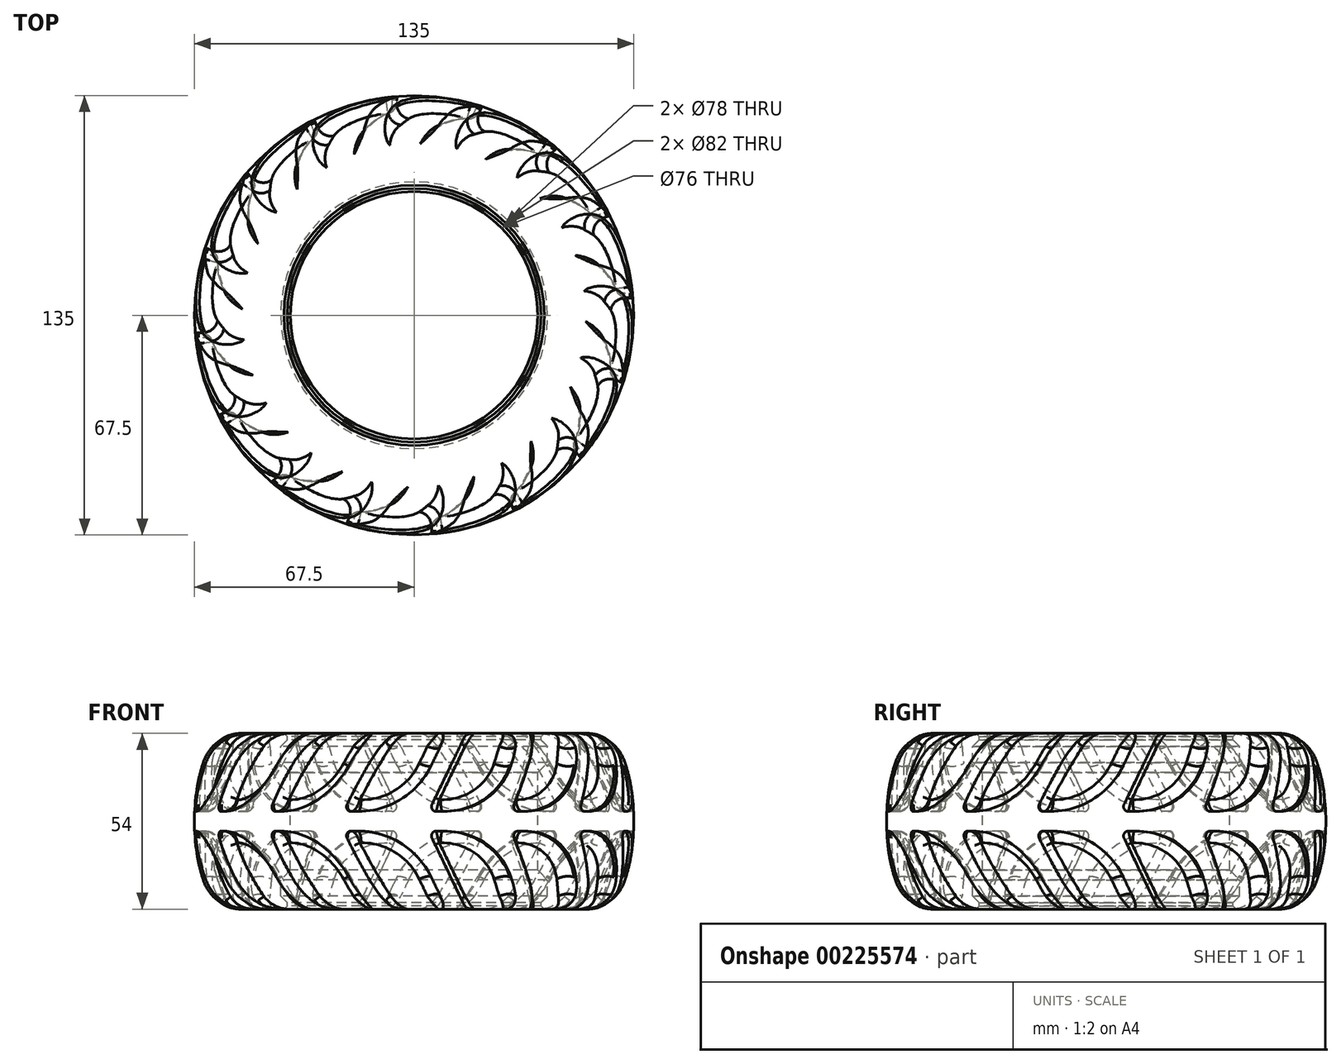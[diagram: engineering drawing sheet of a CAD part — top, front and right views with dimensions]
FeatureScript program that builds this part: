
annotation { "Feature Type Name" : "Feature", "Feature Type Description" : "" }
export const myFeature = defineFeature(function(context is Context, id is Id, definition is map)
    precondition{}
    {
        {
            var Q0;
            Q0=qCreatedBy(makeId("Front.planeOp"),FACE);
            var sketch = newSketch(context, id + "F0", { "sketchPlane" : qUnion([Q0])});
            skLineSegment(sketch, "E0", {"start": v(-39, 25) * mm, "end": v(-39, 27) * mm});
            skLineSegment(sketch, "E1", {"start": v(-39, 25) * mm, "end": v(-41, 23) * mm});
            skLineSegment(sketch, "E2", {"start": v(-41, 23) * mm, "end": v(-41, 18) * mm});
            skLineSegment(sketch, "E3", {"start": v(-41, 18) * mm, "end": v(-38, 15) * mm});
            skLineSegment(sketch, "E4", {"start": v(-38, -15) * mm, "end": v(-41, -18) * mm});
            skLineSegment(sketch, "E5", {"start": v(-41, -18) * mm, "end": v(-41, -23) * mm});
            skLineSegment(sketch, "E6", {"start": v(-41, -23) * mm, "end": v(-39, -25) * mm});
            skLineSegment(sketch, "E7", {"start": v(-39, -25) * mm, "end": v(-39, -27) * mm});
            skLineSegment(sketch, "E8", {"start": v(-38, 15) * mm, "end": v(-38, -15) * mm});
            skLineSegment(sketch, "E9", {"start": v(-38, 0) * mm, "end": v(-62.9, 0) * mm, "construction": true});
            skCircle(sketch, "E10", {"center": v(-52.82, 20.75) * mm, "radius": 6.25 * mm});
            skCircle(sketch, "E11", {"center": v(0, 0) * mm, "radius": 69 * mm});
            skCircle(sketch, "E12", {"center": v(-52.82, -20.75) * mm, "radius": 6.25 * mm});
            skCircle(sketch, "E13", {"center": v(0, 0) * mm, "radius": 63 * mm});
            skLineSegment(sketch, "E14", {"start": v(-39, 27) * mm, "end": v(-52.82, 27) * mm});
            skLineSegment(sketch, "E15", {"start": v(-39, -27) * mm, "end": v(-52.82, -27) * mm});
            skLineSegment(sketch, "E16", {"start": v(0, 89.19) * mm, "end": v(0, -93.9) * mm, "construction": true});
            skCircle(sketch, "E17", {"center": v(-52.82, 20.75) * mm, "radius": 12.25 * mm});
            skSolve(sketch);
        }
        {
            var Q0;
            Q0=makeQuery(id+"F0.imprint","IMPRINT",FACE,{"disambiguationData":[TD([[makeQuery(id+"F0.imprint","IMPRINT",EDGE,{"derivedFrom":sQuery(id+"F0.wireOp",EDGE,"E0")}),1.0]])]});
            var Q1;
            {var subQ0=sQuery(id+"F0.wireOp",EDGE,"E10");var subQ1=makeQuery(id+"F0.imprint","INTERSECT",VERTEX,{"derivedFrom":[subQ0,sQuery(id+"F0.wireOp",EDGE,"E14")]});Q1=makeQuery(id+"F0.imprint","IMPRINT",FACE,{"disambiguationData":[TD([[makeQuery(id+"F0.imprint","IMPRINT",EDGE,{"disambiguationData":[TD([[subQ1,-1.0]])],"derivedFrom":subQ0}),1.0]])]});}
            var Q2;
            {var subQ0=sQuery(id+"F0.wireOp",EDGE,"E12");var subQ1=makeQuery(id+"F0.imprint","INTERSECT",VERTEX,{"derivedFrom":[subQ0,sQuery(id+"F0.wireOp",EDGE,"E15")]});Q2=makeQuery(id+"F0.imprint","IMPRINT",FACE,{"disambiguationData":[TD([[makeQuery(id+"F0.imprint","IMPRINT",EDGE,{"disambiguationData":[TD([[subQ1,1.0]])],"derivedFrom":subQ0}),1.0]])]});}
            var Q3;
            {var subQ6=sQuery(id+"F0.wireOp",EDGE,"E2");Q3=makeQuery(id+"F0.imprint","IMPRINT",FACE,{"disambiguationData":[TD([[makeQuery(id+"F0.imprint","IMPRINT",EDGE,{"derivedFrom":subQ6}),-1.0]])]});}
            var Q4;
            Q4=makeQuery(id+"F0.imprint","IMPRINT",FACE,{"disambiguationData":[TD([[makeQuery(id+"F0.imprint","IMPRINT",EDGE,{"derivedFrom":sQuery(id+"F0.wireOp",EDGE,"E4")}),-1.0]])]});
            var Q5;
            Q5=sQuery(id+"F0.wireOp",EDGE,"E16");
            revolve(context, id + "F1", {"entities" : qUnion([Q0, Q1, Q2, Q3, Q4]), "axis" : qUnion([Q5]), "revolveType" : RevolveType.FULL});
        }
        {
            var Q0;
            Q0=qCreatedBy(makeId("Top.planeOp"),FACE);
            cPlane(context, id + "F2", {"entities" : qUnion([Q0]), "cplaneType" : CPlaneType.OFFSET, "offset" : 27 * mm, "width" : 150 * mm, "height" : 150 * mm});
        }
        {
            var Q0;
            Q0=qCreatedBy(makeId("Top.planeOp"),FACE);
            var sketch = newSketch(context, id + "F3", { "sketchPlane" : qUnion([Q0])});
            skLineSegment(sketch, "E18.bottom", {"start": v(-3, 60) * mm, "end": v(3, 60) * mm});
            skLineSegment(sketch, "E18.top", {"start": v(-3, 70) * mm, "end": v(3, 70) * mm});
            skLineSegment(sketch, "E18.left", {"start": v(-3, 60) * mm, "end": v(-3, 70) * mm});
            skLineSegment(sketch, "E18.right", {"start": v(3, 60) * mm, "end": v(3, 70) * mm});
            skLineSegment(sketch, "E19", {"start": v(0, 113.7) * mm, "end": v(0, -99.56) * mm, "construction": true});
            skLineSegment(sketch, "E20.1.0", {"start": v(-25.73, 54.28) * mm, "end": v(-29.56, 63.52) * mm});
            skLineSegment(sketch, "E20.1.1", {"start": v(-29.56, 63.52) * mm, "end": v(-24.02, 65.82) * mm});
            skLineSegment(sketch, "E20.1.2", {"start": v(-20.19, 56.58) * mm, "end": v(-24.02, 65.82) * mm});
            skLineSegment(sketch, "E20.1.3", {"start": v(-25.73, 54.28) * mm, "end": v(-20.19, 56.58) * mm});
            skLineSegment(sketch, "E20.2.0", {"start": v(-44.55, 40.3) * mm, "end": v(-51.62, 47.38) * mm});
            skLineSegment(sketch, "E20.2.1", {"start": v(-51.62, 47.38) * mm, "end": v(-47.38, 51.62) * mm});
            skLineSegment(sketch, "E20.2.2", {"start": v(-40.3, 44.55) * mm, "end": v(-47.38, 51.62) * mm});
            skLineSegment(sketch, "E20.2.3", {"start": v(-44.55, 40.3) * mm, "end": v(-40.3, 44.55) * mm});
            skLineSegment(sketch, "E20.3.0", {"start": v(-56.58, 20.19) * mm, "end": v(-65.82, 24.02) * mm});
            skLineSegment(sketch, "E20.3.1", {"start": v(-65.82, 24.02) * mm, "end": v(-63.52, 29.56) * mm});
            skLineSegment(sketch, "E20.3.2", {"start": v(-54.28, 25.73) * mm, "end": v(-63.52, 29.56) * mm});
            skLineSegment(sketch, "E20.3.3", {"start": v(-56.58, 20.19) * mm, "end": v(-54.28, 25.73) * mm});
            skLineSegment(sketch, "E20.4.0", {"start": v(-60, -3) * mm, "end": v(-70, -3) * mm});
            skLineSegment(sketch, "E20.4.1", {"start": v(-70, -3) * mm, "end": v(-70, 3) * mm});
            skLineSegment(sketch, "E20.4.2", {"start": v(-60, 3) * mm, "end": v(-70, 3) * mm});
            skLineSegment(sketch, "E20.4.3", {"start": v(-60, -3) * mm, "end": v(-60, 3) * mm});
            skLineSegment(sketch, "E20.5.0", {"start": v(-54.28, -25.73) * mm, "end": v(-63.52, -29.56) * mm});
            skLineSegment(sketch, "E20.5.1", {"start": v(-63.52, -29.56) * mm, "end": v(-65.82, -24.02) * mm});
            skLineSegment(sketch, "E20.5.2", {"start": v(-56.58, -20.19) * mm, "end": v(-65.82, -24.02) * mm});
            skLineSegment(sketch, "E20.5.3", {"start": v(-54.28, -25.73) * mm, "end": v(-56.58, -20.19) * mm});
            skLineSegment(sketch, "E20.6.0", {"start": v(-40.3, -44.55) * mm, "end": v(-47.38, -51.62) * mm});
            skLineSegment(sketch, "E20.6.1", {"start": v(-47.38, -51.62) * mm, "end": v(-51.62, -47.38) * mm});
            skLineSegment(sketch, "E20.6.2", {"start": v(-44.55, -40.3) * mm, "end": v(-51.62, -47.38) * mm});
            skLineSegment(sketch, "E20.6.3", {"start": v(-40.3, -44.55) * mm, "end": v(-44.55, -40.3) * mm});
            skLineSegment(sketch, "E20.7.0", {"start": v(-20.19, -56.58) * mm, "end": v(-24.02, -65.82) * mm});
            skLineSegment(sketch, "E20.7.1", {"start": v(-24.02, -65.82) * mm, "end": v(-29.56, -63.52) * mm});
            skLineSegment(sketch, "E20.7.2", {"start": v(-25.73, -54.28) * mm, "end": v(-29.56, -63.52) * mm});
            skLineSegment(sketch, "E20.7.3", {"start": v(-20.19, -56.58) * mm, "end": v(-25.73, -54.28) * mm});
            skLineSegment(sketch, "E20.8.0", {"start": v(3, -60) * mm, "end": v(3, -70) * mm});
            skLineSegment(sketch, "E20.8.1", {"start": v(3, -70) * mm, "end": v(-3, -70) * mm});
            skLineSegment(sketch, "E20.8.2", {"start": v(-3, -60) * mm, "end": v(-3, -70) * mm});
            skLineSegment(sketch, "E20.8.3", {"start": v(3, -60) * mm, "end": v(-3, -60) * mm});
            skLineSegment(sketch, "E20.9.0", {"start": v(25.73, -54.28) * mm, "end": v(29.56, -63.52) * mm});
            skLineSegment(sketch, "E20.9.1", {"start": v(29.56, -63.52) * mm, "end": v(24.02, -65.82) * mm});
            skLineSegment(sketch, "E20.9.2", {"start": v(20.19, -56.58) * mm, "end": v(24.02, -65.82) * mm});
            skLineSegment(sketch, "E20.9.3", {"start": v(25.73, -54.28) * mm, "end": v(20.19, -56.58) * mm});
            skLineSegment(sketch, "E20.10.0", {"start": v(44.55, -40.3) * mm, "end": v(51.62, -47.38) * mm});
            skLineSegment(sketch, "E20.10.1", {"start": v(51.62, -47.38) * mm, "end": v(47.38, -51.62) * mm});
            skLineSegment(sketch, "E20.10.2", {"start": v(40.3, -44.55) * mm, "end": v(47.38, -51.62) * mm});
            skLineSegment(sketch, "E20.10.3", {"start": v(44.55, -40.3) * mm, "end": v(40.3, -44.55) * mm});
            skLineSegment(sketch, "E20.11.0", {"start": v(56.58, -20.19) * mm, "end": v(65.82, -24.02) * mm});
            skLineSegment(sketch, "E20.11.1", {"start": v(65.82, -24.02) * mm, "end": v(63.52, -29.56) * mm});
            skLineSegment(sketch, "E20.11.2", {"start": v(54.28, -25.73) * mm, "end": v(63.52, -29.56) * mm});
            skLineSegment(sketch, "E20.11.3", {"start": v(56.58, -20.19) * mm, "end": v(54.28, -25.73) * mm});
            skLineSegment(sketch, "E20.12.0", {"start": v(60, 3) * mm, "end": v(70, 3) * mm});
            skLineSegment(sketch, "E20.12.1", {"start": v(70, 3) * mm, "end": v(70, -3) * mm});
            skLineSegment(sketch, "E20.12.2", {"start": v(60, -3) * mm, "end": v(70, -3) * mm});
            skLineSegment(sketch, "E20.12.3", {"start": v(60, 3) * mm, "end": v(60, -3) * mm});
            skLineSegment(sketch, "E20.13.0", {"start": v(54.28, 25.73) * mm, "end": v(63.52, 29.56) * mm});
            skLineSegment(sketch, "E20.13.1", {"start": v(63.52, 29.56) * mm, "end": v(65.82, 24.02) * mm});
            skLineSegment(sketch, "E20.13.2", {"start": v(56.58, 20.19) * mm, "end": v(65.82, 24.02) * mm});
            skLineSegment(sketch, "E20.13.3", {"start": v(54.28, 25.73) * mm, "end": v(56.58, 20.19) * mm});
            skLineSegment(sketch, "E20.14.0", {"start": v(40.3, 44.55) * mm, "end": v(47.38, 51.62) * mm});
            skLineSegment(sketch, "E20.14.1", {"start": v(47.38, 51.62) * mm, "end": v(51.62, 47.38) * mm});
            skLineSegment(sketch, "E20.14.2", {"start": v(44.55, 40.3) * mm, "end": v(51.62, 47.38) * mm});
            skLineSegment(sketch, "E20.14.3", {"start": v(40.3, 44.55) * mm, "end": v(44.55, 40.3) * mm});
            skLineSegment(sketch, "E20.15.0", {"start": v(20.19, 56.58) * mm, "end": v(24.02, 65.82) * mm});
            skLineSegment(sketch, "E20.15.1", {"start": v(24.02, 65.82) * mm, "end": v(29.56, 63.52) * mm});
            skLineSegment(sketch, "E20.15.2", {"start": v(25.73, 54.28) * mm, "end": v(29.56, 63.52) * mm});
            skLineSegment(sketch, "E20.15.3", {"start": v(20.19, 56.58) * mm, "end": v(25.73, 54.28) * mm});
            skPoint(sketch, "E20.center", {"position": v(0, 0) * mm});
            skSolve(sketch);
        }
        {
            var Q0;
            Q0=qCreatedBy(id+"F2.planeOp",FACE);
            var sketch = newSketch(context, id + "F4", { "sketchPlane" : qUnion([Q0])});
            skLineSegment(sketch, "E21", {"start": v(-16, 70) * mm, "end": v(-16, 50) * mm});
            skLineSegment(sketch, "E22", {"start": v(-16, 50) * mm, "end": v(-10, 50) * mm});
            skLineSegment(sketch, "E23", {"start": v(-16, 70) * mm, "end": v(-10, 70) * mm});
            skLineSegment(sketch, "E24", {"start": v(-10, 70) * mm, "end": v(-10, 50) * mm});
            skLineSegment(sketch, "E25", {"start": v(0, 99.7) * mm, "end": v(0, -107.8) * mm, "construction": true});
            skLineSegment(sketch, "E26.1.0", {"start": v(-41.57, 58.55) * mm, "end": v(-33.92, 40.07) * mm});
            skLineSegment(sketch, "E26.1.1", {"start": v(-36.03, 60.84) * mm, "end": v(-28.37, 42.37) * mm});
            skLineSegment(sketch, "E26.1.2", {"start": v(-33.92, 40.07) * mm, "end": v(-28.37, 42.37) * mm});
            skLineSegment(sketch, "E26.1.3", {"start": v(-41.57, 58.55) * mm, "end": v(-36.03, 60.84) * mm});
            skLineSegment(sketch, "E26.2.0", {"start": v(-60.81, 38.18) * mm, "end": v(-46.67, 24.04) * mm});
            skLineSegment(sketch, "E26.2.1", {"start": v(-56.57, 42.43) * mm, "end": v(-42.43, 28.28) * mm});
            skLineSegment(sketch, "E26.2.2", {"start": v(-46.67, 24.04) * mm, "end": v(-42.43, 28.28) * mm});
            skLineSegment(sketch, "E26.2.3", {"start": v(-60.81, 38.18) * mm, "end": v(-56.57, 42.43) * mm});
            skLineSegment(sketch, "E26.3.0", {"start": v(-70.8, 12) * mm, "end": v(-52.32, 4.35) * mm});
            skLineSegment(sketch, "E26.3.1", {"start": v(-68.5, 17.55) * mm, "end": v(-50.02, 9.9) * mm});
            skLineSegment(sketch, "E26.3.2", {"start": v(-52.32, 4.35) * mm, "end": v(-50.02, 9.9) * mm});
            skLineSegment(sketch, "E26.3.3", {"start": v(-70.8, 12) * mm, "end": v(-68.5, 17.55) * mm});
            skLineSegment(sketch, "E26.4.0", {"start": v(-70, -16) * mm, "end": v(-50, -16) * mm});
            skLineSegment(sketch, "E26.4.1", {"start": v(-70, -10) * mm, "end": v(-50, -10) * mm});
            skLineSegment(sketch, "E26.4.2", {"start": v(-50, -16) * mm, "end": v(-50, -10) * mm});
            skLineSegment(sketch, "E26.4.3", {"start": v(-70, -16) * mm, "end": v(-70, -10) * mm});
            skLineSegment(sketch, "E26.5.0", {"start": v(-58.55, -41.57) * mm, "end": v(-40.07, -33.92) * mm});
            skLineSegment(sketch, "E26.5.1", {"start": v(-60.84, -36.03) * mm, "end": v(-42.37, -28.37) * mm});
            skLineSegment(sketch, "E26.5.2", {"start": v(-40.07, -33.92) * mm, "end": v(-42.37, -28.37) * mm});
            skLineSegment(sketch, "E26.5.3", {"start": v(-58.55, -41.57) * mm, "end": v(-60.84, -36.03) * mm});
            skLineSegment(sketch, "E26.6.0", {"start": v(-38.18, -60.81) * mm, "end": v(-24.04, -46.67) * mm});
            skLineSegment(sketch, "E26.6.1", {"start": v(-42.43, -56.57) * mm, "end": v(-28.28, -42.43) * mm});
            skLineSegment(sketch, "E26.6.2", {"start": v(-24.04, -46.67) * mm, "end": v(-28.28, -42.43) * mm});
            skLineSegment(sketch, "E26.6.3", {"start": v(-38.18, -60.81) * mm, "end": v(-42.43, -56.57) * mm});
            skLineSegment(sketch, "E26.7.0", {"start": v(-12, -70.8) * mm, "end": v(-4.35, -52.32) * mm});
            skLineSegment(sketch, "E26.7.1", {"start": v(-17.55, -68.5) * mm, "end": v(-9.9, -50.02) * mm});
            skLineSegment(sketch, "E26.7.2", {"start": v(-4.35, -52.32) * mm, "end": v(-9.9, -50.02) * mm});
            skLineSegment(sketch, "E26.7.3", {"start": v(-12, -70.8) * mm, "end": v(-17.55, -68.5) * mm});
            skLineSegment(sketch, "E26.8.0", {"start": v(16, -70) * mm, "end": v(16, -50) * mm});
            skLineSegment(sketch, "E26.8.1", {"start": v(10, -70) * mm, "end": v(10, -50) * mm});
            skLineSegment(sketch, "E26.8.2", {"start": v(16, -50) * mm, "end": v(10, -50) * mm});
            skLineSegment(sketch, "E26.8.3", {"start": v(16, -70) * mm, "end": v(10, -70) * mm});
            skLineSegment(sketch, "E26.9.0", {"start": v(41.57, -58.55) * mm, "end": v(33.92, -40.07) * mm});
            skLineSegment(sketch, "E26.9.1", {"start": v(36.03, -60.84) * mm, "end": v(28.37, -42.37) * mm});
            skLineSegment(sketch, "E26.9.2", {"start": v(33.92, -40.07) * mm, "end": v(28.37, -42.37) * mm});
            skLineSegment(sketch, "E26.9.3", {"start": v(41.57, -58.55) * mm, "end": v(36.03, -60.84) * mm});
            skLineSegment(sketch, "E26.10.0", {"start": v(60.81, -38.18) * mm, "end": v(46.67, -24.04) * mm});
            skLineSegment(sketch, "E26.10.1", {"start": v(56.57, -42.43) * mm, "end": v(42.43, -28.28) * mm});
            skLineSegment(sketch, "E26.10.2", {"start": v(46.67, -24.04) * mm, "end": v(42.43, -28.28) * mm});
            skLineSegment(sketch, "E26.10.3", {"start": v(60.81, -38.18) * mm, "end": v(56.57, -42.43) * mm});
            skLineSegment(sketch, "E26.11.0", {"start": v(70.8, -12) * mm, "end": v(52.32, -4.35) * mm});
            skLineSegment(sketch, "E26.11.1", {"start": v(68.5, -17.55) * mm, "end": v(50.02, -9.9) * mm});
            skLineSegment(sketch, "E26.11.2", {"start": v(52.32, -4.35) * mm, "end": v(50.02, -9.9) * mm});
            skLineSegment(sketch, "E26.11.3", {"start": v(70.8, -12) * mm, "end": v(68.5, -17.55) * mm});
            skLineSegment(sketch, "E26.12.0", {"start": v(70, 16) * mm, "end": v(50, 16) * mm});
            skLineSegment(sketch, "E26.12.1", {"start": v(70, 10) * mm, "end": v(50, 10) * mm});
            skLineSegment(sketch, "E26.12.2", {"start": v(50, 16) * mm, "end": v(50, 10) * mm});
            skLineSegment(sketch, "E26.12.3", {"start": v(70, 16) * mm, "end": v(70, 10) * mm});
            skLineSegment(sketch, "E26.13.0", {"start": v(58.55, 41.57) * mm, "end": v(40.07, 33.92) * mm});
            skLineSegment(sketch, "E26.13.1", {"start": v(60.84, 36.03) * mm, "end": v(42.37, 28.37) * mm});
            skLineSegment(sketch, "E26.13.2", {"start": v(40.07, 33.92) * mm, "end": v(42.37, 28.37) * mm});
            skLineSegment(sketch, "E26.13.3", {"start": v(58.55, 41.57) * mm, "end": v(60.84, 36.03) * mm});
            skLineSegment(sketch, "E26.14.0", {"start": v(38.18, 60.81) * mm, "end": v(24.04, 46.67) * mm});
            skLineSegment(sketch, "E26.14.1", {"start": v(42.43, 56.57) * mm, "end": v(28.28, 42.43) * mm});
            skLineSegment(sketch, "E26.14.2", {"start": v(24.04, 46.67) * mm, "end": v(28.28, 42.43) * mm});
            skLineSegment(sketch, "E26.14.3", {"start": v(38.18, 60.81) * mm, "end": v(42.43, 56.57) * mm});
            skLineSegment(sketch, "E26.15.0", {"start": v(12, 70.8) * mm, "end": v(4.35, 52.32) * mm});
            skLineSegment(sketch, "E26.15.1", {"start": v(17.55, 68.5) * mm, "end": v(9.9, 50.02) * mm});
            skLineSegment(sketch, "E26.15.2", {"start": v(4.35, 52.32) * mm, "end": v(9.9, 50.02) * mm});
            skLineSegment(sketch, "E26.15.3", {"start": v(12, 70.8) * mm, "end": v(17.55, 68.5) * mm});
            skPoint(sketch, "E26.center", {"position": v(0, 0) * mm});
            skSolve(sketch);
        }
        {
            var Q1;
            Q1=makeQuery(id+"F3.imprint","IMPRINT",FACE,{"disambiguationData":[TD([[makeQuery(id+"F3.imprint","IMPRINT",EDGE,{"derivedFrom":sQuery(id+"F3.wireOp",EDGE,"E18.bottom")}),1.0]])]});
            var Q2;
            Q2=makeQuery(id+"F4.imprint","IMPRINT",FACE,{"disambiguationData":[TD([[makeQuery(id+"F4.imprint","IMPRINT",EDGE,{"derivedFrom":sQuery(id+"F4.wireOp",EDGE,"E21")}),1.0]])]});
            loft(context, id + "F5", {"operationType" : NewBodyOperationType.ADD, "sheetProfilesArray" : [{ "sheetProfileEntities" : qUnion([Q1]) }, { "sheetProfileEntities" : qUnion([Q2]) }]});
        }
        {
            var Q1;
            Q1=makeQuery(id+"F3.imprint","IMPRINT",FACE,{"disambiguationData":[TD([[makeQuery(id+"F3.imprint","IMPRINT",EDGE,{"derivedFrom":sQuery(id+"F3.wireOp",EDGE,"E20.15.0")}),-1.0]])]});
            var Q2;
            Q2=makeQuery(id+"F4.imprint","IMPRINT",FACE,{"disambiguationData":[TD([[makeQuery(id+"F4.imprint","IMPRINT",EDGE,{"derivedFrom":sQuery(id+"F4.wireOp",EDGE,"E26.15.0")}),1.0]])]});
            loft(context, id + "F6", {"operationType" : NewBodyOperationType.ADD, "sheetProfilesArray" : [{ "sheetProfileEntities" : qUnion([Q1]) }, { "sheetProfileEntities" : qUnion([Q2]) }]});
        }
        {
            var Q1;
            Q1=makeQuery(id+"F3.imprint","IMPRINT",FACE,{"disambiguationData":[TD([[makeQuery(id+"F3.imprint","IMPRINT",EDGE,{"derivedFrom":sQuery(id+"F3.wireOp",EDGE,"E20.14.0")}),-1.0]])]});
            var Q2;
            Q2=makeQuery(id+"F4.imprint","IMPRINT",FACE,{"disambiguationData":[TD([[makeQuery(id+"F4.imprint","IMPRINT",EDGE,{"derivedFrom":sQuery(id+"F4.wireOp",EDGE,"E26.14.0")}),1.0]])]});
            loft(context, id + "F7", {"operationType" : NewBodyOperationType.ADD, "sheetProfilesArray" : [{ "sheetProfileEntities" : qUnion([Q1]) }, { "sheetProfileEntities" : qUnion([Q2]) }]});
        }
        {
            var Q1;
            Q1=makeQuery(id+"F3.imprint","IMPRINT",FACE,{"disambiguationData":[TD([[makeQuery(id+"F3.imprint","IMPRINT",EDGE,{"derivedFrom":sQuery(id+"F3.wireOp",EDGE,"E20.13.0")}),-1.0]])]});
            var Q2;
            Q2=makeQuery(id+"F4.imprint","IMPRINT",FACE,{"disambiguationData":[TD([[makeQuery(id+"F4.imprint","IMPRINT",EDGE,{"derivedFrom":sQuery(id+"F4.wireOp",EDGE,"E26.13.0")}),1.0]])]});
            loft(context, id + "F8", {"operationType" : NewBodyOperationType.ADD, "sheetProfilesArray" : [{ "sheetProfileEntities" : qUnion([Q1]) }, { "sheetProfileEntities" : qUnion([Q2]) }]});
        }
        {
            var Q1;
            Q1=makeQuery(id+"F3.imprint","IMPRINT",FACE,{"disambiguationData":[TD([[makeQuery(id+"F3.imprint","IMPRINT",EDGE,{"derivedFrom":sQuery(id+"F3.wireOp",EDGE,"E20.12.0")}),-1.0]])]});
            var Q2;
            Q2=makeQuery(id+"F4.imprint","IMPRINT",FACE,{"disambiguationData":[TD([[makeQuery(id+"F4.imprint","IMPRINT",EDGE,{"derivedFrom":sQuery(id+"F4.wireOp",EDGE,"E26.12.0")}),1.0]])]});
            loft(context, id + "F9", {"operationType" : NewBodyOperationType.ADD, "sheetProfilesArray" : [{ "sheetProfileEntities" : qUnion([Q1]) }, { "sheetProfileEntities" : qUnion([Q2]) }]});
        }
        {
            var Q1;
            Q1=makeQuery(id+"F3.imprint","IMPRINT",FACE,{"disambiguationData":[TD([[makeQuery(id+"F3.imprint","IMPRINT",EDGE,{"derivedFrom":sQuery(id+"F3.wireOp",EDGE,"E20.11.0")}),-1.0]])]});
            var Q2;
            Q2=makeQuery(id+"F4.imprint","IMPRINT",FACE,{"disambiguationData":[TD([[makeQuery(id+"F4.imprint","IMPRINT",EDGE,{"derivedFrom":sQuery(id+"F4.wireOp",EDGE,"E26.11.0")}),1.0]])]});
            loft(context, id + "F10", {"operationType" : NewBodyOperationType.ADD, "sheetProfilesArray" : [{ "sheetProfileEntities" : qUnion([Q1]) }, { "sheetProfileEntities" : qUnion([Q2]) }]});
        }
        {
            var Q1;
            Q1=makeQuery(id+"F3.imprint","IMPRINT",FACE,{"disambiguationData":[TD([[makeQuery(id+"F3.imprint","IMPRINT",EDGE,{"derivedFrom":sQuery(id+"F3.wireOp",EDGE,"E20.10.0")}),-1.0]])]});
            var Q2;
            Q2=makeQuery(id+"F4.imprint","IMPRINT",FACE,{"disambiguationData":[TD([[makeQuery(id+"F4.imprint","IMPRINT",EDGE,{"derivedFrom":sQuery(id+"F4.wireOp",EDGE,"E26.10.0")}),1.0]])]});
            loft(context, id + "F11", {"operationType" : NewBodyOperationType.ADD, "sheetProfilesArray" : [{ "sheetProfileEntities" : qUnion([Q1]) }, { "sheetProfileEntities" : qUnion([Q2]) }]});
        }
        {
            var Q1;
            Q1=makeQuery(id+"F3.imprint","IMPRINT",FACE,{"disambiguationData":[TD([[makeQuery(id+"F3.imprint","IMPRINT",EDGE,{"derivedFrom":sQuery(id+"F3.wireOp",EDGE,"E20.9.0")}),-1.0]])]});
            var Q2;
            Q2=makeQuery(id+"F4.imprint","IMPRINT",FACE,{"disambiguationData":[TD([[makeQuery(id+"F4.imprint","IMPRINT",EDGE,{"derivedFrom":sQuery(id+"F4.wireOp",EDGE,"E26.9.0")}),1.0]])]});
            loft(context, id + "F12", {"operationType" : NewBodyOperationType.ADD, "sheetProfilesArray" : [{ "sheetProfileEntities" : qUnion([Q1]) }, { "sheetProfileEntities" : qUnion([Q2]) }]});
        }
        {
            var Q1;
            Q1=makeQuery(id+"F3.imprint","IMPRINT",FACE,{"disambiguationData":[TD([[makeQuery(id+"F3.imprint","IMPRINT",EDGE,{"derivedFrom":sQuery(id+"F3.wireOp",EDGE,"E20.8.0")}),-1.0]])]});
            var Q2;
            Q2=makeQuery(id+"F4.imprint","IMPRINT",FACE,{"disambiguationData":[TD([[makeQuery(id+"F4.imprint","IMPRINT",EDGE,{"derivedFrom":sQuery(id+"F4.wireOp",EDGE,"E26.8.0")}),1.0]])]});
            loft(context, id + "F13", {"operationType" : NewBodyOperationType.ADD, "sheetProfilesArray" : [{ "sheetProfileEntities" : qUnion([Q1]) }, { "sheetProfileEntities" : qUnion([Q2]) }]});
        }
        {
            var Q1;
            Q1=makeQuery(id+"F3.imprint","IMPRINT",FACE,{"disambiguationData":[TD([[makeQuery(id+"F3.imprint","IMPRINT",EDGE,{"derivedFrom":sQuery(id+"F3.wireOp",EDGE,"E20.7.0")}),-1.0]])]});
            var Q2;
            Q2=makeQuery(id+"F4.imprint","IMPRINT",FACE,{"disambiguationData":[TD([[makeQuery(id+"F4.imprint","IMPRINT",EDGE,{"derivedFrom":sQuery(id+"F4.wireOp",EDGE,"E26.7.0")}),1.0]])]});
            loft(context, id + "F14", {"operationType" : NewBodyOperationType.ADD, "sheetProfilesArray" : [{ "sheetProfileEntities" : qUnion([Q1]) }, { "sheetProfileEntities" : qUnion([Q2]) }]});
        }
        {
            var Q1;
            Q1=makeQuery(id+"F3.imprint","IMPRINT",FACE,{"disambiguationData":[TD([[makeQuery(id+"F3.imprint","IMPRINT",EDGE,{"derivedFrom":sQuery(id+"F3.wireOp",EDGE,"E20.6.0")}),-1.0]])]});
            var Q2;
            Q2=makeQuery(id+"F4.imprint","IMPRINT",FACE,{"disambiguationData":[TD([[makeQuery(id+"F4.imprint","IMPRINT",EDGE,{"derivedFrom":sQuery(id+"F4.wireOp",EDGE,"E26.6.0")}),1.0]])]});
            loft(context, id + "F15", {"operationType" : NewBodyOperationType.ADD, "sheetProfilesArray" : [{ "sheetProfileEntities" : qUnion([Q1]) }, { "sheetProfileEntities" : qUnion([Q2]) }]});
        }
        {
            var Q1;
            Q1=makeQuery(id+"F3.imprint","IMPRINT",FACE,{"disambiguationData":[TD([[makeQuery(id+"F3.imprint","IMPRINT",EDGE,{"derivedFrom":sQuery(id+"F3.wireOp",EDGE,"E20.5.0")}),-1.0]])]});
            var Q2;
            Q2=makeQuery(id+"F4.imprint","IMPRINT",FACE,{"disambiguationData":[TD([[makeQuery(id+"F4.imprint","IMPRINT",EDGE,{"derivedFrom":sQuery(id+"F4.wireOp",EDGE,"E26.5.0")}),1.0]])]});
            loft(context, id + "F16", {"operationType" : NewBodyOperationType.ADD, "sheetProfilesArray" : [{ "sheetProfileEntities" : qUnion([Q1]) }, { "sheetProfileEntities" : qUnion([Q2]) }]});
        }
        {
            var Q1;
            Q1=makeQuery(id+"F4.imprint","IMPRINT",FACE,{"disambiguationData":[TD([[makeQuery(id+"F4.imprint","IMPRINT",EDGE,{"derivedFrom":sQuery(id+"F4.wireOp",EDGE,"E26.4.0")}),1.0]])]});
            var Q2;
            Q2=makeQuery(id+"F3.imprint","IMPRINT",FACE,{"disambiguationData":[TD([[makeQuery(id+"F3.imprint","IMPRINT",EDGE,{"derivedFrom":sQuery(id+"F3.wireOp",EDGE,"E20.4.0")}),-1.0]])]});
            loft(context, id + "F17", {"operationType" : NewBodyOperationType.ADD, "sheetProfilesArray" : [{ "sheetProfileEntities" : qUnion([Q1]) }, { "sheetProfileEntities" : qUnion([Q2]) }]});
        }
        {
            var Q1;
            Q1=makeQuery(id+"F3.imprint","IMPRINT",FACE,{"disambiguationData":[TD([[makeQuery(id+"F3.imprint","IMPRINT",EDGE,{"derivedFrom":sQuery(id+"F3.wireOp",EDGE,"E20.3.0")}),-1.0]])]});
            var Q2;
            Q2=makeQuery(id+"F4.imprint","IMPRINT",FACE,{"disambiguationData":[TD([[makeQuery(id+"F4.imprint","IMPRINT",EDGE,{"derivedFrom":sQuery(id+"F4.wireOp",EDGE,"E26.3.0")}),1.0]])]});
            loft(context, id + "F18", {"operationType" : NewBodyOperationType.ADD, "sheetProfilesArray" : [{ "sheetProfileEntities" : qUnion([Q1]) }, { "sheetProfileEntities" : qUnion([Q2]) }]});
        }
        {
            var Q1;
            Q1=makeQuery(id+"F3.imprint","IMPRINT",FACE,{"disambiguationData":[TD([[makeQuery(id+"F3.imprint","IMPRINT",EDGE,{"derivedFrom":sQuery(id+"F3.wireOp",EDGE,"E20.2.0")}),-1.0]])]});
            var Q2;
            Q2=makeQuery(id+"F4.imprint","IMPRINT",FACE,{"disambiguationData":[TD([[makeQuery(id+"F4.imprint","IMPRINT",EDGE,{"derivedFrom":sQuery(id+"F4.wireOp",EDGE,"E26.2.0")}),1.0]])]});
            loft(context, id + "F19", {"operationType" : NewBodyOperationType.ADD, "sheetProfilesArray" : [{ "sheetProfileEntities" : qUnion([Q1]) }, { "sheetProfileEntities" : qUnion([Q2]) }]});
        }
        {
            var Q1;
            Q1=makeQuery(id+"F3.imprint","IMPRINT",FACE,{"disambiguationData":[TD([[makeQuery(id+"F3.imprint","IMPRINT",EDGE,{"derivedFrom":sQuery(id+"F3.wireOp",EDGE,"E20.1.0")}),-1.0]])]});
            var Q2;
            Q2=makeQuery(id+"F4.imprint","IMPRINT",FACE,{"disambiguationData":[TD([[makeQuery(id+"F4.imprint","IMPRINT",EDGE,{"derivedFrom":sQuery(id+"F4.wireOp",EDGE,"E26.1.0")}),1.0]])]});
            loft(context, id + "F20", {"operationType" : NewBodyOperationType.ADD, "sheetProfilesArray" : [{ "sheetProfileEntities" : qUnion([Q1]) }, { "sheetProfileEntities" : qUnion([Q2]) }]});
        }
        {
            var Q0;
            Q0=qCreatedBy(makeId("Top.planeOp"),FACE);
            cPlane(context, id + "F21", {"entities" : qUnion([Q0]), "cplaneType" : CPlaneType.OFFSET, "offset" : 27 * mm, "oppositeDirection" : true, "width" : 150 * mm, "height" : 150 * mm});
        }
        {
            var Q0;
            Q0=qCreatedBy(id+"F21.planeOp",FACE);
            var sketch = newSketch(context, id + "F22", { "sketchPlane" : qUnion([Q0])});
            skLineSegment(sketch, "E27.bottom", {"start": v(10, -70) * mm, "end": v(16, -70) * mm});
            skLineSegment(sketch, "E27.top", {"start": v(10, -50) * mm, "end": v(16, -50) * mm});
            skLineSegment(sketch, "E27.left", {"start": v(10, -70) * mm, "end": v(10, -50) * mm});
            skLineSegment(sketch, "E27.right", {"start": v(16, -70) * mm, "end": v(16, -50) * mm});
            skLineSegment(sketch, "E28.1.0", {"start": v(36.03, -60.84) * mm, "end": v(28.37, -42.37) * mm});
            skLineSegment(sketch, "E28.1.1", {"start": v(41.57, -58.55) * mm, "end": v(33.92, -40.07) * mm});
            skLineSegment(sketch, "E28.1.2", {"start": v(36.03, -60.84) * mm, "end": v(41.57, -58.55) * mm});
            skLineSegment(sketch, "E28.1.3", {"start": v(28.37, -42.37) * mm, "end": v(33.92, -40.07) * mm});
            skLineSegment(sketch, "E28.2.0", {"start": v(56.57, -42.43) * mm, "end": v(42.43, -28.28) * mm});
            skLineSegment(sketch, "E28.2.1", {"start": v(60.81, -38.18) * mm, "end": v(46.67, -24.04) * mm});
            skLineSegment(sketch, "E28.2.2", {"start": v(56.57, -42.43) * mm, "end": v(60.81, -38.18) * mm});
            skLineSegment(sketch, "E28.2.3", {"start": v(42.43, -28.28) * mm, "end": v(46.67, -24.04) * mm});
            skLineSegment(sketch, "E28.3.0", {"start": v(68.5, -17.55) * mm, "end": v(50.02, -9.9) * mm});
            skLineSegment(sketch, "E28.3.1", {"start": v(70.8, -12) * mm, "end": v(52.32, -4.35) * mm});
            skLineSegment(sketch, "E28.3.2", {"start": v(68.5, -17.55) * mm, "end": v(70.8, -12) * mm});
            skLineSegment(sketch, "E28.3.3", {"start": v(50.02, -9.9) * mm, "end": v(52.32, -4.35) * mm});
            skLineSegment(sketch, "E28.4.0", {"start": v(70, 10) * mm, "end": v(50, 10) * mm});
            skLineSegment(sketch, "E28.4.1", {"start": v(70, 16) * mm, "end": v(50, 16) * mm});
            skLineSegment(sketch, "E28.4.2", {"start": v(70, 10) * mm, "end": v(70, 16) * mm});
            skLineSegment(sketch, "E28.4.3", {"start": v(50, 10) * mm, "end": v(50, 16) * mm});
            skLineSegment(sketch, "E28.5.0", {"start": v(60.84, 36.03) * mm, "end": v(42.37, 28.37) * mm});
            skLineSegment(sketch, "E28.5.1", {"start": v(58.55, 41.57) * mm, "end": v(40.07, 33.92) * mm});
            skLineSegment(sketch, "E28.5.2", {"start": v(60.84, 36.03) * mm, "end": v(58.55, 41.57) * mm});
            skLineSegment(sketch, "E28.5.3", {"start": v(42.37, 28.37) * mm, "end": v(40.07, 33.92) * mm});
            skLineSegment(sketch, "E28.6.0", {"start": v(42.43, 56.57) * mm, "end": v(28.28, 42.43) * mm});
            skLineSegment(sketch, "E28.6.1", {"start": v(38.18, 60.81) * mm, "end": v(24.04, 46.67) * mm});
            skLineSegment(sketch, "E28.6.2", {"start": v(42.43, 56.57) * mm, "end": v(38.18, 60.81) * mm});
            skLineSegment(sketch, "E28.6.3", {"start": v(28.28, 42.43) * mm, "end": v(24.04, 46.67) * mm});
            skLineSegment(sketch, "E28.7.0", {"start": v(17.55, 68.5) * mm, "end": v(9.9, 50.02) * mm});
            skLineSegment(sketch, "E28.7.1", {"start": v(12, 70.8) * mm, "end": v(4.35, 52.32) * mm});
            skLineSegment(sketch, "E28.7.2", {"start": v(17.55, 68.5) * mm, "end": v(12, 70.8) * mm});
            skLineSegment(sketch, "E28.7.3", {"start": v(9.9, 50.02) * mm, "end": v(4.35, 52.32) * mm});
            skLineSegment(sketch, "E28.8.0", {"start": v(-10, 70) * mm, "end": v(-10, 50) * mm});
            skLineSegment(sketch, "E28.8.1", {"start": v(-16, 70) * mm, "end": v(-16, 50) * mm});
            skLineSegment(sketch, "E28.8.2", {"start": v(-10, 70) * mm, "end": v(-16, 70) * mm});
            skLineSegment(sketch, "E28.8.3", {"start": v(-10, 50) * mm, "end": v(-16, 50) * mm});
            skLineSegment(sketch, "E28.9.0", {"start": v(-36.03, 60.84) * mm, "end": v(-28.37, 42.37) * mm});
            skLineSegment(sketch, "E28.9.1", {"start": v(-41.57, 58.55) * mm, "end": v(-33.92, 40.07) * mm});
            skLineSegment(sketch, "E28.9.2", {"start": v(-36.03, 60.84) * mm, "end": v(-41.57, 58.55) * mm});
            skLineSegment(sketch, "E28.9.3", {"start": v(-28.37, 42.37) * mm, "end": v(-33.92, 40.07) * mm});
            skLineSegment(sketch, "E28.10.0", {"start": v(-56.57, 42.43) * mm, "end": v(-42.43, 28.28) * mm});
            skLineSegment(sketch, "E28.10.1", {"start": v(-60.81, 38.18) * mm, "end": v(-46.67, 24.04) * mm});
            skLineSegment(sketch, "E28.10.2", {"start": v(-56.57, 42.43) * mm, "end": v(-60.81, 38.18) * mm});
            skLineSegment(sketch, "E28.10.3", {"start": v(-42.43, 28.28) * mm, "end": v(-46.67, 24.04) * mm});
            skLineSegment(sketch, "E28.11.0", {"start": v(-68.5, 17.55) * mm, "end": v(-50.02, 9.9) * mm});
            skLineSegment(sketch, "E28.11.1", {"start": v(-70.8, 12) * mm, "end": v(-52.32, 4.35) * mm});
            skLineSegment(sketch, "E28.11.2", {"start": v(-68.5, 17.55) * mm, "end": v(-70.8, 12) * mm});
            skLineSegment(sketch, "E28.11.3", {"start": v(-50.02, 9.9) * mm, "end": v(-52.32, 4.35) * mm});
            skLineSegment(sketch, "E28.12.0", {"start": v(-70, -10) * mm, "end": v(-50, -10) * mm});
            skLineSegment(sketch, "E28.12.1", {"start": v(-70, -16) * mm, "end": v(-50, -16) * mm});
            skLineSegment(sketch, "E28.12.2", {"start": v(-70, -10) * mm, "end": v(-70, -16) * mm});
            skLineSegment(sketch, "E28.12.3", {"start": v(-50, -10) * mm, "end": v(-50, -16) * mm});
            skLineSegment(sketch, "E28.13.0", {"start": v(-60.84, -36.03) * mm, "end": v(-42.37, -28.37) * mm});
            skLineSegment(sketch, "E28.13.1", {"start": v(-58.55, -41.57) * mm, "end": v(-40.07, -33.92) * mm});
            skLineSegment(sketch, "E28.13.2", {"start": v(-60.84, -36.03) * mm, "end": v(-58.55, -41.57) * mm});
            skLineSegment(sketch, "E28.13.3", {"start": v(-42.37, -28.37) * mm, "end": v(-40.07, -33.92) * mm});
            skLineSegment(sketch, "E28.14.0", {"start": v(-42.43, -56.57) * mm, "end": v(-28.28, -42.43) * mm});
            skLineSegment(sketch, "E28.14.1", {"start": v(-38.18, -60.81) * mm, "end": v(-24.04, -46.67) * mm});
            skLineSegment(sketch, "E28.14.2", {"start": v(-42.43, -56.57) * mm, "end": v(-38.18, -60.81) * mm});
            skLineSegment(sketch, "E28.14.3", {"start": v(-28.28, -42.43) * mm, "end": v(-24.04, -46.67) * mm});
            skLineSegment(sketch, "E28.15.0", {"start": v(-17.55, -68.5) * mm, "end": v(-9.9, -50.02) * mm});
            skLineSegment(sketch, "E28.15.1", {"start": v(-12, -70.8) * mm, "end": v(-4.35, -52.32) * mm});
            skLineSegment(sketch, "E28.15.2", {"start": v(-17.55, -68.5) * mm, "end": v(-12, -70.8) * mm});
            skLineSegment(sketch, "E28.15.3", {"start": v(-9.9, -50.02) * mm, "end": v(-4.35, -52.32) * mm});
            skPoint(sketch, "E28.center", {"position": v(0, 0) * mm});
            skSolve(sketch);
        }
        {
            var Q1;
            Q1=makeQuery(id+"F22.imprint","IMPRINT",FACE,{"disambiguationData":[TD([[makeQuery(id+"F22.imprint","IMPRINT",EDGE,{"derivedFrom":sQuery(id+"F22.wireOp",EDGE,"E27.bottom")}),1.0]])]});
            var Q2;
            Q2=makeQuery(id+"F3.imprint","IMPRINT",FACE,{"disambiguationData":[TD([[makeQuery(id+"F3.imprint","IMPRINT",EDGE,{"derivedFrom":sQuery(id+"F3.wireOp",EDGE,"E20.8.0")}),-1.0]])]});
            loft(context, id + "F23", {"operationType" : NewBodyOperationType.ADD, "sheetProfilesArray" : [{ "sheetProfileEntities" : qUnion([Q1]) }, { "sheetProfileEntities" : qUnion([Q2]) }]});
        }
        {
            var Q1;
            Q1=makeQuery(id+"F22.imprint","IMPRINT",FACE,{"disambiguationData":[TD([[makeQuery(id+"F22.imprint","IMPRINT",EDGE,{"derivedFrom":sQuery(id+"F22.wireOp",EDGE,"E28.1.0")}),-1.0]])]});
            var Q2;
            Q2=makeQuery(id+"F3.imprint","IMPRINT",FACE,{"disambiguationData":[TD([[makeQuery(id+"F3.imprint","IMPRINT",EDGE,{"derivedFrom":sQuery(id+"F3.wireOp",EDGE,"E20.9.0")}),-1.0]])]});
            loft(context, id + "F24", {"operationType" : NewBodyOperationType.ADD, "sheetProfilesArray" : [{ "sheetProfileEntities" : qUnion([Q1]) }, { "sheetProfileEntities" : qUnion([Q2]) }]});
        }
        {
            var Q1;
            Q1=makeQuery(id+"F22.imprint","IMPRINT",FACE,{"disambiguationData":[TD([[makeQuery(id+"F22.imprint","IMPRINT",EDGE,{"derivedFrom":sQuery(id+"F22.wireOp",EDGE,"E28.2.0")}),-1.0]])]});
            var Q2;
            Q2=makeQuery(id+"F3.imprint","IMPRINT",FACE,{"disambiguationData":[TD([[makeQuery(id+"F3.imprint","IMPRINT",EDGE,{"derivedFrom":sQuery(id+"F3.wireOp",EDGE,"E20.10.0")}),-1.0]])]});
            loft(context, id + "F25", {"operationType" : NewBodyOperationType.ADD, "sheetProfilesArray" : [{ "sheetProfileEntities" : qUnion([Q1]) }, { "sheetProfileEntities" : qUnion([Q2]) }]});
        }
        {
            var Q1;
            Q1=makeQuery(id+"F22.imprint","IMPRINT",FACE,{"disambiguationData":[TD([[makeQuery(id+"F22.imprint","IMPRINT",EDGE,{"derivedFrom":sQuery(id+"F22.wireOp",EDGE,"E28.3.0")}),-1.0]])]});
            var Q2;
            Q2=makeQuery(id+"F3.imprint","IMPRINT",FACE,{"disambiguationData":[TD([[makeQuery(id+"F3.imprint","IMPRINT",EDGE,{"derivedFrom":sQuery(id+"F3.wireOp",EDGE,"E20.11.0")}),-1.0]])]});
            loft(context, id + "F26", {"operationType" : NewBodyOperationType.ADD, "sheetProfilesArray" : [{ "sheetProfileEntities" : qUnion([Q1]) }, { "sheetProfileEntities" : qUnion([Q2]) }]});
        }
        {
            var Q1;
            Q1=makeQuery(id+"F22.imprint","IMPRINT",FACE,{"disambiguationData":[TD([[makeQuery(id+"F22.imprint","IMPRINT",EDGE,{"derivedFrom":sQuery(id+"F22.wireOp",EDGE,"E28.4.0")}),-1.0]])]});
            var Q2;
            Q2=makeQuery(id+"F3.imprint","IMPRINT",FACE,{"disambiguationData":[TD([[makeQuery(id+"F3.imprint","IMPRINT",EDGE,{"derivedFrom":sQuery(id+"F3.wireOp",EDGE,"E20.12.0")}),-1.0]])]});
            loft(context, id + "F27", {"operationType" : NewBodyOperationType.ADD, "sheetProfilesArray" : [{ "sheetProfileEntities" : qUnion([Q1]) }, { "sheetProfileEntities" : qUnion([Q2]) }]});
        }
        {
            var Q1;
            Q1=makeQuery(id+"F22.imprint","IMPRINT",FACE,{"disambiguationData":[TD([[makeQuery(id+"F22.imprint","IMPRINT",EDGE,{"derivedFrom":sQuery(id+"F22.wireOp",EDGE,"E28.5.0")}),-1.0]])]});
            var Q2;
            Q2=makeQuery(id+"F3.imprint","IMPRINT",FACE,{"disambiguationData":[TD([[makeQuery(id+"F3.imprint","IMPRINT",EDGE,{"derivedFrom":sQuery(id+"F3.wireOp",EDGE,"E20.13.0")}),-1.0]])]});
            loft(context, id + "F28", {"operationType" : NewBodyOperationType.ADD, "sheetProfilesArray" : [{ "sheetProfileEntities" : qUnion([Q1]) }, { "sheetProfileEntities" : qUnion([Q2]) }]});
        }
        {
            var Q1;
            Q1=makeQuery(id+"F22.imprint","IMPRINT",FACE,{"disambiguationData":[TD([[makeQuery(id+"F22.imprint","IMPRINT",EDGE,{"derivedFrom":sQuery(id+"F22.wireOp",EDGE,"E28.6.0")}),-1.0]])]});
            var Q2;
            Q2=makeQuery(id+"F3.imprint","IMPRINT",FACE,{"disambiguationData":[TD([[makeQuery(id+"F3.imprint","IMPRINT",EDGE,{"derivedFrom":sQuery(id+"F3.wireOp",EDGE,"E20.14.0")}),-1.0]])]});
            loft(context, id + "F29", {"operationType" : NewBodyOperationType.ADD, "sheetProfilesArray" : [{ "sheetProfileEntities" : qUnion([Q1]) }, { "sheetProfileEntities" : qUnion([Q2]) }]});
        }
        {
            var Q1;
            Q1=makeQuery(id+"F22.imprint","IMPRINT",FACE,{"disambiguationData":[TD([[makeQuery(id+"F22.imprint","IMPRINT",EDGE,{"derivedFrom":sQuery(id+"F22.wireOp",EDGE,"E28.7.0")}),-1.0]])]});
            var Q2;
            Q2=makeQuery(id+"F3.imprint","IMPRINT",FACE,{"disambiguationData":[TD([[makeQuery(id+"F3.imprint","IMPRINT",EDGE,{"derivedFrom":sQuery(id+"F3.wireOp",EDGE,"E20.15.0")}),-1.0]])]});
            loft(context, id + "F30", {"operationType" : NewBodyOperationType.ADD, "sheetProfilesArray" : [{ "sheetProfileEntities" : qUnion([Q1]) }, { "sheetProfileEntities" : qUnion([Q2]) }]});
        }
        {
            var Q1;
            Q1=makeQuery(id+"F22.imprint","IMPRINT",FACE,{"disambiguationData":[TD([[makeQuery(id+"F22.imprint","IMPRINT",EDGE,{"derivedFrom":sQuery(id+"F22.wireOp",EDGE,"E28.8.0")}),-1.0]])]});
            var Q2;
            Q2=makeQuery(id+"F3.imprint","IMPRINT",FACE,{"disambiguationData":[TD([[makeQuery(id+"F3.imprint","IMPRINT",EDGE,{"derivedFrom":sQuery(id+"F3.wireOp",EDGE,"E18.bottom")}),1.0]])]});
            loft(context, id + "F31", {"operationType" : NewBodyOperationType.ADD, "sheetProfilesArray" : [{ "sheetProfileEntities" : qUnion([Q1]) }, { "sheetProfileEntities" : qUnion([Q2]) }]});
        }
        {
            var Q1;
            Q1=makeQuery(id+"F22.imprint","IMPRINT",FACE,{"disambiguationData":[TD([[makeQuery(id+"F22.imprint","IMPRINT",EDGE,{"derivedFrom":sQuery(id+"F22.wireOp",EDGE,"E28.9.0")}),-1.0]])]});
            var Q2;
            Q2=makeQuery(id+"F3.imprint","IMPRINT",FACE,{"disambiguationData":[TD([[makeQuery(id+"F3.imprint","IMPRINT",EDGE,{"derivedFrom":sQuery(id+"F3.wireOp",EDGE,"E20.1.0")}),-1.0]])]});
            loft(context, id + "F32", {"operationType" : NewBodyOperationType.ADD, "sheetProfilesArray" : [{ "sheetProfileEntities" : qUnion([Q1]) }, { "sheetProfileEntities" : qUnion([Q2]) }]});
        }
        {
            var Q1;
            Q1=makeQuery(id+"F22.imprint","IMPRINT",FACE,{"disambiguationData":[TD([[makeQuery(id+"F22.imprint","IMPRINT",EDGE,{"derivedFrom":sQuery(id+"F22.wireOp",EDGE,"E28.10.0")}),-1.0]])]});
            var Q2;
            Q2=makeQuery(id+"F3.imprint","IMPRINT",FACE,{"disambiguationData":[TD([[makeQuery(id+"F3.imprint","IMPRINT",EDGE,{"derivedFrom":sQuery(id+"F3.wireOp",EDGE,"E20.2.0")}),-1.0]])]});
            loft(context, id + "F33", {"operationType" : NewBodyOperationType.ADD, "sheetProfilesArray" : [{ "sheetProfileEntities" : qUnion([Q1]) }, { "sheetProfileEntities" : qUnion([Q2]) }]});
        }
        {
            var Q1;
            Q1=makeQuery(id+"F22.imprint","IMPRINT",FACE,{"disambiguationData":[TD([[makeQuery(id+"F22.imprint","IMPRINT",EDGE,{"derivedFrom":sQuery(id+"F22.wireOp",EDGE,"E28.11.0")}),-1.0]])]});
            var Q2;
            Q2=makeQuery(id+"F3.imprint","IMPRINT",FACE,{"disambiguationData":[TD([[makeQuery(id+"F3.imprint","IMPRINT",EDGE,{"derivedFrom":sQuery(id+"F3.wireOp",EDGE,"E20.3.0")}),-1.0]])]});
            loft(context, id + "F34", {"operationType" : NewBodyOperationType.ADD, "sheetProfilesArray" : [{ "sheetProfileEntities" : qUnion([Q1]) }, { "sheetProfileEntities" : qUnion([Q2]) }]});
        }
        {
            var Q1;
            Q1=makeQuery(id+"F22.imprint","IMPRINT",FACE,{"disambiguationData":[TD([[makeQuery(id+"F22.imprint","IMPRINT",EDGE,{"derivedFrom":sQuery(id+"F22.wireOp",EDGE,"E28.12.0")}),-1.0]])]});
            var Q2;
            Q2=makeQuery(id+"F3.imprint","IMPRINT",FACE,{"disambiguationData":[TD([[makeQuery(id+"F3.imprint","IMPRINT",EDGE,{"derivedFrom":sQuery(id+"F3.wireOp",EDGE,"E20.4.0")}),-1.0]])]});
            loft(context, id + "F35", {"operationType" : NewBodyOperationType.ADD, "sheetProfilesArray" : [{ "sheetProfileEntities" : qUnion([Q1]) }, { "sheetProfileEntities" : qUnion([Q2]) }]});
        }
        {
            var Q1;
            Q1=makeQuery(id+"F22.imprint","IMPRINT",FACE,{"disambiguationData":[TD([[makeQuery(id+"F22.imprint","IMPRINT",EDGE,{"derivedFrom":sQuery(id+"F22.wireOp",EDGE,"E28.13.0")}),-1.0]])]});
            var Q2;
            Q2=makeQuery(id+"F3.imprint","IMPRINT",FACE,{"disambiguationData":[TD([[makeQuery(id+"F3.imprint","IMPRINT",EDGE,{"derivedFrom":sQuery(id+"F3.wireOp",EDGE,"E20.5.0")}),-1.0]])]});
            loft(context, id + "F36", {"operationType" : NewBodyOperationType.ADD, "sheetProfilesArray" : [{ "sheetProfileEntities" : qUnion([Q1]) }, { "sheetProfileEntities" : qUnion([Q2]) }]});
        }
        {
            var Q1;
            Q1=makeQuery(id+"F22.imprint","IMPRINT",FACE,{"disambiguationData":[TD([[makeQuery(id+"F22.imprint","IMPRINT",EDGE,{"derivedFrom":sQuery(id+"F22.wireOp",EDGE,"E28.14.0")}),-1.0]])]});
            var Q2;
            Q2=makeQuery(id+"F3.imprint","IMPRINT",FACE,{"disambiguationData":[TD([[makeQuery(id+"F3.imprint","IMPRINT",EDGE,{"derivedFrom":sQuery(id+"F3.wireOp",EDGE,"E20.6.0")}),-1.0]])]});
            loft(context, id + "F37", {"operationType" : NewBodyOperationType.ADD, "sheetProfilesArray" : [{ "sheetProfileEntities" : qUnion([Q1]) }, { "sheetProfileEntities" : qUnion([Q2]) }]});
        }
        {
            var Q1;
            Q1=makeQuery(id+"F22.imprint","IMPRINT",FACE,{"disambiguationData":[TD([[makeQuery(id+"F22.imprint","IMPRINT",EDGE,{"derivedFrom":sQuery(id+"F22.wireOp",EDGE,"E28.15.0")}),-1.0]])]});
            var Q2;
            Q2=makeQuery(id+"F3.imprint","IMPRINT",FACE,{"disambiguationData":[TD([[makeQuery(id+"F3.imprint","IMPRINT",EDGE,{"derivedFrom":sQuery(id+"F3.wireOp",EDGE,"E20.7.0")}),-1.0]])]});
            loft(context, id + "F38", {"operationType" : NewBodyOperationType.ADD, "sheetProfilesArray" : [{ "sheetProfileEntities" : qUnion([Q1]) }, { "sheetProfileEntities" : qUnion([Q2]) }]});
        }
        {
            var Q0;
            Q0=qCreatedBy(makeId("Top.planeOp"),FACE);
            var sketch = newSketch(context, id + "F39", { "sketchPlane" : qUnion([Q0])});
            skCircle(sketch, "E29", {"center": v(0, 0) * mm, "radius": 61 * mm});
            skCircle(sketch, "E30", {"center": v(0, 0) * mm, "radius": 69 * mm});
            skSolve(sketch);
        }
        {
            var Q0;
            Q0=makeQuery(id+"F39.imprint","IMPRINT",FACE,{"disambiguationData":[TD([[makeQuery(id+"F39.imprint","IMPRINT",EDGE,{"derivedFrom":sQuery(id+"F39.wireOp",EDGE,"E29")}),-1.0]])]});
            extrude(context, id + "F40", {"entities" : qUnion([Q0]), "operationType" : NewBodyOperationType.ADD, "depth" : 6 * mm, "symmetric" : true});
        }
        {
            var Q0;
            Q0=qCreatedBy(makeId("Right.planeOp"),FACE);
            var sketch = newSketch(context, id + "F41", { "sketchPlane" : qUnion([Q0])});
            skLineSegment(sketch, "E31", {"start": v(0, 27) * mm, "end": v(0, -27) * mm, "construction": true});
            skCircle(sketch, "E32", {"center": v(0, 0) * mm, "radius": 67.5 * mm});
            skCircle(sketch, "E33", {"center": v(0, 0) * mm, "radius": 85 * mm});
            skLineSegment(sketch, "E34", {"start": v(0, 85) * mm, "end": v(0, -85) * mm});
            skSolve(sketch);
        }
        {
            var Q0;
            {var subQ0=sQuery(id+"F41.wireOp",EDGE,"E34");var subQ1=sQuery(id+"F41.wireOp",EDGE,"E32");var subQ2=makeQuery(id+"F41.imprint","INTERSECT",VERTEX,{"disambiguationData":[OD(0.0)],"derivedFrom":[subQ1,subQ0]});Q0=makeQuery(id+"F41.imprint","IMPRINT",FACE,{"disambiguationData":[TD([[makeQuery(id+"F41.imprint","IMPRINT",EDGE,{"disambiguationData":[TD([[subQ2,-1.0]])],"derivedFrom":subQ1}),-1.0]])]});}
            var Q1;
            Q1=sQuery(id+"F41.wireOp",EDGE,"E31");
            revolve(context, id + "F42", {"operationType" : NewBodyOperationType.REMOVE, "entities" : qUnion([Q0]), "axis" : qUnion([Q1]), "revolveType" : RevolveType.FULL, "oppositeDirection" : true});
        }
        {
            var Q0;
            Q0=makeQuery(id+"F42.boolean.opBoolean","INTERSECT",EDGE,{"disambiguationData":[OD(5.0)],"derivedFrom":[makeQuery(id+"F20.boolean.opBoolean","MERGE",FACE,{"derivedFrom":[makeQuery(id+"F19.boolean.opBoolean","MERGE",FACE,{"derivedFrom":[makeQuery(id+"F18.boolean.opBoolean","MERGE",FACE,{"derivedFrom":[makeQuery(id+"F17.boolean.opBoolean","MERGE",FACE,{"derivedFrom":[makeQuery(id+"F16.boolean.opBoolean","MERGE",FACE,{"derivedFrom":[makeQuery(id+"F15.boolean.opBoolean","MERGE",FACE,{"derivedFrom":[makeQuery(id+"F14.boolean.opBoolean","MERGE",FACE,{"derivedFrom":[makeQuery(id+"F13.boolean.opBoolean","MERGE",FACE,{"derivedFrom":[makeQuery(id+"F12.boolean.opBoolean","MERGE",FACE,{"derivedFrom":[makeQuery(id+"F11.boolean.opBoolean","MERGE",FACE,{"derivedFrom":[makeQuery(id+"F10.boolean.opBoolean","MERGE",FACE,{"derivedFrom":[makeQuery(id+"F9.boolean.opBoolean","MERGE",FACE,{"derivedFrom":[makeQuery(id+"F8.boolean.opBoolean","MERGE",FACE,{"derivedFrom":[makeQuery(id+"F7.boolean.opBoolean","MERGE",FACE,{"derivedFrom":[makeQuery(id+"F6.boolean.opBoolean","MERGE",FACE,{"derivedFrom":[makeQuery(id+"F5.boolean.opBoolean","MERGE",FACE,{"derivedFrom":[makeQuery(id+"F1.opRevolve","SWEPT_FACE",FACE,{"disambiguationData":[OSD([sQuery(id+"F0.wireOp",EDGE,"E14")])]}),makeQuery(id+"F5.opLoft","CAP_FACE",FACE,{"disambiguationData":[OSD([makeQuery(id+"F4.imprint","IMPRINT",FACE,{"disambiguationData":[TD([[makeQuery(id+"F4.imprint","IMPRINT",EDGE,{"derivedFrom":sQuery(id+"F4.wireOp",EDGE,"E21")}),1.0]])]})])],"isStart":true})]}),makeQuery(id+"F6.opLoft","CAP_FACE",FACE,{"disambiguationData":[OSD([makeQuery(id+"F4.imprint","IMPRINT",FACE,{"disambiguationData":[TD([[makeQuery(id+"F4.imprint","IMPRINT",EDGE,{"derivedFrom":sQuery(id+"F4.wireOp",EDGE,"E26.15.0")}),1.0]])]})])],"isStart":true})]}),makeQuery(id+"F7.opLoft","CAP_FACE",FACE,{"disambiguationData":[OSD([makeQuery(id+"F4.imprint","IMPRINT",FACE,{"disambiguationData":[TD([[makeQuery(id+"F4.imprint","IMPRINT",EDGE,{"derivedFrom":sQuery(id+"F4.wireOp",EDGE,"E26.14.0")}),1.0]])]})])],"isStart":true})]}),makeQuery(id+"F8.opLoft","CAP_FACE",FACE,{"disambiguationData":[OSD([makeQuery(id+"F4.imprint","IMPRINT",FACE,{"disambiguationData":[TD([[makeQuery(id+"F4.imprint","IMPRINT",EDGE,{"derivedFrom":sQuery(id+"F4.wireOp",EDGE,"E26.13.0")}),1.0]])]})])],"isStart":true})]}),makeQuery(id+"F9.opLoft","CAP_FACE",FACE,{"disambiguationData":[OSD([makeQuery(id+"F4.imprint","IMPRINT",FACE,{"disambiguationData":[TD([[makeQuery(id+"F4.imprint","IMPRINT",EDGE,{"derivedFrom":sQuery(id+"F4.wireOp",EDGE,"E26.12.0")}),1.0]])]})])],"isStart":true})]}),makeQuery(id+"F10.opLoft","CAP_FACE",FACE,{"disambiguationData":[OSD([makeQuery(id+"F4.imprint","IMPRINT",FACE,{"disambiguationData":[TD([[makeQuery(id+"F4.imprint","IMPRINT",EDGE,{"derivedFrom":sQuery(id+"F4.wireOp",EDGE,"E26.11.0")}),1.0]])]})])],"isStart":true})]}),makeQuery(id+"F11.opLoft","CAP_FACE",FACE,{"disambiguationData":[OSD([makeQuery(id+"F4.imprint","IMPRINT",FACE,{"disambiguationData":[TD([[makeQuery(id+"F4.imprint","IMPRINT",EDGE,{"derivedFrom":sQuery(id+"F4.wireOp",EDGE,"E26.10.0")}),1.0]])]})])],"isStart":true})]}),makeQuery(id+"F12.opLoft","CAP_FACE",FACE,{"disambiguationData":[OSD([makeQuery(id+"F4.imprint","IMPRINT",FACE,{"disambiguationData":[TD([[makeQuery(id+"F4.imprint","IMPRINT",EDGE,{"derivedFrom":sQuery(id+"F4.wireOp",EDGE,"E26.9.0")}),1.0]])]})])],"isStart":true})]}),makeQuery(id+"F13.opLoft","CAP_FACE",FACE,{"disambiguationData":[OSD([makeQuery(id+"F4.imprint","IMPRINT",FACE,{"disambiguationData":[TD([[makeQuery(id+"F4.imprint","IMPRINT",EDGE,{"derivedFrom":sQuery(id+"F4.wireOp",EDGE,"E26.8.0")}),1.0]])]})])],"isStart":true})]}),makeQuery(id+"F14.opLoft","CAP_FACE",FACE,{"disambiguationData":[OSD([makeQuery(id+"F4.imprint","IMPRINT",FACE,{"disambiguationData":[TD([[makeQuery(id+"F4.imprint","IMPRINT",EDGE,{"derivedFrom":sQuery(id+"F4.wireOp",EDGE,"E26.7.0")}),1.0]])]})])],"isStart":true})]}),makeQuery(id+"F15.opLoft","CAP_FACE",FACE,{"disambiguationData":[OSD([makeQuery(id+"F4.imprint","IMPRINT",FACE,{"disambiguationData":[TD([[makeQuery(id+"F4.imprint","IMPRINT",EDGE,{"derivedFrom":sQuery(id+"F4.wireOp",EDGE,"E26.6.0")}),1.0]])]})])],"isStart":true})]}),makeQuery(id+"F16.opLoft","CAP_FACE",FACE,{"disambiguationData":[OSD([makeQuery(id+"F4.imprint","IMPRINT",FACE,{"disambiguationData":[TD([[makeQuery(id+"F4.imprint","IMPRINT",EDGE,{"derivedFrom":sQuery(id+"F4.wireOp",EDGE,"E26.5.0")}),1.0]])]})])],"isStart":true})]}),makeQuery(id+"F17.opLoft","CAP_FACE",FACE,{"disambiguationData":[OSD([makeQuery(id+"F4.imprint","IMPRINT",FACE,{"disambiguationData":[TD([[makeQuery(id+"F4.imprint","IMPRINT",EDGE,{"derivedFrom":sQuery(id+"F4.wireOp",EDGE,"E26.4.0")}),1.0]])]})])],"isStart":true})]}),makeQuery(id+"F18.opLoft","CAP_FACE",FACE,{"disambiguationData":[OSD([makeQuery(id+"F4.imprint","IMPRINT",FACE,{"disambiguationData":[TD([[makeQuery(id+"F4.imprint","IMPRINT",EDGE,{"derivedFrom":sQuery(id+"F4.wireOp",EDGE,"E26.3.0")}),1.0]])]})])],"isStart":true})]}),makeQuery(id+"F19.opLoft","CAP_FACE",FACE,{"disambiguationData":[OSD([makeQuery(id+"F4.imprint","IMPRINT",FACE,{"disambiguationData":[TD([[makeQuery(id+"F4.imprint","IMPRINT",EDGE,{"derivedFrom":sQuery(id+"F4.wireOp",EDGE,"E26.2.0")}),1.0]])]})])],"isStart":true})]}),makeQuery(id+"F20.opLoft","CAP_FACE",FACE,{"disambiguationData":[OSD([makeQuery(id+"F4.imprint","IMPRINT",FACE,{"disambiguationData":[TD([[makeQuery(id+"F4.imprint","IMPRINT",EDGE,{"derivedFrom":sQuery(id+"F4.wireOp",EDGE,"E26.1.0")}),1.0]])]})])],"isStart":true})]}),makeQuery(id+"F42.opRevolve","SWEPT_FACE",FACE,{"disambiguationData":[OSD([sQuery(id+"F41.wireOp",EDGE,"E32")])]})]});
            var Q1;
            Q1=makeQuery(id+"F42.boolean.opBoolean","INTERSECT",EDGE,{"disambiguationData":[OD(4.0)],"derivedFrom":[makeQuery(id+"F20.boolean.opBoolean","MERGE",FACE,{"derivedFrom":[makeQuery(id+"F19.boolean.opBoolean","MERGE",FACE,{"derivedFrom":[makeQuery(id+"F18.boolean.opBoolean","MERGE",FACE,{"derivedFrom":[makeQuery(id+"F17.boolean.opBoolean","MERGE",FACE,{"derivedFrom":[makeQuery(id+"F16.boolean.opBoolean","MERGE",FACE,{"derivedFrom":[makeQuery(id+"F15.boolean.opBoolean","MERGE",FACE,{"derivedFrom":[makeQuery(id+"F14.boolean.opBoolean","MERGE",FACE,{"derivedFrom":[makeQuery(id+"F13.boolean.opBoolean","MERGE",FACE,{"derivedFrom":[makeQuery(id+"F12.boolean.opBoolean","MERGE",FACE,{"derivedFrom":[makeQuery(id+"F11.boolean.opBoolean","MERGE",FACE,{"derivedFrom":[makeQuery(id+"F10.boolean.opBoolean","MERGE",FACE,{"derivedFrom":[makeQuery(id+"F9.boolean.opBoolean","MERGE",FACE,{"derivedFrom":[makeQuery(id+"F8.boolean.opBoolean","MERGE",FACE,{"derivedFrom":[makeQuery(id+"F7.boolean.opBoolean","MERGE",FACE,{"derivedFrom":[makeQuery(id+"F6.boolean.opBoolean","MERGE",FACE,{"derivedFrom":[makeQuery(id+"F5.boolean.opBoolean","MERGE",FACE,{"derivedFrom":[makeQuery(id+"F1.opRevolve","SWEPT_FACE",FACE,{"disambiguationData":[OSD([sQuery(id+"F0.wireOp",EDGE,"E14")])]}),makeQuery(id+"F5.opLoft","CAP_FACE",FACE,{"disambiguationData":[OSD([makeQuery(id+"F4.imprint","IMPRINT",FACE,{"disambiguationData":[TD([[makeQuery(id+"F4.imprint","IMPRINT",EDGE,{"derivedFrom":sQuery(id+"F4.wireOp",EDGE,"E21")}),1.0]])]})])],"isStart":true})]}),makeQuery(id+"F6.opLoft","CAP_FACE",FACE,{"disambiguationData":[OSD([makeQuery(id+"F4.imprint","IMPRINT",FACE,{"disambiguationData":[TD([[makeQuery(id+"F4.imprint","IMPRINT",EDGE,{"derivedFrom":sQuery(id+"F4.wireOp",EDGE,"E26.15.0")}),1.0]])]})])],"isStart":true})]}),makeQuery(id+"F7.opLoft","CAP_FACE",FACE,{"disambiguationData":[OSD([makeQuery(id+"F4.imprint","IMPRINT",FACE,{"disambiguationData":[TD([[makeQuery(id+"F4.imprint","IMPRINT",EDGE,{"derivedFrom":sQuery(id+"F4.wireOp",EDGE,"E26.14.0")}),1.0]])]})])],"isStart":true})]}),makeQuery(id+"F8.opLoft","CAP_FACE",FACE,{"disambiguationData":[OSD([makeQuery(id+"F4.imprint","IMPRINT",FACE,{"disambiguationData":[TD([[makeQuery(id+"F4.imprint","IMPRINT",EDGE,{"derivedFrom":sQuery(id+"F4.wireOp",EDGE,"E26.13.0")}),1.0]])]})])],"isStart":true})]}),makeQuery(id+"F9.opLoft","CAP_FACE",FACE,{"disambiguationData":[OSD([makeQuery(id+"F4.imprint","IMPRINT",FACE,{"disambiguationData":[TD([[makeQuery(id+"F4.imprint","IMPRINT",EDGE,{"derivedFrom":sQuery(id+"F4.wireOp",EDGE,"E26.12.0")}),1.0]])]})])],"isStart":true})]}),makeQuery(id+"F10.opLoft","CAP_FACE",FACE,{"disambiguationData":[OSD([makeQuery(id+"F4.imprint","IMPRINT",FACE,{"disambiguationData":[TD([[makeQuery(id+"F4.imprint","IMPRINT",EDGE,{"derivedFrom":sQuery(id+"F4.wireOp",EDGE,"E26.11.0")}),1.0]])]})])],"isStart":true})]}),makeQuery(id+"F11.opLoft","CAP_FACE",FACE,{"disambiguationData":[OSD([makeQuery(id+"F4.imprint","IMPRINT",FACE,{"disambiguationData":[TD([[makeQuery(id+"F4.imprint","IMPRINT",EDGE,{"derivedFrom":sQuery(id+"F4.wireOp",EDGE,"E26.10.0")}),1.0]])]})])],"isStart":true})]}),makeQuery(id+"F12.opLoft","CAP_FACE",FACE,{"disambiguationData":[OSD([makeQuery(id+"F4.imprint","IMPRINT",FACE,{"disambiguationData":[TD([[makeQuery(id+"F4.imprint","IMPRINT",EDGE,{"derivedFrom":sQuery(id+"F4.wireOp",EDGE,"E26.9.0")}),1.0]])]})])],"isStart":true})]}),makeQuery(id+"F13.opLoft","CAP_FACE",FACE,{"disambiguationData":[OSD([makeQuery(id+"F4.imprint","IMPRINT",FACE,{"disambiguationData":[TD([[makeQuery(id+"F4.imprint","IMPRINT",EDGE,{"derivedFrom":sQuery(id+"F4.wireOp",EDGE,"E26.8.0")}),1.0]])]})])],"isStart":true})]}),makeQuery(id+"F14.opLoft","CAP_FACE",FACE,{"disambiguationData":[OSD([makeQuery(id+"F4.imprint","IMPRINT",FACE,{"disambiguationData":[TD([[makeQuery(id+"F4.imprint","IMPRINT",EDGE,{"derivedFrom":sQuery(id+"F4.wireOp",EDGE,"E26.7.0")}),1.0]])]})])],"isStart":true})]}),makeQuery(id+"F15.opLoft","CAP_FACE",FACE,{"disambiguationData":[OSD([makeQuery(id+"F4.imprint","IMPRINT",FACE,{"disambiguationData":[TD([[makeQuery(id+"F4.imprint","IMPRINT",EDGE,{"derivedFrom":sQuery(id+"F4.wireOp",EDGE,"E26.6.0")}),1.0]])]})])],"isStart":true})]}),makeQuery(id+"F16.opLoft","CAP_FACE",FACE,{"disambiguationData":[OSD([makeQuery(id+"F4.imprint","IMPRINT",FACE,{"disambiguationData":[TD([[makeQuery(id+"F4.imprint","IMPRINT",EDGE,{"derivedFrom":sQuery(id+"F4.wireOp",EDGE,"E26.5.0")}),1.0]])]})])],"isStart":true})]}),makeQuery(id+"F17.opLoft","CAP_FACE",FACE,{"disambiguationData":[OSD([makeQuery(id+"F4.imprint","IMPRINT",FACE,{"disambiguationData":[TD([[makeQuery(id+"F4.imprint","IMPRINT",EDGE,{"derivedFrom":sQuery(id+"F4.wireOp",EDGE,"E26.4.0")}),1.0]])]})])],"isStart":true})]}),makeQuery(id+"F18.opLoft","CAP_FACE",FACE,{"disambiguationData":[OSD([makeQuery(id+"F4.imprint","IMPRINT",FACE,{"disambiguationData":[TD([[makeQuery(id+"F4.imprint","IMPRINT",EDGE,{"derivedFrom":sQuery(id+"F4.wireOp",EDGE,"E26.3.0")}),1.0]])]})])],"isStart":true})]}),makeQuery(id+"F19.opLoft","CAP_FACE",FACE,{"disambiguationData":[OSD([makeQuery(id+"F4.imprint","IMPRINT",FACE,{"disambiguationData":[TD([[makeQuery(id+"F4.imprint","IMPRINT",EDGE,{"derivedFrom":sQuery(id+"F4.wireOp",EDGE,"E26.2.0")}),1.0]])]})])],"isStart":true})]}),makeQuery(id+"F20.opLoft","CAP_FACE",FACE,{"disambiguationData":[OSD([makeQuery(id+"F4.imprint","IMPRINT",FACE,{"disambiguationData":[TD([[makeQuery(id+"F4.imprint","IMPRINT",EDGE,{"derivedFrom":sQuery(id+"F4.wireOp",EDGE,"E26.1.0")}),1.0]])]})])],"isStart":true})]}),makeQuery(id+"F42.opRevolve","SWEPT_FACE",FACE,{"disambiguationData":[OSD([sQuery(id+"F41.wireOp",EDGE,"E32")])]})]});
            var Q2;
            Q2=makeQuery(id+"F42.boolean.opBoolean","INTERSECT",EDGE,{"disambiguationData":[OD(3.0)],"derivedFrom":[makeQuery(id+"F20.boolean.opBoolean","MERGE",FACE,{"derivedFrom":[makeQuery(id+"F19.boolean.opBoolean","MERGE",FACE,{"derivedFrom":[makeQuery(id+"F18.boolean.opBoolean","MERGE",FACE,{"derivedFrom":[makeQuery(id+"F17.boolean.opBoolean","MERGE",FACE,{"derivedFrom":[makeQuery(id+"F16.boolean.opBoolean","MERGE",FACE,{"derivedFrom":[makeQuery(id+"F15.boolean.opBoolean","MERGE",FACE,{"derivedFrom":[makeQuery(id+"F14.boolean.opBoolean","MERGE",FACE,{"derivedFrom":[makeQuery(id+"F13.boolean.opBoolean","MERGE",FACE,{"derivedFrom":[makeQuery(id+"F12.boolean.opBoolean","MERGE",FACE,{"derivedFrom":[makeQuery(id+"F11.boolean.opBoolean","MERGE",FACE,{"derivedFrom":[makeQuery(id+"F10.boolean.opBoolean","MERGE",FACE,{"derivedFrom":[makeQuery(id+"F9.boolean.opBoolean","MERGE",FACE,{"derivedFrom":[makeQuery(id+"F8.boolean.opBoolean","MERGE",FACE,{"derivedFrom":[makeQuery(id+"F7.boolean.opBoolean","MERGE",FACE,{"derivedFrom":[makeQuery(id+"F6.boolean.opBoolean","MERGE",FACE,{"derivedFrom":[makeQuery(id+"F5.boolean.opBoolean","MERGE",FACE,{"derivedFrom":[makeQuery(id+"F1.opRevolve","SWEPT_FACE",FACE,{"disambiguationData":[OSD([sQuery(id+"F0.wireOp",EDGE,"E14")])]}),makeQuery(id+"F5.opLoft","CAP_FACE",FACE,{"disambiguationData":[OSD([makeQuery(id+"F4.imprint","IMPRINT",FACE,{"disambiguationData":[TD([[makeQuery(id+"F4.imprint","IMPRINT",EDGE,{"derivedFrom":sQuery(id+"F4.wireOp",EDGE,"E21")}),1.0]])]})])],"isStart":true})]}),makeQuery(id+"F6.opLoft","CAP_FACE",FACE,{"disambiguationData":[OSD([makeQuery(id+"F4.imprint","IMPRINT",FACE,{"disambiguationData":[TD([[makeQuery(id+"F4.imprint","IMPRINT",EDGE,{"derivedFrom":sQuery(id+"F4.wireOp",EDGE,"E26.15.0")}),1.0]])]})])],"isStart":true})]}),makeQuery(id+"F7.opLoft","CAP_FACE",FACE,{"disambiguationData":[OSD([makeQuery(id+"F4.imprint","IMPRINT",FACE,{"disambiguationData":[TD([[makeQuery(id+"F4.imprint","IMPRINT",EDGE,{"derivedFrom":sQuery(id+"F4.wireOp",EDGE,"E26.14.0")}),1.0]])]})])],"isStart":true})]}),makeQuery(id+"F8.opLoft","CAP_FACE",FACE,{"disambiguationData":[OSD([makeQuery(id+"F4.imprint","IMPRINT",FACE,{"disambiguationData":[TD([[makeQuery(id+"F4.imprint","IMPRINT",EDGE,{"derivedFrom":sQuery(id+"F4.wireOp",EDGE,"E26.13.0")}),1.0]])]})])],"isStart":true})]}),makeQuery(id+"F9.opLoft","CAP_FACE",FACE,{"disambiguationData":[OSD([makeQuery(id+"F4.imprint","IMPRINT",FACE,{"disambiguationData":[TD([[makeQuery(id+"F4.imprint","IMPRINT",EDGE,{"derivedFrom":sQuery(id+"F4.wireOp",EDGE,"E26.12.0")}),1.0]])]})])],"isStart":true})]}),makeQuery(id+"F10.opLoft","CAP_FACE",FACE,{"disambiguationData":[OSD([makeQuery(id+"F4.imprint","IMPRINT",FACE,{"disambiguationData":[TD([[makeQuery(id+"F4.imprint","IMPRINT",EDGE,{"derivedFrom":sQuery(id+"F4.wireOp",EDGE,"E26.11.0")}),1.0]])]})])],"isStart":true})]}),makeQuery(id+"F11.opLoft","CAP_FACE",FACE,{"disambiguationData":[OSD([makeQuery(id+"F4.imprint","IMPRINT",FACE,{"disambiguationData":[TD([[makeQuery(id+"F4.imprint","IMPRINT",EDGE,{"derivedFrom":sQuery(id+"F4.wireOp",EDGE,"E26.10.0")}),1.0]])]})])],"isStart":true})]}),makeQuery(id+"F12.opLoft","CAP_FACE",FACE,{"disambiguationData":[OSD([makeQuery(id+"F4.imprint","IMPRINT",FACE,{"disambiguationData":[TD([[makeQuery(id+"F4.imprint","IMPRINT",EDGE,{"derivedFrom":sQuery(id+"F4.wireOp",EDGE,"E26.9.0")}),1.0]])]})])],"isStart":true})]}),makeQuery(id+"F13.opLoft","CAP_FACE",FACE,{"disambiguationData":[OSD([makeQuery(id+"F4.imprint","IMPRINT",FACE,{"disambiguationData":[TD([[makeQuery(id+"F4.imprint","IMPRINT",EDGE,{"derivedFrom":sQuery(id+"F4.wireOp",EDGE,"E26.8.0")}),1.0]])]})])],"isStart":true})]}),makeQuery(id+"F14.opLoft","CAP_FACE",FACE,{"disambiguationData":[OSD([makeQuery(id+"F4.imprint","IMPRINT",FACE,{"disambiguationData":[TD([[makeQuery(id+"F4.imprint","IMPRINT",EDGE,{"derivedFrom":sQuery(id+"F4.wireOp",EDGE,"E26.7.0")}),1.0]])]})])],"isStart":true})]}),makeQuery(id+"F15.opLoft","CAP_FACE",FACE,{"disambiguationData":[OSD([makeQuery(id+"F4.imprint","IMPRINT",FACE,{"disambiguationData":[TD([[makeQuery(id+"F4.imprint","IMPRINT",EDGE,{"derivedFrom":sQuery(id+"F4.wireOp",EDGE,"E26.6.0")}),1.0]])]})])],"isStart":true})]}),makeQuery(id+"F16.opLoft","CAP_FACE",FACE,{"disambiguationData":[OSD([makeQuery(id+"F4.imprint","IMPRINT",FACE,{"disambiguationData":[TD([[makeQuery(id+"F4.imprint","IMPRINT",EDGE,{"derivedFrom":sQuery(id+"F4.wireOp",EDGE,"E26.5.0")}),1.0]])]})])],"isStart":true})]}),makeQuery(id+"F17.opLoft","CAP_FACE",FACE,{"disambiguationData":[OSD([makeQuery(id+"F4.imprint","IMPRINT",FACE,{"disambiguationData":[TD([[makeQuery(id+"F4.imprint","IMPRINT",EDGE,{"derivedFrom":sQuery(id+"F4.wireOp",EDGE,"E26.4.0")}),1.0]])]})])],"isStart":true})]}),makeQuery(id+"F18.opLoft","CAP_FACE",FACE,{"disambiguationData":[OSD([makeQuery(id+"F4.imprint","IMPRINT",FACE,{"disambiguationData":[TD([[makeQuery(id+"F4.imprint","IMPRINT",EDGE,{"derivedFrom":sQuery(id+"F4.wireOp",EDGE,"E26.3.0")}),1.0]])]})])],"isStart":true})]}),makeQuery(id+"F19.opLoft","CAP_FACE",FACE,{"disambiguationData":[OSD([makeQuery(id+"F4.imprint","IMPRINT",FACE,{"disambiguationData":[TD([[makeQuery(id+"F4.imprint","IMPRINT",EDGE,{"derivedFrom":sQuery(id+"F4.wireOp",EDGE,"E26.2.0")}),1.0]])]})])],"isStart":true})]}),makeQuery(id+"F20.opLoft","CAP_FACE",FACE,{"disambiguationData":[OSD([makeQuery(id+"F4.imprint","IMPRINT",FACE,{"disambiguationData":[TD([[makeQuery(id+"F4.imprint","IMPRINT",EDGE,{"derivedFrom":sQuery(id+"F4.wireOp",EDGE,"E26.1.0")}),1.0]])]})])],"isStart":true})]}),makeQuery(id+"F42.opRevolve","SWEPT_FACE",FACE,{"disambiguationData":[OSD([sQuery(id+"F41.wireOp",EDGE,"E32")])]})]});
            var Q3;
            Q3=makeQuery(id+"F42.boolean.opBoolean","INTERSECT",EDGE,{"disambiguationData":[OD(2.0)],"derivedFrom":[makeQuery(id+"F20.boolean.opBoolean","MERGE",FACE,{"derivedFrom":[makeQuery(id+"F19.boolean.opBoolean","MERGE",FACE,{"derivedFrom":[makeQuery(id+"F18.boolean.opBoolean","MERGE",FACE,{"derivedFrom":[makeQuery(id+"F17.boolean.opBoolean","MERGE",FACE,{"derivedFrom":[makeQuery(id+"F16.boolean.opBoolean","MERGE",FACE,{"derivedFrom":[makeQuery(id+"F15.boolean.opBoolean","MERGE",FACE,{"derivedFrom":[makeQuery(id+"F14.boolean.opBoolean","MERGE",FACE,{"derivedFrom":[makeQuery(id+"F13.boolean.opBoolean","MERGE",FACE,{"derivedFrom":[makeQuery(id+"F12.boolean.opBoolean","MERGE",FACE,{"derivedFrom":[makeQuery(id+"F11.boolean.opBoolean","MERGE",FACE,{"derivedFrom":[makeQuery(id+"F10.boolean.opBoolean","MERGE",FACE,{"derivedFrom":[makeQuery(id+"F9.boolean.opBoolean","MERGE",FACE,{"derivedFrom":[makeQuery(id+"F8.boolean.opBoolean","MERGE",FACE,{"derivedFrom":[makeQuery(id+"F7.boolean.opBoolean","MERGE",FACE,{"derivedFrom":[makeQuery(id+"F6.boolean.opBoolean","MERGE",FACE,{"derivedFrom":[makeQuery(id+"F5.boolean.opBoolean","MERGE",FACE,{"derivedFrom":[makeQuery(id+"F1.opRevolve","SWEPT_FACE",FACE,{"disambiguationData":[OSD([sQuery(id+"F0.wireOp",EDGE,"E14")])]}),makeQuery(id+"F5.opLoft","CAP_FACE",FACE,{"disambiguationData":[OSD([makeQuery(id+"F4.imprint","IMPRINT",FACE,{"disambiguationData":[TD([[makeQuery(id+"F4.imprint","IMPRINT",EDGE,{"derivedFrom":sQuery(id+"F4.wireOp",EDGE,"E21")}),1.0]])]})])],"isStart":true})]}),makeQuery(id+"F6.opLoft","CAP_FACE",FACE,{"disambiguationData":[OSD([makeQuery(id+"F4.imprint","IMPRINT",FACE,{"disambiguationData":[TD([[makeQuery(id+"F4.imprint","IMPRINT",EDGE,{"derivedFrom":sQuery(id+"F4.wireOp",EDGE,"E26.15.0")}),1.0]])]})])],"isStart":true})]}),makeQuery(id+"F7.opLoft","CAP_FACE",FACE,{"disambiguationData":[OSD([makeQuery(id+"F4.imprint","IMPRINT",FACE,{"disambiguationData":[TD([[makeQuery(id+"F4.imprint","IMPRINT",EDGE,{"derivedFrom":sQuery(id+"F4.wireOp",EDGE,"E26.14.0")}),1.0]])]})])],"isStart":true})]}),makeQuery(id+"F8.opLoft","CAP_FACE",FACE,{"disambiguationData":[OSD([makeQuery(id+"F4.imprint","IMPRINT",FACE,{"disambiguationData":[TD([[makeQuery(id+"F4.imprint","IMPRINT",EDGE,{"derivedFrom":sQuery(id+"F4.wireOp",EDGE,"E26.13.0")}),1.0]])]})])],"isStart":true})]}),makeQuery(id+"F9.opLoft","CAP_FACE",FACE,{"disambiguationData":[OSD([makeQuery(id+"F4.imprint","IMPRINT",FACE,{"disambiguationData":[TD([[makeQuery(id+"F4.imprint","IMPRINT",EDGE,{"derivedFrom":sQuery(id+"F4.wireOp",EDGE,"E26.12.0")}),1.0]])]})])],"isStart":true})]}),makeQuery(id+"F10.opLoft","CAP_FACE",FACE,{"disambiguationData":[OSD([makeQuery(id+"F4.imprint","IMPRINT",FACE,{"disambiguationData":[TD([[makeQuery(id+"F4.imprint","IMPRINT",EDGE,{"derivedFrom":sQuery(id+"F4.wireOp",EDGE,"E26.11.0")}),1.0]])]})])],"isStart":true})]}),makeQuery(id+"F11.opLoft","CAP_FACE",FACE,{"disambiguationData":[OSD([makeQuery(id+"F4.imprint","IMPRINT",FACE,{"disambiguationData":[TD([[makeQuery(id+"F4.imprint","IMPRINT",EDGE,{"derivedFrom":sQuery(id+"F4.wireOp",EDGE,"E26.10.0")}),1.0]])]})])],"isStart":true})]}),makeQuery(id+"F12.opLoft","CAP_FACE",FACE,{"disambiguationData":[OSD([makeQuery(id+"F4.imprint","IMPRINT",FACE,{"disambiguationData":[TD([[makeQuery(id+"F4.imprint","IMPRINT",EDGE,{"derivedFrom":sQuery(id+"F4.wireOp",EDGE,"E26.9.0")}),1.0]])]})])],"isStart":true})]}),makeQuery(id+"F13.opLoft","CAP_FACE",FACE,{"disambiguationData":[OSD([makeQuery(id+"F4.imprint","IMPRINT",FACE,{"disambiguationData":[TD([[makeQuery(id+"F4.imprint","IMPRINT",EDGE,{"derivedFrom":sQuery(id+"F4.wireOp",EDGE,"E26.8.0")}),1.0]])]})])],"isStart":true})]}),makeQuery(id+"F14.opLoft","CAP_FACE",FACE,{"disambiguationData":[OSD([makeQuery(id+"F4.imprint","IMPRINT",FACE,{"disambiguationData":[TD([[makeQuery(id+"F4.imprint","IMPRINT",EDGE,{"derivedFrom":sQuery(id+"F4.wireOp",EDGE,"E26.7.0")}),1.0]])]})])],"isStart":true})]}),makeQuery(id+"F15.opLoft","CAP_FACE",FACE,{"disambiguationData":[OSD([makeQuery(id+"F4.imprint","IMPRINT",FACE,{"disambiguationData":[TD([[makeQuery(id+"F4.imprint","IMPRINT",EDGE,{"derivedFrom":sQuery(id+"F4.wireOp",EDGE,"E26.6.0")}),1.0]])]})])],"isStart":true})]}),makeQuery(id+"F16.opLoft","CAP_FACE",FACE,{"disambiguationData":[OSD([makeQuery(id+"F4.imprint","IMPRINT",FACE,{"disambiguationData":[TD([[makeQuery(id+"F4.imprint","IMPRINT",EDGE,{"derivedFrom":sQuery(id+"F4.wireOp",EDGE,"E26.5.0")}),1.0]])]})])],"isStart":true})]}),makeQuery(id+"F17.opLoft","CAP_FACE",FACE,{"disambiguationData":[OSD([makeQuery(id+"F4.imprint","IMPRINT",FACE,{"disambiguationData":[TD([[makeQuery(id+"F4.imprint","IMPRINT",EDGE,{"derivedFrom":sQuery(id+"F4.wireOp",EDGE,"E26.4.0")}),1.0]])]})])],"isStart":true})]}),makeQuery(id+"F18.opLoft","CAP_FACE",FACE,{"disambiguationData":[OSD([makeQuery(id+"F4.imprint","IMPRINT",FACE,{"disambiguationData":[TD([[makeQuery(id+"F4.imprint","IMPRINT",EDGE,{"derivedFrom":sQuery(id+"F4.wireOp",EDGE,"E26.3.0")}),1.0]])]})])],"isStart":true})]}),makeQuery(id+"F19.opLoft","CAP_FACE",FACE,{"disambiguationData":[OSD([makeQuery(id+"F4.imprint","IMPRINT",FACE,{"disambiguationData":[TD([[makeQuery(id+"F4.imprint","IMPRINT",EDGE,{"derivedFrom":sQuery(id+"F4.wireOp",EDGE,"E26.2.0")}),1.0]])]})])],"isStart":true})]}),makeQuery(id+"F20.opLoft","CAP_FACE",FACE,{"disambiguationData":[OSD([makeQuery(id+"F4.imprint","IMPRINT",FACE,{"disambiguationData":[TD([[makeQuery(id+"F4.imprint","IMPRINT",EDGE,{"derivedFrom":sQuery(id+"F4.wireOp",EDGE,"E26.1.0")}),1.0]])]})])],"isStart":true})]}),makeQuery(id+"F42.opRevolve","SWEPT_FACE",FACE,{"disambiguationData":[OSD([sQuery(id+"F41.wireOp",EDGE,"E32")])]})]});
            var Q4;
            Q4=makeQuery(id+"F42.boolean.opBoolean","INTERSECT",EDGE,{"disambiguationData":[OD(1.0)],"derivedFrom":[makeQuery(id+"F20.boolean.opBoolean","MERGE",FACE,{"derivedFrom":[makeQuery(id+"F19.boolean.opBoolean","MERGE",FACE,{"derivedFrom":[makeQuery(id+"F18.boolean.opBoolean","MERGE",FACE,{"derivedFrom":[makeQuery(id+"F17.boolean.opBoolean","MERGE",FACE,{"derivedFrom":[makeQuery(id+"F16.boolean.opBoolean","MERGE",FACE,{"derivedFrom":[makeQuery(id+"F15.boolean.opBoolean","MERGE",FACE,{"derivedFrom":[makeQuery(id+"F14.boolean.opBoolean","MERGE",FACE,{"derivedFrom":[makeQuery(id+"F13.boolean.opBoolean","MERGE",FACE,{"derivedFrom":[makeQuery(id+"F12.boolean.opBoolean","MERGE",FACE,{"derivedFrom":[makeQuery(id+"F11.boolean.opBoolean","MERGE",FACE,{"derivedFrom":[makeQuery(id+"F10.boolean.opBoolean","MERGE",FACE,{"derivedFrom":[makeQuery(id+"F9.boolean.opBoolean","MERGE",FACE,{"derivedFrom":[makeQuery(id+"F8.boolean.opBoolean","MERGE",FACE,{"derivedFrom":[makeQuery(id+"F7.boolean.opBoolean","MERGE",FACE,{"derivedFrom":[makeQuery(id+"F6.boolean.opBoolean","MERGE",FACE,{"derivedFrom":[makeQuery(id+"F5.boolean.opBoolean","MERGE",FACE,{"derivedFrom":[makeQuery(id+"F1.opRevolve","SWEPT_FACE",FACE,{"disambiguationData":[OSD([sQuery(id+"F0.wireOp",EDGE,"E14")])]}),makeQuery(id+"F5.opLoft","CAP_FACE",FACE,{"disambiguationData":[OSD([makeQuery(id+"F4.imprint","IMPRINT",FACE,{"disambiguationData":[TD([[makeQuery(id+"F4.imprint","IMPRINT",EDGE,{"derivedFrom":sQuery(id+"F4.wireOp",EDGE,"E21")}),1.0]])]})])],"isStart":true})]}),makeQuery(id+"F6.opLoft","CAP_FACE",FACE,{"disambiguationData":[OSD([makeQuery(id+"F4.imprint","IMPRINT",FACE,{"disambiguationData":[TD([[makeQuery(id+"F4.imprint","IMPRINT",EDGE,{"derivedFrom":sQuery(id+"F4.wireOp",EDGE,"E26.15.0")}),1.0]])]})])],"isStart":true})]}),makeQuery(id+"F7.opLoft","CAP_FACE",FACE,{"disambiguationData":[OSD([makeQuery(id+"F4.imprint","IMPRINT",FACE,{"disambiguationData":[TD([[makeQuery(id+"F4.imprint","IMPRINT",EDGE,{"derivedFrom":sQuery(id+"F4.wireOp",EDGE,"E26.14.0")}),1.0]])]})])],"isStart":true})]}),makeQuery(id+"F8.opLoft","CAP_FACE",FACE,{"disambiguationData":[OSD([makeQuery(id+"F4.imprint","IMPRINT",FACE,{"disambiguationData":[TD([[makeQuery(id+"F4.imprint","IMPRINT",EDGE,{"derivedFrom":sQuery(id+"F4.wireOp",EDGE,"E26.13.0")}),1.0]])]})])],"isStart":true})]}),makeQuery(id+"F9.opLoft","CAP_FACE",FACE,{"disambiguationData":[OSD([makeQuery(id+"F4.imprint","IMPRINT",FACE,{"disambiguationData":[TD([[makeQuery(id+"F4.imprint","IMPRINT",EDGE,{"derivedFrom":sQuery(id+"F4.wireOp",EDGE,"E26.12.0")}),1.0]])]})])],"isStart":true})]}),makeQuery(id+"F10.opLoft","CAP_FACE",FACE,{"disambiguationData":[OSD([makeQuery(id+"F4.imprint","IMPRINT",FACE,{"disambiguationData":[TD([[makeQuery(id+"F4.imprint","IMPRINT",EDGE,{"derivedFrom":sQuery(id+"F4.wireOp",EDGE,"E26.11.0")}),1.0]])]})])],"isStart":true})]}),makeQuery(id+"F11.opLoft","CAP_FACE",FACE,{"disambiguationData":[OSD([makeQuery(id+"F4.imprint","IMPRINT",FACE,{"disambiguationData":[TD([[makeQuery(id+"F4.imprint","IMPRINT",EDGE,{"derivedFrom":sQuery(id+"F4.wireOp",EDGE,"E26.10.0")}),1.0]])]})])],"isStart":true})]}),makeQuery(id+"F12.opLoft","CAP_FACE",FACE,{"disambiguationData":[OSD([makeQuery(id+"F4.imprint","IMPRINT",FACE,{"disambiguationData":[TD([[makeQuery(id+"F4.imprint","IMPRINT",EDGE,{"derivedFrom":sQuery(id+"F4.wireOp",EDGE,"E26.9.0")}),1.0]])]})])],"isStart":true})]}),makeQuery(id+"F13.opLoft","CAP_FACE",FACE,{"disambiguationData":[OSD([makeQuery(id+"F4.imprint","IMPRINT",FACE,{"disambiguationData":[TD([[makeQuery(id+"F4.imprint","IMPRINT",EDGE,{"derivedFrom":sQuery(id+"F4.wireOp",EDGE,"E26.8.0")}),1.0]])]})])],"isStart":true})]}),makeQuery(id+"F14.opLoft","CAP_FACE",FACE,{"disambiguationData":[OSD([makeQuery(id+"F4.imprint","IMPRINT",FACE,{"disambiguationData":[TD([[makeQuery(id+"F4.imprint","IMPRINT",EDGE,{"derivedFrom":sQuery(id+"F4.wireOp",EDGE,"E26.7.0")}),1.0]])]})])],"isStart":true})]}),makeQuery(id+"F15.opLoft","CAP_FACE",FACE,{"disambiguationData":[OSD([makeQuery(id+"F4.imprint","IMPRINT",FACE,{"disambiguationData":[TD([[makeQuery(id+"F4.imprint","IMPRINT",EDGE,{"derivedFrom":sQuery(id+"F4.wireOp",EDGE,"E26.6.0")}),1.0]])]})])],"isStart":true})]}),makeQuery(id+"F16.opLoft","CAP_FACE",FACE,{"disambiguationData":[OSD([makeQuery(id+"F4.imprint","IMPRINT",FACE,{"disambiguationData":[TD([[makeQuery(id+"F4.imprint","IMPRINT",EDGE,{"derivedFrom":sQuery(id+"F4.wireOp",EDGE,"E26.5.0")}),1.0]])]})])],"isStart":true})]}),makeQuery(id+"F17.opLoft","CAP_FACE",FACE,{"disambiguationData":[OSD([makeQuery(id+"F4.imprint","IMPRINT",FACE,{"disambiguationData":[TD([[makeQuery(id+"F4.imprint","IMPRINT",EDGE,{"derivedFrom":sQuery(id+"F4.wireOp",EDGE,"E26.4.0")}),1.0]])]})])],"isStart":true})]}),makeQuery(id+"F18.opLoft","CAP_FACE",FACE,{"disambiguationData":[OSD([makeQuery(id+"F4.imprint","IMPRINT",FACE,{"disambiguationData":[TD([[makeQuery(id+"F4.imprint","IMPRINT",EDGE,{"derivedFrom":sQuery(id+"F4.wireOp",EDGE,"E26.3.0")}),1.0]])]})])],"isStart":true})]}),makeQuery(id+"F19.opLoft","CAP_FACE",FACE,{"disambiguationData":[OSD([makeQuery(id+"F4.imprint","IMPRINT",FACE,{"disambiguationData":[TD([[makeQuery(id+"F4.imprint","IMPRINT",EDGE,{"derivedFrom":sQuery(id+"F4.wireOp",EDGE,"E26.2.0")}),1.0]])]})])],"isStart":true})]}),makeQuery(id+"F20.opLoft","CAP_FACE",FACE,{"disambiguationData":[OSD([makeQuery(id+"F4.imprint","IMPRINT",FACE,{"disambiguationData":[TD([[makeQuery(id+"F4.imprint","IMPRINT",EDGE,{"derivedFrom":sQuery(id+"F4.wireOp",EDGE,"E26.1.0")}),1.0]])]})])],"isStart":true})]}),makeQuery(id+"F42.opRevolve","SWEPT_FACE",FACE,{"disambiguationData":[OSD([sQuery(id+"F41.wireOp",EDGE,"E32")])]})]});
            var Q5;
            Q5=makeQuery(id+"F42.boolean.opBoolean","INTERSECT",EDGE,{"disambiguationData":[OD(0.0)],"derivedFrom":[makeQuery(id+"F20.boolean.opBoolean","MERGE",FACE,{"derivedFrom":[makeQuery(id+"F19.boolean.opBoolean","MERGE",FACE,{"derivedFrom":[makeQuery(id+"F18.boolean.opBoolean","MERGE",FACE,{"derivedFrom":[makeQuery(id+"F17.boolean.opBoolean","MERGE",FACE,{"derivedFrom":[makeQuery(id+"F16.boolean.opBoolean","MERGE",FACE,{"derivedFrom":[makeQuery(id+"F15.boolean.opBoolean","MERGE",FACE,{"derivedFrom":[makeQuery(id+"F14.boolean.opBoolean","MERGE",FACE,{"derivedFrom":[makeQuery(id+"F13.boolean.opBoolean","MERGE",FACE,{"derivedFrom":[makeQuery(id+"F12.boolean.opBoolean","MERGE",FACE,{"derivedFrom":[makeQuery(id+"F11.boolean.opBoolean","MERGE",FACE,{"derivedFrom":[makeQuery(id+"F10.boolean.opBoolean","MERGE",FACE,{"derivedFrom":[makeQuery(id+"F9.boolean.opBoolean","MERGE",FACE,{"derivedFrom":[makeQuery(id+"F8.boolean.opBoolean","MERGE",FACE,{"derivedFrom":[makeQuery(id+"F7.boolean.opBoolean","MERGE",FACE,{"derivedFrom":[makeQuery(id+"F6.boolean.opBoolean","MERGE",FACE,{"derivedFrom":[makeQuery(id+"F5.boolean.opBoolean","MERGE",FACE,{"derivedFrom":[makeQuery(id+"F1.opRevolve","SWEPT_FACE",FACE,{"disambiguationData":[OSD([sQuery(id+"F0.wireOp",EDGE,"E14")])]}),makeQuery(id+"F5.opLoft","CAP_FACE",FACE,{"disambiguationData":[OSD([makeQuery(id+"F4.imprint","IMPRINT",FACE,{"disambiguationData":[TD([[makeQuery(id+"F4.imprint","IMPRINT",EDGE,{"derivedFrom":sQuery(id+"F4.wireOp",EDGE,"E21")}),1.0]])]})])],"isStart":true})]}),makeQuery(id+"F6.opLoft","CAP_FACE",FACE,{"disambiguationData":[OSD([makeQuery(id+"F4.imprint","IMPRINT",FACE,{"disambiguationData":[TD([[makeQuery(id+"F4.imprint","IMPRINT",EDGE,{"derivedFrom":sQuery(id+"F4.wireOp",EDGE,"E26.15.0")}),1.0]])]})])],"isStart":true})]}),makeQuery(id+"F7.opLoft","CAP_FACE",FACE,{"disambiguationData":[OSD([makeQuery(id+"F4.imprint","IMPRINT",FACE,{"disambiguationData":[TD([[makeQuery(id+"F4.imprint","IMPRINT",EDGE,{"derivedFrom":sQuery(id+"F4.wireOp",EDGE,"E26.14.0")}),1.0]])]})])],"isStart":true})]}),makeQuery(id+"F8.opLoft","CAP_FACE",FACE,{"disambiguationData":[OSD([makeQuery(id+"F4.imprint","IMPRINT",FACE,{"disambiguationData":[TD([[makeQuery(id+"F4.imprint","IMPRINT",EDGE,{"derivedFrom":sQuery(id+"F4.wireOp",EDGE,"E26.13.0")}),1.0]])]})])],"isStart":true})]}),makeQuery(id+"F9.opLoft","CAP_FACE",FACE,{"disambiguationData":[OSD([makeQuery(id+"F4.imprint","IMPRINT",FACE,{"disambiguationData":[TD([[makeQuery(id+"F4.imprint","IMPRINT",EDGE,{"derivedFrom":sQuery(id+"F4.wireOp",EDGE,"E26.12.0")}),1.0]])]})])],"isStart":true})]}),makeQuery(id+"F10.opLoft","CAP_FACE",FACE,{"disambiguationData":[OSD([makeQuery(id+"F4.imprint","IMPRINT",FACE,{"disambiguationData":[TD([[makeQuery(id+"F4.imprint","IMPRINT",EDGE,{"derivedFrom":sQuery(id+"F4.wireOp",EDGE,"E26.11.0")}),1.0]])]})])],"isStart":true})]}),makeQuery(id+"F11.opLoft","CAP_FACE",FACE,{"disambiguationData":[OSD([makeQuery(id+"F4.imprint","IMPRINT",FACE,{"disambiguationData":[TD([[makeQuery(id+"F4.imprint","IMPRINT",EDGE,{"derivedFrom":sQuery(id+"F4.wireOp",EDGE,"E26.10.0")}),1.0]])]})])],"isStart":true})]}),makeQuery(id+"F12.opLoft","CAP_FACE",FACE,{"disambiguationData":[OSD([makeQuery(id+"F4.imprint","IMPRINT",FACE,{"disambiguationData":[TD([[makeQuery(id+"F4.imprint","IMPRINT",EDGE,{"derivedFrom":sQuery(id+"F4.wireOp",EDGE,"E26.9.0")}),1.0]])]})])],"isStart":true})]}),makeQuery(id+"F13.opLoft","CAP_FACE",FACE,{"disambiguationData":[OSD([makeQuery(id+"F4.imprint","IMPRINT",FACE,{"disambiguationData":[TD([[makeQuery(id+"F4.imprint","IMPRINT",EDGE,{"derivedFrom":sQuery(id+"F4.wireOp",EDGE,"E26.8.0")}),1.0]])]})])],"isStart":true})]}),makeQuery(id+"F14.opLoft","CAP_FACE",FACE,{"disambiguationData":[OSD([makeQuery(id+"F4.imprint","IMPRINT",FACE,{"disambiguationData":[TD([[makeQuery(id+"F4.imprint","IMPRINT",EDGE,{"derivedFrom":sQuery(id+"F4.wireOp",EDGE,"E26.7.0")}),1.0]])]})])],"isStart":true})]}),makeQuery(id+"F15.opLoft","CAP_FACE",FACE,{"disambiguationData":[OSD([makeQuery(id+"F4.imprint","IMPRINT",FACE,{"disambiguationData":[TD([[makeQuery(id+"F4.imprint","IMPRINT",EDGE,{"derivedFrom":sQuery(id+"F4.wireOp",EDGE,"E26.6.0")}),1.0]])]})])],"isStart":true})]}),makeQuery(id+"F16.opLoft","CAP_FACE",FACE,{"disambiguationData":[OSD([makeQuery(id+"F4.imprint","IMPRINT",FACE,{"disambiguationData":[TD([[makeQuery(id+"F4.imprint","IMPRINT",EDGE,{"derivedFrom":sQuery(id+"F4.wireOp",EDGE,"E26.5.0")}),1.0]])]})])],"isStart":true})]}),makeQuery(id+"F17.opLoft","CAP_FACE",FACE,{"disambiguationData":[OSD([makeQuery(id+"F4.imprint","IMPRINT",FACE,{"disambiguationData":[TD([[makeQuery(id+"F4.imprint","IMPRINT",EDGE,{"derivedFrom":sQuery(id+"F4.wireOp",EDGE,"E26.4.0")}),1.0]])]})])],"isStart":true})]}),makeQuery(id+"F18.opLoft","CAP_FACE",FACE,{"disambiguationData":[OSD([makeQuery(id+"F4.imprint","IMPRINT",FACE,{"disambiguationData":[TD([[makeQuery(id+"F4.imprint","IMPRINT",EDGE,{"derivedFrom":sQuery(id+"F4.wireOp",EDGE,"E26.3.0")}),1.0]])]})])],"isStart":true})]}),makeQuery(id+"F19.opLoft","CAP_FACE",FACE,{"disambiguationData":[OSD([makeQuery(id+"F4.imprint","IMPRINT",FACE,{"disambiguationData":[TD([[makeQuery(id+"F4.imprint","IMPRINT",EDGE,{"derivedFrom":sQuery(id+"F4.wireOp",EDGE,"E26.2.0")}),1.0]])]})])],"isStart":true})]}),makeQuery(id+"F20.opLoft","CAP_FACE",FACE,{"disambiguationData":[OSD([makeQuery(id+"F4.imprint","IMPRINT",FACE,{"disambiguationData":[TD([[makeQuery(id+"F4.imprint","IMPRINT",EDGE,{"derivedFrom":sQuery(id+"F4.wireOp",EDGE,"E26.1.0")}),1.0]])]})])],"isStart":true})]}),makeQuery(id+"F42.opRevolve","SWEPT_FACE",FACE,{"disambiguationData":[OSD([sQuery(id+"F41.wireOp",EDGE,"E32")])]})]});
            var Q6;
            Q6=makeQuery(id+"F42.boolean.opBoolean","INTERSECT",EDGE,{"disambiguationData":[OD(15.0)],"derivedFrom":[makeQuery(id+"F20.boolean.opBoolean","MERGE",FACE,{"derivedFrom":[makeQuery(id+"F19.boolean.opBoolean","MERGE",FACE,{"derivedFrom":[makeQuery(id+"F18.boolean.opBoolean","MERGE",FACE,{"derivedFrom":[makeQuery(id+"F17.boolean.opBoolean","MERGE",FACE,{"derivedFrom":[makeQuery(id+"F16.boolean.opBoolean","MERGE",FACE,{"derivedFrom":[makeQuery(id+"F15.boolean.opBoolean","MERGE",FACE,{"derivedFrom":[makeQuery(id+"F14.boolean.opBoolean","MERGE",FACE,{"derivedFrom":[makeQuery(id+"F13.boolean.opBoolean","MERGE",FACE,{"derivedFrom":[makeQuery(id+"F12.boolean.opBoolean","MERGE",FACE,{"derivedFrom":[makeQuery(id+"F11.boolean.opBoolean","MERGE",FACE,{"derivedFrom":[makeQuery(id+"F10.boolean.opBoolean","MERGE",FACE,{"derivedFrom":[makeQuery(id+"F9.boolean.opBoolean","MERGE",FACE,{"derivedFrom":[makeQuery(id+"F8.boolean.opBoolean","MERGE",FACE,{"derivedFrom":[makeQuery(id+"F7.boolean.opBoolean","MERGE",FACE,{"derivedFrom":[makeQuery(id+"F6.boolean.opBoolean","MERGE",FACE,{"derivedFrom":[makeQuery(id+"F5.boolean.opBoolean","MERGE",FACE,{"derivedFrom":[makeQuery(id+"F1.opRevolve","SWEPT_FACE",FACE,{"disambiguationData":[OSD([sQuery(id+"F0.wireOp",EDGE,"E14")])]}),makeQuery(id+"F5.opLoft","CAP_FACE",FACE,{"disambiguationData":[OSD([makeQuery(id+"F4.imprint","IMPRINT",FACE,{"disambiguationData":[TD([[makeQuery(id+"F4.imprint","IMPRINT",EDGE,{"derivedFrom":sQuery(id+"F4.wireOp",EDGE,"E21")}),1.0]])]})])],"isStart":true})]}),makeQuery(id+"F6.opLoft","CAP_FACE",FACE,{"disambiguationData":[OSD([makeQuery(id+"F4.imprint","IMPRINT",FACE,{"disambiguationData":[TD([[makeQuery(id+"F4.imprint","IMPRINT",EDGE,{"derivedFrom":sQuery(id+"F4.wireOp",EDGE,"E26.15.0")}),1.0]])]})])],"isStart":true})]}),makeQuery(id+"F7.opLoft","CAP_FACE",FACE,{"disambiguationData":[OSD([makeQuery(id+"F4.imprint","IMPRINT",FACE,{"disambiguationData":[TD([[makeQuery(id+"F4.imprint","IMPRINT",EDGE,{"derivedFrom":sQuery(id+"F4.wireOp",EDGE,"E26.14.0")}),1.0]])]})])],"isStart":true})]}),makeQuery(id+"F8.opLoft","CAP_FACE",FACE,{"disambiguationData":[OSD([makeQuery(id+"F4.imprint","IMPRINT",FACE,{"disambiguationData":[TD([[makeQuery(id+"F4.imprint","IMPRINT",EDGE,{"derivedFrom":sQuery(id+"F4.wireOp",EDGE,"E26.13.0")}),1.0]])]})])],"isStart":true})]}),makeQuery(id+"F9.opLoft","CAP_FACE",FACE,{"disambiguationData":[OSD([makeQuery(id+"F4.imprint","IMPRINT",FACE,{"disambiguationData":[TD([[makeQuery(id+"F4.imprint","IMPRINT",EDGE,{"derivedFrom":sQuery(id+"F4.wireOp",EDGE,"E26.12.0")}),1.0]])]})])],"isStart":true})]}),makeQuery(id+"F10.opLoft","CAP_FACE",FACE,{"disambiguationData":[OSD([makeQuery(id+"F4.imprint","IMPRINT",FACE,{"disambiguationData":[TD([[makeQuery(id+"F4.imprint","IMPRINT",EDGE,{"derivedFrom":sQuery(id+"F4.wireOp",EDGE,"E26.11.0")}),1.0]])]})])],"isStart":true})]}),makeQuery(id+"F11.opLoft","CAP_FACE",FACE,{"disambiguationData":[OSD([makeQuery(id+"F4.imprint","IMPRINT",FACE,{"disambiguationData":[TD([[makeQuery(id+"F4.imprint","IMPRINT",EDGE,{"derivedFrom":sQuery(id+"F4.wireOp",EDGE,"E26.10.0")}),1.0]])]})])],"isStart":true})]}),makeQuery(id+"F12.opLoft","CAP_FACE",FACE,{"disambiguationData":[OSD([makeQuery(id+"F4.imprint","IMPRINT",FACE,{"disambiguationData":[TD([[makeQuery(id+"F4.imprint","IMPRINT",EDGE,{"derivedFrom":sQuery(id+"F4.wireOp",EDGE,"E26.9.0")}),1.0]])]})])],"isStart":true})]}),makeQuery(id+"F13.opLoft","CAP_FACE",FACE,{"disambiguationData":[OSD([makeQuery(id+"F4.imprint","IMPRINT",FACE,{"disambiguationData":[TD([[makeQuery(id+"F4.imprint","IMPRINT",EDGE,{"derivedFrom":sQuery(id+"F4.wireOp",EDGE,"E26.8.0")}),1.0]])]})])],"isStart":true})]}),makeQuery(id+"F14.opLoft","CAP_FACE",FACE,{"disambiguationData":[OSD([makeQuery(id+"F4.imprint","IMPRINT",FACE,{"disambiguationData":[TD([[makeQuery(id+"F4.imprint","IMPRINT",EDGE,{"derivedFrom":sQuery(id+"F4.wireOp",EDGE,"E26.7.0")}),1.0]])]})])],"isStart":true})]}),makeQuery(id+"F15.opLoft","CAP_FACE",FACE,{"disambiguationData":[OSD([makeQuery(id+"F4.imprint","IMPRINT",FACE,{"disambiguationData":[TD([[makeQuery(id+"F4.imprint","IMPRINT",EDGE,{"derivedFrom":sQuery(id+"F4.wireOp",EDGE,"E26.6.0")}),1.0]])]})])],"isStart":true})]}),makeQuery(id+"F16.opLoft","CAP_FACE",FACE,{"disambiguationData":[OSD([makeQuery(id+"F4.imprint","IMPRINT",FACE,{"disambiguationData":[TD([[makeQuery(id+"F4.imprint","IMPRINT",EDGE,{"derivedFrom":sQuery(id+"F4.wireOp",EDGE,"E26.5.0")}),1.0]])]})])],"isStart":true})]}),makeQuery(id+"F17.opLoft","CAP_FACE",FACE,{"disambiguationData":[OSD([makeQuery(id+"F4.imprint","IMPRINT",FACE,{"disambiguationData":[TD([[makeQuery(id+"F4.imprint","IMPRINT",EDGE,{"derivedFrom":sQuery(id+"F4.wireOp",EDGE,"E26.4.0")}),1.0]])]})])],"isStart":true})]}),makeQuery(id+"F18.opLoft","CAP_FACE",FACE,{"disambiguationData":[OSD([makeQuery(id+"F4.imprint","IMPRINT",FACE,{"disambiguationData":[TD([[makeQuery(id+"F4.imprint","IMPRINT",EDGE,{"derivedFrom":sQuery(id+"F4.wireOp",EDGE,"E26.3.0")}),1.0]])]})])],"isStart":true})]}),makeQuery(id+"F19.opLoft","CAP_FACE",FACE,{"disambiguationData":[OSD([makeQuery(id+"F4.imprint","IMPRINT",FACE,{"disambiguationData":[TD([[makeQuery(id+"F4.imprint","IMPRINT",EDGE,{"derivedFrom":sQuery(id+"F4.wireOp",EDGE,"E26.2.0")}),1.0]])]})])],"isStart":true})]}),makeQuery(id+"F20.opLoft","CAP_FACE",FACE,{"disambiguationData":[OSD([makeQuery(id+"F4.imprint","IMPRINT",FACE,{"disambiguationData":[TD([[makeQuery(id+"F4.imprint","IMPRINT",EDGE,{"derivedFrom":sQuery(id+"F4.wireOp",EDGE,"E26.1.0")}),1.0]])]})])],"isStart":true})]}),makeQuery(id+"F42.opRevolve","SWEPT_FACE",FACE,{"disambiguationData":[OSD([sQuery(id+"F41.wireOp",EDGE,"E32")])]})]});
            var Q7;
            Q7=makeQuery(id+"F42.boolean.opBoolean","INTERSECT",EDGE,{"disambiguationData":[OD(14.0)],"derivedFrom":[makeQuery(id+"F20.boolean.opBoolean","MERGE",FACE,{"derivedFrom":[makeQuery(id+"F19.boolean.opBoolean","MERGE",FACE,{"derivedFrom":[makeQuery(id+"F18.boolean.opBoolean","MERGE",FACE,{"derivedFrom":[makeQuery(id+"F17.boolean.opBoolean","MERGE",FACE,{"derivedFrom":[makeQuery(id+"F16.boolean.opBoolean","MERGE",FACE,{"derivedFrom":[makeQuery(id+"F15.boolean.opBoolean","MERGE",FACE,{"derivedFrom":[makeQuery(id+"F14.boolean.opBoolean","MERGE",FACE,{"derivedFrom":[makeQuery(id+"F13.boolean.opBoolean","MERGE",FACE,{"derivedFrom":[makeQuery(id+"F12.boolean.opBoolean","MERGE",FACE,{"derivedFrom":[makeQuery(id+"F11.boolean.opBoolean","MERGE",FACE,{"derivedFrom":[makeQuery(id+"F10.boolean.opBoolean","MERGE",FACE,{"derivedFrom":[makeQuery(id+"F9.boolean.opBoolean","MERGE",FACE,{"derivedFrom":[makeQuery(id+"F8.boolean.opBoolean","MERGE",FACE,{"derivedFrom":[makeQuery(id+"F7.boolean.opBoolean","MERGE",FACE,{"derivedFrom":[makeQuery(id+"F6.boolean.opBoolean","MERGE",FACE,{"derivedFrom":[makeQuery(id+"F5.boolean.opBoolean","MERGE",FACE,{"derivedFrom":[makeQuery(id+"F1.opRevolve","SWEPT_FACE",FACE,{"disambiguationData":[OSD([sQuery(id+"F0.wireOp",EDGE,"E14")])]}),makeQuery(id+"F5.opLoft","CAP_FACE",FACE,{"disambiguationData":[OSD([makeQuery(id+"F4.imprint","IMPRINT",FACE,{"disambiguationData":[TD([[makeQuery(id+"F4.imprint","IMPRINT",EDGE,{"derivedFrom":sQuery(id+"F4.wireOp",EDGE,"E21")}),1.0]])]})])],"isStart":true})]}),makeQuery(id+"F6.opLoft","CAP_FACE",FACE,{"disambiguationData":[OSD([makeQuery(id+"F4.imprint","IMPRINT",FACE,{"disambiguationData":[TD([[makeQuery(id+"F4.imprint","IMPRINT",EDGE,{"derivedFrom":sQuery(id+"F4.wireOp",EDGE,"E26.15.0")}),1.0]])]})])],"isStart":true})]}),makeQuery(id+"F7.opLoft","CAP_FACE",FACE,{"disambiguationData":[OSD([makeQuery(id+"F4.imprint","IMPRINT",FACE,{"disambiguationData":[TD([[makeQuery(id+"F4.imprint","IMPRINT",EDGE,{"derivedFrom":sQuery(id+"F4.wireOp",EDGE,"E26.14.0")}),1.0]])]})])],"isStart":true})]}),makeQuery(id+"F8.opLoft","CAP_FACE",FACE,{"disambiguationData":[OSD([makeQuery(id+"F4.imprint","IMPRINT",FACE,{"disambiguationData":[TD([[makeQuery(id+"F4.imprint","IMPRINT",EDGE,{"derivedFrom":sQuery(id+"F4.wireOp",EDGE,"E26.13.0")}),1.0]])]})])],"isStart":true})]}),makeQuery(id+"F9.opLoft","CAP_FACE",FACE,{"disambiguationData":[OSD([makeQuery(id+"F4.imprint","IMPRINT",FACE,{"disambiguationData":[TD([[makeQuery(id+"F4.imprint","IMPRINT",EDGE,{"derivedFrom":sQuery(id+"F4.wireOp",EDGE,"E26.12.0")}),1.0]])]})])],"isStart":true})]}),makeQuery(id+"F10.opLoft","CAP_FACE",FACE,{"disambiguationData":[OSD([makeQuery(id+"F4.imprint","IMPRINT",FACE,{"disambiguationData":[TD([[makeQuery(id+"F4.imprint","IMPRINT",EDGE,{"derivedFrom":sQuery(id+"F4.wireOp",EDGE,"E26.11.0")}),1.0]])]})])],"isStart":true})]}),makeQuery(id+"F11.opLoft","CAP_FACE",FACE,{"disambiguationData":[OSD([makeQuery(id+"F4.imprint","IMPRINT",FACE,{"disambiguationData":[TD([[makeQuery(id+"F4.imprint","IMPRINT",EDGE,{"derivedFrom":sQuery(id+"F4.wireOp",EDGE,"E26.10.0")}),1.0]])]})])],"isStart":true})]}),makeQuery(id+"F12.opLoft","CAP_FACE",FACE,{"disambiguationData":[OSD([makeQuery(id+"F4.imprint","IMPRINT",FACE,{"disambiguationData":[TD([[makeQuery(id+"F4.imprint","IMPRINT",EDGE,{"derivedFrom":sQuery(id+"F4.wireOp",EDGE,"E26.9.0")}),1.0]])]})])],"isStart":true})]}),makeQuery(id+"F13.opLoft","CAP_FACE",FACE,{"disambiguationData":[OSD([makeQuery(id+"F4.imprint","IMPRINT",FACE,{"disambiguationData":[TD([[makeQuery(id+"F4.imprint","IMPRINT",EDGE,{"derivedFrom":sQuery(id+"F4.wireOp",EDGE,"E26.8.0")}),1.0]])]})])],"isStart":true})]}),makeQuery(id+"F14.opLoft","CAP_FACE",FACE,{"disambiguationData":[OSD([makeQuery(id+"F4.imprint","IMPRINT",FACE,{"disambiguationData":[TD([[makeQuery(id+"F4.imprint","IMPRINT",EDGE,{"derivedFrom":sQuery(id+"F4.wireOp",EDGE,"E26.7.0")}),1.0]])]})])],"isStart":true})]}),makeQuery(id+"F15.opLoft","CAP_FACE",FACE,{"disambiguationData":[OSD([makeQuery(id+"F4.imprint","IMPRINT",FACE,{"disambiguationData":[TD([[makeQuery(id+"F4.imprint","IMPRINT",EDGE,{"derivedFrom":sQuery(id+"F4.wireOp",EDGE,"E26.6.0")}),1.0]])]})])],"isStart":true})]}),makeQuery(id+"F16.opLoft","CAP_FACE",FACE,{"disambiguationData":[OSD([makeQuery(id+"F4.imprint","IMPRINT",FACE,{"disambiguationData":[TD([[makeQuery(id+"F4.imprint","IMPRINT",EDGE,{"derivedFrom":sQuery(id+"F4.wireOp",EDGE,"E26.5.0")}),1.0]])]})])],"isStart":true})]}),makeQuery(id+"F17.opLoft","CAP_FACE",FACE,{"disambiguationData":[OSD([makeQuery(id+"F4.imprint","IMPRINT",FACE,{"disambiguationData":[TD([[makeQuery(id+"F4.imprint","IMPRINT",EDGE,{"derivedFrom":sQuery(id+"F4.wireOp",EDGE,"E26.4.0")}),1.0]])]})])],"isStart":true})]}),makeQuery(id+"F18.opLoft","CAP_FACE",FACE,{"disambiguationData":[OSD([makeQuery(id+"F4.imprint","IMPRINT",FACE,{"disambiguationData":[TD([[makeQuery(id+"F4.imprint","IMPRINT",EDGE,{"derivedFrom":sQuery(id+"F4.wireOp",EDGE,"E26.3.0")}),1.0]])]})])],"isStart":true})]}),makeQuery(id+"F19.opLoft","CAP_FACE",FACE,{"disambiguationData":[OSD([makeQuery(id+"F4.imprint","IMPRINT",FACE,{"disambiguationData":[TD([[makeQuery(id+"F4.imprint","IMPRINT",EDGE,{"derivedFrom":sQuery(id+"F4.wireOp",EDGE,"E26.2.0")}),1.0]])]})])],"isStart":true})]}),makeQuery(id+"F20.opLoft","CAP_FACE",FACE,{"disambiguationData":[OSD([makeQuery(id+"F4.imprint","IMPRINT",FACE,{"disambiguationData":[TD([[makeQuery(id+"F4.imprint","IMPRINT",EDGE,{"derivedFrom":sQuery(id+"F4.wireOp",EDGE,"E26.1.0")}),1.0]])]})])],"isStart":true})]}),makeQuery(id+"F42.opRevolve","SWEPT_FACE",FACE,{"disambiguationData":[OSD([sQuery(id+"F41.wireOp",EDGE,"E32")])]})]});
            var Q8;
            Q8=makeQuery(id+"F42.boolean.opBoolean","INTERSECT",EDGE,{"disambiguationData":[OD(13.0)],"derivedFrom":[makeQuery(id+"F20.boolean.opBoolean","MERGE",FACE,{"derivedFrom":[makeQuery(id+"F19.boolean.opBoolean","MERGE",FACE,{"derivedFrom":[makeQuery(id+"F18.boolean.opBoolean","MERGE",FACE,{"derivedFrom":[makeQuery(id+"F17.boolean.opBoolean","MERGE",FACE,{"derivedFrom":[makeQuery(id+"F16.boolean.opBoolean","MERGE",FACE,{"derivedFrom":[makeQuery(id+"F15.boolean.opBoolean","MERGE",FACE,{"derivedFrom":[makeQuery(id+"F14.boolean.opBoolean","MERGE",FACE,{"derivedFrom":[makeQuery(id+"F13.boolean.opBoolean","MERGE",FACE,{"derivedFrom":[makeQuery(id+"F12.boolean.opBoolean","MERGE",FACE,{"derivedFrom":[makeQuery(id+"F11.boolean.opBoolean","MERGE",FACE,{"derivedFrom":[makeQuery(id+"F10.boolean.opBoolean","MERGE",FACE,{"derivedFrom":[makeQuery(id+"F9.boolean.opBoolean","MERGE",FACE,{"derivedFrom":[makeQuery(id+"F8.boolean.opBoolean","MERGE",FACE,{"derivedFrom":[makeQuery(id+"F7.boolean.opBoolean","MERGE",FACE,{"derivedFrom":[makeQuery(id+"F6.boolean.opBoolean","MERGE",FACE,{"derivedFrom":[makeQuery(id+"F5.boolean.opBoolean","MERGE",FACE,{"derivedFrom":[makeQuery(id+"F1.opRevolve","SWEPT_FACE",FACE,{"disambiguationData":[OSD([sQuery(id+"F0.wireOp",EDGE,"E14")])]}),makeQuery(id+"F5.opLoft","CAP_FACE",FACE,{"disambiguationData":[OSD([makeQuery(id+"F4.imprint","IMPRINT",FACE,{"disambiguationData":[TD([[makeQuery(id+"F4.imprint","IMPRINT",EDGE,{"derivedFrom":sQuery(id+"F4.wireOp",EDGE,"E21")}),1.0]])]})])],"isStart":true})]}),makeQuery(id+"F6.opLoft","CAP_FACE",FACE,{"disambiguationData":[OSD([makeQuery(id+"F4.imprint","IMPRINT",FACE,{"disambiguationData":[TD([[makeQuery(id+"F4.imprint","IMPRINT",EDGE,{"derivedFrom":sQuery(id+"F4.wireOp",EDGE,"E26.15.0")}),1.0]])]})])],"isStart":true})]}),makeQuery(id+"F7.opLoft","CAP_FACE",FACE,{"disambiguationData":[OSD([makeQuery(id+"F4.imprint","IMPRINT",FACE,{"disambiguationData":[TD([[makeQuery(id+"F4.imprint","IMPRINT",EDGE,{"derivedFrom":sQuery(id+"F4.wireOp",EDGE,"E26.14.0")}),1.0]])]})])],"isStart":true})]}),makeQuery(id+"F8.opLoft","CAP_FACE",FACE,{"disambiguationData":[OSD([makeQuery(id+"F4.imprint","IMPRINT",FACE,{"disambiguationData":[TD([[makeQuery(id+"F4.imprint","IMPRINT",EDGE,{"derivedFrom":sQuery(id+"F4.wireOp",EDGE,"E26.13.0")}),1.0]])]})])],"isStart":true})]}),makeQuery(id+"F9.opLoft","CAP_FACE",FACE,{"disambiguationData":[OSD([makeQuery(id+"F4.imprint","IMPRINT",FACE,{"disambiguationData":[TD([[makeQuery(id+"F4.imprint","IMPRINT",EDGE,{"derivedFrom":sQuery(id+"F4.wireOp",EDGE,"E26.12.0")}),1.0]])]})])],"isStart":true})]}),makeQuery(id+"F10.opLoft","CAP_FACE",FACE,{"disambiguationData":[OSD([makeQuery(id+"F4.imprint","IMPRINT",FACE,{"disambiguationData":[TD([[makeQuery(id+"F4.imprint","IMPRINT",EDGE,{"derivedFrom":sQuery(id+"F4.wireOp",EDGE,"E26.11.0")}),1.0]])]})])],"isStart":true})]}),makeQuery(id+"F11.opLoft","CAP_FACE",FACE,{"disambiguationData":[OSD([makeQuery(id+"F4.imprint","IMPRINT",FACE,{"disambiguationData":[TD([[makeQuery(id+"F4.imprint","IMPRINT",EDGE,{"derivedFrom":sQuery(id+"F4.wireOp",EDGE,"E26.10.0")}),1.0]])]})])],"isStart":true})]}),makeQuery(id+"F12.opLoft","CAP_FACE",FACE,{"disambiguationData":[OSD([makeQuery(id+"F4.imprint","IMPRINT",FACE,{"disambiguationData":[TD([[makeQuery(id+"F4.imprint","IMPRINT",EDGE,{"derivedFrom":sQuery(id+"F4.wireOp",EDGE,"E26.9.0")}),1.0]])]})])],"isStart":true})]}),makeQuery(id+"F13.opLoft","CAP_FACE",FACE,{"disambiguationData":[OSD([makeQuery(id+"F4.imprint","IMPRINT",FACE,{"disambiguationData":[TD([[makeQuery(id+"F4.imprint","IMPRINT",EDGE,{"derivedFrom":sQuery(id+"F4.wireOp",EDGE,"E26.8.0")}),1.0]])]})])],"isStart":true})]}),makeQuery(id+"F14.opLoft","CAP_FACE",FACE,{"disambiguationData":[OSD([makeQuery(id+"F4.imprint","IMPRINT",FACE,{"disambiguationData":[TD([[makeQuery(id+"F4.imprint","IMPRINT",EDGE,{"derivedFrom":sQuery(id+"F4.wireOp",EDGE,"E26.7.0")}),1.0]])]})])],"isStart":true})]}),makeQuery(id+"F15.opLoft","CAP_FACE",FACE,{"disambiguationData":[OSD([makeQuery(id+"F4.imprint","IMPRINT",FACE,{"disambiguationData":[TD([[makeQuery(id+"F4.imprint","IMPRINT",EDGE,{"derivedFrom":sQuery(id+"F4.wireOp",EDGE,"E26.6.0")}),1.0]])]})])],"isStart":true})]}),makeQuery(id+"F16.opLoft","CAP_FACE",FACE,{"disambiguationData":[OSD([makeQuery(id+"F4.imprint","IMPRINT",FACE,{"disambiguationData":[TD([[makeQuery(id+"F4.imprint","IMPRINT",EDGE,{"derivedFrom":sQuery(id+"F4.wireOp",EDGE,"E26.5.0")}),1.0]])]})])],"isStart":true})]}),makeQuery(id+"F17.opLoft","CAP_FACE",FACE,{"disambiguationData":[OSD([makeQuery(id+"F4.imprint","IMPRINT",FACE,{"disambiguationData":[TD([[makeQuery(id+"F4.imprint","IMPRINT",EDGE,{"derivedFrom":sQuery(id+"F4.wireOp",EDGE,"E26.4.0")}),1.0]])]})])],"isStart":true})]}),makeQuery(id+"F18.opLoft","CAP_FACE",FACE,{"disambiguationData":[OSD([makeQuery(id+"F4.imprint","IMPRINT",FACE,{"disambiguationData":[TD([[makeQuery(id+"F4.imprint","IMPRINT",EDGE,{"derivedFrom":sQuery(id+"F4.wireOp",EDGE,"E26.3.0")}),1.0]])]})])],"isStart":true})]}),makeQuery(id+"F19.opLoft","CAP_FACE",FACE,{"disambiguationData":[OSD([makeQuery(id+"F4.imprint","IMPRINT",FACE,{"disambiguationData":[TD([[makeQuery(id+"F4.imprint","IMPRINT",EDGE,{"derivedFrom":sQuery(id+"F4.wireOp",EDGE,"E26.2.0")}),1.0]])]})])],"isStart":true})]}),makeQuery(id+"F20.opLoft","CAP_FACE",FACE,{"disambiguationData":[OSD([makeQuery(id+"F4.imprint","IMPRINT",FACE,{"disambiguationData":[TD([[makeQuery(id+"F4.imprint","IMPRINT",EDGE,{"derivedFrom":sQuery(id+"F4.wireOp",EDGE,"E26.1.0")}),1.0]])]})])],"isStart":true})]}),makeQuery(id+"F42.opRevolve","SWEPT_FACE",FACE,{"disambiguationData":[OSD([sQuery(id+"F41.wireOp",EDGE,"E32")])]})]});
            var Q9;
            Q9=makeQuery(id+"F42.boolean.opBoolean","INTERSECT",EDGE,{"disambiguationData":[OD(12.0)],"derivedFrom":[makeQuery(id+"F20.boolean.opBoolean","MERGE",FACE,{"derivedFrom":[makeQuery(id+"F19.boolean.opBoolean","MERGE",FACE,{"derivedFrom":[makeQuery(id+"F18.boolean.opBoolean","MERGE",FACE,{"derivedFrom":[makeQuery(id+"F17.boolean.opBoolean","MERGE",FACE,{"derivedFrom":[makeQuery(id+"F16.boolean.opBoolean","MERGE",FACE,{"derivedFrom":[makeQuery(id+"F15.boolean.opBoolean","MERGE",FACE,{"derivedFrom":[makeQuery(id+"F14.boolean.opBoolean","MERGE",FACE,{"derivedFrom":[makeQuery(id+"F13.boolean.opBoolean","MERGE",FACE,{"derivedFrom":[makeQuery(id+"F12.boolean.opBoolean","MERGE",FACE,{"derivedFrom":[makeQuery(id+"F11.boolean.opBoolean","MERGE",FACE,{"derivedFrom":[makeQuery(id+"F10.boolean.opBoolean","MERGE",FACE,{"derivedFrom":[makeQuery(id+"F9.boolean.opBoolean","MERGE",FACE,{"derivedFrom":[makeQuery(id+"F8.boolean.opBoolean","MERGE",FACE,{"derivedFrom":[makeQuery(id+"F7.boolean.opBoolean","MERGE",FACE,{"derivedFrom":[makeQuery(id+"F6.boolean.opBoolean","MERGE",FACE,{"derivedFrom":[makeQuery(id+"F5.boolean.opBoolean","MERGE",FACE,{"derivedFrom":[makeQuery(id+"F1.opRevolve","SWEPT_FACE",FACE,{"disambiguationData":[OSD([sQuery(id+"F0.wireOp",EDGE,"E14")])]}),makeQuery(id+"F5.opLoft","CAP_FACE",FACE,{"disambiguationData":[OSD([makeQuery(id+"F4.imprint","IMPRINT",FACE,{"disambiguationData":[TD([[makeQuery(id+"F4.imprint","IMPRINT",EDGE,{"derivedFrom":sQuery(id+"F4.wireOp",EDGE,"E21")}),1.0]])]})])],"isStart":true})]}),makeQuery(id+"F6.opLoft","CAP_FACE",FACE,{"disambiguationData":[OSD([makeQuery(id+"F4.imprint","IMPRINT",FACE,{"disambiguationData":[TD([[makeQuery(id+"F4.imprint","IMPRINT",EDGE,{"derivedFrom":sQuery(id+"F4.wireOp",EDGE,"E26.15.0")}),1.0]])]})])],"isStart":true})]}),makeQuery(id+"F7.opLoft","CAP_FACE",FACE,{"disambiguationData":[OSD([makeQuery(id+"F4.imprint","IMPRINT",FACE,{"disambiguationData":[TD([[makeQuery(id+"F4.imprint","IMPRINT",EDGE,{"derivedFrom":sQuery(id+"F4.wireOp",EDGE,"E26.14.0")}),1.0]])]})])],"isStart":true})]}),makeQuery(id+"F8.opLoft","CAP_FACE",FACE,{"disambiguationData":[OSD([makeQuery(id+"F4.imprint","IMPRINT",FACE,{"disambiguationData":[TD([[makeQuery(id+"F4.imprint","IMPRINT",EDGE,{"derivedFrom":sQuery(id+"F4.wireOp",EDGE,"E26.13.0")}),1.0]])]})])],"isStart":true})]}),makeQuery(id+"F9.opLoft","CAP_FACE",FACE,{"disambiguationData":[OSD([makeQuery(id+"F4.imprint","IMPRINT",FACE,{"disambiguationData":[TD([[makeQuery(id+"F4.imprint","IMPRINT",EDGE,{"derivedFrom":sQuery(id+"F4.wireOp",EDGE,"E26.12.0")}),1.0]])]})])],"isStart":true})]}),makeQuery(id+"F10.opLoft","CAP_FACE",FACE,{"disambiguationData":[OSD([makeQuery(id+"F4.imprint","IMPRINT",FACE,{"disambiguationData":[TD([[makeQuery(id+"F4.imprint","IMPRINT",EDGE,{"derivedFrom":sQuery(id+"F4.wireOp",EDGE,"E26.11.0")}),1.0]])]})])],"isStart":true})]}),makeQuery(id+"F11.opLoft","CAP_FACE",FACE,{"disambiguationData":[OSD([makeQuery(id+"F4.imprint","IMPRINT",FACE,{"disambiguationData":[TD([[makeQuery(id+"F4.imprint","IMPRINT",EDGE,{"derivedFrom":sQuery(id+"F4.wireOp",EDGE,"E26.10.0")}),1.0]])]})])],"isStart":true})]}),makeQuery(id+"F12.opLoft","CAP_FACE",FACE,{"disambiguationData":[OSD([makeQuery(id+"F4.imprint","IMPRINT",FACE,{"disambiguationData":[TD([[makeQuery(id+"F4.imprint","IMPRINT",EDGE,{"derivedFrom":sQuery(id+"F4.wireOp",EDGE,"E26.9.0")}),1.0]])]})])],"isStart":true})]}),makeQuery(id+"F13.opLoft","CAP_FACE",FACE,{"disambiguationData":[OSD([makeQuery(id+"F4.imprint","IMPRINT",FACE,{"disambiguationData":[TD([[makeQuery(id+"F4.imprint","IMPRINT",EDGE,{"derivedFrom":sQuery(id+"F4.wireOp",EDGE,"E26.8.0")}),1.0]])]})])],"isStart":true})]}),makeQuery(id+"F14.opLoft","CAP_FACE",FACE,{"disambiguationData":[OSD([makeQuery(id+"F4.imprint","IMPRINT",FACE,{"disambiguationData":[TD([[makeQuery(id+"F4.imprint","IMPRINT",EDGE,{"derivedFrom":sQuery(id+"F4.wireOp",EDGE,"E26.7.0")}),1.0]])]})])],"isStart":true})]}),makeQuery(id+"F15.opLoft","CAP_FACE",FACE,{"disambiguationData":[OSD([makeQuery(id+"F4.imprint","IMPRINT",FACE,{"disambiguationData":[TD([[makeQuery(id+"F4.imprint","IMPRINT",EDGE,{"derivedFrom":sQuery(id+"F4.wireOp",EDGE,"E26.6.0")}),1.0]])]})])],"isStart":true})]}),makeQuery(id+"F16.opLoft","CAP_FACE",FACE,{"disambiguationData":[OSD([makeQuery(id+"F4.imprint","IMPRINT",FACE,{"disambiguationData":[TD([[makeQuery(id+"F4.imprint","IMPRINT",EDGE,{"derivedFrom":sQuery(id+"F4.wireOp",EDGE,"E26.5.0")}),1.0]])]})])],"isStart":true})]}),makeQuery(id+"F17.opLoft","CAP_FACE",FACE,{"disambiguationData":[OSD([makeQuery(id+"F4.imprint","IMPRINT",FACE,{"disambiguationData":[TD([[makeQuery(id+"F4.imprint","IMPRINT",EDGE,{"derivedFrom":sQuery(id+"F4.wireOp",EDGE,"E26.4.0")}),1.0]])]})])],"isStart":true})]}),makeQuery(id+"F18.opLoft","CAP_FACE",FACE,{"disambiguationData":[OSD([makeQuery(id+"F4.imprint","IMPRINT",FACE,{"disambiguationData":[TD([[makeQuery(id+"F4.imprint","IMPRINT",EDGE,{"derivedFrom":sQuery(id+"F4.wireOp",EDGE,"E26.3.0")}),1.0]])]})])],"isStart":true})]}),makeQuery(id+"F19.opLoft","CAP_FACE",FACE,{"disambiguationData":[OSD([makeQuery(id+"F4.imprint","IMPRINT",FACE,{"disambiguationData":[TD([[makeQuery(id+"F4.imprint","IMPRINT",EDGE,{"derivedFrom":sQuery(id+"F4.wireOp",EDGE,"E26.2.0")}),1.0]])]})])],"isStart":true})]}),makeQuery(id+"F20.opLoft","CAP_FACE",FACE,{"disambiguationData":[OSD([makeQuery(id+"F4.imprint","IMPRINT",FACE,{"disambiguationData":[TD([[makeQuery(id+"F4.imprint","IMPRINT",EDGE,{"derivedFrom":sQuery(id+"F4.wireOp",EDGE,"E26.1.0")}),1.0]])]})])],"isStart":true})]}),makeQuery(id+"F42.opRevolve","SWEPT_FACE",FACE,{"disambiguationData":[OSD([sQuery(id+"F41.wireOp",EDGE,"E32")])]})]});
            var Q10;
            Q10=makeQuery(id+"F42.boolean.opBoolean","INTERSECT",EDGE,{"disambiguationData":[OD(11.0)],"derivedFrom":[makeQuery(id+"F20.boolean.opBoolean","MERGE",FACE,{"derivedFrom":[makeQuery(id+"F19.boolean.opBoolean","MERGE",FACE,{"derivedFrom":[makeQuery(id+"F18.boolean.opBoolean","MERGE",FACE,{"derivedFrom":[makeQuery(id+"F17.boolean.opBoolean","MERGE",FACE,{"derivedFrom":[makeQuery(id+"F16.boolean.opBoolean","MERGE",FACE,{"derivedFrom":[makeQuery(id+"F15.boolean.opBoolean","MERGE",FACE,{"derivedFrom":[makeQuery(id+"F14.boolean.opBoolean","MERGE",FACE,{"derivedFrom":[makeQuery(id+"F13.boolean.opBoolean","MERGE",FACE,{"derivedFrom":[makeQuery(id+"F12.boolean.opBoolean","MERGE",FACE,{"derivedFrom":[makeQuery(id+"F11.boolean.opBoolean","MERGE",FACE,{"derivedFrom":[makeQuery(id+"F10.boolean.opBoolean","MERGE",FACE,{"derivedFrom":[makeQuery(id+"F9.boolean.opBoolean","MERGE",FACE,{"derivedFrom":[makeQuery(id+"F8.boolean.opBoolean","MERGE",FACE,{"derivedFrom":[makeQuery(id+"F7.boolean.opBoolean","MERGE",FACE,{"derivedFrom":[makeQuery(id+"F6.boolean.opBoolean","MERGE",FACE,{"derivedFrom":[makeQuery(id+"F5.boolean.opBoolean","MERGE",FACE,{"derivedFrom":[makeQuery(id+"F1.opRevolve","SWEPT_FACE",FACE,{"disambiguationData":[OSD([sQuery(id+"F0.wireOp",EDGE,"E14")])]}),makeQuery(id+"F5.opLoft","CAP_FACE",FACE,{"disambiguationData":[OSD([makeQuery(id+"F4.imprint","IMPRINT",FACE,{"disambiguationData":[TD([[makeQuery(id+"F4.imprint","IMPRINT",EDGE,{"derivedFrom":sQuery(id+"F4.wireOp",EDGE,"E21")}),1.0]])]})])],"isStart":true})]}),makeQuery(id+"F6.opLoft","CAP_FACE",FACE,{"disambiguationData":[OSD([makeQuery(id+"F4.imprint","IMPRINT",FACE,{"disambiguationData":[TD([[makeQuery(id+"F4.imprint","IMPRINT",EDGE,{"derivedFrom":sQuery(id+"F4.wireOp",EDGE,"E26.15.0")}),1.0]])]})])],"isStart":true})]}),makeQuery(id+"F7.opLoft","CAP_FACE",FACE,{"disambiguationData":[OSD([makeQuery(id+"F4.imprint","IMPRINT",FACE,{"disambiguationData":[TD([[makeQuery(id+"F4.imprint","IMPRINT",EDGE,{"derivedFrom":sQuery(id+"F4.wireOp",EDGE,"E26.14.0")}),1.0]])]})])],"isStart":true})]}),makeQuery(id+"F8.opLoft","CAP_FACE",FACE,{"disambiguationData":[OSD([makeQuery(id+"F4.imprint","IMPRINT",FACE,{"disambiguationData":[TD([[makeQuery(id+"F4.imprint","IMPRINT",EDGE,{"derivedFrom":sQuery(id+"F4.wireOp",EDGE,"E26.13.0")}),1.0]])]})])],"isStart":true})]}),makeQuery(id+"F9.opLoft","CAP_FACE",FACE,{"disambiguationData":[OSD([makeQuery(id+"F4.imprint","IMPRINT",FACE,{"disambiguationData":[TD([[makeQuery(id+"F4.imprint","IMPRINT",EDGE,{"derivedFrom":sQuery(id+"F4.wireOp",EDGE,"E26.12.0")}),1.0]])]})])],"isStart":true})]}),makeQuery(id+"F10.opLoft","CAP_FACE",FACE,{"disambiguationData":[OSD([makeQuery(id+"F4.imprint","IMPRINT",FACE,{"disambiguationData":[TD([[makeQuery(id+"F4.imprint","IMPRINT",EDGE,{"derivedFrom":sQuery(id+"F4.wireOp",EDGE,"E26.11.0")}),1.0]])]})])],"isStart":true})]}),makeQuery(id+"F11.opLoft","CAP_FACE",FACE,{"disambiguationData":[OSD([makeQuery(id+"F4.imprint","IMPRINT",FACE,{"disambiguationData":[TD([[makeQuery(id+"F4.imprint","IMPRINT",EDGE,{"derivedFrom":sQuery(id+"F4.wireOp",EDGE,"E26.10.0")}),1.0]])]})])],"isStart":true})]}),makeQuery(id+"F12.opLoft","CAP_FACE",FACE,{"disambiguationData":[OSD([makeQuery(id+"F4.imprint","IMPRINT",FACE,{"disambiguationData":[TD([[makeQuery(id+"F4.imprint","IMPRINT",EDGE,{"derivedFrom":sQuery(id+"F4.wireOp",EDGE,"E26.9.0")}),1.0]])]})])],"isStart":true})]}),makeQuery(id+"F13.opLoft","CAP_FACE",FACE,{"disambiguationData":[OSD([makeQuery(id+"F4.imprint","IMPRINT",FACE,{"disambiguationData":[TD([[makeQuery(id+"F4.imprint","IMPRINT",EDGE,{"derivedFrom":sQuery(id+"F4.wireOp",EDGE,"E26.8.0")}),1.0]])]})])],"isStart":true})]}),makeQuery(id+"F14.opLoft","CAP_FACE",FACE,{"disambiguationData":[OSD([makeQuery(id+"F4.imprint","IMPRINT",FACE,{"disambiguationData":[TD([[makeQuery(id+"F4.imprint","IMPRINT",EDGE,{"derivedFrom":sQuery(id+"F4.wireOp",EDGE,"E26.7.0")}),1.0]])]})])],"isStart":true})]}),makeQuery(id+"F15.opLoft","CAP_FACE",FACE,{"disambiguationData":[OSD([makeQuery(id+"F4.imprint","IMPRINT",FACE,{"disambiguationData":[TD([[makeQuery(id+"F4.imprint","IMPRINT",EDGE,{"derivedFrom":sQuery(id+"F4.wireOp",EDGE,"E26.6.0")}),1.0]])]})])],"isStart":true})]}),makeQuery(id+"F16.opLoft","CAP_FACE",FACE,{"disambiguationData":[OSD([makeQuery(id+"F4.imprint","IMPRINT",FACE,{"disambiguationData":[TD([[makeQuery(id+"F4.imprint","IMPRINT",EDGE,{"derivedFrom":sQuery(id+"F4.wireOp",EDGE,"E26.5.0")}),1.0]])]})])],"isStart":true})]}),makeQuery(id+"F17.opLoft","CAP_FACE",FACE,{"disambiguationData":[OSD([makeQuery(id+"F4.imprint","IMPRINT",FACE,{"disambiguationData":[TD([[makeQuery(id+"F4.imprint","IMPRINT",EDGE,{"derivedFrom":sQuery(id+"F4.wireOp",EDGE,"E26.4.0")}),1.0]])]})])],"isStart":true})]}),makeQuery(id+"F18.opLoft","CAP_FACE",FACE,{"disambiguationData":[OSD([makeQuery(id+"F4.imprint","IMPRINT",FACE,{"disambiguationData":[TD([[makeQuery(id+"F4.imprint","IMPRINT",EDGE,{"derivedFrom":sQuery(id+"F4.wireOp",EDGE,"E26.3.0")}),1.0]])]})])],"isStart":true})]}),makeQuery(id+"F19.opLoft","CAP_FACE",FACE,{"disambiguationData":[OSD([makeQuery(id+"F4.imprint","IMPRINT",FACE,{"disambiguationData":[TD([[makeQuery(id+"F4.imprint","IMPRINT",EDGE,{"derivedFrom":sQuery(id+"F4.wireOp",EDGE,"E26.2.0")}),1.0]])]})])],"isStart":true})]}),makeQuery(id+"F20.opLoft","CAP_FACE",FACE,{"disambiguationData":[OSD([makeQuery(id+"F4.imprint","IMPRINT",FACE,{"disambiguationData":[TD([[makeQuery(id+"F4.imprint","IMPRINT",EDGE,{"derivedFrom":sQuery(id+"F4.wireOp",EDGE,"E26.1.0")}),1.0]])]})])],"isStart":true})]}),makeQuery(id+"F42.opRevolve","SWEPT_FACE",FACE,{"disambiguationData":[OSD([sQuery(id+"F41.wireOp",EDGE,"E32")])]})]});
            var Q11;
            Q11=makeQuery(id+"F42.boolean.opBoolean","INTERSECT",EDGE,{"disambiguationData":[OD(10.0)],"derivedFrom":[makeQuery(id+"F20.boolean.opBoolean","MERGE",FACE,{"derivedFrom":[makeQuery(id+"F19.boolean.opBoolean","MERGE",FACE,{"derivedFrom":[makeQuery(id+"F18.boolean.opBoolean","MERGE",FACE,{"derivedFrom":[makeQuery(id+"F17.boolean.opBoolean","MERGE",FACE,{"derivedFrom":[makeQuery(id+"F16.boolean.opBoolean","MERGE",FACE,{"derivedFrom":[makeQuery(id+"F15.boolean.opBoolean","MERGE",FACE,{"derivedFrom":[makeQuery(id+"F14.boolean.opBoolean","MERGE",FACE,{"derivedFrom":[makeQuery(id+"F13.boolean.opBoolean","MERGE",FACE,{"derivedFrom":[makeQuery(id+"F12.boolean.opBoolean","MERGE",FACE,{"derivedFrom":[makeQuery(id+"F11.boolean.opBoolean","MERGE",FACE,{"derivedFrom":[makeQuery(id+"F10.boolean.opBoolean","MERGE",FACE,{"derivedFrom":[makeQuery(id+"F9.boolean.opBoolean","MERGE",FACE,{"derivedFrom":[makeQuery(id+"F8.boolean.opBoolean","MERGE",FACE,{"derivedFrom":[makeQuery(id+"F7.boolean.opBoolean","MERGE",FACE,{"derivedFrom":[makeQuery(id+"F6.boolean.opBoolean","MERGE",FACE,{"derivedFrom":[makeQuery(id+"F5.boolean.opBoolean","MERGE",FACE,{"derivedFrom":[makeQuery(id+"F1.opRevolve","SWEPT_FACE",FACE,{"disambiguationData":[OSD([sQuery(id+"F0.wireOp",EDGE,"E14")])]}),makeQuery(id+"F5.opLoft","CAP_FACE",FACE,{"disambiguationData":[OSD([makeQuery(id+"F4.imprint","IMPRINT",FACE,{"disambiguationData":[TD([[makeQuery(id+"F4.imprint","IMPRINT",EDGE,{"derivedFrom":sQuery(id+"F4.wireOp",EDGE,"E21")}),1.0]])]})])],"isStart":true})]}),makeQuery(id+"F6.opLoft","CAP_FACE",FACE,{"disambiguationData":[OSD([makeQuery(id+"F4.imprint","IMPRINT",FACE,{"disambiguationData":[TD([[makeQuery(id+"F4.imprint","IMPRINT",EDGE,{"derivedFrom":sQuery(id+"F4.wireOp",EDGE,"E26.15.0")}),1.0]])]})])],"isStart":true})]}),makeQuery(id+"F7.opLoft","CAP_FACE",FACE,{"disambiguationData":[OSD([makeQuery(id+"F4.imprint","IMPRINT",FACE,{"disambiguationData":[TD([[makeQuery(id+"F4.imprint","IMPRINT",EDGE,{"derivedFrom":sQuery(id+"F4.wireOp",EDGE,"E26.14.0")}),1.0]])]})])],"isStart":true})]}),makeQuery(id+"F8.opLoft","CAP_FACE",FACE,{"disambiguationData":[OSD([makeQuery(id+"F4.imprint","IMPRINT",FACE,{"disambiguationData":[TD([[makeQuery(id+"F4.imprint","IMPRINT",EDGE,{"derivedFrom":sQuery(id+"F4.wireOp",EDGE,"E26.13.0")}),1.0]])]})])],"isStart":true})]}),makeQuery(id+"F9.opLoft","CAP_FACE",FACE,{"disambiguationData":[OSD([makeQuery(id+"F4.imprint","IMPRINT",FACE,{"disambiguationData":[TD([[makeQuery(id+"F4.imprint","IMPRINT",EDGE,{"derivedFrom":sQuery(id+"F4.wireOp",EDGE,"E26.12.0")}),1.0]])]})])],"isStart":true})]}),makeQuery(id+"F10.opLoft","CAP_FACE",FACE,{"disambiguationData":[OSD([makeQuery(id+"F4.imprint","IMPRINT",FACE,{"disambiguationData":[TD([[makeQuery(id+"F4.imprint","IMPRINT",EDGE,{"derivedFrom":sQuery(id+"F4.wireOp",EDGE,"E26.11.0")}),1.0]])]})])],"isStart":true})]}),makeQuery(id+"F11.opLoft","CAP_FACE",FACE,{"disambiguationData":[OSD([makeQuery(id+"F4.imprint","IMPRINT",FACE,{"disambiguationData":[TD([[makeQuery(id+"F4.imprint","IMPRINT",EDGE,{"derivedFrom":sQuery(id+"F4.wireOp",EDGE,"E26.10.0")}),1.0]])]})])],"isStart":true})]}),makeQuery(id+"F12.opLoft","CAP_FACE",FACE,{"disambiguationData":[OSD([makeQuery(id+"F4.imprint","IMPRINT",FACE,{"disambiguationData":[TD([[makeQuery(id+"F4.imprint","IMPRINT",EDGE,{"derivedFrom":sQuery(id+"F4.wireOp",EDGE,"E26.9.0")}),1.0]])]})])],"isStart":true})]}),makeQuery(id+"F13.opLoft","CAP_FACE",FACE,{"disambiguationData":[OSD([makeQuery(id+"F4.imprint","IMPRINT",FACE,{"disambiguationData":[TD([[makeQuery(id+"F4.imprint","IMPRINT",EDGE,{"derivedFrom":sQuery(id+"F4.wireOp",EDGE,"E26.8.0")}),1.0]])]})])],"isStart":true})]}),makeQuery(id+"F14.opLoft","CAP_FACE",FACE,{"disambiguationData":[OSD([makeQuery(id+"F4.imprint","IMPRINT",FACE,{"disambiguationData":[TD([[makeQuery(id+"F4.imprint","IMPRINT",EDGE,{"derivedFrom":sQuery(id+"F4.wireOp",EDGE,"E26.7.0")}),1.0]])]})])],"isStart":true})]}),makeQuery(id+"F15.opLoft","CAP_FACE",FACE,{"disambiguationData":[OSD([makeQuery(id+"F4.imprint","IMPRINT",FACE,{"disambiguationData":[TD([[makeQuery(id+"F4.imprint","IMPRINT",EDGE,{"derivedFrom":sQuery(id+"F4.wireOp",EDGE,"E26.6.0")}),1.0]])]})])],"isStart":true})]}),makeQuery(id+"F16.opLoft","CAP_FACE",FACE,{"disambiguationData":[OSD([makeQuery(id+"F4.imprint","IMPRINT",FACE,{"disambiguationData":[TD([[makeQuery(id+"F4.imprint","IMPRINT",EDGE,{"derivedFrom":sQuery(id+"F4.wireOp",EDGE,"E26.5.0")}),1.0]])]})])],"isStart":true})]}),makeQuery(id+"F17.opLoft","CAP_FACE",FACE,{"disambiguationData":[OSD([makeQuery(id+"F4.imprint","IMPRINT",FACE,{"disambiguationData":[TD([[makeQuery(id+"F4.imprint","IMPRINT",EDGE,{"derivedFrom":sQuery(id+"F4.wireOp",EDGE,"E26.4.0")}),1.0]])]})])],"isStart":true})]}),makeQuery(id+"F18.opLoft","CAP_FACE",FACE,{"disambiguationData":[OSD([makeQuery(id+"F4.imprint","IMPRINT",FACE,{"disambiguationData":[TD([[makeQuery(id+"F4.imprint","IMPRINT",EDGE,{"derivedFrom":sQuery(id+"F4.wireOp",EDGE,"E26.3.0")}),1.0]])]})])],"isStart":true})]}),makeQuery(id+"F19.opLoft","CAP_FACE",FACE,{"disambiguationData":[OSD([makeQuery(id+"F4.imprint","IMPRINT",FACE,{"disambiguationData":[TD([[makeQuery(id+"F4.imprint","IMPRINT",EDGE,{"derivedFrom":sQuery(id+"F4.wireOp",EDGE,"E26.2.0")}),1.0]])]})])],"isStart":true})]}),makeQuery(id+"F20.opLoft","CAP_FACE",FACE,{"disambiguationData":[OSD([makeQuery(id+"F4.imprint","IMPRINT",FACE,{"disambiguationData":[TD([[makeQuery(id+"F4.imprint","IMPRINT",EDGE,{"derivedFrom":sQuery(id+"F4.wireOp",EDGE,"E26.1.0")}),1.0]])]})])],"isStart":true})]}),makeQuery(id+"F42.opRevolve","SWEPT_FACE",FACE,{"disambiguationData":[OSD([sQuery(id+"F41.wireOp",EDGE,"E32")])]})]});
            var Q12;
            Q12=makeQuery(id+"F42.boolean.opBoolean","INTERSECT",EDGE,{"disambiguationData":[OD(9.0)],"derivedFrom":[makeQuery(id+"F20.boolean.opBoolean","MERGE",FACE,{"derivedFrom":[makeQuery(id+"F19.boolean.opBoolean","MERGE",FACE,{"derivedFrom":[makeQuery(id+"F18.boolean.opBoolean","MERGE",FACE,{"derivedFrom":[makeQuery(id+"F17.boolean.opBoolean","MERGE",FACE,{"derivedFrom":[makeQuery(id+"F16.boolean.opBoolean","MERGE",FACE,{"derivedFrom":[makeQuery(id+"F15.boolean.opBoolean","MERGE",FACE,{"derivedFrom":[makeQuery(id+"F14.boolean.opBoolean","MERGE",FACE,{"derivedFrom":[makeQuery(id+"F13.boolean.opBoolean","MERGE",FACE,{"derivedFrom":[makeQuery(id+"F12.boolean.opBoolean","MERGE",FACE,{"derivedFrom":[makeQuery(id+"F11.boolean.opBoolean","MERGE",FACE,{"derivedFrom":[makeQuery(id+"F10.boolean.opBoolean","MERGE",FACE,{"derivedFrom":[makeQuery(id+"F9.boolean.opBoolean","MERGE",FACE,{"derivedFrom":[makeQuery(id+"F8.boolean.opBoolean","MERGE",FACE,{"derivedFrom":[makeQuery(id+"F7.boolean.opBoolean","MERGE",FACE,{"derivedFrom":[makeQuery(id+"F6.boolean.opBoolean","MERGE",FACE,{"derivedFrom":[makeQuery(id+"F5.boolean.opBoolean","MERGE",FACE,{"derivedFrom":[makeQuery(id+"F1.opRevolve","SWEPT_FACE",FACE,{"disambiguationData":[OSD([sQuery(id+"F0.wireOp",EDGE,"E14")])]}),makeQuery(id+"F5.opLoft","CAP_FACE",FACE,{"disambiguationData":[OSD([makeQuery(id+"F4.imprint","IMPRINT",FACE,{"disambiguationData":[TD([[makeQuery(id+"F4.imprint","IMPRINT",EDGE,{"derivedFrom":sQuery(id+"F4.wireOp",EDGE,"E21")}),1.0]])]})])],"isStart":true})]}),makeQuery(id+"F6.opLoft","CAP_FACE",FACE,{"disambiguationData":[OSD([makeQuery(id+"F4.imprint","IMPRINT",FACE,{"disambiguationData":[TD([[makeQuery(id+"F4.imprint","IMPRINT",EDGE,{"derivedFrom":sQuery(id+"F4.wireOp",EDGE,"E26.15.0")}),1.0]])]})])],"isStart":true})]}),makeQuery(id+"F7.opLoft","CAP_FACE",FACE,{"disambiguationData":[OSD([makeQuery(id+"F4.imprint","IMPRINT",FACE,{"disambiguationData":[TD([[makeQuery(id+"F4.imprint","IMPRINT",EDGE,{"derivedFrom":sQuery(id+"F4.wireOp",EDGE,"E26.14.0")}),1.0]])]})])],"isStart":true})]}),makeQuery(id+"F8.opLoft","CAP_FACE",FACE,{"disambiguationData":[OSD([makeQuery(id+"F4.imprint","IMPRINT",FACE,{"disambiguationData":[TD([[makeQuery(id+"F4.imprint","IMPRINT",EDGE,{"derivedFrom":sQuery(id+"F4.wireOp",EDGE,"E26.13.0")}),1.0]])]})])],"isStart":true})]}),makeQuery(id+"F9.opLoft","CAP_FACE",FACE,{"disambiguationData":[OSD([makeQuery(id+"F4.imprint","IMPRINT",FACE,{"disambiguationData":[TD([[makeQuery(id+"F4.imprint","IMPRINT",EDGE,{"derivedFrom":sQuery(id+"F4.wireOp",EDGE,"E26.12.0")}),1.0]])]})])],"isStart":true})]}),makeQuery(id+"F10.opLoft","CAP_FACE",FACE,{"disambiguationData":[OSD([makeQuery(id+"F4.imprint","IMPRINT",FACE,{"disambiguationData":[TD([[makeQuery(id+"F4.imprint","IMPRINT",EDGE,{"derivedFrom":sQuery(id+"F4.wireOp",EDGE,"E26.11.0")}),1.0]])]})])],"isStart":true})]}),makeQuery(id+"F11.opLoft","CAP_FACE",FACE,{"disambiguationData":[OSD([makeQuery(id+"F4.imprint","IMPRINT",FACE,{"disambiguationData":[TD([[makeQuery(id+"F4.imprint","IMPRINT",EDGE,{"derivedFrom":sQuery(id+"F4.wireOp",EDGE,"E26.10.0")}),1.0]])]})])],"isStart":true})]}),makeQuery(id+"F12.opLoft","CAP_FACE",FACE,{"disambiguationData":[OSD([makeQuery(id+"F4.imprint","IMPRINT",FACE,{"disambiguationData":[TD([[makeQuery(id+"F4.imprint","IMPRINT",EDGE,{"derivedFrom":sQuery(id+"F4.wireOp",EDGE,"E26.9.0")}),1.0]])]})])],"isStart":true})]}),makeQuery(id+"F13.opLoft","CAP_FACE",FACE,{"disambiguationData":[OSD([makeQuery(id+"F4.imprint","IMPRINT",FACE,{"disambiguationData":[TD([[makeQuery(id+"F4.imprint","IMPRINT",EDGE,{"derivedFrom":sQuery(id+"F4.wireOp",EDGE,"E26.8.0")}),1.0]])]})])],"isStart":true})]}),makeQuery(id+"F14.opLoft","CAP_FACE",FACE,{"disambiguationData":[OSD([makeQuery(id+"F4.imprint","IMPRINT",FACE,{"disambiguationData":[TD([[makeQuery(id+"F4.imprint","IMPRINT",EDGE,{"derivedFrom":sQuery(id+"F4.wireOp",EDGE,"E26.7.0")}),1.0]])]})])],"isStart":true})]}),makeQuery(id+"F15.opLoft","CAP_FACE",FACE,{"disambiguationData":[OSD([makeQuery(id+"F4.imprint","IMPRINT",FACE,{"disambiguationData":[TD([[makeQuery(id+"F4.imprint","IMPRINT",EDGE,{"derivedFrom":sQuery(id+"F4.wireOp",EDGE,"E26.6.0")}),1.0]])]})])],"isStart":true})]}),makeQuery(id+"F16.opLoft","CAP_FACE",FACE,{"disambiguationData":[OSD([makeQuery(id+"F4.imprint","IMPRINT",FACE,{"disambiguationData":[TD([[makeQuery(id+"F4.imprint","IMPRINT",EDGE,{"derivedFrom":sQuery(id+"F4.wireOp",EDGE,"E26.5.0")}),1.0]])]})])],"isStart":true})]}),makeQuery(id+"F17.opLoft","CAP_FACE",FACE,{"disambiguationData":[OSD([makeQuery(id+"F4.imprint","IMPRINT",FACE,{"disambiguationData":[TD([[makeQuery(id+"F4.imprint","IMPRINT",EDGE,{"derivedFrom":sQuery(id+"F4.wireOp",EDGE,"E26.4.0")}),1.0]])]})])],"isStart":true})]}),makeQuery(id+"F18.opLoft","CAP_FACE",FACE,{"disambiguationData":[OSD([makeQuery(id+"F4.imprint","IMPRINT",FACE,{"disambiguationData":[TD([[makeQuery(id+"F4.imprint","IMPRINT",EDGE,{"derivedFrom":sQuery(id+"F4.wireOp",EDGE,"E26.3.0")}),1.0]])]})])],"isStart":true})]}),makeQuery(id+"F19.opLoft","CAP_FACE",FACE,{"disambiguationData":[OSD([makeQuery(id+"F4.imprint","IMPRINT",FACE,{"disambiguationData":[TD([[makeQuery(id+"F4.imprint","IMPRINT",EDGE,{"derivedFrom":sQuery(id+"F4.wireOp",EDGE,"E26.2.0")}),1.0]])]})])],"isStart":true})]}),makeQuery(id+"F20.opLoft","CAP_FACE",FACE,{"disambiguationData":[OSD([makeQuery(id+"F4.imprint","IMPRINT",FACE,{"disambiguationData":[TD([[makeQuery(id+"F4.imprint","IMPRINT",EDGE,{"derivedFrom":sQuery(id+"F4.wireOp",EDGE,"E26.1.0")}),1.0]])]})])],"isStart":true})]}),makeQuery(id+"F42.opRevolve","SWEPT_FACE",FACE,{"disambiguationData":[OSD([sQuery(id+"F41.wireOp",EDGE,"E32")])]})]});
            var Q13;
            Q13=makeQuery(id+"F42.boolean.opBoolean","INTERSECT",EDGE,{"disambiguationData":[OD(8.0)],"derivedFrom":[makeQuery(id+"F20.boolean.opBoolean","MERGE",FACE,{"derivedFrom":[makeQuery(id+"F19.boolean.opBoolean","MERGE",FACE,{"derivedFrom":[makeQuery(id+"F18.boolean.opBoolean","MERGE",FACE,{"derivedFrom":[makeQuery(id+"F17.boolean.opBoolean","MERGE",FACE,{"derivedFrom":[makeQuery(id+"F16.boolean.opBoolean","MERGE",FACE,{"derivedFrom":[makeQuery(id+"F15.boolean.opBoolean","MERGE",FACE,{"derivedFrom":[makeQuery(id+"F14.boolean.opBoolean","MERGE",FACE,{"derivedFrom":[makeQuery(id+"F13.boolean.opBoolean","MERGE",FACE,{"derivedFrom":[makeQuery(id+"F12.boolean.opBoolean","MERGE",FACE,{"derivedFrom":[makeQuery(id+"F11.boolean.opBoolean","MERGE",FACE,{"derivedFrom":[makeQuery(id+"F10.boolean.opBoolean","MERGE",FACE,{"derivedFrom":[makeQuery(id+"F9.boolean.opBoolean","MERGE",FACE,{"derivedFrom":[makeQuery(id+"F8.boolean.opBoolean","MERGE",FACE,{"derivedFrom":[makeQuery(id+"F7.boolean.opBoolean","MERGE",FACE,{"derivedFrom":[makeQuery(id+"F6.boolean.opBoolean","MERGE",FACE,{"derivedFrom":[makeQuery(id+"F5.boolean.opBoolean","MERGE",FACE,{"derivedFrom":[makeQuery(id+"F1.opRevolve","SWEPT_FACE",FACE,{"disambiguationData":[OSD([sQuery(id+"F0.wireOp",EDGE,"E14")])]}),makeQuery(id+"F5.opLoft","CAP_FACE",FACE,{"disambiguationData":[OSD([makeQuery(id+"F4.imprint","IMPRINT",FACE,{"disambiguationData":[TD([[makeQuery(id+"F4.imprint","IMPRINT",EDGE,{"derivedFrom":sQuery(id+"F4.wireOp",EDGE,"E21")}),1.0]])]})])],"isStart":true})]}),makeQuery(id+"F6.opLoft","CAP_FACE",FACE,{"disambiguationData":[OSD([makeQuery(id+"F4.imprint","IMPRINT",FACE,{"disambiguationData":[TD([[makeQuery(id+"F4.imprint","IMPRINT",EDGE,{"derivedFrom":sQuery(id+"F4.wireOp",EDGE,"E26.15.0")}),1.0]])]})])],"isStart":true})]}),makeQuery(id+"F7.opLoft","CAP_FACE",FACE,{"disambiguationData":[OSD([makeQuery(id+"F4.imprint","IMPRINT",FACE,{"disambiguationData":[TD([[makeQuery(id+"F4.imprint","IMPRINT",EDGE,{"derivedFrom":sQuery(id+"F4.wireOp",EDGE,"E26.14.0")}),1.0]])]})])],"isStart":true})]}),makeQuery(id+"F8.opLoft","CAP_FACE",FACE,{"disambiguationData":[OSD([makeQuery(id+"F4.imprint","IMPRINT",FACE,{"disambiguationData":[TD([[makeQuery(id+"F4.imprint","IMPRINT",EDGE,{"derivedFrom":sQuery(id+"F4.wireOp",EDGE,"E26.13.0")}),1.0]])]})])],"isStart":true})]}),makeQuery(id+"F9.opLoft","CAP_FACE",FACE,{"disambiguationData":[OSD([makeQuery(id+"F4.imprint","IMPRINT",FACE,{"disambiguationData":[TD([[makeQuery(id+"F4.imprint","IMPRINT",EDGE,{"derivedFrom":sQuery(id+"F4.wireOp",EDGE,"E26.12.0")}),1.0]])]})])],"isStart":true})]}),makeQuery(id+"F10.opLoft","CAP_FACE",FACE,{"disambiguationData":[OSD([makeQuery(id+"F4.imprint","IMPRINT",FACE,{"disambiguationData":[TD([[makeQuery(id+"F4.imprint","IMPRINT",EDGE,{"derivedFrom":sQuery(id+"F4.wireOp",EDGE,"E26.11.0")}),1.0]])]})])],"isStart":true})]}),makeQuery(id+"F11.opLoft","CAP_FACE",FACE,{"disambiguationData":[OSD([makeQuery(id+"F4.imprint","IMPRINT",FACE,{"disambiguationData":[TD([[makeQuery(id+"F4.imprint","IMPRINT",EDGE,{"derivedFrom":sQuery(id+"F4.wireOp",EDGE,"E26.10.0")}),1.0]])]})])],"isStart":true})]}),makeQuery(id+"F12.opLoft","CAP_FACE",FACE,{"disambiguationData":[OSD([makeQuery(id+"F4.imprint","IMPRINT",FACE,{"disambiguationData":[TD([[makeQuery(id+"F4.imprint","IMPRINT",EDGE,{"derivedFrom":sQuery(id+"F4.wireOp",EDGE,"E26.9.0")}),1.0]])]})])],"isStart":true})]}),makeQuery(id+"F13.opLoft","CAP_FACE",FACE,{"disambiguationData":[OSD([makeQuery(id+"F4.imprint","IMPRINT",FACE,{"disambiguationData":[TD([[makeQuery(id+"F4.imprint","IMPRINT",EDGE,{"derivedFrom":sQuery(id+"F4.wireOp",EDGE,"E26.8.0")}),1.0]])]})])],"isStart":true})]}),makeQuery(id+"F14.opLoft","CAP_FACE",FACE,{"disambiguationData":[OSD([makeQuery(id+"F4.imprint","IMPRINT",FACE,{"disambiguationData":[TD([[makeQuery(id+"F4.imprint","IMPRINT",EDGE,{"derivedFrom":sQuery(id+"F4.wireOp",EDGE,"E26.7.0")}),1.0]])]})])],"isStart":true})]}),makeQuery(id+"F15.opLoft","CAP_FACE",FACE,{"disambiguationData":[OSD([makeQuery(id+"F4.imprint","IMPRINT",FACE,{"disambiguationData":[TD([[makeQuery(id+"F4.imprint","IMPRINT",EDGE,{"derivedFrom":sQuery(id+"F4.wireOp",EDGE,"E26.6.0")}),1.0]])]})])],"isStart":true})]}),makeQuery(id+"F16.opLoft","CAP_FACE",FACE,{"disambiguationData":[OSD([makeQuery(id+"F4.imprint","IMPRINT",FACE,{"disambiguationData":[TD([[makeQuery(id+"F4.imprint","IMPRINT",EDGE,{"derivedFrom":sQuery(id+"F4.wireOp",EDGE,"E26.5.0")}),1.0]])]})])],"isStart":true})]}),makeQuery(id+"F17.opLoft","CAP_FACE",FACE,{"disambiguationData":[OSD([makeQuery(id+"F4.imprint","IMPRINT",FACE,{"disambiguationData":[TD([[makeQuery(id+"F4.imprint","IMPRINT",EDGE,{"derivedFrom":sQuery(id+"F4.wireOp",EDGE,"E26.4.0")}),1.0]])]})])],"isStart":true})]}),makeQuery(id+"F18.opLoft","CAP_FACE",FACE,{"disambiguationData":[OSD([makeQuery(id+"F4.imprint","IMPRINT",FACE,{"disambiguationData":[TD([[makeQuery(id+"F4.imprint","IMPRINT",EDGE,{"derivedFrom":sQuery(id+"F4.wireOp",EDGE,"E26.3.0")}),1.0]])]})])],"isStart":true})]}),makeQuery(id+"F19.opLoft","CAP_FACE",FACE,{"disambiguationData":[OSD([makeQuery(id+"F4.imprint","IMPRINT",FACE,{"disambiguationData":[TD([[makeQuery(id+"F4.imprint","IMPRINT",EDGE,{"derivedFrom":sQuery(id+"F4.wireOp",EDGE,"E26.2.0")}),1.0]])]})])],"isStart":true})]}),makeQuery(id+"F20.opLoft","CAP_FACE",FACE,{"disambiguationData":[OSD([makeQuery(id+"F4.imprint","IMPRINT",FACE,{"disambiguationData":[TD([[makeQuery(id+"F4.imprint","IMPRINT",EDGE,{"derivedFrom":sQuery(id+"F4.wireOp",EDGE,"E26.1.0")}),1.0]])]})])],"isStart":true})]}),makeQuery(id+"F42.opRevolve","SWEPT_FACE",FACE,{"disambiguationData":[OSD([sQuery(id+"F41.wireOp",EDGE,"E32")])]})]});
            var Q14;
            Q14=makeQuery(id+"F42.boolean.opBoolean","INTERSECT",EDGE,{"disambiguationData":[OD(7.0)],"derivedFrom":[makeQuery(id+"F20.boolean.opBoolean","MERGE",FACE,{"derivedFrom":[makeQuery(id+"F19.boolean.opBoolean","MERGE",FACE,{"derivedFrom":[makeQuery(id+"F18.boolean.opBoolean","MERGE",FACE,{"derivedFrom":[makeQuery(id+"F17.boolean.opBoolean","MERGE",FACE,{"derivedFrom":[makeQuery(id+"F16.boolean.opBoolean","MERGE",FACE,{"derivedFrom":[makeQuery(id+"F15.boolean.opBoolean","MERGE",FACE,{"derivedFrom":[makeQuery(id+"F14.boolean.opBoolean","MERGE",FACE,{"derivedFrom":[makeQuery(id+"F13.boolean.opBoolean","MERGE",FACE,{"derivedFrom":[makeQuery(id+"F12.boolean.opBoolean","MERGE",FACE,{"derivedFrom":[makeQuery(id+"F11.boolean.opBoolean","MERGE",FACE,{"derivedFrom":[makeQuery(id+"F10.boolean.opBoolean","MERGE",FACE,{"derivedFrom":[makeQuery(id+"F9.boolean.opBoolean","MERGE",FACE,{"derivedFrom":[makeQuery(id+"F8.boolean.opBoolean","MERGE",FACE,{"derivedFrom":[makeQuery(id+"F7.boolean.opBoolean","MERGE",FACE,{"derivedFrom":[makeQuery(id+"F6.boolean.opBoolean","MERGE",FACE,{"derivedFrom":[makeQuery(id+"F5.boolean.opBoolean","MERGE",FACE,{"derivedFrom":[makeQuery(id+"F1.opRevolve","SWEPT_FACE",FACE,{"disambiguationData":[OSD([sQuery(id+"F0.wireOp",EDGE,"E14")])]}),makeQuery(id+"F5.opLoft","CAP_FACE",FACE,{"disambiguationData":[OSD([makeQuery(id+"F4.imprint","IMPRINT",FACE,{"disambiguationData":[TD([[makeQuery(id+"F4.imprint","IMPRINT",EDGE,{"derivedFrom":sQuery(id+"F4.wireOp",EDGE,"E21")}),1.0]])]})])],"isStart":true})]}),makeQuery(id+"F6.opLoft","CAP_FACE",FACE,{"disambiguationData":[OSD([makeQuery(id+"F4.imprint","IMPRINT",FACE,{"disambiguationData":[TD([[makeQuery(id+"F4.imprint","IMPRINT",EDGE,{"derivedFrom":sQuery(id+"F4.wireOp",EDGE,"E26.15.0")}),1.0]])]})])],"isStart":true})]}),makeQuery(id+"F7.opLoft","CAP_FACE",FACE,{"disambiguationData":[OSD([makeQuery(id+"F4.imprint","IMPRINT",FACE,{"disambiguationData":[TD([[makeQuery(id+"F4.imprint","IMPRINT",EDGE,{"derivedFrom":sQuery(id+"F4.wireOp",EDGE,"E26.14.0")}),1.0]])]})])],"isStart":true})]}),makeQuery(id+"F8.opLoft","CAP_FACE",FACE,{"disambiguationData":[OSD([makeQuery(id+"F4.imprint","IMPRINT",FACE,{"disambiguationData":[TD([[makeQuery(id+"F4.imprint","IMPRINT",EDGE,{"derivedFrom":sQuery(id+"F4.wireOp",EDGE,"E26.13.0")}),1.0]])]})])],"isStart":true})]}),makeQuery(id+"F9.opLoft","CAP_FACE",FACE,{"disambiguationData":[OSD([makeQuery(id+"F4.imprint","IMPRINT",FACE,{"disambiguationData":[TD([[makeQuery(id+"F4.imprint","IMPRINT",EDGE,{"derivedFrom":sQuery(id+"F4.wireOp",EDGE,"E26.12.0")}),1.0]])]})])],"isStart":true})]}),makeQuery(id+"F10.opLoft","CAP_FACE",FACE,{"disambiguationData":[OSD([makeQuery(id+"F4.imprint","IMPRINT",FACE,{"disambiguationData":[TD([[makeQuery(id+"F4.imprint","IMPRINT",EDGE,{"derivedFrom":sQuery(id+"F4.wireOp",EDGE,"E26.11.0")}),1.0]])]})])],"isStart":true})]}),makeQuery(id+"F11.opLoft","CAP_FACE",FACE,{"disambiguationData":[OSD([makeQuery(id+"F4.imprint","IMPRINT",FACE,{"disambiguationData":[TD([[makeQuery(id+"F4.imprint","IMPRINT",EDGE,{"derivedFrom":sQuery(id+"F4.wireOp",EDGE,"E26.10.0")}),1.0]])]})])],"isStart":true})]}),makeQuery(id+"F12.opLoft","CAP_FACE",FACE,{"disambiguationData":[OSD([makeQuery(id+"F4.imprint","IMPRINT",FACE,{"disambiguationData":[TD([[makeQuery(id+"F4.imprint","IMPRINT",EDGE,{"derivedFrom":sQuery(id+"F4.wireOp",EDGE,"E26.9.0")}),1.0]])]})])],"isStart":true})]}),makeQuery(id+"F13.opLoft","CAP_FACE",FACE,{"disambiguationData":[OSD([makeQuery(id+"F4.imprint","IMPRINT",FACE,{"disambiguationData":[TD([[makeQuery(id+"F4.imprint","IMPRINT",EDGE,{"derivedFrom":sQuery(id+"F4.wireOp",EDGE,"E26.8.0")}),1.0]])]})])],"isStart":true})]}),makeQuery(id+"F14.opLoft","CAP_FACE",FACE,{"disambiguationData":[OSD([makeQuery(id+"F4.imprint","IMPRINT",FACE,{"disambiguationData":[TD([[makeQuery(id+"F4.imprint","IMPRINT",EDGE,{"derivedFrom":sQuery(id+"F4.wireOp",EDGE,"E26.7.0")}),1.0]])]})])],"isStart":true})]}),makeQuery(id+"F15.opLoft","CAP_FACE",FACE,{"disambiguationData":[OSD([makeQuery(id+"F4.imprint","IMPRINT",FACE,{"disambiguationData":[TD([[makeQuery(id+"F4.imprint","IMPRINT",EDGE,{"derivedFrom":sQuery(id+"F4.wireOp",EDGE,"E26.6.0")}),1.0]])]})])],"isStart":true})]}),makeQuery(id+"F16.opLoft","CAP_FACE",FACE,{"disambiguationData":[OSD([makeQuery(id+"F4.imprint","IMPRINT",FACE,{"disambiguationData":[TD([[makeQuery(id+"F4.imprint","IMPRINT",EDGE,{"derivedFrom":sQuery(id+"F4.wireOp",EDGE,"E26.5.0")}),1.0]])]})])],"isStart":true})]}),makeQuery(id+"F17.opLoft","CAP_FACE",FACE,{"disambiguationData":[OSD([makeQuery(id+"F4.imprint","IMPRINT",FACE,{"disambiguationData":[TD([[makeQuery(id+"F4.imprint","IMPRINT",EDGE,{"derivedFrom":sQuery(id+"F4.wireOp",EDGE,"E26.4.0")}),1.0]])]})])],"isStart":true})]}),makeQuery(id+"F18.opLoft","CAP_FACE",FACE,{"disambiguationData":[OSD([makeQuery(id+"F4.imprint","IMPRINT",FACE,{"disambiguationData":[TD([[makeQuery(id+"F4.imprint","IMPRINT",EDGE,{"derivedFrom":sQuery(id+"F4.wireOp",EDGE,"E26.3.0")}),1.0]])]})])],"isStart":true})]}),makeQuery(id+"F19.opLoft","CAP_FACE",FACE,{"disambiguationData":[OSD([makeQuery(id+"F4.imprint","IMPRINT",FACE,{"disambiguationData":[TD([[makeQuery(id+"F4.imprint","IMPRINT",EDGE,{"derivedFrom":sQuery(id+"F4.wireOp",EDGE,"E26.2.0")}),1.0]])]})])],"isStart":true})]}),makeQuery(id+"F20.opLoft","CAP_FACE",FACE,{"disambiguationData":[OSD([makeQuery(id+"F4.imprint","IMPRINT",FACE,{"disambiguationData":[TD([[makeQuery(id+"F4.imprint","IMPRINT",EDGE,{"derivedFrom":sQuery(id+"F4.wireOp",EDGE,"E26.1.0")}),1.0]])]})])],"isStart":true})]}),makeQuery(id+"F42.opRevolve","SWEPT_FACE",FACE,{"disambiguationData":[OSD([sQuery(id+"F41.wireOp",EDGE,"E32")])]})]});
            var Q15;
            Q15=makeQuery(id+"F42.boolean.opBoolean","INTERSECT",EDGE,{"disambiguationData":[OD(6.0)],"derivedFrom":[makeQuery(id+"F20.boolean.opBoolean","MERGE",FACE,{"derivedFrom":[makeQuery(id+"F19.boolean.opBoolean","MERGE",FACE,{"derivedFrom":[makeQuery(id+"F18.boolean.opBoolean","MERGE",FACE,{"derivedFrom":[makeQuery(id+"F17.boolean.opBoolean","MERGE",FACE,{"derivedFrom":[makeQuery(id+"F16.boolean.opBoolean","MERGE",FACE,{"derivedFrom":[makeQuery(id+"F15.boolean.opBoolean","MERGE",FACE,{"derivedFrom":[makeQuery(id+"F14.boolean.opBoolean","MERGE",FACE,{"derivedFrom":[makeQuery(id+"F13.boolean.opBoolean","MERGE",FACE,{"derivedFrom":[makeQuery(id+"F12.boolean.opBoolean","MERGE",FACE,{"derivedFrom":[makeQuery(id+"F11.boolean.opBoolean","MERGE",FACE,{"derivedFrom":[makeQuery(id+"F10.boolean.opBoolean","MERGE",FACE,{"derivedFrom":[makeQuery(id+"F9.boolean.opBoolean","MERGE",FACE,{"derivedFrom":[makeQuery(id+"F8.boolean.opBoolean","MERGE",FACE,{"derivedFrom":[makeQuery(id+"F7.boolean.opBoolean","MERGE",FACE,{"derivedFrom":[makeQuery(id+"F6.boolean.opBoolean","MERGE",FACE,{"derivedFrom":[makeQuery(id+"F5.boolean.opBoolean","MERGE",FACE,{"derivedFrom":[makeQuery(id+"F1.opRevolve","SWEPT_FACE",FACE,{"disambiguationData":[OSD([sQuery(id+"F0.wireOp",EDGE,"E14")])]}),makeQuery(id+"F5.opLoft","CAP_FACE",FACE,{"disambiguationData":[OSD([makeQuery(id+"F4.imprint","IMPRINT",FACE,{"disambiguationData":[TD([[makeQuery(id+"F4.imprint","IMPRINT",EDGE,{"derivedFrom":sQuery(id+"F4.wireOp",EDGE,"E21")}),1.0]])]})])],"isStart":true})]}),makeQuery(id+"F6.opLoft","CAP_FACE",FACE,{"disambiguationData":[OSD([makeQuery(id+"F4.imprint","IMPRINT",FACE,{"disambiguationData":[TD([[makeQuery(id+"F4.imprint","IMPRINT",EDGE,{"derivedFrom":sQuery(id+"F4.wireOp",EDGE,"E26.15.0")}),1.0]])]})])],"isStart":true})]}),makeQuery(id+"F7.opLoft","CAP_FACE",FACE,{"disambiguationData":[OSD([makeQuery(id+"F4.imprint","IMPRINT",FACE,{"disambiguationData":[TD([[makeQuery(id+"F4.imprint","IMPRINT",EDGE,{"derivedFrom":sQuery(id+"F4.wireOp",EDGE,"E26.14.0")}),1.0]])]})])],"isStart":true})]}),makeQuery(id+"F8.opLoft","CAP_FACE",FACE,{"disambiguationData":[OSD([makeQuery(id+"F4.imprint","IMPRINT",FACE,{"disambiguationData":[TD([[makeQuery(id+"F4.imprint","IMPRINT",EDGE,{"derivedFrom":sQuery(id+"F4.wireOp",EDGE,"E26.13.0")}),1.0]])]})])],"isStart":true})]}),makeQuery(id+"F9.opLoft","CAP_FACE",FACE,{"disambiguationData":[OSD([makeQuery(id+"F4.imprint","IMPRINT",FACE,{"disambiguationData":[TD([[makeQuery(id+"F4.imprint","IMPRINT",EDGE,{"derivedFrom":sQuery(id+"F4.wireOp",EDGE,"E26.12.0")}),1.0]])]})])],"isStart":true})]}),makeQuery(id+"F10.opLoft","CAP_FACE",FACE,{"disambiguationData":[OSD([makeQuery(id+"F4.imprint","IMPRINT",FACE,{"disambiguationData":[TD([[makeQuery(id+"F4.imprint","IMPRINT",EDGE,{"derivedFrom":sQuery(id+"F4.wireOp",EDGE,"E26.11.0")}),1.0]])]})])],"isStart":true})]}),makeQuery(id+"F11.opLoft","CAP_FACE",FACE,{"disambiguationData":[OSD([makeQuery(id+"F4.imprint","IMPRINT",FACE,{"disambiguationData":[TD([[makeQuery(id+"F4.imprint","IMPRINT",EDGE,{"derivedFrom":sQuery(id+"F4.wireOp",EDGE,"E26.10.0")}),1.0]])]})])],"isStart":true})]}),makeQuery(id+"F12.opLoft","CAP_FACE",FACE,{"disambiguationData":[OSD([makeQuery(id+"F4.imprint","IMPRINT",FACE,{"disambiguationData":[TD([[makeQuery(id+"F4.imprint","IMPRINT",EDGE,{"derivedFrom":sQuery(id+"F4.wireOp",EDGE,"E26.9.0")}),1.0]])]})])],"isStart":true})]}),makeQuery(id+"F13.opLoft","CAP_FACE",FACE,{"disambiguationData":[OSD([makeQuery(id+"F4.imprint","IMPRINT",FACE,{"disambiguationData":[TD([[makeQuery(id+"F4.imprint","IMPRINT",EDGE,{"derivedFrom":sQuery(id+"F4.wireOp",EDGE,"E26.8.0")}),1.0]])]})])],"isStart":true})]}),makeQuery(id+"F14.opLoft","CAP_FACE",FACE,{"disambiguationData":[OSD([makeQuery(id+"F4.imprint","IMPRINT",FACE,{"disambiguationData":[TD([[makeQuery(id+"F4.imprint","IMPRINT",EDGE,{"derivedFrom":sQuery(id+"F4.wireOp",EDGE,"E26.7.0")}),1.0]])]})])],"isStart":true})]}),makeQuery(id+"F15.opLoft","CAP_FACE",FACE,{"disambiguationData":[OSD([makeQuery(id+"F4.imprint","IMPRINT",FACE,{"disambiguationData":[TD([[makeQuery(id+"F4.imprint","IMPRINT",EDGE,{"derivedFrom":sQuery(id+"F4.wireOp",EDGE,"E26.6.0")}),1.0]])]})])],"isStart":true})]}),makeQuery(id+"F16.opLoft","CAP_FACE",FACE,{"disambiguationData":[OSD([makeQuery(id+"F4.imprint","IMPRINT",FACE,{"disambiguationData":[TD([[makeQuery(id+"F4.imprint","IMPRINT",EDGE,{"derivedFrom":sQuery(id+"F4.wireOp",EDGE,"E26.5.0")}),1.0]])]})])],"isStart":true})]}),makeQuery(id+"F17.opLoft","CAP_FACE",FACE,{"disambiguationData":[OSD([makeQuery(id+"F4.imprint","IMPRINT",FACE,{"disambiguationData":[TD([[makeQuery(id+"F4.imprint","IMPRINT",EDGE,{"derivedFrom":sQuery(id+"F4.wireOp",EDGE,"E26.4.0")}),1.0]])]})])],"isStart":true})]}),makeQuery(id+"F18.opLoft","CAP_FACE",FACE,{"disambiguationData":[OSD([makeQuery(id+"F4.imprint","IMPRINT",FACE,{"disambiguationData":[TD([[makeQuery(id+"F4.imprint","IMPRINT",EDGE,{"derivedFrom":sQuery(id+"F4.wireOp",EDGE,"E26.3.0")}),1.0]])]})])],"isStart":true})]}),makeQuery(id+"F19.opLoft","CAP_FACE",FACE,{"disambiguationData":[OSD([makeQuery(id+"F4.imprint","IMPRINT",FACE,{"disambiguationData":[TD([[makeQuery(id+"F4.imprint","IMPRINT",EDGE,{"derivedFrom":sQuery(id+"F4.wireOp",EDGE,"E26.2.0")}),1.0]])]})])],"isStart":true})]}),makeQuery(id+"F20.opLoft","CAP_FACE",FACE,{"disambiguationData":[OSD([makeQuery(id+"F4.imprint","IMPRINT",FACE,{"disambiguationData":[TD([[makeQuery(id+"F4.imprint","IMPRINT",EDGE,{"derivedFrom":sQuery(id+"F4.wireOp",EDGE,"E26.1.0")}),1.0]])]})])],"isStart":true})]}),makeQuery(id+"F42.opRevolve","SWEPT_FACE",FACE,{"disambiguationData":[OSD([sQuery(id+"F41.wireOp",EDGE,"E32")])]})]});
            var Q16;
            Q16=makeQuery(id+"F42.boolean.opBoolean","INTERSECT",EDGE,{"derivedFrom":[makeQuery(id+"F27.opLoft","CAP_FACE",FACE,{"disambiguationData":[OSD([makeQuery(id+"F22.imprint","IMPRINT",FACE,{"disambiguationData":[TD([[makeQuery(id+"F22.imprint","IMPRINT",EDGE,{"derivedFrom":sQuery(id+"F22.wireOp",EDGE,"E28.4.0")}),-1.0]])]})])],"isStart":true}),makeQuery(id+"F42.opRevolve","SWEPT_FACE",FACE,{"disambiguationData":[OSD([sQuery(id+"F41.wireOp",EDGE,"E32")])]})]});
            var Q17;
            Q17=makeQuery(id+"F42.boolean.opBoolean","INTERSECT",EDGE,{"derivedFrom":[makeQuery(id+"F26.opLoft","CAP_FACE",FACE,{"disambiguationData":[OSD([makeQuery(id+"F22.imprint","IMPRINT",FACE,{"disambiguationData":[TD([[makeQuery(id+"F22.imprint","IMPRINT",EDGE,{"derivedFrom":sQuery(id+"F22.wireOp",EDGE,"E28.3.0")}),-1.0]])]})])],"isStart":true}),makeQuery(id+"F42.opRevolve","SWEPT_FACE",FACE,{"disambiguationData":[OSD([sQuery(id+"F41.wireOp",EDGE,"E32")])]})]});
            var Q18;
            Q18=makeQuery(id+"F42.boolean.opBoolean","INTERSECT",EDGE,{"derivedFrom":[makeQuery(id+"F25.opLoft","CAP_FACE",FACE,{"disambiguationData":[OSD([makeQuery(id+"F22.imprint","IMPRINT",FACE,{"disambiguationData":[TD([[makeQuery(id+"F22.imprint","IMPRINT",EDGE,{"derivedFrom":sQuery(id+"F22.wireOp",EDGE,"E28.2.0")}),-1.0]])]})])],"isStart":true}),makeQuery(id+"F42.opRevolve","SWEPT_FACE",FACE,{"disambiguationData":[OSD([sQuery(id+"F41.wireOp",EDGE,"E32")])]})]});
            var Q19;
            Q19=makeQuery(id+"F42.boolean.opBoolean","INTERSECT",EDGE,{"derivedFrom":[makeQuery(id+"F24.opLoft","CAP_FACE",FACE,{"disambiguationData":[OSD([makeQuery(id+"F22.imprint","IMPRINT",FACE,{"disambiguationData":[TD([[makeQuery(id+"F22.imprint","IMPRINT",EDGE,{"derivedFrom":sQuery(id+"F22.wireOp",EDGE,"E28.1.0")}),-1.0]])]})])],"isStart":true}),makeQuery(id+"F42.opRevolve","SWEPT_FACE",FACE,{"disambiguationData":[OSD([sQuery(id+"F41.wireOp",EDGE,"E32")])]})]});
            var Q20;
            Q20=makeQuery(id+"F42.boolean.opBoolean","INTERSECT",EDGE,{"derivedFrom":[makeQuery(id+"F23.opLoft","CAP_FACE",FACE,{"disambiguationData":[OSD([makeQuery(id+"F22.imprint","IMPRINT",FACE,{"disambiguationData":[TD([[makeQuery(id+"F22.imprint","IMPRINT",EDGE,{"derivedFrom":sQuery(id+"F22.wireOp",EDGE,"E27.bottom")}),1.0]])]})])],"isStart":true}),makeQuery(id+"F42.opRevolve","SWEPT_FACE",FACE,{"disambiguationData":[OSD([sQuery(id+"F41.wireOp",EDGE,"E32")])]})]});
            var Q21;
            Q21=makeQuery(id+"F42.boolean.opBoolean","INTERSECT",EDGE,{"derivedFrom":[makeQuery(id+"F38.opLoft","CAP_FACE",FACE,{"disambiguationData":[OSD([makeQuery(id+"F22.imprint","IMPRINT",FACE,{"disambiguationData":[TD([[makeQuery(id+"F22.imprint","IMPRINT",EDGE,{"derivedFrom":sQuery(id+"F22.wireOp",EDGE,"E28.15.0")}),-1.0]])]})])],"isStart":true}),makeQuery(id+"F42.opRevolve","SWEPT_FACE",FACE,{"disambiguationData":[OSD([sQuery(id+"F41.wireOp",EDGE,"E32")])]})]});
            var Q22;
            Q22=makeQuery(id+"F42.boolean.opBoolean","INTERSECT",EDGE,{"derivedFrom":[makeQuery(id+"F37.opLoft","CAP_FACE",FACE,{"disambiguationData":[OSD([makeQuery(id+"F22.imprint","IMPRINT",FACE,{"disambiguationData":[TD([[makeQuery(id+"F22.imprint","IMPRINT",EDGE,{"derivedFrom":sQuery(id+"F22.wireOp",EDGE,"E28.14.0")}),-1.0]])]})])],"isStart":true}),makeQuery(id+"F42.opRevolve","SWEPT_FACE",FACE,{"disambiguationData":[OSD([sQuery(id+"F41.wireOp",EDGE,"E32")])]})]});
            var Q23;
            Q23=makeQuery(id+"F42.boolean.opBoolean","INTERSECT",EDGE,{"derivedFrom":[makeQuery(id+"F36.opLoft","CAP_FACE",FACE,{"disambiguationData":[OSD([makeQuery(id+"F22.imprint","IMPRINT",FACE,{"disambiguationData":[TD([[makeQuery(id+"F22.imprint","IMPRINT",EDGE,{"derivedFrom":sQuery(id+"F22.wireOp",EDGE,"E28.13.0")}),-1.0]])]})])],"isStart":true}),makeQuery(id+"F42.opRevolve","SWEPT_FACE",FACE,{"disambiguationData":[OSD([sQuery(id+"F41.wireOp",EDGE,"E32")])]})]});
            var Q24;
            Q24=makeQuery(id+"F42.boolean.opBoolean","INTERSECT",EDGE,{"derivedFrom":[makeQuery(id+"F35.opLoft","CAP_FACE",FACE,{"disambiguationData":[OSD([makeQuery(id+"F22.imprint","IMPRINT",FACE,{"disambiguationData":[TD([[makeQuery(id+"F22.imprint","IMPRINT",EDGE,{"derivedFrom":sQuery(id+"F22.wireOp",EDGE,"E28.12.0")}),-1.0]])]})])],"isStart":true}),makeQuery(id+"F42.opRevolve","SWEPT_FACE",FACE,{"disambiguationData":[OSD([sQuery(id+"F41.wireOp",EDGE,"E32")])]})]});
            var Q25;
            Q25=makeQuery(id+"F42.boolean.opBoolean","INTERSECT",EDGE,{"derivedFrom":[makeQuery(id+"F34.opLoft","CAP_FACE",FACE,{"disambiguationData":[OSD([makeQuery(id+"F22.imprint","IMPRINT",FACE,{"disambiguationData":[TD([[makeQuery(id+"F22.imprint","IMPRINT",EDGE,{"derivedFrom":sQuery(id+"F22.wireOp",EDGE,"E28.11.0")}),-1.0]])]})])],"isStart":true}),makeQuery(id+"F42.opRevolve","SWEPT_FACE",FACE,{"disambiguationData":[OSD([sQuery(id+"F41.wireOp",EDGE,"E32")])]})]});
            var Q26;
            Q26=makeQuery(id+"F42.boolean.opBoolean","INTERSECT",EDGE,{"derivedFrom":[makeQuery(id+"F33.opLoft","CAP_FACE",FACE,{"disambiguationData":[OSD([makeQuery(id+"F22.imprint","IMPRINT",FACE,{"disambiguationData":[TD([[makeQuery(id+"F22.imprint","IMPRINT",EDGE,{"derivedFrom":sQuery(id+"F22.wireOp",EDGE,"E28.10.0")}),-1.0]])]})])],"isStart":true}),makeQuery(id+"F42.opRevolve","SWEPT_FACE",FACE,{"disambiguationData":[OSD([sQuery(id+"F41.wireOp",EDGE,"E32")])]})]});
            var Q27;
            Q27=makeQuery(id+"F42.boolean.opBoolean","INTERSECT",EDGE,{"derivedFrom":[makeQuery(id+"F32.opLoft","CAP_FACE",FACE,{"disambiguationData":[OSD([makeQuery(id+"F22.imprint","IMPRINT",FACE,{"disambiguationData":[TD([[makeQuery(id+"F22.imprint","IMPRINT",EDGE,{"derivedFrom":sQuery(id+"F22.wireOp",EDGE,"E28.9.0")}),-1.0]])]})])],"isStart":true}),makeQuery(id+"F42.opRevolve","SWEPT_FACE",FACE,{"disambiguationData":[OSD([sQuery(id+"F41.wireOp",EDGE,"E32")])]})]});
            var Q28;
            Q28=makeQuery(id+"F42.boolean.opBoolean","INTERSECT",EDGE,{"derivedFrom":[makeQuery(id+"F31.opLoft","CAP_FACE",FACE,{"disambiguationData":[OSD([makeQuery(id+"F22.imprint","IMPRINT",FACE,{"disambiguationData":[TD([[makeQuery(id+"F22.imprint","IMPRINT",EDGE,{"derivedFrom":sQuery(id+"F22.wireOp",EDGE,"E28.8.0")}),-1.0]])]})])],"isStart":true}),makeQuery(id+"F42.opRevolve","SWEPT_FACE",FACE,{"disambiguationData":[OSD([sQuery(id+"F41.wireOp",EDGE,"E32")])]})]});
            var Q29;
            Q29=makeQuery(id+"F42.boolean.opBoolean","INTERSECT",EDGE,{"derivedFrom":[makeQuery(id+"F30.opLoft","CAP_FACE",FACE,{"disambiguationData":[OSD([makeQuery(id+"F22.imprint","IMPRINT",FACE,{"disambiguationData":[TD([[makeQuery(id+"F22.imprint","IMPRINT",EDGE,{"derivedFrom":sQuery(id+"F22.wireOp",EDGE,"E28.7.0")}),-1.0]])]})])],"isStart":true}),makeQuery(id+"F42.opRevolve","SWEPT_FACE",FACE,{"disambiguationData":[OSD([sQuery(id+"F41.wireOp",EDGE,"E32")])]})]});
            var Q30;
            Q30=makeQuery(id+"F42.boolean.opBoolean","INTERSECT",EDGE,{"derivedFrom":[makeQuery(id+"F29.opLoft","CAP_FACE",FACE,{"disambiguationData":[OSD([makeQuery(id+"F22.imprint","IMPRINT",FACE,{"disambiguationData":[TD([[makeQuery(id+"F22.imprint","IMPRINT",EDGE,{"derivedFrom":sQuery(id+"F22.wireOp",EDGE,"E28.6.0")}),-1.0]])]})])],"isStart":true}),makeQuery(id+"F42.opRevolve","SWEPT_FACE",FACE,{"disambiguationData":[OSD([sQuery(id+"F41.wireOp",EDGE,"E32")])]})]});
            var Q31;
            Q31=makeQuery(id+"F42.boolean.opBoolean","INTERSECT",EDGE,{"derivedFrom":[makeQuery(id+"F28.opLoft","CAP_FACE",FACE,{"disambiguationData":[OSD([makeQuery(id+"F22.imprint","IMPRINT",FACE,{"disambiguationData":[TD([[makeQuery(id+"F22.imprint","IMPRINT",EDGE,{"derivedFrom":sQuery(id+"F22.wireOp",EDGE,"E28.5.0")}),-1.0]])]})])],"isStart":true}),makeQuery(id+"F42.opRevolve","SWEPT_FACE",FACE,{"disambiguationData":[OSD([sQuery(id+"F41.wireOp",EDGE,"E32")])]})]});
            fillet(context, id + "F43", {"entities" : qUnion([Q0, Q1, Q2, Q3, Q4, Q5, Q6, Q7, Q8, Q9, Q10, Q11, Q12, Q13, Q14, Q15, Q16, Q17, Q18, Q19, Q20, Q21, Q22, Q23, Q24, Q25, Q26, Q27, Q28, Q29, Q30, Q31]), "radius" : 12 * mm, "tangentPropagation" : true, "allowEdgeOverflow" : false});
        }
        {
            var Q0;
            Q0=makeQuery(id+"F40.boolean.opBoolean","INTERSECT",EDGE,{"derivedFrom":[makeQuery(id+"F20.opLoft","SWEPT_FACE",FACE,{"disambiguationData":[OSD([sQuery(id+"F3.wireOp",EDGE,"E20.1.1"),sQuery(id+"F3.wireOp",EDGE,"E20.1.2"),sQuery(id+"F3.wireOp",EDGE,"E20.1.3"),sQuery(id+"F4.wireOp",EDGE,"E26.1.1"),sQuery(id+"F4.wireOp",EDGE,"E26.1.2"),sQuery(id+"F4.wireOp",EDGE,"E26.1.3")])]}),makeQuery(id+"F40.opExtrude","CAP_FACE",FACE,{"disambiguationData":[OSD([sQuery(id+"F39.wireOp",EDGE,"E29"),sQuery(id+"F39.wireOp",EDGE,"E30")])],"isStart":false})]});
            var Q1;
            Q1=makeQuery(id+"F40.boolean.opBoolean","INTERSECT",EDGE,{"derivedFrom":[makeQuery(id+"F32.opLoft","SWEPT_FACE",FACE,{"disambiguationData":[OSD([sQuery(id+"F3.wireOp",EDGE,"E20.1.1"),sQuery(id+"F3.wireOp",EDGE,"E20.1.2"),sQuery(id+"F3.wireOp",EDGE,"E20.1.3"),sQuery(id+"F22.wireOp",EDGE,"E28.9.0"),sQuery(id+"F22.wireOp",EDGE,"E28.9.2"),sQuery(id+"F22.wireOp",EDGE,"E28.9.3")])]}),makeQuery(id+"F40.opExtrude","CAP_FACE",FACE,{"disambiguationData":[OSD([sQuery(id+"F39.wireOp",EDGE,"E29"),sQuery(id+"F39.wireOp",EDGE,"E30")])],"isStart":true})]});
            var Q2;
            Q2=makeQuery(id+"F40.boolean.opBoolean","INTERSECT",EDGE,{"derivedFrom":[makeQuery(id+"F5.opLoft","SWEPT_FACE",FACE,{"disambiguationData":[OSD([sQuery(id+"F3.wireOp",EDGE,"E18.bottom"),sQuery(id+"F3.wireOp",EDGE,"E18.top"),sQuery(id+"F3.wireOp",EDGE,"E18.right"),sQuery(id+"F4.wireOp",EDGE,"E22"),sQuery(id+"F4.wireOp",EDGE,"E23"),sQuery(id+"F4.wireOp",EDGE,"E24")])]}),makeQuery(id+"F40.opExtrude","CAP_FACE",FACE,{"disambiguationData":[OSD([sQuery(id+"F39.wireOp",EDGE,"E29"),sQuery(id+"F39.wireOp",EDGE,"E30")])],"isStart":false})]});
            var Q3;
            Q3=makeQuery(id+"F40.boolean.opBoolean","INTERSECT",EDGE,{"derivedFrom":[makeQuery(id+"F31.opLoft","SWEPT_FACE",FACE,{"disambiguationData":[OSD([sQuery(id+"F3.wireOp",EDGE,"E18.bottom"),sQuery(id+"F3.wireOp",EDGE,"E18.top"),sQuery(id+"F3.wireOp",EDGE,"E18.right"),sQuery(id+"F22.wireOp",EDGE,"E28.8.0"),sQuery(id+"F22.wireOp",EDGE,"E28.8.2"),sQuery(id+"F22.wireOp",EDGE,"E28.8.3")])]}),makeQuery(id+"F40.opExtrude","CAP_FACE",FACE,{"disambiguationData":[OSD([sQuery(id+"F39.wireOp",EDGE,"E29"),sQuery(id+"F39.wireOp",EDGE,"E30")])],"isStart":true})]});
            var Q4;
            Q4=makeQuery(id+"F40.boolean.opBoolean","INTERSECT",EDGE,{"derivedFrom":[makeQuery(id+"F6.opLoft","SWEPT_FACE",FACE,{"disambiguationData":[OSD([sQuery(id+"F3.wireOp",EDGE,"E20.15.1"),sQuery(id+"F3.wireOp",EDGE,"E20.15.2"),sQuery(id+"F3.wireOp",EDGE,"E20.15.3"),sQuery(id+"F4.wireOp",EDGE,"E26.15.1"),sQuery(id+"F4.wireOp",EDGE,"E26.15.2"),sQuery(id+"F4.wireOp",EDGE,"E26.15.3")])]}),makeQuery(id+"F40.opExtrude","CAP_FACE",FACE,{"disambiguationData":[OSD([sQuery(id+"F39.wireOp",EDGE,"E29"),sQuery(id+"F39.wireOp",EDGE,"E30")])],"isStart":false})]});
            var Q5;
            Q5=makeQuery(id+"F40.boolean.opBoolean","INTERSECT",EDGE,{"derivedFrom":[makeQuery(id+"F30.opLoft","SWEPT_FACE",FACE,{"disambiguationData":[OSD([sQuery(id+"F3.wireOp",EDGE,"E20.15.1"),sQuery(id+"F3.wireOp",EDGE,"E20.15.2"),sQuery(id+"F3.wireOp",EDGE,"E20.15.3"),sQuery(id+"F22.wireOp",EDGE,"E28.7.0"),sQuery(id+"F22.wireOp",EDGE,"E28.7.2"),sQuery(id+"F22.wireOp",EDGE,"E28.7.3")])]}),makeQuery(id+"F40.opExtrude","CAP_FACE",FACE,{"disambiguationData":[OSD([sQuery(id+"F39.wireOp",EDGE,"E29"),sQuery(id+"F39.wireOp",EDGE,"E30")])],"isStart":true})]});
            var Q6;
            Q6=makeQuery(id+"F40.boolean.opBoolean","INTERSECT",EDGE,{"derivedFrom":[makeQuery(id+"F29.opLoft","SWEPT_FACE",FACE,{"disambiguationData":[OSD([sQuery(id+"F3.wireOp",EDGE,"E20.14.1"),sQuery(id+"F3.wireOp",EDGE,"E20.14.2"),sQuery(id+"F3.wireOp",EDGE,"E20.14.3"),sQuery(id+"F22.wireOp",EDGE,"E28.6.0"),sQuery(id+"F22.wireOp",EDGE,"E28.6.2"),sQuery(id+"F22.wireOp",EDGE,"E28.6.3")])]}),makeQuery(id+"F40.opExtrude","CAP_FACE",FACE,{"disambiguationData":[OSD([sQuery(id+"F39.wireOp",EDGE,"E29"),sQuery(id+"F39.wireOp",EDGE,"E30")])],"isStart":true})]});
            var Q7;
            Q7=makeQuery(id+"F40.boolean.opBoolean","INTERSECT",EDGE,{"derivedFrom":[makeQuery(id+"F28.opLoft","SWEPT_FACE",FACE,{"disambiguationData":[OSD([sQuery(id+"F3.wireOp",EDGE,"E20.13.1"),sQuery(id+"F3.wireOp",EDGE,"E20.13.2"),sQuery(id+"F3.wireOp",EDGE,"E20.13.3"),sQuery(id+"F22.wireOp",EDGE,"E28.5.0"),sQuery(id+"F22.wireOp",EDGE,"E28.5.2"),sQuery(id+"F22.wireOp",EDGE,"E28.5.3")])]}),makeQuery(id+"F40.opExtrude","CAP_FACE",FACE,{"disambiguationData":[OSD([sQuery(id+"F39.wireOp",EDGE,"E29"),sQuery(id+"F39.wireOp",EDGE,"E30")])],"isStart":true})]});
            var Q8;
            Q8=makeQuery(id+"F40.boolean.opBoolean","INTERSECT",EDGE,{"derivedFrom":[makeQuery(id+"F27.opLoft","SWEPT_FACE",FACE,{"disambiguationData":[OSD([sQuery(id+"F3.wireOp",EDGE,"E20.12.1"),sQuery(id+"F3.wireOp",EDGE,"E20.12.2"),sQuery(id+"F3.wireOp",EDGE,"E20.12.3"),sQuery(id+"F22.wireOp",EDGE,"E28.4.0"),sQuery(id+"F22.wireOp",EDGE,"E28.4.2"),sQuery(id+"F22.wireOp",EDGE,"E28.4.3")])]}),makeQuery(id+"F40.opExtrude","CAP_FACE",FACE,{"disambiguationData":[OSD([sQuery(id+"F39.wireOp",EDGE,"E29"),sQuery(id+"F39.wireOp",EDGE,"E30")])],"isStart":true})]});
            var Q9;
            Q9=makeQuery(id+"F40.boolean.opBoolean","INTERSECT",EDGE,{"derivedFrom":[makeQuery(id+"F26.opLoft","SWEPT_FACE",FACE,{"disambiguationData":[OSD([sQuery(id+"F3.wireOp",EDGE,"E20.11.1"),sQuery(id+"F3.wireOp",EDGE,"E20.11.2"),sQuery(id+"F3.wireOp",EDGE,"E20.11.3"),sQuery(id+"F22.wireOp",EDGE,"E28.3.0"),sQuery(id+"F22.wireOp",EDGE,"E28.3.2"),sQuery(id+"F22.wireOp",EDGE,"E28.3.3")])]}),makeQuery(id+"F40.opExtrude","CAP_FACE",FACE,{"disambiguationData":[OSD([sQuery(id+"F39.wireOp",EDGE,"E29"),sQuery(id+"F39.wireOp",EDGE,"E30")])],"isStart":true})]});
            var Q10;
            Q10=makeQuery(id+"F40.boolean.opBoolean","INTERSECT",EDGE,{"derivedFrom":[makeQuery(id+"F25.opLoft","SWEPT_FACE",FACE,{"disambiguationData":[OSD([sQuery(id+"F3.wireOp",EDGE,"E20.10.1"),sQuery(id+"F3.wireOp",EDGE,"E20.10.2"),sQuery(id+"F3.wireOp",EDGE,"E20.10.3"),sQuery(id+"F22.wireOp",EDGE,"E28.2.0"),sQuery(id+"F22.wireOp",EDGE,"E28.2.2"),sQuery(id+"F22.wireOp",EDGE,"E28.2.3")])]}),makeQuery(id+"F40.opExtrude","CAP_FACE",FACE,{"disambiguationData":[OSD([sQuery(id+"F39.wireOp",EDGE,"E29"),sQuery(id+"F39.wireOp",EDGE,"E30")])],"isStart":true})]});
            var Q11;
            Q11=makeQuery(id+"F40.boolean.opBoolean","INTERSECT",EDGE,{"derivedFrom":[makeQuery(id+"F24.opLoft","SWEPT_FACE",FACE,{"disambiguationData":[OSD([sQuery(id+"F3.wireOp",EDGE,"E20.9.1"),sQuery(id+"F3.wireOp",EDGE,"E20.9.2"),sQuery(id+"F3.wireOp",EDGE,"E20.9.3"),sQuery(id+"F22.wireOp",EDGE,"E28.1.0"),sQuery(id+"F22.wireOp",EDGE,"E28.1.2"),sQuery(id+"F22.wireOp",EDGE,"E28.1.3")])]}),makeQuery(id+"F40.opExtrude","CAP_FACE",FACE,{"disambiguationData":[OSD([sQuery(id+"F39.wireOp",EDGE,"E29"),sQuery(id+"F39.wireOp",EDGE,"E30")])],"isStart":true})]});
            var Q12;
            Q12=makeQuery(id+"F40.boolean.opBoolean","INTERSECT",EDGE,{"derivedFrom":[makeQuery(id+"F23.opLoft","SWEPT_FACE",FACE,{"disambiguationData":[OSD([sQuery(id+"F3.wireOp",EDGE,"E20.8.1"),sQuery(id+"F3.wireOp",EDGE,"E20.8.2"),sQuery(id+"F3.wireOp",EDGE,"E20.8.3"),sQuery(id+"F22.wireOp",EDGE,"E27.bottom"),sQuery(id+"F22.wireOp",EDGE,"E27.top"),sQuery(id+"F22.wireOp",EDGE,"E27.left")])]}),makeQuery(id+"F40.opExtrude","CAP_FACE",FACE,{"disambiguationData":[OSD([sQuery(id+"F39.wireOp",EDGE,"E29"),sQuery(id+"F39.wireOp",EDGE,"E30")])],"isStart":true})]});
            var Q13;
            Q13=makeQuery(id+"F40.boolean.opBoolean","INTERSECT",EDGE,{"derivedFrom":[makeQuery(id+"F38.opLoft","SWEPT_FACE",FACE,{"disambiguationData":[OSD([sQuery(id+"F3.wireOp",EDGE,"E20.7.1"),sQuery(id+"F3.wireOp",EDGE,"E20.7.2"),sQuery(id+"F3.wireOp",EDGE,"E20.7.3"),sQuery(id+"F22.wireOp",EDGE,"E28.15.0"),sQuery(id+"F22.wireOp",EDGE,"E28.15.2"),sQuery(id+"F22.wireOp",EDGE,"E28.15.3")])]}),makeQuery(id+"F40.opExtrude","CAP_FACE",FACE,{"disambiguationData":[OSD([sQuery(id+"F39.wireOp",EDGE,"E29"),sQuery(id+"F39.wireOp",EDGE,"E30")])],"isStart":true})]});
            var Q14;
            Q14=makeQuery(id+"F40.boolean.opBoolean","INTERSECT",EDGE,{"derivedFrom":[makeQuery(id+"F37.opLoft","SWEPT_FACE",FACE,{"disambiguationData":[OSD([sQuery(id+"F3.wireOp",EDGE,"E20.6.1"),sQuery(id+"F3.wireOp",EDGE,"E20.6.2"),sQuery(id+"F3.wireOp",EDGE,"E20.6.3"),sQuery(id+"F22.wireOp",EDGE,"E28.14.0"),sQuery(id+"F22.wireOp",EDGE,"E28.14.2"),sQuery(id+"F22.wireOp",EDGE,"E28.14.3")])]}),makeQuery(id+"F40.opExtrude","CAP_FACE",FACE,{"disambiguationData":[OSD([sQuery(id+"F39.wireOp",EDGE,"E29"),sQuery(id+"F39.wireOp",EDGE,"E30")])],"isStart":true})]});
            var Q15;
            Q15=makeQuery(id+"F40.boolean.opBoolean","INTERSECT",EDGE,{"derivedFrom":[makeQuery(id+"F36.opLoft","SWEPT_FACE",FACE,{"disambiguationData":[OSD([sQuery(id+"F3.wireOp",EDGE,"E20.5.1"),sQuery(id+"F3.wireOp",EDGE,"E20.5.2"),sQuery(id+"F3.wireOp",EDGE,"E20.5.3"),sQuery(id+"F22.wireOp",EDGE,"E28.13.0"),sQuery(id+"F22.wireOp",EDGE,"E28.13.2"),sQuery(id+"F22.wireOp",EDGE,"E28.13.3")])]}),makeQuery(id+"F40.opExtrude","CAP_FACE",FACE,{"disambiguationData":[OSD([sQuery(id+"F39.wireOp",EDGE,"E29"),sQuery(id+"F39.wireOp",EDGE,"E30")])],"isStart":true})]});
            var Q16;
            Q16=makeQuery(id+"F40.boolean.opBoolean","INTERSECT",EDGE,{"derivedFrom":[makeQuery(id+"F35.opLoft","SWEPT_FACE",FACE,{"disambiguationData":[OSD([sQuery(id+"F3.wireOp",EDGE,"E20.4.1"),sQuery(id+"F3.wireOp",EDGE,"E20.4.2"),sQuery(id+"F3.wireOp",EDGE,"E20.4.3"),sQuery(id+"F22.wireOp",EDGE,"E28.12.0"),sQuery(id+"F22.wireOp",EDGE,"E28.12.2"),sQuery(id+"F22.wireOp",EDGE,"E28.12.3")])]}),makeQuery(id+"F40.opExtrude","CAP_FACE",FACE,{"disambiguationData":[OSD([sQuery(id+"F39.wireOp",EDGE,"E29"),sQuery(id+"F39.wireOp",EDGE,"E30")])],"isStart":true})]});
            var Q17;
            Q17=makeQuery(id+"F40.boolean.opBoolean","INTERSECT",EDGE,{"derivedFrom":[makeQuery(id+"F34.opLoft","SWEPT_FACE",FACE,{"disambiguationData":[OSD([sQuery(id+"F3.wireOp",EDGE,"E20.3.1"),sQuery(id+"F3.wireOp",EDGE,"E20.3.2"),sQuery(id+"F3.wireOp",EDGE,"E20.3.3"),sQuery(id+"F22.wireOp",EDGE,"E28.11.0"),sQuery(id+"F22.wireOp",EDGE,"E28.11.2"),sQuery(id+"F22.wireOp",EDGE,"E28.11.3")])]}),makeQuery(id+"F40.opExtrude","CAP_FACE",FACE,{"disambiguationData":[OSD([sQuery(id+"F39.wireOp",EDGE,"E29"),sQuery(id+"F39.wireOp",EDGE,"E30")])],"isStart":true})]});
            var Q18;
            Q18=makeQuery(id+"F40.boolean.opBoolean","INTERSECT",EDGE,{"derivedFrom":[makeQuery(id+"F33.opLoft","SWEPT_FACE",FACE,{"disambiguationData":[OSD([sQuery(id+"F3.wireOp",EDGE,"E20.2.1"),sQuery(id+"F3.wireOp",EDGE,"E20.2.2"),sQuery(id+"F3.wireOp",EDGE,"E20.2.3"),sQuery(id+"F22.wireOp",EDGE,"E28.10.0"),sQuery(id+"F22.wireOp",EDGE,"E28.10.2"),sQuery(id+"F22.wireOp",EDGE,"E28.10.3")])]}),makeQuery(id+"F40.opExtrude","CAP_FACE",FACE,{"disambiguationData":[OSD([sQuery(id+"F39.wireOp",EDGE,"E29"),sQuery(id+"F39.wireOp",EDGE,"E30")])],"isStart":true})]});
            var Q19;
            Q19=makeQuery(id+"F40.boolean.opBoolean","INTERSECT",EDGE,{"derivedFrom":[makeQuery(id+"F19.opLoft","SWEPT_FACE",FACE,{"disambiguationData":[OSD([sQuery(id+"F3.wireOp",EDGE,"E20.2.1"),sQuery(id+"F3.wireOp",EDGE,"E20.2.2"),sQuery(id+"F3.wireOp",EDGE,"E20.2.3"),sQuery(id+"F4.wireOp",EDGE,"E26.2.1"),sQuery(id+"F4.wireOp",EDGE,"E26.2.2"),sQuery(id+"F4.wireOp",EDGE,"E26.2.3")])]}),makeQuery(id+"F40.opExtrude","CAP_FACE",FACE,{"disambiguationData":[OSD([sQuery(id+"F39.wireOp",EDGE,"E29"),sQuery(id+"F39.wireOp",EDGE,"E30")])],"isStart":false})]});
            var Q20;
            Q20=makeQuery(id+"F40.boolean.opBoolean","INTERSECT",EDGE,{"derivedFrom":[makeQuery(id+"F18.opLoft","SWEPT_FACE",FACE,{"disambiguationData":[OSD([sQuery(id+"F3.wireOp",EDGE,"E20.3.1"),sQuery(id+"F3.wireOp",EDGE,"E20.3.2"),sQuery(id+"F3.wireOp",EDGE,"E20.3.3"),sQuery(id+"F4.wireOp",EDGE,"E26.3.1"),sQuery(id+"F4.wireOp",EDGE,"E26.3.2"),sQuery(id+"F4.wireOp",EDGE,"E26.3.3")])]}),makeQuery(id+"F40.opExtrude","CAP_FACE",FACE,{"disambiguationData":[OSD([sQuery(id+"F39.wireOp",EDGE,"E29"),sQuery(id+"F39.wireOp",EDGE,"E30")])],"isStart":false})]});
            var Q21;
            Q21=makeQuery(id+"F40.boolean.opBoolean","INTERSECT",EDGE,{"derivedFrom":[makeQuery(id+"F17.opLoft","SWEPT_FACE",FACE,{"disambiguationData":[OSD([sQuery(id+"F3.wireOp",EDGE,"E20.4.1"),sQuery(id+"F3.wireOp",EDGE,"E20.4.2"),sQuery(id+"F3.wireOp",EDGE,"E20.4.3"),sQuery(id+"F4.wireOp",EDGE,"E26.4.1"),sQuery(id+"F4.wireOp",EDGE,"E26.4.2"),sQuery(id+"F4.wireOp",EDGE,"E26.4.3")])]}),makeQuery(id+"F40.opExtrude","CAP_FACE",FACE,{"disambiguationData":[OSD([sQuery(id+"F39.wireOp",EDGE,"E29"),sQuery(id+"F39.wireOp",EDGE,"E30")])],"isStart":false})]});
            var Q22;
            Q22=makeQuery(id+"F40.boolean.opBoolean","INTERSECT",EDGE,{"derivedFrom":[makeQuery(id+"F16.opLoft","SWEPT_FACE",FACE,{"disambiguationData":[OSD([sQuery(id+"F3.wireOp",EDGE,"E20.5.1"),sQuery(id+"F3.wireOp",EDGE,"E20.5.2"),sQuery(id+"F3.wireOp",EDGE,"E20.5.3"),sQuery(id+"F4.wireOp",EDGE,"E26.5.1"),sQuery(id+"F4.wireOp",EDGE,"E26.5.2"),sQuery(id+"F4.wireOp",EDGE,"E26.5.3")])]}),makeQuery(id+"F40.opExtrude","CAP_FACE",FACE,{"disambiguationData":[OSD([sQuery(id+"F39.wireOp",EDGE,"E29"),sQuery(id+"F39.wireOp",EDGE,"E30")])],"isStart":false})]});
            var Q23;
            Q23=makeQuery(id+"F40.boolean.opBoolean","INTERSECT",EDGE,{"derivedFrom":[makeQuery(id+"F15.opLoft","SWEPT_FACE",FACE,{"disambiguationData":[OSD([sQuery(id+"F3.wireOp",EDGE,"E20.6.1"),sQuery(id+"F3.wireOp",EDGE,"E20.6.2"),sQuery(id+"F3.wireOp",EDGE,"E20.6.3"),sQuery(id+"F4.wireOp",EDGE,"E26.6.1"),sQuery(id+"F4.wireOp",EDGE,"E26.6.2"),sQuery(id+"F4.wireOp",EDGE,"E26.6.3")])]}),makeQuery(id+"F40.opExtrude","CAP_FACE",FACE,{"disambiguationData":[OSD([sQuery(id+"F39.wireOp",EDGE,"E29"),sQuery(id+"F39.wireOp",EDGE,"E30")])],"isStart":false})]});
            var Q24;
            Q24=makeQuery(id+"F40.boolean.opBoolean","INTERSECT",EDGE,{"derivedFrom":[makeQuery(id+"F14.opLoft","SWEPT_FACE",FACE,{"disambiguationData":[OSD([sQuery(id+"F3.wireOp",EDGE,"E20.7.1"),sQuery(id+"F3.wireOp",EDGE,"E20.7.2"),sQuery(id+"F3.wireOp",EDGE,"E20.7.3"),sQuery(id+"F4.wireOp",EDGE,"E26.7.1"),sQuery(id+"F4.wireOp",EDGE,"E26.7.2"),sQuery(id+"F4.wireOp",EDGE,"E26.7.3")])]}),makeQuery(id+"F40.opExtrude","CAP_FACE",FACE,{"disambiguationData":[OSD([sQuery(id+"F39.wireOp",EDGE,"E29"),sQuery(id+"F39.wireOp",EDGE,"E30")])],"isStart":false})]});
            var Q25;
            Q25=makeQuery(id+"F40.boolean.opBoolean","INTERSECT",EDGE,{"derivedFrom":[makeQuery(id+"F13.opLoft","SWEPT_FACE",FACE,{"disambiguationData":[OSD([sQuery(id+"F3.wireOp",EDGE,"E20.8.1"),sQuery(id+"F3.wireOp",EDGE,"E20.8.2"),sQuery(id+"F3.wireOp",EDGE,"E20.8.3"),sQuery(id+"F4.wireOp",EDGE,"E26.8.1"),sQuery(id+"F4.wireOp",EDGE,"E26.8.2"),sQuery(id+"F4.wireOp",EDGE,"E26.8.3")])]}),makeQuery(id+"F40.opExtrude","CAP_FACE",FACE,{"disambiguationData":[OSD([sQuery(id+"F39.wireOp",EDGE,"E29"),sQuery(id+"F39.wireOp",EDGE,"E30")])],"isStart":false})]});
            var Q26;
            Q26=makeQuery(id+"F40.boolean.opBoolean","INTERSECT",EDGE,{"derivedFrom":[makeQuery(id+"F12.opLoft","SWEPT_FACE",FACE,{"disambiguationData":[OSD([sQuery(id+"F3.wireOp",EDGE,"E20.9.1"),sQuery(id+"F3.wireOp",EDGE,"E20.9.2"),sQuery(id+"F3.wireOp",EDGE,"E20.9.3"),sQuery(id+"F4.wireOp",EDGE,"E26.9.1"),sQuery(id+"F4.wireOp",EDGE,"E26.9.2"),sQuery(id+"F4.wireOp",EDGE,"E26.9.3")])]}),makeQuery(id+"F40.opExtrude","CAP_FACE",FACE,{"disambiguationData":[OSD([sQuery(id+"F39.wireOp",EDGE,"E29"),sQuery(id+"F39.wireOp",EDGE,"E30")])],"isStart":false})]});
            var Q27;
            Q27=makeQuery(id+"F40.boolean.opBoolean","INTERSECT",EDGE,{"derivedFrom":[makeQuery(id+"F11.opLoft","SWEPT_FACE",FACE,{"disambiguationData":[OSD([sQuery(id+"F3.wireOp",EDGE,"E20.10.1"),sQuery(id+"F3.wireOp",EDGE,"E20.10.2"),sQuery(id+"F3.wireOp",EDGE,"E20.10.3"),sQuery(id+"F4.wireOp",EDGE,"E26.10.1"),sQuery(id+"F4.wireOp",EDGE,"E26.10.2"),sQuery(id+"F4.wireOp",EDGE,"E26.10.3")])]}),makeQuery(id+"F40.opExtrude","CAP_FACE",FACE,{"disambiguationData":[OSD([sQuery(id+"F39.wireOp",EDGE,"E29"),sQuery(id+"F39.wireOp",EDGE,"E30")])],"isStart":false})]});
            var Q28;
            Q28=makeQuery(id+"F40.boolean.opBoolean","INTERSECT",EDGE,{"derivedFrom":[makeQuery(id+"F10.opLoft","SWEPT_FACE",FACE,{"disambiguationData":[OSD([sQuery(id+"F3.wireOp",EDGE,"E20.11.1"),sQuery(id+"F3.wireOp",EDGE,"E20.11.2"),sQuery(id+"F3.wireOp",EDGE,"E20.11.3"),sQuery(id+"F4.wireOp",EDGE,"E26.11.1"),sQuery(id+"F4.wireOp",EDGE,"E26.11.2"),sQuery(id+"F4.wireOp",EDGE,"E26.11.3")])]}),makeQuery(id+"F40.opExtrude","CAP_FACE",FACE,{"disambiguationData":[OSD([sQuery(id+"F39.wireOp",EDGE,"E29"),sQuery(id+"F39.wireOp",EDGE,"E30")])],"isStart":false})]});
            var Q29;
            Q29=makeQuery(id+"F40.boolean.opBoolean","INTERSECT",EDGE,{"derivedFrom":[makeQuery(id+"F9.opLoft","SWEPT_FACE",FACE,{"disambiguationData":[OSD([sQuery(id+"F3.wireOp",EDGE,"E20.12.1"),sQuery(id+"F3.wireOp",EDGE,"E20.12.2"),sQuery(id+"F3.wireOp",EDGE,"E20.12.3"),sQuery(id+"F4.wireOp",EDGE,"E26.12.1"),sQuery(id+"F4.wireOp",EDGE,"E26.12.2"),sQuery(id+"F4.wireOp",EDGE,"E26.12.3")])]}),makeQuery(id+"F40.opExtrude","CAP_FACE",FACE,{"disambiguationData":[OSD([sQuery(id+"F39.wireOp",EDGE,"E29"),sQuery(id+"F39.wireOp",EDGE,"E30")])],"isStart":false})]});
            var Q30;
            Q30=makeQuery(id+"F40.boolean.opBoolean","INTERSECT",EDGE,{"derivedFrom":[makeQuery(id+"F8.opLoft","SWEPT_FACE",FACE,{"disambiguationData":[OSD([sQuery(id+"F3.wireOp",EDGE,"E20.13.1"),sQuery(id+"F3.wireOp",EDGE,"E20.13.2"),sQuery(id+"F3.wireOp",EDGE,"E20.13.3"),sQuery(id+"F4.wireOp",EDGE,"E26.13.1"),sQuery(id+"F4.wireOp",EDGE,"E26.13.2"),sQuery(id+"F4.wireOp",EDGE,"E26.13.3")])]}),makeQuery(id+"F40.opExtrude","CAP_FACE",FACE,{"disambiguationData":[OSD([sQuery(id+"F39.wireOp",EDGE,"E29"),sQuery(id+"F39.wireOp",EDGE,"E30")])],"isStart":false})]});
            var Q31;
            Q31=makeQuery(id+"F40.boolean.opBoolean","INTERSECT",EDGE,{"derivedFrom":[makeQuery(id+"F7.opLoft","SWEPT_FACE",FACE,{"disambiguationData":[OSD([sQuery(id+"F3.wireOp",EDGE,"E20.14.1"),sQuery(id+"F3.wireOp",EDGE,"E20.14.2"),sQuery(id+"F3.wireOp",EDGE,"E20.14.3"),sQuery(id+"F4.wireOp",EDGE,"E26.14.1"),sQuery(id+"F4.wireOp",EDGE,"E26.14.2"),sQuery(id+"F4.wireOp",EDGE,"E26.14.3")])]}),makeQuery(id+"F40.opExtrude","CAP_FACE",FACE,{"disambiguationData":[OSD([sQuery(id+"F39.wireOp",EDGE,"E29"),sQuery(id+"F39.wireOp",EDGE,"E30")])],"isStart":false})]});
            fillet(context, id + "F44", {"entities" : qUnion([Q0, Q1, Q2, Q3, Q4, Q5, Q6, Q7, Q8, Q9, Q10, Q11, Q12, Q13, Q14, Q15, Q16, Q17, Q18, Q19, Q20, Q21, Q22, Q23, Q24, Q25, Q26, Q27, Q28, Q29, Q30, Q31]), "radius" : 25 * mm, "tangentPropagation" : true, "allowEdgeOverflow" : false});
        }
        {
            var Q0;
            {var subQ0=makeQuery(id+"F1.opRevolve","SWEPT_FACE",FACE,{"disambiguationData":[OSD([sQuery(id+"F0.wireOp",EDGE,"E10")])]});var subQ1=sQuery(id+"F4.wireOp",EDGE,"E23");var subQ2=sQuery(id+"F4.wireOp",EDGE,"E22");var subQ3=sQuery(id+"F3.wireOp",EDGE,"E18.right");var subQ4=sQuery(id+"F3.wireOp",EDGE,"E18.top");var subQ5=sQuery(id+"F3.wireOp",EDGE,"E18.bottom");var subQ6=makeQuery(id+"F5.opLoft","SWEPT_FACE",FACE,{"disambiguationData":[OSD([subQ5,subQ4,subQ3,subQ2,subQ1,sQuery(id+"F4.wireOp",EDGE,"E24")])]});var subQ13=makeQuery(id+"F40.opExtrude","CAP_FACE",FACE,{"disambiguationData":[OSD([sQuery(id+"F39.wireOp",EDGE,"E29"),sQuery(id+"F39.wireOp",EDGE,"E30")])],"isStart":false});var subQ58=makeQuery(id+"F5.opLoft","CAP_FACE",FACE,{"disambiguationData":[OSD([makeQuery(id+"F3.imprint","IMPRINT",FACE,{"disambiguationData":[TD([[makeQuery(id+"F3.imprint","IMPRINT",EDGE,{"derivedFrom":subQ5}),1.0]])]})])],"isStart":true});Q0=makeQuery(id+"F44.opFillet","BLEND_EDGE",EDGE,{"blendedFrom":[makeQuery(id+"F40.boolean.opBoolean","INTERSECT",EDGE,{"derivedFrom":[subQ6,subQ13]}),makeQuery(id+"F40.boolean.opBoolean","SPLIT",FACE,{"disambiguationData":[TD([subQ0])],"derivedFrom":makeQuery(id+"F31.boolean.opBoolean","SPLIT",FACE,{"disambiguationData":[TD([subQ6])],"derivedFrom":makeQuery(id+"F30.boolean.opBoolean","SPLIT",FACE,{"disambiguationData":[TD([subQ58])],"derivedFrom":makeQuery(id+"F29.boolean.opBoolean","SPLIT",FACE,{"disambiguationData":[TD([subQ58])],"derivedFrom":makeQuery(id+"F28.boolean.opBoolean","SPLIT",FACE,{"disambiguationData":[TD([subQ58])],"derivedFrom":makeQuery(id+"F27.boolean.opBoolean","SPLIT",FACE,{"disambiguationData":[TD([subQ58])],"derivedFrom":makeQuery(id+"F26.boolean.opBoolean","SPLIT",FACE,{"disambiguationData":[TD([subQ58])],"derivedFrom":makeQuery(id+"F25.boolean.opBoolean","SPLIT",FACE,{"disambiguationData":[TD([subQ58])],"derivedFrom":makeQuery(id+"F24.boolean.opBoolean","SPLIT",FACE,{"disambiguationData":[TD([subQ58])],"derivedFrom":makeQuery(id+"F1.opRevolve","SWEPT_FACE",FACE,{"disambiguationData":[OSD([sQuery(id+"F0.wireOp",EDGE,"E13")])]})})})})})})})})})})],"blendedInto":[makeQuery(id+"F40.boolean.opBoolean","SPLIT",FACE,{"disambiguationData":[TD([subQ0])],"derivedFrom":makeQuery(id+"F31.boolean.opBoolean","SPLIT",FACE,{"disambiguationData":[TD([subQ6])],"derivedFrom":makeQuery(id+"F30.boolean.opBoolean","SPLIT",FACE,{"disambiguationData":[TD([subQ58])],"derivedFrom":makeQuery(id+"F29.boolean.opBoolean","SPLIT",FACE,{"disambiguationData":[TD([subQ58])],"derivedFrom":makeQuery(id+"F28.boolean.opBoolean","SPLIT",FACE,{"disambiguationData":[TD([subQ58])],"derivedFrom":makeQuery(id+"F27.boolean.opBoolean","SPLIT",FACE,{"disambiguationData":[TD([subQ58])],"derivedFrom":makeQuery(id+"F26.boolean.opBoolean","SPLIT",FACE,{"disambiguationData":[TD([subQ58])],"derivedFrom":makeQuery(id+"F25.boolean.opBoolean","SPLIT",FACE,{"disambiguationData":[TD([subQ58])],"derivedFrom":makeQuery(id+"F24.boolean.opBoolean","SPLIT",FACE,{"disambiguationData":[TD([subQ58])],"derivedFrom":makeQuery(id+"F1.opRevolve","SWEPT_FACE",FACE,{"disambiguationData":[OSD([sQuery(id+"F0.wireOp",EDGE,"E13")])]})})})})})})})})})})]});}
            var Q1;
            {var subQ0=makeQuery(id+"F1.opRevolve","SWEPT_FACE",FACE,{"disambiguationData":[OSD([sQuery(id+"F0.wireOp",EDGE,"E10")])]});var subQ1=sQuery(id+"F4.wireOp",EDGE,"E23");var subQ2=sQuery(id+"F4.wireOp",EDGE,"E22");var subQ3=sQuery(id+"F3.wireOp",EDGE,"E18.left");var subQ4=sQuery(id+"F3.wireOp",EDGE,"E18.top");var subQ5=sQuery(id+"F3.wireOp",EDGE,"E18.bottom");var subQ6=makeQuery(id+"F5.opLoft","SWEPT_FACE",FACE,{"disambiguationData":[OSD([subQ5,subQ4,subQ3,sQuery(id+"F4.wireOp",EDGE,"E21"),subQ2,subQ1])]});var subQ7=sQuery(id+"F4.wireOp",EDGE,"E26.1.3");var subQ8=sQuery(id+"F4.wireOp",EDGE,"E26.1.2");var subQ9=sQuery(id+"F3.wireOp",EDGE,"E20.1.3");var subQ10=sQuery(id+"F3.wireOp",EDGE,"E20.1.2");var subQ11=sQuery(id+"F3.wireOp",EDGE,"E20.1.1");var subQ12=makeQuery(id+"F20.opLoft","SWEPT_FACE",FACE,{"disambiguationData":[OSD([subQ11,subQ10,subQ9,sQuery(id+"F4.wireOp",EDGE,"E26.1.1"),subQ8,subQ7])]});var subQ13=makeQuery(id+"F40.opExtrude","CAP_FACE",FACE,{"disambiguationData":[OSD([sQuery(id+"F39.wireOp",EDGE,"E29"),sQuery(id+"F39.wireOp",EDGE,"E30")])],"isStart":false});var subQ64=sQuery(id+"F3.wireOp",EDGE,"E20.7.0");var subQ72=makeQuery(id+"F14.opLoft","CAP_FACE",FACE,{"disambiguationData":[OSD([makeQuery(id+"F3.imprint","IMPRINT",FACE,{"disambiguationData":[TD([[makeQuery(id+"F3.imprint","IMPRINT",EDGE,{"derivedFrom":subQ64}),-1.0]])]})])],"isStart":true});var subQ80=makeQuery(id+"F5.opLoft","CAP_FACE",FACE,{"disambiguationData":[OSD([makeQuery(id+"F3.imprint","IMPRINT",FACE,{"disambiguationData":[TD([[makeQuery(id+"F3.imprint","IMPRINT",EDGE,{"derivedFrom":subQ5}),1.0]])]})])],"isStart":true});Q1=makeQuery(id+"F44.opFillet","BLEND_EDGE",EDGE,{"blendedFrom":[makeQuery(id+"F40.boolean.opBoolean","INTERSECT",EDGE,{"derivedFrom":[subQ12,subQ13]}),makeQuery(id+"F40.boolean.opBoolean","SPLIT",FACE,{"disambiguationData":[TD([subQ0])],"derivedFrom":makeQuery(id+"F32.boolean.opBoolean","SPLIT",FACE,{"disambiguationData":[TD([subQ6])],"derivedFrom":makeQuery(id+"F31.boolean.opBoolean","SPLIT",FACE,{"disambiguationData":[TD([subQ72])],"derivedFrom":makeQuery(id+"F30.boolean.opBoolean","SPLIT",FACE,{"disambiguationData":[TD([subQ80])],"derivedFrom":makeQuery(id+"F29.boolean.opBoolean","SPLIT",FACE,{"disambiguationData":[TD([subQ80])],"derivedFrom":makeQuery(id+"F28.boolean.opBoolean","SPLIT",FACE,{"disambiguationData":[TD([subQ80])],"derivedFrom":makeQuery(id+"F27.boolean.opBoolean","SPLIT",FACE,{"disambiguationData":[TD([subQ80])],"derivedFrom":makeQuery(id+"F26.boolean.opBoolean","SPLIT",FACE,{"disambiguationData":[TD([subQ80])],"derivedFrom":makeQuery(id+"F25.boolean.opBoolean","SPLIT",FACE,{"disambiguationData":[TD([subQ80])],"derivedFrom":makeQuery(id+"F24.boolean.opBoolean","SPLIT",FACE,{"disambiguationData":[TD([subQ80])],"derivedFrom":makeQuery(id+"F1.opRevolve","SWEPT_FACE",FACE,{"disambiguationData":[OSD([sQuery(id+"F0.wireOp",EDGE,"E13")])]})})})})})})})})})})})],"blendedInto":[makeQuery(id+"F40.boolean.opBoolean","SPLIT",FACE,{"disambiguationData":[TD([subQ0])],"derivedFrom":makeQuery(id+"F32.boolean.opBoolean","SPLIT",FACE,{"disambiguationData":[TD([subQ6])],"derivedFrom":makeQuery(id+"F31.boolean.opBoolean","SPLIT",FACE,{"disambiguationData":[TD([subQ72])],"derivedFrom":makeQuery(id+"F30.boolean.opBoolean","SPLIT",FACE,{"disambiguationData":[TD([subQ80])],"derivedFrom":makeQuery(id+"F29.boolean.opBoolean","SPLIT",FACE,{"disambiguationData":[TD([subQ80])],"derivedFrom":makeQuery(id+"F28.boolean.opBoolean","SPLIT",FACE,{"disambiguationData":[TD([subQ80])],"derivedFrom":makeQuery(id+"F27.boolean.opBoolean","SPLIT",FACE,{"disambiguationData":[TD([subQ80])],"derivedFrom":makeQuery(id+"F26.boolean.opBoolean","SPLIT",FACE,{"disambiguationData":[TD([subQ80])],"derivedFrom":makeQuery(id+"F25.boolean.opBoolean","SPLIT",FACE,{"disambiguationData":[TD([subQ80])],"derivedFrom":makeQuery(id+"F24.boolean.opBoolean","SPLIT",FACE,{"disambiguationData":[TD([subQ80])],"derivedFrom":makeQuery(id+"F1.opRevolve","SWEPT_FACE",FACE,{"disambiguationData":[OSD([sQuery(id+"F0.wireOp",EDGE,"E13")])]})})})})})})})})})})})]});}
            var Q2;
            {var subQ0=makeQuery(id+"F1.opRevolve","SWEPT_FACE",FACE,{"disambiguationData":[OSD([sQuery(id+"F0.wireOp",EDGE,"E10")])]});var subQ1=sQuery(id+"F4.wireOp",EDGE,"E26.2.3");var subQ2=sQuery(id+"F4.wireOp",EDGE,"E26.2.2");var subQ3=sQuery(id+"F3.wireOp",EDGE,"E20.2.3");var subQ4=sQuery(id+"F3.wireOp",EDGE,"E20.2.2");var subQ5=sQuery(id+"F3.wireOp",EDGE,"E20.2.1");var subQ6=makeQuery(id+"F19.opLoft","SWEPT_FACE",FACE,{"disambiguationData":[OSD([subQ5,subQ4,subQ3,sQuery(id+"F4.wireOp",EDGE,"E26.2.1"),subQ2,subQ1])]});var subQ13=makeQuery(id+"F40.opExtrude","CAP_FACE",FACE,{"disambiguationData":[OSD([sQuery(id+"F39.wireOp",EDGE,"E29"),sQuery(id+"F39.wireOp",EDGE,"E30")])],"isStart":false});var subQ55=sQuery(id+"F3.wireOp",EDGE,"E20.7.0");var subQ62=makeQuery(id+"F14.opLoft","CAP_FACE",FACE,{"disambiguationData":[OSD([makeQuery(id+"F3.imprint","IMPRINT",FACE,{"disambiguationData":[TD([[makeQuery(id+"F3.imprint","IMPRINT",EDGE,{"derivedFrom":subQ55}),-1.0]])]})])],"isStart":true});var subQ75=sQuery(id+"F3.wireOp",EDGE,"E18.bottom");var subQ80=makeQuery(id+"F5.opLoft","CAP_FACE",FACE,{"disambiguationData":[OSD([makeQuery(id+"F3.imprint","IMPRINT",FACE,{"disambiguationData":[TD([[makeQuery(id+"F3.imprint","IMPRINT",EDGE,{"derivedFrom":subQ75}),1.0]])]})])],"isStart":true});Q2=makeQuery(id+"F44.opFillet","BLEND_EDGE",EDGE,{"blendedFrom":[makeQuery(id+"F40.boolean.opBoolean","INTERSECT",EDGE,{"derivedFrom":[subQ6,subQ13]}),makeQuery(id+"F40.boolean.opBoolean","SPLIT",FACE,{"disambiguationData":[TD([subQ0])],"derivedFrom":makeQuery(id+"F33.boolean.opBoolean","SPLIT",FACE,{"disambiguationData":[TD([subQ6])],"derivedFrom":makeQuery(id+"F32.boolean.opBoolean","SPLIT",FACE,{"disambiguationData":[TD([subQ62])],"derivedFrom":makeQuery(id+"F31.boolean.opBoolean","SPLIT",FACE,{"disambiguationData":[TD([subQ62])],"derivedFrom":makeQuery(id+"F30.boolean.opBoolean","SPLIT",FACE,{"disambiguationData":[TD([subQ80])],"derivedFrom":makeQuery(id+"F29.boolean.opBoolean","SPLIT",FACE,{"disambiguationData":[TD([subQ80])],"derivedFrom":makeQuery(id+"F28.boolean.opBoolean","SPLIT",FACE,{"disambiguationData":[TD([subQ80])],"derivedFrom":makeQuery(id+"F27.boolean.opBoolean","SPLIT",FACE,{"disambiguationData":[TD([subQ80])],"derivedFrom":makeQuery(id+"F26.boolean.opBoolean","SPLIT",FACE,{"disambiguationData":[TD([subQ80])],"derivedFrom":makeQuery(id+"F25.boolean.opBoolean","SPLIT",FACE,{"disambiguationData":[TD([subQ80])],"derivedFrom":makeQuery(id+"F24.boolean.opBoolean","SPLIT",FACE,{"disambiguationData":[TD([subQ80])],"derivedFrom":makeQuery(id+"F1.opRevolve","SWEPT_FACE",FACE,{"disambiguationData":[OSD([sQuery(id+"F0.wireOp",EDGE,"E13")])]})})})})})})})})})})})})],"blendedInto":[makeQuery(id+"F40.boolean.opBoolean","SPLIT",FACE,{"disambiguationData":[TD([subQ0])],"derivedFrom":makeQuery(id+"F33.boolean.opBoolean","SPLIT",FACE,{"disambiguationData":[TD([subQ6])],"derivedFrom":makeQuery(id+"F32.boolean.opBoolean","SPLIT",FACE,{"disambiguationData":[TD([subQ62])],"derivedFrom":makeQuery(id+"F31.boolean.opBoolean","SPLIT",FACE,{"disambiguationData":[TD([subQ62])],"derivedFrom":makeQuery(id+"F30.boolean.opBoolean","SPLIT",FACE,{"disambiguationData":[TD([subQ80])],"derivedFrom":makeQuery(id+"F29.boolean.opBoolean","SPLIT",FACE,{"disambiguationData":[TD([subQ80])],"derivedFrom":makeQuery(id+"F28.boolean.opBoolean","SPLIT",FACE,{"disambiguationData":[TD([subQ80])],"derivedFrom":makeQuery(id+"F27.boolean.opBoolean","SPLIT",FACE,{"disambiguationData":[TD([subQ80])],"derivedFrom":makeQuery(id+"F26.boolean.opBoolean","SPLIT",FACE,{"disambiguationData":[TD([subQ80])],"derivedFrom":makeQuery(id+"F25.boolean.opBoolean","SPLIT",FACE,{"disambiguationData":[TD([subQ80])],"derivedFrom":makeQuery(id+"F24.boolean.opBoolean","SPLIT",FACE,{"disambiguationData":[TD([subQ80])],"derivedFrom":makeQuery(id+"F1.opRevolve","SWEPT_FACE",FACE,{"disambiguationData":[OSD([sQuery(id+"F0.wireOp",EDGE,"E13")])]})})})})})})})})})})})})]});}
            var Q3;
            {var subQ0=makeQuery(id+"F1.opRevolve","SWEPT_FACE",FACE,{"disambiguationData":[OSD([sQuery(id+"F0.wireOp",EDGE,"E12")])]});var subQ5=sQuery(id+"F3.wireOp",EDGE,"E20.2.3");var subQ6=sQuery(id+"F3.wireOp",EDGE,"E20.2.2");var subQ7=sQuery(id+"F3.wireOp",EDGE,"E20.2.1");var subQ8=makeQuery(id+"F33.opLoft","SWEPT_FACE",FACE,{"disambiguationData":[OSD([subQ7,subQ6,subQ5,sQuery(id+"F22.wireOp",EDGE,"E28.10.0"),sQuery(id+"F22.wireOp",EDGE,"E28.10.2"),sQuery(id+"F22.wireOp",EDGE,"E28.10.3")])]});var subQ9=makeQuery(id+"F40.opExtrude","CAP_FACE",FACE,{"disambiguationData":[OSD([sQuery(id+"F39.wireOp",EDGE,"E29"),sQuery(id+"F39.wireOp",EDGE,"E30")])],"isStart":true});var subQ13=sQuery(id+"F4.wireOp",EDGE,"E26.2.3");var subQ14=sQuery(id+"F4.wireOp",EDGE,"E26.2.2");var subQ15=makeQuery(id+"F19.opLoft","SWEPT_FACE",FACE,{"disambiguationData":[OSD([subQ7,subQ6,subQ5,sQuery(id+"F4.wireOp",EDGE,"E26.2.1"),subQ14,subQ13])]});var subQ56=sQuery(id+"F3.wireOp",EDGE,"E20.7.0");var subQ63=makeQuery(id+"F14.opLoft","CAP_FACE",FACE,{"disambiguationData":[OSD([makeQuery(id+"F3.imprint","IMPRINT",FACE,{"disambiguationData":[TD([[makeQuery(id+"F3.imprint","IMPRINT",EDGE,{"derivedFrom":subQ56}),-1.0]])]})])],"isStart":true});var subQ76=sQuery(id+"F3.wireOp",EDGE,"E18.bottom");var subQ81=makeQuery(id+"F5.opLoft","CAP_FACE",FACE,{"disambiguationData":[OSD([makeQuery(id+"F3.imprint","IMPRINT",FACE,{"disambiguationData":[TD([[makeQuery(id+"F3.imprint","IMPRINT",EDGE,{"derivedFrom":subQ76}),1.0]])]})])],"isStart":true});Q3=makeQuery(id+"F44.opFillet","BLEND_EDGE",EDGE,{"blendedFrom":[makeQuery(id+"F40.boolean.opBoolean","INTERSECT",EDGE,{"derivedFrom":[subQ8,subQ9]}),makeQuery(id+"F40.boolean.opBoolean","SPLIT",FACE,{"disambiguationData":[TD([subQ0])],"derivedFrom":makeQuery(id+"F33.boolean.opBoolean","SPLIT",FACE,{"disambiguationData":[TD([subQ15])],"derivedFrom":makeQuery(id+"F32.boolean.opBoolean","SPLIT",FACE,{"disambiguationData":[TD([subQ63])],"derivedFrom":makeQuery(id+"F31.boolean.opBoolean","SPLIT",FACE,{"disambiguationData":[TD([subQ63])],"derivedFrom":makeQuery(id+"F30.boolean.opBoolean","SPLIT",FACE,{"disambiguationData":[TD([subQ81])],"derivedFrom":makeQuery(id+"F29.boolean.opBoolean","SPLIT",FACE,{"disambiguationData":[TD([subQ81])],"derivedFrom":makeQuery(id+"F28.boolean.opBoolean","SPLIT",FACE,{"disambiguationData":[TD([subQ81])],"derivedFrom":makeQuery(id+"F27.boolean.opBoolean","SPLIT",FACE,{"disambiguationData":[TD([subQ81])],"derivedFrom":makeQuery(id+"F26.boolean.opBoolean","SPLIT",FACE,{"disambiguationData":[TD([subQ81])],"derivedFrom":makeQuery(id+"F25.boolean.opBoolean","SPLIT",FACE,{"disambiguationData":[TD([subQ81])],"derivedFrom":makeQuery(id+"F24.boolean.opBoolean","SPLIT",FACE,{"disambiguationData":[TD([subQ81])],"derivedFrom":makeQuery(id+"F1.opRevolve","SWEPT_FACE",FACE,{"disambiguationData":[OSD([sQuery(id+"F0.wireOp",EDGE,"E13")])]})})})})})})})})})})})})],"blendedInto":[makeQuery(id+"F40.boolean.opBoolean","SPLIT",FACE,{"disambiguationData":[TD([subQ0])],"derivedFrom":makeQuery(id+"F33.boolean.opBoolean","SPLIT",FACE,{"disambiguationData":[TD([subQ15])],"derivedFrom":makeQuery(id+"F32.boolean.opBoolean","SPLIT",FACE,{"disambiguationData":[TD([subQ63])],"derivedFrom":makeQuery(id+"F31.boolean.opBoolean","SPLIT",FACE,{"disambiguationData":[TD([subQ63])],"derivedFrom":makeQuery(id+"F30.boolean.opBoolean","SPLIT",FACE,{"disambiguationData":[TD([subQ81])],"derivedFrom":makeQuery(id+"F29.boolean.opBoolean","SPLIT",FACE,{"disambiguationData":[TD([subQ81])],"derivedFrom":makeQuery(id+"F28.boolean.opBoolean","SPLIT",FACE,{"disambiguationData":[TD([subQ81])],"derivedFrom":makeQuery(id+"F27.boolean.opBoolean","SPLIT",FACE,{"disambiguationData":[TD([subQ81])],"derivedFrom":makeQuery(id+"F26.boolean.opBoolean","SPLIT",FACE,{"disambiguationData":[TD([subQ81])],"derivedFrom":makeQuery(id+"F25.boolean.opBoolean","SPLIT",FACE,{"disambiguationData":[TD([subQ81])],"derivedFrom":makeQuery(id+"F24.boolean.opBoolean","SPLIT",FACE,{"disambiguationData":[TD([subQ81])],"derivedFrom":makeQuery(id+"F1.opRevolve","SWEPT_FACE",FACE,{"disambiguationData":[OSD([sQuery(id+"F0.wireOp",EDGE,"E13")])]})})})})})})})})})})})})]});}
            var Q4;
            {var subQ0=makeQuery(id+"F1.opRevolve","SWEPT_FACE",FACE,{"disambiguationData":[OSD([sQuery(id+"F0.wireOp",EDGE,"E12")])]});var subQ1=sQuery(id+"F3.wireOp",EDGE,"E20.1.3");var subQ2=sQuery(id+"F3.wireOp",EDGE,"E20.1.2");var subQ3=sQuery(id+"F3.wireOp",EDGE,"E20.1.1");var subQ4=makeQuery(id+"F32.opLoft","SWEPT_FACE",FACE,{"disambiguationData":[OSD([subQ3,subQ2,subQ1,sQuery(id+"F22.wireOp",EDGE,"E28.9.0"),sQuery(id+"F22.wireOp",EDGE,"E28.9.2"),sQuery(id+"F22.wireOp",EDGE,"E28.9.3")])]});var subQ5=sQuery(id+"F3.wireOp",EDGE,"E18.left");var subQ6=sQuery(id+"F3.wireOp",EDGE,"E18.top");var subQ7=sQuery(id+"F3.wireOp",EDGE,"E18.bottom");var subQ9=makeQuery(id+"F40.opExtrude","CAP_FACE",FACE,{"disambiguationData":[OSD([sQuery(id+"F39.wireOp",EDGE,"E29"),sQuery(id+"F39.wireOp",EDGE,"E30")])],"isStart":true});var subQ13=sQuery(id+"F4.wireOp",EDGE,"E23");var subQ14=sQuery(id+"F4.wireOp",EDGE,"E22");var subQ15=makeQuery(id+"F5.opLoft","SWEPT_FACE",FACE,{"disambiguationData":[OSD([subQ7,subQ6,subQ5,sQuery(id+"F4.wireOp",EDGE,"E21"),subQ14,subQ13])]});var subQ65=sQuery(id+"F3.wireOp",EDGE,"E20.7.0");var subQ73=makeQuery(id+"F14.opLoft","CAP_FACE",FACE,{"disambiguationData":[OSD([makeQuery(id+"F3.imprint","IMPRINT",FACE,{"disambiguationData":[TD([[makeQuery(id+"F3.imprint","IMPRINT",EDGE,{"derivedFrom":subQ65}),-1.0]])]})])],"isStart":true});var subQ81=makeQuery(id+"F5.opLoft","CAP_FACE",FACE,{"disambiguationData":[OSD([makeQuery(id+"F3.imprint","IMPRINT",FACE,{"disambiguationData":[TD([[makeQuery(id+"F3.imprint","IMPRINT",EDGE,{"derivedFrom":subQ7}),1.0]])]})])],"isStart":true});Q4=makeQuery(id+"F44.opFillet","BLEND_EDGE",EDGE,{"blendedFrom":[makeQuery(id+"F40.boolean.opBoolean","INTERSECT",EDGE,{"derivedFrom":[subQ4,subQ9]}),makeQuery(id+"F40.boolean.opBoolean","SPLIT",FACE,{"disambiguationData":[TD([subQ0])],"derivedFrom":makeQuery(id+"F32.boolean.opBoolean","SPLIT",FACE,{"disambiguationData":[TD([subQ15])],"derivedFrom":makeQuery(id+"F31.boolean.opBoolean","SPLIT",FACE,{"disambiguationData":[TD([subQ73])],"derivedFrom":makeQuery(id+"F30.boolean.opBoolean","SPLIT",FACE,{"disambiguationData":[TD([subQ81])],"derivedFrom":makeQuery(id+"F29.boolean.opBoolean","SPLIT",FACE,{"disambiguationData":[TD([subQ81])],"derivedFrom":makeQuery(id+"F28.boolean.opBoolean","SPLIT",FACE,{"disambiguationData":[TD([subQ81])],"derivedFrom":makeQuery(id+"F27.boolean.opBoolean","SPLIT",FACE,{"disambiguationData":[TD([subQ81])],"derivedFrom":makeQuery(id+"F26.boolean.opBoolean","SPLIT",FACE,{"disambiguationData":[TD([subQ81])],"derivedFrom":makeQuery(id+"F25.boolean.opBoolean","SPLIT",FACE,{"disambiguationData":[TD([subQ81])],"derivedFrom":makeQuery(id+"F24.boolean.opBoolean","SPLIT",FACE,{"disambiguationData":[TD([subQ81])],"derivedFrom":makeQuery(id+"F1.opRevolve","SWEPT_FACE",FACE,{"disambiguationData":[OSD([sQuery(id+"F0.wireOp",EDGE,"E13")])]})})})})})})})})})})})],"blendedInto":[makeQuery(id+"F40.boolean.opBoolean","SPLIT",FACE,{"disambiguationData":[TD([subQ0])],"derivedFrom":makeQuery(id+"F32.boolean.opBoolean","SPLIT",FACE,{"disambiguationData":[TD([subQ15])],"derivedFrom":makeQuery(id+"F31.boolean.opBoolean","SPLIT",FACE,{"disambiguationData":[TD([subQ73])],"derivedFrom":makeQuery(id+"F30.boolean.opBoolean","SPLIT",FACE,{"disambiguationData":[TD([subQ81])],"derivedFrom":makeQuery(id+"F29.boolean.opBoolean","SPLIT",FACE,{"disambiguationData":[TD([subQ81])],"derivedFrom":makeQuery(id+"F28.boolean.opBoolean","SPLIT",FACE,{"disambiguationData":[TD([subQ81])],"derivedFrom":makeQuery(id+"F27.boolean.opBoolean","SPLIT",FACE,{"disambiguationData":[TD([subQ81])],"derivedFrom":makeQuery(id+"F26.boolean.opBoolean","SPLIT",FACE,{"disambiguationData":[TD([subQ81])],"derivedFrom":makeQuery(id+"F25.boolean.opBoolean","SPLIT",FACE,{"disambiguationData":[TD([subQ81])],"derivedFrom":makeQuery(id+"F24.boolean.opBoolean","SPLIT",FACE,{"disambiguationData":[TD([subQ81])],"derivedFrom":makeQuery(id+"F1.opRevolve","SWEPT_FACE",FACE,{"disambiguationData":[OSD([sQuery(id+"F0.wireOp",EDGE,"E13")])]})})})})})})})})})})})]});}
            var Q5;
            {var subQ0=makeQuery(id+"F1.opRevolve","SWEPT_FACE",FACE,{"disambiguationData":[OSD([sQuery(id+"F0.wireOp",EDGE,"E12")])]});var subQ1=sQuery(id+"F3.wireOp",EDGE,"E18.right");var subQ2=sQuery(id+"F3.wireOp",EDGE,"E18.top");var subQ3=sQuery(id+"F3.wireOp",EDGE,"E18.bottom");var subQ4=makeQuery(id+"F31.opLoft","SWEPT_FACE",FACE,{"disambiguationData":[OSD([subQ3,subQ2,subQ1,sQuery(id+"F22.wireOp",EDGE,"E28.8.0"),sQuery(id+"F22.wireOp",EDGE,"E28.8.2"),sQuery(id+"F22.wireOp",EDGE,"E28.8.3")])]});var subQ9=makeQuery(id+"F40.opExtrude","CAP_FACE",FACE,{"disambiguationData":[OSD([sQuery(id+"F39.wireOp",EDGE,"E29"),sQuery(id+"F39.wireOp",EDGE,"E30")])],"isStart":true});var subQ13=sQuery(id+"F4.wireOp",EDGE,"E23");var subQ14=sQuery(id+"F4.wireOp",EDGE,"E22");var subQ15=makeQuery(id+"F5.opLoft","SWEPT_FACE",FACE,{"disambiguationData":[OSD([subQ3,subQ2,subQ1,subQ14,subQ13,sQuery(id+"F4.wireOp",EDGE,"E24")])]});var subQ59=makeQuery(id+"F5.opLoft","CAP_FACE",FACE,{"disambiguationData":[OSD([makeQuery(id+"F3.imprint","IMPRINT",FACE,{"disambiguationData":[TD([[makeQuery(id+"F3.imprint","IMPRINT",EDGE,{"derivedFrom":subQ3}),1.0]])]})])],"isStart":true});Q5=makeQuery(id+"F44.opFillet","BLEND_EDGE",EDGE,{"blendedFrom":[makeQuery(id+"F40.boolean.opBoolean","INTERSECT",EDGE,{"derivedFrom":[subQ4,subQ9]}),makeQuery(id+"F40.boolean.opBoolean","SPLIT",FACE,{"disambiguationData":[TD([subQ0])],"derivedFrom":makeQuery(id+"F31.boolean.opBoolean","SPLIT",FACE,{"disambiguationData":[TD([subQ15])],"derivedFrom":makeQuery(id+"F30.boolean.opBoolean","SPLIT",FACE,{"disambiguationData":[TD([subQ59])],"derivedFrom":makeQuery(id+"F29.boolean.opBoolean","SPLIT",FACE,{"disambiguationData":[TD([subQ59])],"derivedFrom":makeQuery(id+"F28.boolean.opBoolean","SPLIT",FACE,{"disambiguationData":[TD([subQ59])],"derivedFrom":makeQuery(id+"F27.boolean.opBoolean","SPLIT",FACE,{"disambiguationData":[TD([subQ59])],"derivedFrom":makeQuery(id+"F26.boolean.opBoolean","SPLIT",FACE,{"disambiguationData":[TD([subQ59])],"derivedFrom":makeQuery(id+"F25.boolean.opBoolean","SPLIT",FACE,{"disambiguationData":[TD([subQ59])],"derivedFrom":makeQuery(id+"F24.boolean.opBoolean","SPLIT",FACE,{"disambiguationData":[TD([subQ59])],"derivedFrom":makeQuery(id+"F1.opRevolve","SWEPT_FACE",FACE,{"disambiguationData":[OSD([sQuery(id+"F0.wireOp",EDGE,"E13")])]})})})})})})})})})})],"blendedInto":[makeQuery(id+"F40.boolean.opBoolean","SPLIT",FACE,{"disambiguationData":[TD([subQ0])],"derivedFrom":makeQuery(id+"F31.boolean.opBoolean","SPLIT",FACE,{"disambiguationData":[TD([subQ15])],"derivedFrom":makeQuery(id+"F30.boolean.opBoolean","SPLIT",FACE,{"disambiguationData":[TD([subQ59])],"derivedFrom":makeQuery(id+"F29.boolean.opBoolean","SPLIT",FACE,{"disambiguationData":[TD([subQ59])],"derivedFrom":makeQuery(id+"F28.boolean.opBoolean","SPLIT",FACE,{"disambiguationData":[TD([subQ59])],"derivedFrom":makeQuery(id+"F27.boolean.opBoolean","SPLIT",FACE,{"disambiguationData":[TD([subQ59])],"derivedFrom":makeQuery(id+"F26.boolean.opBoolean","SPLIT",FACE,{"disambiguationData":[TD([subQ59])],"derivedFrom":makeQuery(id+"F25.boolean.opBoolean","SPLIT",FACE,{"disambiguationData":[TD([subQ59])],"derivedFrom":makeQuery(id+"F24.boolean.opBoolean","SPLIT",FACE,{"disambiguationData":[TD([subQ59])],"derivedFrom":makeQuery(id+"F1.opRevolve","SWEPT_FACE",FACE,{"disambiguationData":[OSD([sQuery(id+"F0.wireOp",EDGE,"E13")])]})})})})})})})})})})]});}
            var Q6;
            {var subQ0=makeQuery(id+"F1.opRevolve","SWEPT_FACE",FACE,{"disambiguationData":[OSD([sQuery(id+"F0.wireOp",EDGE,"E12")])]});var subQ5=sQuery(id+"F3.wireOp",EDGE,"E20.15.3");var subQ6=sQuery(id+"F3.wireOp",EDGE,"E20.15.2");var subQ7=sQuery(id+"F3.wireOp",EDGE,"E20.15.1");var subQ8=makeQuery(id+"F30.opLoft","SWEPT_FACE",FACE,{"disambiguationData":[OSD([subQ7,subQ6,subQ5,sQuery(id+"F22.wireOp",EDGE,"E28.7.0"),sQuery(id+"F22.wireOp",EDGE,"E28.7.2"),sQuery(id+"F22.wireOp",EDGE,"E28.7.3")])]});var subQ9=makeQuery(id+"F40.opExtrude","CAP_FACE",FACE,{"disambiguationData":[OSD([sQuery(id+"F39.wireOp",EDGE,"E29"),sQuery(id+"F39.wireOp",EDGE,"E30")])],"isStart":true});var subQ10=sQuery(id+"F4.wireOp",EDGE,"E26.15.3");var subQ11=sQuery(id+"F4.wireOp",EDGE,"E26.15.2");var subQ12=makeQuery(id+"F6.opLoft","SWEPT_FACE",FACE,{"disambiguationData":[OSD([subQ7,subQ6,subQ5,sQuery(id+"F4.wireOp",EDGE,"E26.15.1"),subQ11,subQ10])]});var subQ48=sQuery(id+"F3.wireOp",EDGE,"E18.bottom");var subQ51=makeQuery(id+"F5.opLoft","CAP_FACE",FACE,{"disambiguationData":[OSD([makeQuery(id+"F3.imprint","IMPRINT",FACE,{"disambiguationData":[TD([[makeQuery(id+"F3.imprint","IMPRINT",EDGE,{"derivedFrom":subQ48}),1.0]])]})])],"isStart":true});Q6=makeQuery(id+"F44.opFillet","BLEND_EDGE",EDGE,{"blendedFrom":[makeQuery(id+"F40.boolean.opBoolean","INTERSECT",EDGE,{"derivedFrom":[subQ8,subQ9]}),makeQuery(id+"F40.boolean.opBoolean","SPLIT",FACE,{"disambiguationData":[TD([subQ0])],"derivedFrom":makeQuery(id+"F30.boolean.opBoolean","SPLIT",FACE,{"disambiguationData":[TD([subQ12])],"derivedFrom":makeQuery(id+"F29.boolean.opBoolean","SPLIT",FACE,{"disambiguationData":[TD([subQ51])],"derivedFrom":makeQuery(id+"F28.boolean.opBoolean","SPLIT",FACE,{"disambiguationData":[TD([subQ51])],"derivedFrom":makeQuery(id+"F27.boolean.opBoolean","SPLIT",FACE,{"disambiguationData":[TD([subQ51])],"derivedFrom":makeQuery(id+"F26.boolean.opBoolean","SPLIT",FACE,{"disambiguationData":[TD([subQ51])],"derivedFrom":makeQuery(id+"F25.boolean.opBoolean","SPLIT",FACE,{"disambiguationData":[TD([subQ51])],"derivedFrom":makeQuery(id+"F24.boolean.opBoolean","SPLIT",FACE,{"disambiguationData":[TD([subQ51])],"derivedFrom":makeQuery(id+"F1.opRevolve","SWEPT_FACE",FACE,{"disambiguationData":[OSD([sQuery(id+"F0.wireOp",EDGE,"E13")])]})})})})})})})})})],"blendedInto":[makeQuery(id+"F40.boolean.opBoolean","SPLIT",FACE,{"disambiguationData":[TD([subQ0])],"derivedFrom":makeQuery(id+"F30.boolean.opBoolean","SPLIT",FACE,{"disambiguationData":[TD([subQ12])],"derivedFrom":makeQuery(id+"F29.boolean.opBoolean","SPLIT",FACE,{"disambiguationData":[TD([subQ51])],"derivedFrom":makeQuery(id+"F28.boolean.opBoolean","SPLIT",FACE,{"disambiguationData":[TD([subQ51])],"derivedFrom":makeQuery(id+"F27.boolean.opBoolean","SPLIT",FACE,{"disambiguationData":[TD([subQ51])],"derivedFrom":makeQuery(id+"F26.boolean.opBoolean","SPLIT",FACE,{"disambiguationData":[TD([subQ51])],"derivedFrom":makeQuery(id+"F25.boolean.opBoolean","SPLIT",FACE,{"disambiguationData":[TD([subQ51])],"derivedFrom":makeQuery(id+"F24.boolean.opBoolean","SPLIT",FACE,{"disambiguationData":[TD([subQ51])],"derivedFrom":makeQuery(id+"F1.opRevolve","SWEPT_FACE",FACE,{"disambiguationData":[OSD([sQuery(id+"F0.wireOp",EDGE,"E13")])]})})})})})})})})})]});}
            var Q7;
            {var subQ0=makeQuery(id+"F1.opRevolve","SWEPT_FACE",FACE,{"disambiguationData":[OSD([sQuery(id+"F0.wireOp",EDGE,"E12")])]});var subQ5=sQuery(id+"F3.wireOp",EDGE,"E20.14.3");var subQ6=sQuery(id+"F3.wireOp",EDGE,"E20.14.2");var subQ7=sQuery(id+"F3.wireOp",EDGE,"E20.14.1");var subQ8=makeQuery(id+"F29.opLoft","SWEPT_FACE",FACE,{"disambiguationData":[OSD([subQ7,subQ6,subQ5,sQuery(id+"F22.wireOp",EDGE,"E28.6.0"),sQuery(id+"F22.wireOp",EDGE,"E28.6.2"),sQuery(id+"F22.wireOp",EDGE,"E28.6.3")])]});var subQ9=makeQuery(id+"F40.opExtrude","CAP_FACE",FACE,{"disambiguationData":[OSD([sQuery(id+"F39.wireOp",EDGE,"E29"),sQuery(id+"F39.wireOp",EDGE,"E30")])],"isStart":true});var subQ13=sQuery(id+"F4.wireOp",EDGE,"E26.14.3");var subQ14=sQuery(id+"F4.wireOp",EDGE,"E26.14.2");var subQ15=makeQuery(id+"F7.opLoft","SWEPT_FACE",FACE,{"disambiguationData":[OSD([subQ7,subQ6,subQ5,sQuery(id+"F4.wireOp",EDGE,"E26.14.1"),subQ14,subQ13])]});var subQ49=sQuery(id+"F3.wireOp",EDGE,"E18.bottom");var subQ52=makeQuery(id+"F5.opLoft","CAP_FACE",FACE,{"disambiguationData":[OSD([makeQuery(id+"F3.imprint","IMPRINT",FACE,{"disambiguationData":[TD([[makeQuery(id+"F3.imprint","IMPRINT",EDGE,{"derivedFrom":subQ49}),1.0]])]})])],"isStart":true});Q7=makeQuery(id+"F44.opFillet","BLEND_EDGE",EDGE,{"blendedFrom":[makeQuery(id+"F40.boolean.opBoolean","INTERSECT",EDGE,{"derivedFrom":[subQ8,subQ9]}),makeQuery(id+"F40.boolean.opBoolean","SPLIT",FACE,{"disambiguationData":[TD([subQ0])],"derivedFrom":makeQuery(id+"F29.boolean.opBoolean","SPLIT",FACE,{"disambiguationData":[TD([subQ15])],"derivedFrom":makeQuery(id+"F28.boolean.opBoolean","SPLIT",FACE,{"disambiguationData":[TD([subQ52])],"derivedFrom":makeQuery(id+"F27.boolean.opBoolean","SPLIT",FACE,{"disambiguationData":[TD([subQ52])],"derivedFrom":makeQuery(id+"F26.boolean.opBoolean","SPLIT",FACE,{"disambiguationData":[TD([subQ52])],"derivedFrom":makeQuery(id+"F25.boolean.opBoolean","SPLIT",FACE,{"disambiguationData":[TD([subQ52])],"derivedFrom":makeQuery(id+"F24.boolean.opBoolean","SPLIT",FACE,{"disambiguationData":[TD([subQ52])],"derivedFrom":makeQuery(id+"F1.opRevolve","SWEPT_FACE",FACE,{"disambiguationData":[OSD([sQuery(id+"F0.wireOp",EDGE,"E13")])]})})})})})})})})],"blendedInto":[makeQuery(id+"F40.boolean.opBoolean","SPLIT",FACE,{"disambiguationData":[TD([subQ0])],"derivedFrom":makeQuery(id+"F29.boolean.opBoolean","SPLIT",FACE,{"disambiguationData":[TD([subQ15])],"derivedFrom":makeQuery(id+"F28.boolean.opBoolean","SPLIT",FACE,{"disambiguationData":[TD([subQ52])],"derivedFrom":makeQuery(id+"F27.boolean.opBoolean","SPLIT",FACE,{"disambiguationData":[TD([subQ52])],"derivedFrom":makeQuery(id+"F26.boolean.opBoolean","SPLIT",FACE,{"disambiguationData":[TD([subQ52])],"derivedFrom":makeQuery(id+"F25.boolean.opBoolean","SPLIT",FACE,{"disambiguationData":[TD([subQ52])],"derivedFrom":makeQuery(id+"F24.boolean.opBoolean","SPLIT",FACE,{"disambiguationData":[TD([subQ52])],"derivedFrom":makeQuery(id+"F1.opRevolve","SWEPT_FACE",FACE,{"disambiguationData":[OSD([sQuery(id+"F0.wireOp",EDGE,"E13")])]})})})})})})})})]});}
            var Q8;
            {var subQ0=makeQuery(id+"F1.opRevolve","SWEPT_FACE",FACE,{"disambiguationData":[OSD([sQuery(id+"F0.wireOp",EDGE,"E12")])]});var subQ5=sQuery(id+"F3.wireOp",EDGE,"E20.13.3");var subQ6=sQuery(id+"F3.wireOp",EDGE,"E20.13.2");var subQ7=sQuery(id+"F3.wireOp",EDGE,"E20.13.1");var subQ8=makeQuery(id+"F28.opLoft","SWEPT_FACE",FACE,{"disambiguationData":[OSD([subQ7,subQ6,subQ5,sQuery(id+"F22.wireOp",EDGE,"E28.5.0"),sQuery(id+"F22.wireOp",EDGE,"E28.5.2"),sQuery(id+"F22.wireOp",EDGE,"E28.5.3")])]});var subQ9=makeQuery(id+"F40.opExtrude","CAP_FACE",FACE,{"disambiguationData":[OSD([sQuery(id+"F39.wireOp",EDGE,"E29"),sQuery(id+"F39.wireOp",EDGE,"E30")])],"isStart":true});var subQ13=sQuery(id+"F4.wireOp",EDGE,"E26.13.3");var subQ14=sQuery(id+"F4.wireOp",EDGE,"E26.13.2");var subQ15=makeQuery(id+"F8.opLoft","SWEPT_FACE",FACE,{"disambiguationData":[OSD([subQ7,subQ6,subQ5,sQuery(id+"F4.wireOp",EDGE,"E26.13.1"),subQ14,subQ13])]});var subQ57=sQuery(id+"F3.wireOp",EDGE,"E18.bottom");var subQ60=makeQuery(id+"F5.opLoft","CAP_FACE",FACE,{"disambiguationData":[OSD([makeQuery(id+"F3.imprint","IMPRINT",FACE,{"disambiguationData":[TD([[makeQuery(id+"F3.imprint","IMPRINT",EDGE,{"derivedFrom":subQ57}),1.0]])]})])],"isStart":true});Q8=makeQuery(id+"F44.opFillet","BLEND_EDGE",EDGE,{"blendedFrom":[makeQuery(id+"F40.boolean.opBoolean","INTERSECT",EDGE,{"derivedFrom":[subQ8,subQ9]}),makeQuery(id+"F40.boolean.opBoolean","SPLIT",FACE,{"disambiguationData":[TD([subQ0])],"derivedFrom":makeQuery(id+"F28.boolean.opBoolean","SPLIT",FACE,{"disambiguationData":[TD([subQ15])],"derivedFrom":makeQuery(id+"F27.boolean.opBoolean","SPLIT",FACE,{"disambiguationData":[TD([subQ60])],"derivedFrom":makeQuery(id+"F26.boolean.opBoolean","SPLIT",FACE,{"disambiguationData":[TD([subQ60])],"derivedFrom":makeQuery(id+"F25.boolean.opBoolean","SPLIT",FACE,{"disambiguationData":[TD([subQ60])],"derivedFrom":makeQuery(id+"F24.boolean.opBoolean","SPLIT",FACE,{"disambiguationData":[TD([subQ60])],"derivedFrom":makeQuery(id+"F1.opRevolve","SWEPT_FACE",FACE,{"disambiguationData":[OSD([sQuery(id+"F0.wireOp",EDGE,"E13")])]})})})})})})})],"blendedInto":[makeQuery(id+"F40.boolean.opBoolean","SPLIT",FACE,{"disambiguationData":[TD([subQ0])],"derivedFrom":makeQuery(id+"F28.boolean.opBoolean","SPLIT",FACE,{"disambiguationData":[TD([subQ15])],"derivedFrom":makeQuery(id+"F27.boolean.opBoolean","SPLIT",FACE,{"disambiguationData":[TD([subQ60])],"derivedFrom":makeQuery(id+"F26.boolean.opBoolean","SPLIT",FACE,{"disambiguationData":[TD([subQ60])],"derivedFrom":makeQuery(id+"F25.boolean.opBoolean","SPLIT",FACE,{"disambiguationData":[TD([subQ60])],"derivedFrom":makeQuery(id+"F24.boolean.opBoolean","SPLIT",FACE,{"disambiguationData":[TD([subQ60])],"derivedFrom":makeQuery(id+"F1.opRevolve","SWEPT_FACE",FACE,{"disambiguationData":[OSD([sQuery(id+"F0.wireOp",EDGE,"E13")])]})})})})})})})]});}
            var Q9;
            {var subQ0=makeQuery(id+"F1.opRevolve","SWEPT_FACE",FACE,{"disambiguationData":[OSD([sQuery(id+"F0.wireOp",EDGE,"E12")])]});var subQ5=sQuery(id+"F3.wireOp",EDGE,"E20.12.3");var subQ6=sQuery(id+"F3.wireOp",EDGE,"E20.12.2");var subQ7=sQuery(id+"F3.wireOp",EDGE,"E20.12.1");var subQ8=makeQuery(id+"F27.opLoft","SWEPT_FACE",FACE,{"disambiguationData":[OSD([subQ7,subQ6,subQ5,sQuery(id+"F22.wireOp",EDGE,"E28.4.0"),sQuery(id+"F22.wireOp",EDGE,"E28.4.2"),sQuery(id+"F22.wireOp",EDGE,"E28.4.3")])]});var subQ9=makeQuery(id+"F40.opExtrude","CAP_FACE",FACE,{"disambiguationData":[OSD([sQuery(id+"F39.wireOp",EDGE,"E29"),sQuery(id+"F39.wireOp",EDGE,"E30")])],"isStart":true});var subQ13=sQuery(id+"F4.wireOp",EDGE,"E26.12.3");var subQ14=sQuery(id+"F4.wireOp",EDGE,"E26.12.2");var subQ15=makeQuery(id+"F9.opLoft","SWEPT_FACE",FACE,{"disambiguationData":[OSD([subQ7,subQ6,subQ5,sQuery(id+"F4.wireOp",EDGE,"E26.12.1"),subQ14,subQ13])]});var subQ75=sQuery(id+"F3.wireOp",EDGE,"E18.bottom");var subQ78=makeQuery(id+"F5.opLoft","CAP_FACE",FACE,{"disambiguationData":[OSD([makeQuery(id+"F3.imprint","IMPRINT",FACE,{"disambiguationData":[TD([[makeQuery(id+"F3.imprint","IMPRINT",EDGE,{"derivedFrom":subQ75}),1.0]])]})])],"isStart":true});Q9=makeQuery(id+"F44.opFillet","BLEND_EDGE",EDGE,{"blendedFrom":[makeQuery(id+"F40.boolean.opBoolean","INTERSECT",EDGE,{"derivedFrom":[subQ8,subQ9]}),makeQuery(id+"F40.boolean.opBoolean","SPLIT",FACE,{"disambiguationData":[TD([subQ0])],"derivedFrom":makeQuery(id+"F27.boolean.opBoolean","SPLIT",FACE,{"disambiguationData":[TD([subQ15])],"derivedFrom":makeQuery(id+"F26.boolean.opBoolean","SPLIT",FACE,{"disambiguationData":[TD([subQ78])],"derivedFrom":makeQuery(id+"F25.boolean.opBoolean","SPLIT",FACE,{"disambiguationData":[TD([subQ78])],"derivedFrom":makeQuery(id+"F24.boolean.opBoolean","SPLIT",FACE,{"disambiguationData":[TD([subQ78])],"derivedFrom":makeQuery(id+"F1.opRevolve","SWEPT_FACE",FACE,{"disambiguationData":[OSD([sQuery(id+"F0.wireOp",EDGE,"E13")])]})})})})})})],"blendedInto":[makeQuery(id+"F40.boolean.opBoolean","SPLIT",FACE,{"disambiguationData":[TD([subQ0])],"derivedFrom":makeQuery(id+"F27.boolean.opBoolean","SPLIT",FACE,{"disambiguationData":[TD([subQ15])],"derivedFrom":makeQuery(id+"F26.boolean.opBoolean","SPLIT",FACE,{"disambiguationData":[TD([subQ78])],"derivedFrom":makeQuery(id+"F25.boolean.opBoolean","SPLIT",FACE,{"disambiguationData":[TD([subQ78])],"derivedFrom":makeQuery(id+"F24.boolean.opBoolean","SPLIT",FACE,{"disambiguationData":[TD([subQ78])],"derivedFrom":makeQuery(id+"F1.opRevolve","SWEPT_FACE",FACE,{"disambiguationData":[OSD([sQuery(id+"F0.wireOp",EDGE,"E13")])]})})})})})})]});}
            var Q10;
            {var subQ0=makeQuery(id+"F1.opRevolve","SWEPT_FACE",FACE,{"disambiguationData":[OSD([sQuery(id+"F0.wireOp",EDGE,"E12")])]});var subQ5=sQuery(id+"F3.wireOp",EDGE,"E20.11.3");var subQ6=sQuery(id+"F3.wireOp",EDGE,"E20.11.2");var subQ7=sQuery(id+"F3.wireOp",EDGE,"E20.11.1");var subQ8=makeQuery(id+"F26.opLoft","SWEPT_FACE",FACE,{"disambiguationData":[OSD([subQ7,subQ6,subQ5,sQuery(id+"F22.wireOp",EDGE,"E28.3.0"),sQuery(id+"F22.wireOp",EDGE,"E28.3.2"),sQuery(id+"F22.wireOp",EDGE,"E28.3.3")])]});var subQ9=makeQuery(id+"F40.opExtrude","CAP_FACE",FACE,{"disambiguationData":[OSD([sQuery(id+"F39.wireOp",EDGE,"E29"),sQuery(id+"F39.wireOp",EDGE,"E30")])],"isStart":true});var subQ13=sQuery(id+"F4.wireOp",EDGE,"E26.11.3");var subQ14=sQuery(id+"F4.wireOp",EDGE,"E26.11.2");var subQ15=makeQuery(id+"F10.opLoft","SWEPT_FACE",FACE,{"disambiguationData":[OSD([subQ7,subQ6,subQ5,sQuery(id+"F4.wireOp",EDGE,"E26.11.1"),subQ14,subQ13])]});var subQ80=sQuery(id+"F3.wireOp",EDGE,"E18.bottom");var subQ83=makeQuery(id+"F5.opLoft","CAP_FACE",FACE,{"disambiguationData":[OSD([makeQuery(id+"F3.imprint","IMPRINT",FACE,{"disambiguationData":[TD([[makeQuery(id+"F3.imprint","IMPRINT",EDGE,{"derivedFrom":subQ80}),1.0]])]})])],"isStart":true});Q10=makeQuery(id+"F44.opFillet","BLEND_EDGE",EDGE,{"blendedFrom":[makeQuery(id+"F40.boolean.opBoolean","INTERSECT",EDGE,{"derivedFrom":[subQ8,subQ9]}),makeQuery(id+"F40.boolean.opBoolean","SPLIT",FACE,{"disambiguationData":[TD([subQ0])],"derivedFrom":makeQuery(id+"F26.boolean.opBoolean","SPLIT",FACE,{"disambiguationData":[TD([subQ15])],"derivedFrom":makeQuery(id+"F25.boolean.opBoolean","SPLIT",FACE,{"disambiguationData":[TD([subQ83])],"derivedFrom":makeQuery(id+"F24.boolean.opBoolean","SPLIT",FACE,{"disambiguationData":[TD([subQ83])],"derivedFrom":makeQuery(id+"F1.opRevolve","SWEPT_FACE",FACE,{"disambiguationData":[OSD([sQuery(id+"F0.wireOp",EDGE,"E13")])]})})})})})],"blendedInto":[makeQuery(id+"F40.boolean.opBoolean","SPLIT",FACE,{"disambiguationData":[TD([subQ0])],"derivedFrom":makeQuery(id+"F26.boolean.opBoolean","SPLIT",FACE,{"disambiguationData":[TD([subQ15])],"derivedFrom":makeQuery(id+"F25.boolean.opBoolean","SPLIT",FACE,{"disambiguationData":[TD([subQ83])],"derivedFrom":makeQuery(id+"F24.boolean.opBoolean","SPLIT",FACE,{"disambiguationData":[TD([subQ83])],"derivedFrom":makeQuery(id+"F1.opRevolve","SWEPT_FACE",FACE,{"disambiguationData":[OSD([sQuery(id+"F0.wireOp",EDGE,"E13")])]})})})})})]});}
            var Q11;
            {var subQ0=makeQuery(id+"F1.opRevolve","SWEPT_FACE",FACE,{"disambiguationData":[OSD([sQuery(id+"F0.wireOp",EDGE,"E12")])]});var subQ5=sQuery(id+"F3.wireOp",EDGE,"E20.10.3");var subQ6=sQuery(id+"F3.wireOp",EDGE,"E20.10.2");var subQ7=sQuery(id+"F3.wireOp",EDGE,"E20.10.1");var subQ8=makeQuery(id+"F25.opLoft","SWEPT_FACE",FACE,{"disambiguationData":[OSD([subQ7,subQ6,subQ5,sQuery(id+"F22.wireOp",EDGE,"E28.2.0"),sQuery(id+"F22.wireOp",EDGE,"E28.2.2"),sQuery(id+"F22.wireOp",EDGE,"E28.2.3")])]});var subQ9=makeQuery(id+"F40.opExtrude","CAP_FACE",FACE,{"disambiguationData":[OSD([sQuery(id+"F39.wireOp",EDGE,"E29"),sQuery(id+"F39.wireOp",EDGE,"E30")])],"isStart":true});var subQ12=sQuery(id+"F4.wireOp",EDGE,"E26.10.3");var subQ13=sQuery(id+"F4.wireOp",EDGE,"E26.10.2");var subQ14=makeQuery(id+"F11.opLoft","SWEPT_FACE",FACE,{"disambiguationData":[OSD([subQ7,subQ6,subQ5,sQuery(id+"F4.wireOp",EDGE,"E26.10.1"),subQ13,subQ12])]});var subQ90=sQuery(id+"F3.wireOp",EDGE,"E18.bottom");Q11=makeQuery(id+"F44.opFillet","BLEND_EDGE",EDGE,{"blendedFrom":[makeQuery(id+"F40.boolean.opBoolean","INTERSECT",EDGE,{"derivedFrom":[subQ8,subQ9]}),makeQuery(id+"F40.boolean.opBoolean","SPLIT",FACE,{"disambiguationData":[TD([subQ0])],"derivedFrom":makeQuery(id+"F25.boolean.opBoolean","SPLIT",FACE,{"disambiguationData":[TD([subQ14])],"derivedFrom":makeQuery(id+"F24.boolean.opBoolean","SPLIT",FACE,{"disambiguationData":[TD([makeQuery(id+"F5.opLoft","CAP_FACE",FACE,{"disambiguationData":[OSD([makeQuery(id+"F3.imprint","IMPRINT",FACE,{"disambiguationData":[TD([[makeQuery(id+"F3.imprint","IMPRINT",EDGE,{"derivedFrom":subQ90}),1.0]])]})])],"isStart":true})])],"derivedFrom":makeQuery(id+"F1.opRevolve","SWEPT_FACE",FACE,{"disambiguationData":[OSD([sQuery(id+"F0.wireOp",EDGE,"E13")])]})})})})],"blendedInto":[makeQuery(id+"F40.boolean.opBoolean","SPLIT",FACE,{"disambiguationData":[TD([subQ0])],"derivedFrom":makeQuery(id+"F25.boolean.opBoolean","SPLIT",FACE,{"disambiguationData":[TD([subQ14])],"derivedFrom":makeQuery(id+"F24.boolean.opBoolean","SPLIT",FACE,{"disambiguationData":[TD([makeQuery(id+"F5.opLoft","CAP_FACE",FACE,{"disambiguationData":[OSD([makeQuery(id+"F3.imprint","IMPRINT",FACE,{"disambiguationData":[TD([[makeQuery(id+"F3.imprint","IMPRINT",EDGE,{"derivedFrom":subQ90}),1.0]])]})])],"isStart":true})])],"derivedFrom":makeQuery(id+"F1.opRevolve","SWEPT_FACE",FACE,{"disambiguationData":[OSD([sQuery(id+"F0.wireOp",EDGE,"E13")])]})})})})]});}
            var Q12;
            {var subQ0=makeQuery(id+"F1.opRevolve","SWEPT_FACE",FACE,{"disambiguationData":[OSD([sQuery(id+"F0.wireOp",EDGE,"E12")])]});var subQ1=sQuery(id+"F3.wireOp",EDGE,"E20.9.3");var subQ2=sQuery(id+"F3.wireOp",EDGE,"E20.9.2");var subQ3=sQuery(id+"F3.wireOp",EDGE,"E20.9.1");var subQ4=makeQuery(id+"F24.opLoft","SWEPT_FACE",FACE,{"disambiguationData":[OSD([subQ3,subQ2,subQ1,sQuery(id+"F22.wireOp",EDGE,"E28.1.0"),sQuery(id+"F22.wireOp",EDGE,"E28.1.2"),sQuery(id+"F22.wireOp",EDGE,"E28.1.3")])]});var subQ9=makeQuery(id+"F40.opExtrude","CAP_FACE",FACE,{"disambiguationData":[OSD([sQuery(id+"F39.wireOp",EDGE,"E29"),sQuery(id+"F39.wireOp",EDGE,"E30")])],"isStart":true});Q12=makeQuery(id+"F44.opFillet","BLEND_EDGE",EDGE,{"blendedFrom":[makeQuery(id+"F40.boolean.opBoolean","INTERSECT",EDGE,{"derivedFrom":[subQ4,subQ9]}),makeQuery(id+"F40.boolean.opBoolean","SPLIT",FACE,{"disambiguationData":[TD([subQ0])],"derivedFrom":makeQuery(id+"F24.boolean.opBoolean","SPLIT",FACE,{"disambiguationData":[TD([makeQuery(id+"F12.opLoft","SWEPT_FACE",FACE,{"disambiguationData":[OSD([subQ3,subQ2,subQ1,sQuery(id+"F4.wireOp",EDGE,"E26.9.1"),sQuery(id+"F4.wireOp",EDGE,"E26.9.2"),sQuery(id+"F4.wireOp",EDGE,"E26.9.3")])]})])],"derivedFrom":makeQuery(id+"F1.opRevolve","SWEPT_FACE",FACE,{"disambiguationData":[OSD([sQuery(id+"F0.wireOp",EDGE,"E13")])]})})})],"blendedInto":[makeQuery(id+"F40.boolean.opBoolean","SPLIT",FACE,{"disambiguationData":[TD([subQ0])],"derivedFrom":makeQuery(id+"F24.boolean.opBoolean","SPLIT",FACE,{"disambiguationData":[TD([makeQuery(id+"F12.opLoft","SWEPT_FACE",FACE,{"disambiguationData":[OSD([subQ3,subQ2,subQ1,sQuery(id+"F4.wireOp",EDGE,"E26.9.1"),sQuery(id+"F4.wireOp",EDGE,"E26.9.2"),sQuery(id+"F4.wireOp",EDGE,"E26.9.3")])]})])],"derivedFrom":makeQuery(id+"F1.opRevolve","SWEPT_FACE",FACE,{"disambiguationData":[OSD([sQuery(id+"F0.wireOp",EDGE,"E13")])]})})})]});}
            var Q13;
            {var subQ0=makeQuery(id+"F1.opRevolve","SWEPT_FACE",FACE,{"disambiguationData":[OSD([sQuery(id+"F0.wireOp",EDGE,"E12")])]});var subQ1=sQuery(id+"F3.wireOp",EDGE,"E20.8.3");var subQ2=sQuery(id+"F3.wireOp",EDGE,"E20.8.2");var subQ3=sQuery(id+"F3.wireOp",EDGE,"E20.8.1");var subQ4=makeQuery(id+"F23.opLoft","SWEPT_FACE",FACE,{"disambiguationData":[OSD([subQ3,subQ2,subQ1,sQuery(id+"F22.wireOp",EDGE,"E27.bottom"),sQuery(id+"F22.wireOp",EDGE,"E27.top"),sQuery(id+"F22.wireOp",EDGE,"E27.left")])]});var subQ7=sQuery(id+"F3.wireOp",EDGE,"E20.7.0");var subQ9=makeQuery(id+"F40.opExtrude","CAP_FACE",FACE,{"disambiguationData":[OSD([sQuery(id+"F39.wireOp",EDGE,"E29"),sQuery(id+"F39.wireOp",EDGE,"E30")])],"isStart":true});var subQ10=makeQuery(id+"F13.opLoft","SWEPT_FACE",FACE,{"disambiguationData":[OSD([subQ3,subQ2,subQ1,sQuery(id+"F4.wireOp",EDGE,"E26.8.1"),sQuery(id+"F4.wireOp",EDGE,"E26.8.2"),sQuery(id+"F4.wireOp",EDGE,"E26.8.3")])]});var subQ17=makeQuery(id+"F14.opLoft","CAP_FACE",FACE,{"disambiguationData":[OSD([makeQuery(id+"F3.imprint","IMPRINT",FACE,{"disambiguationData":[TD([[makeQuery(id+"F3.imprint","IMPRINT",EDGE,{"derivedFrom":subQ7}),-1.0]])]})])],"isStart":true});var subQ75=sQuery(id+"F3.wireOp",EDGE,"E18.bottom");var subQ80=makeQuery(id+"F5.opLoft","CAP_FACE",FACE,{"disambiguationData":[OSD([makeQuery(id+"F3.imprint","IMPRINT",FACE,{"disambiguationData":[TD([[makeQuery(id+"F3.imprint","IMPRINT",EDGE,{"derivedFrom":subQ75}),1.0]])]})])],"isStart":true});Q13=makeQuery(id+"F44.opFillet","BLEND_EDGE",EDGE,{"blendedFrom":[makeQuery(id+"F40.boolean.opBoolean","INTERSECT",EDGE,{"derivedFrom":[subQ4,subQ9]}),makeQuery(id+"F40.boolean.opBoolean","SPLIT",FACE,{"disambiguationData":[TD([subQ0])],"derivedFrom":makeQuery(id+"F38.boolean.opBoolean","SPLIT",FACE,{"disambiguationData":[TD([subQ10])],"derivedFrom":makeQuery(id+"F37.boolean.opBoolean","SPLIT",FACE,{"disambiguationData":[TD([subQ17])],"derivedFrom":makeQuery(id+"F36.boolean.opBoolean","SPLIT",FACE,{"disambiguationData":[TD([subQ17])],"derivedFrom":makeQuery(id+"F35.boolean.opBoolean","SPLIT",FACE,{"disambiguationData":[TD([subQ17])],"derivedFrom":makeQuery(id+"F34.boolean.opBoolean","SPLIT",FACE,{"disambiguationData":[TD([subQ17])],"derivedFrom":makeQuery(id+"F33.boolean.opBoolean","SPLIT",FACE,{"disambiguationData":[TD([subQ17])],"derivedFrom":makeQuery(id+"F32.boolean.opBoolean","SPLIT",FACE,{"disambiguationData":[TD([subQ17])],"derivedFrom":makeQuery(id+"F31.boolean.opBoolean","SPLIT",FACE,{"disambiguationData":[TD([subQ17])],"derivedFrom":makeQuery(id+"F30.boolean.opBoolean","SPLIT",FACE,{"disambiguationData":[TD([subQ80])],"derivedFrom":makeQuery(id+"F29.boolean.opBoolean","SPLIT",FACE,{"disambiguationData":[TD([subQ80])],"derivedFrom":makeQuery(id+"F28.boolean.opBoolean","SPLIT",FACE,{"disambiguationData":[TD([subQ80])],"derivedFrom":makeQuery(id+"F27.boolean.opBoolean","SPLIT",FACE,{"disambiguationData":[TD([subQ80])],"derivedFrom":makeQuery(id+"F26.boolean.opBoolean","SPLIT",FACE,{"disambiguationData":[TD([subQ80])],"derivedFrom":makeQuery(id+"F25.boolean.opBoolean","SPLIT",FACE,{"disambiguationData":[TD([subQ80])],"derivedFrom":makeQuery(id+"F24.boolean.opBoolean","SPLIT",FACE,{"disambiguationData":[TD([subQ80])],"derivedFrom":makeQuery(id+"F1.opRevolve","SWEPT_FACE",FACE,{"disambiguationData":[OSD([sQuery(id+"F0.wireOp",EDGE,"E13")])]})})})})})})})})})})})})})})})})})],"blendedInto":[makeQuery(id+"F40.boolean.opBoolean","SPLIT",FACE,{"disambiguationData":[TD([subQ0])],"derivedFrom":makeQuery(id+"F38.boolean.opBoolean","SPLIT",FACE,{"disambiguationData":[TD([subQ10])],"derivedFrom":makeQuery(id+"F37.boolean.opBoolean","SPLIT",FACE,{"disambiguationData":[TD([subQ17])],"derivedFrom":makeQuery(id+"F36.boolean.opBoolean","SPLIT",FACE,{"disambiguationData":[TD([subQ17])],"derivedFrom":makeQuery(id+"F35.boolean.opBoolean","SPLIT",FACE,{"disambiguationData":[TD([subQ17])],"derivedFrom":makeQuery(id+"F34.boolean.opBoolean","SPLIT",FACE,{"disambiguationData":[TD([subQ17])],"derivedFrom":makeQuery(id+"F33.boolean.opBoolean","SPLIT",FACE,{"disambiguationData":[TD([subQ17])],"derivedFrom":makeQuery(id+"F32.boolean.opBoolean","SPLIT",FACE,{"disambiguationData":[TD([subQ17])],"derivedFrom":makeQuery(id+"F31.boolean.opBoolean","SPLIT",FACE,{"disambiguationData":[TD([subQ17])],"derivedFrom":makeQuery(id+"F30.boolean.opBoolean","SPLIT",FACE,{"disambiguationData":[TD([subQ80])],"derivedFrom":makeQuery(id+"F29.boolean.opBoolean","SPLIT",FACE,{"disambiguationData":[TD([subQ80])],"derivedFrom":makeQuery(id+"F28.boolean.opBoolean","SPLIT",FACE,{"disambiguationData":[TD([subQ80])],"derivedFrom":makeQuery(id+"F27.boolean.opBoolean","SPLIT",FACE,{"disambiguationData":[TD([subQ80])],"derivedFrom":makeQuery(id+"F26.boolean.opBoolean","SPLIT",FACE,{"disambiguationData":[TD([subQ80])],"derivedFrom":makeQuery(id+"F25.boolean.opBoolean","SPLIT",FACE,{"disambiguationData":[TD([subQ80])],"derivedFrom":makeQuery(id+"F24.boolean.opBoolean","SPLIT",FACE,{"disambiguationData":[TD([subQ80])],"derivedFrom":makeQuery(id+"F1.opRevolve","SWEPT_FACE",FACE,{"disambiguationData":[OSD([sQuery(id+"F0.wireOp",EDGE,"E13")])]})})})})})})})})})})})})})})})})})]});}
            var Q14;
            {var subQ0=makeQuery(id+"F1.opRevolve","SWEPT_FACE",FACE,{"disambiguationData":[OSD([sQuery(id+"F0.wireOp",EDGE,"E12")])]});var subQ5=sQuery(id+"F3.wireOp",EDGE,"E20.7.3");var subQ6=sQuery(id+"F3.wireOp",EDGE,"E20.7.2");var subQ7=sQuery(id+"F3.wireOp",EDGE,"E20.7.1");var subQ8=makeQuery(id+"F38.opLoft","SWEPT_FACE",FACE,{"disambiguationData":[OSD([subQ7,subQ6,subQ5,sQuery(id+"F22.wireOp",EDGE,"E28.15.0"),sQuery(id+"F22.wireOp",EDGE,"E28.15.2"),sQuery(id+"F22.wireOp",EDGE,"E28.15.3")])]});var subQ9=makeQuery(id+"F40.opExtrude","CAP_FACE",FACE,{"disambiguationData":[OSD([sQuery(id+"F39.wireOp",EDGE,"E29"),sQuery(id+"F39.wireOp",EDGE,"E30")])],"isStart":true});var subQ13=sQuery(id+"F4.wireOp",EDGE,"E26.7.3");var subQ14=sQuery(id+"F4.wireOp",EDGE,"E26.7.2");var subQ15=makeQuery(id+"F14.opLoft","SWEPT_FACE",FACE,{"disambiguationData":[OSD([subQ7,subQ6,subQ5,sQuery(id+"F4.wireOp",EDGE,"E26.7.1"),subQ14,subQ13])]});var subQ21=sQuery(id+"F3.wireOp",EDGE,"E20.7.0");var subQ23=makeQuery(id+"F14.opLoft","CAP_FACE",FACE,{"disambiguationData":[OSD([makeQuery(id+"F3.imprint","IMPRINT",FACE,{"disambiguationData":[TD([[makeQuery(id+"F3.imprint","IMPRINT",EDGE,{"derivedFrom":subQ21}),-1.0]])]})])],"isStart":true});var subQ76=sQuery(id+"F3.wireOp",EDGE,"E18.bottom");var subQ81=makeQuery(id+"F5.opLoft","CAP_FACE",FACE,{"disambiguationData":[OSD([makeQuery(id+"F3.imprint","IMPRINT",FACE,{"disambiguationData":[TD([[makeQuery(id+"F3.imprint","IMPRINT",EDGE,{"derivedFrom":subQ76}),1.0]])]})])],"isStart":true});Q14=makeQuery(id+"F44.opFillet","BLEND_EDGE",EDGE,{"blendedFrom":[makeQuery(id+"F40.boolean.opBoolean","INTERSECT",EDGE,{"derivedFrom":[subQ8,subQ9]}),makeQuery(id+"F40.boolean.opBoolean","SPLIT",FACE,{"disambiguationData":[TD([subQ0])],"derivedFrom":makeQuery(id+"F38.boolean.opBoolean","SPLIT",FACE,{"disambiguationData":[TD([subQ15])],"derivedFrom":makeQuery(id+"F37.boolean.opBoolean","SPLIT",FACE,{"disambiguationData":[TD([subQ23])],"derivedFrom":makeQuery(id+"F36.boolean.opBoolean","SPLIT",FACE,{"disambiguationData":[TD([subQ23])],"derivedFrom":makeQuery(id+"F35.boolean.opBoolean","SPLIT",FACE,{"disambiguationData":[TD([subQ23])],"derivedFrom":makeQuery(id+"F34.boolean.opBoolean","SPLIT",FACE,{"disambiguationData":[TD([subQ23])],"derivedFrom":makeQuery(id+"F33.boolean.opBoolean","SPLIT",FACE,{"disambiguationData":[TD([subQ23])],"derivedFrom":makeQuery(id+"F32.boolean.opBoolean","SPLIT",FACE,{"disambiguationData":[TD([subQ23])],"derivedFrom":makeQuery(id+"F31.boolean.opBoolean","SPLIT",FACE,{"disambiguationData":[TD([subQ23])],"derivedFrom":makeQuery(id+"F30.boolean.opBoolean","SPLIT",FACE,{"disambiguationData":[TD([subQ81])],"derivedFrom":makeQuery(id+"F29.boolean.opBoolean","SPLIT",FACE,{"disambiguationData":[TD([subQ81])],"derivedFrom":makeQuery(id+"F28.boolean.opBoolean","SPLIT",FACE,{"disambiguationData":[TD([subQ81])],"derivedFrom":makeQuery(id+"F27.boolean.opBoolean","SPLIT",FACE,{"disambiguationData":[TD([subQ81])],"derivedFrom":makeQuery(id+"F26.boolean.opBoolean","SPLIT",FACE,{"disambiguationData":[TD([subQ81])],"derivedFrom":makeQuery(id+"F25.boolean.opBoolean","SPLIT",FACE,{"disambiguationData":[TD([subQ81])],"derivedFrom":makeQuery(id+"F24.boolean.opBoolean","SPLIT",FACE,{"disambiguationData":[TD([subQ81])],"derivedFrom":makeQuery(id+"F1.opRevolve","SWEPT_FACE",FACE,{"disambiguationData":[OSD([sQuery(id+"F0.wireOp",EDGE,"E13")])]})})})})})})})})})})})})})})})})})],"blendedInto":[makeQuery(id+"F40.boolean.opBoolean","SPLIT",FACE,{"disambiguationData":[TD([subQ0])],"derivedFrom":makeQuery(id+"F38.boolean.opBoolean","SPLIT",FACE,{"disambiguationData":[TD([subQ15])],"derivedFrom":makeQuery(id+"F37.boolean.opBoolean","SPLIT",FACE,{"disambiguationData":[TD([subQ23])],"derivedFrom":makeQuery(id+"F36.boolean.opBoolean","SPLIT",FACE,{"disambiguationData":[TD([subQ23])],"derivedFrom":makeQuery(id+"F35.boolean.opBoolean","SPLIT",FACE,{"disambiguationData":[TD([subQ23])],"derivedFrom":makeQuery(id+"F34.boolean.opBoolean","SPLIT",FACE,{"disambiguationData":[TD([subQ23])],"derivedFrom":makeQuery(id+"F33.boolean.opBoolean","SPLIT",FACE,{"disambiguationData":[TD([subQ23])],"derivedFrom":makeQuery(id+"F32.boolean.opBoolean","SPLIT",FACE,{"disambiguationData":[TD([subQ23])],"derivedFrom":makeQuery(id+"F31.boolean.opBoolean","SPLIT",FACE,{"disambiguationData":[TD([subQ23])],"derivedFrom":makeQuery(id+"F30.boolean.opBoolean","SPLIT",FACE,{"disambiguationData":[TD([subQ81])],"derivedFrom":makeQuery(id+"F29.boolean.opBoolean","SPLIT",FACE,{"disambiguationData":[TD([subQ81])],"derivedFrom":makeQuery(id+"F28.boolean.opBoolean","SPLIT",FACE,{"disambiguationData":[TD([subQ81])],"derivedFrom":makeQuery(id+"F27.boolean.opBoolean","SPLIT",FACE,{"disambiguationData":[TD([subQ81])],"derivedFrom":makeQuery(id+"F26.boolean.opBoolean","SPLIT",FACE,{"disambiguationData":[TD([subQ81])],"derivedFrom":makeQuery(id+"F25.boolean.opBoolean","SPLIT",FACE,{"disambiguationData":[TD([subQ81])],"derivedFrom":makeQuery(id+"F24.boolean.opBoolean","SPLIT",FACE,{"disambiguationData":[TD([subQ81])],"derivedFrom":makeQuery(id+"F1.opRevolve","SWEPT_FACE",FACE,{"disambiguationData":[OSD([sQuery(id+"F0.wireOp",EDGE,"E13")])]})})})})})})})})})})})})})})})})})]});}
            var Q15;
            {var subQ0=makeQuery(id+"F1.opRevolve","SWEPT_FACE",FACE,{"disambiguationData":[OSD([sQuery(id+"F0.wireOp",EDGE,"E12")])]});var subQ5=sQuery(id+"F3.wireOp",EDGE,"E20.6.3");var subQ6=sQuery(id+"F3.wireOp",EDGE,"E20.6.2");var subQ7=sQuery(id+"F3.wireOp",EDGE,"E20.6.1");var subQ8=makeQuery(id+"F37.opLoft","SWEPT_FACE",FACE,{"disambiguationData":[OSD([subQ7,subQ6,subQ5,sQuery(id+"F22.wireOp",EDGE,"E28.14.0"),sQuery(id+"F22.wireOp",EDGE,"E28.14.2"),sQuery(id+"F22.wireOp",EDGE,"E28.14.3")])]});var subQ9=makeQuery(id+"F40.opExtrude","CAP_FACE",FACE,{"disambiguationData":[OSD([sQuery(id+"F39.wireOp",EDGE,"E29"),sQuery(id+"F39.wireOp",EDGE,"E30")])],"isStart":true});var subQ13=sQuery(id+"F4.wireOp",EDGE,"E26.6.3");var subQ14=sQuery(id+"F4.wireOp",EDGE,"E26.6.2");var subQ15=makeQuery(id+"F15.opLoft","SWEPT_FACE",FACE,{"disambiguationData":[OSD([subQ7,subQ6,subQ5,sQuery(id+"F4.wireOp",EDGE,"E26.6.1"),subQ14,subQ13])]});var subQ20=sQuery(id+"F3.wireOp",EDGE,"E20.7.0");var subQ24=makeQuery(id+"F14.opLoft","CAP_FACE",FACE,{"disambiguationData":[OSD([makeQuery(id+"F3.imprint","IMPRINT",FACE,{"disambiguationData":[TD([[makeQuery(id+"F3.imprint","IMPRINT",EDGE,{"derivedFrom":subQ20}),-1.0]])]})])],"isStart":true});var subQ76=sQuery(id+"F3.wireOp",EDGE,"E18.bottom");var subQ81=makeQuery(id+"F5.opLoft","CAP_FACE",FACE,{"disambiguationData":[OSD([makeQuery(id+"F3.imprint","IMPRINT",FACE,{"disambiguationData":[TD([[makeQuery(id+"F3.imprint","IMPRINT",EDGE,{"derivedFrom":subQ76}),1.0]])]})])],"isStart":true});Q15=makeQuery(id+"F44.opFillet","BLEND_EDGE",EDGE,{"blendedFrom":[makeQuery(id+"F40.boolean.opBoolean","INTERSECT",EDGE,{"derivedFrom":[subQ8,subQ9]}),makeQuery(id+"F40.boolean.opBoolean","SPLIT",FACE,{"disambiguationData":[TD([subQ0])],"derivedFrom":makeQuery(id+"F37.boolean.opBoolean","SPLIT",FACE,{"disambiguationData":[TD([subQ15])],"derivedFrom":makeQuery(id+"F36.boolean.opBoolean","SPLIT",FACE,{"disambiguationData":[TD([subQ24])],"derivedFrom":makeQuery(id+"F35.boolean.opBoolean","SPLIT",FACE,{"disambiguationData":[TD([subQ24])],"derivedFrom":makeQuery(id+"F34.boolean.opBoolean","SPLIT",FACE,{"disambiguationData":[TD([subQ24])],"derivedFrom":makeQuery(id+"F33.boolean.opBoolean","SPLIT",FACE,{"disambiguationData":[TD([subQ24])],"derivedFrom":makeQuery(id+"F32.boolean.opBoolean","SPLIT",FACE,{"disambiguationData":[TD([subQ24])],"derivedFrom":makeQuery(id+"F31.boolean.opBoolean","SPLIT",FACE,{"disambiguationData":[TD([subQ24])],"derivedFrom":makeQuery(id+"F30.boolean.opBoolean","SPLIT",FACE,{"disambiguationData":[TD([subQ81])],"derivedFrom":makeQuery(id+"F29.boolean.opBoolean","SPLIT",FACE,{"disambiguationData":[TD([subQ81])],"derivedFrom":makeQuery(id+"F28.boolean.opBoolean","SPLIT",FACE,{"disambiguationData":[TD([subQ81])],"derivedFrom":makeQuery(id+"F27.boolean.opBoolean","SPLIT",FACE,{"disambiguationData":[TD([subQ81])],"derivedFrom":makeQuery(id+"F26.boolean.opBoolean","SPLIT",FACE,{"disambiguationData":[TD([subQ81])],"derivedFrom":makeQuery(id+"F25.boolean.opBoolean","SPLIT",FACE,{"disambiguationData":[TD([subQ81])],"derivedFrom":makeQuery(id+"F24.boolean.opBoolean","SPLIT",FACE,{"disambiguationData":[TD([subQ81])],"derivedFrom":makeQuery(id+"F1.opRevolve","SWEPT_FACE",FACE,{"disambiguationData":[OSD([sQuery(id+"F0.wireOp",EDGE,"E13")])]})})})})})})})})})})})})})})})})],"blendedInto":[makeQuery(id+"F40.boolean.opBoolean","SPLIT",FACE,{"disambiguationData":[TD([subQ0])],"derivedFrom":makeQuery(id+"F37.boolean.opBoolean","SPLIT",FACE,{"disambiguationData":[TD([subQ15])],"derivedFrom":makeQuery(id+"F36.boolean.opBoolean","SPLIT",FACE,{"disambiguationData":[TD([subQ24])],"derivedFrom":makeQuery(id+"F35.boolean.opBoolean","SPLIT",FACE,{"disambiguationData":[TD([subQ24])],"derivedFrom":makeQuery(id+"F34.boolean.opBoolean","SPLIT",FACE,{"disambiguationData":[TD([subQ24])],"derivedFrom":makeQuery(id+"F33.boolean.opBoolean","SPLIT",FACE,{"disambiguationData":[TD([subQ24])],"derivedFrom":makeQuery(id+"F32.boolean.opBoolean","SPLIT",FACE,{"disambiguationData":[TD([subQ24])],"derivedFrom":makeQuery(id+"F31.boolean.opBoolean","SPLIT",FACE,{"disambiguationData":[TD([subQ24])],"derivedFrom":makeQuery(id+"F30.boolean.opBoolean","SPLIT",FACE,{"disambiguationData":[TD([subQ81])],"derivedFrom":makeQuery(id+"F29.boolean.opBoolean","SPLIT",FACE,{"disambiguationData":[TD([subQ81])],"derivedFrom":makeQuery(id+"F28.boolean.opBoolean","SPLIT",FACE,{"disambiguationData":[TD([subQ81])],"derivedFrom":makeQuery(id+"F27.boolean.opBoolean","SPLIT",FACE,{"disambiguationData":[TD([subQ81])],"derivedFrom":makeQuery(id+"F26.boolean.opBoolean","SPLIT",FACE,{"disambiguationData":[TD([subQ81])],"derivedFrom":makeQuery(id+"F25.boolean.opBoolean","SPLIT",FACE,{"disambiguationData":[TD([subQ81])],"derivedFrom":makeQuery(id+"F24.boolean.opBoolean","SPLIT",FACE,{"disambiguationData":[TD([subQ81])],"derivedFrom":makeQuery(id+"F1.opRevolve","SWEPT_FACE",FACE,{"disambiguationData":[OSD([sQuery(id+"F0.wireOp",EDGE,"E13")])]})})})})})})})})})})})})})})})})]});}
            var Q16;
            {var subQ0=makeQuery(id+"F1.opRevolve","SWEPT_FACE",FACE,{"disambiguationData":[OSD([sQuery(id+"F0.wireOp",EDGE,"E12")])]});var subQ1=sQuery(id+"F3.wireOp",EDGE,"E20.5.3");var subQ2=sQuery(id+"F3.wireOp",EDGE,"E20.5.2");var subQ3=sQuery(id+"F3.wireOp",EDGE,"E20.5.1");var subQ4=makeQuery(id+"F36.opLoft","SWEPT_FACE",FACE,{"disambiguationData":[OSD([subQ3,subQ2,subQ1,sQuery(id+"F22.wireOp",EDGE,"E28.13.0"),sQuery(id+"F22.wireOp",EDGE,"E28.13.2"),sQuery(id+"F22.wireOp",EDGE,"E28.13.3")])]});var subQ9=makeQuery(id+"F40.opExtrude","CAP_FACE",FACE,{"disambiguationData":[OSD([sQuery(id+"F39.wireOp",EDGE,"E29"),sQuery(id+"F39.wireOp",EDGE,"E30")])],"isStart":true});var subQ10=sQuery(id+"F4.wireOp",EDGE,"E26.5.3");var subQ11=sQuery(id+"F4.wireOp",EDGE,"E26.5.2");var subQ12=makeQuery(id+"F16.opLoft","SWEPT_FACE",FACE,{"disambiguationData":[OSD([subQ3,subQ2,subQ1,sQuery(id+"F4.wireOp",EDGE,"E26.5.1"),subQ11,subQ10])]});var subQ27=sQuery(id+"F3.wireOp",EDGE,"E20.7.0");var subQ31=makeQuery(id+"F14.opLoft","CAP_FACE",FACE,{"disambiguationData":[OSD([makeQuery(id+"F3.imprint","IMPRINT",FACE,{"disambiguationData":[TD([[makeQuery(id+"F3.imprint","IMPRINT",EDGE,{"derivedFrom":subQ27}),-1.0]])]})])],"isStart":true});var subQ76=sQuery(id+"F3.wireOp",EDGE,"E18.bottom");var subQ81=makeQuery(id+"F5.opLoft","CAP_FACE",FACE,{"disambiguationData":[OSD([makeQuery(id+"F3.imprint","IMPRINT",FACE,{"disambiguationData":[TD([[makeQuery(id+"F3.imprint","IMPRINT",EDGE,{"derivedFrom":subQ76}),1.0]])]})])],"isStart":true});Q16=makeQuery(id+"F44.opFillet","BLEND_EDGE",EDGE,{"blendedFrom":[makeQuery(id+"F40.boolean.opBoolean","INTERSECT",EDGE,{"derivedFrom":[subQ4,subQ9]}),makeQuery(id+"F40.boolean.opBoolean","SPLIT",FACE,{"disambiguationData":[TD([subQ0])],"derivedFrom":makeQuery(id+"F36.boolean.opBoolean","SPLIT",FACE,{"disambiguationData":[TD([subQ12])],"derivedFrom":makeQuery(id+"F35.boolean.opBoolean","SPLIT",FACE,{"disambiguationData":[TD([subQ31])],"derivedFrom":makeQuery(id+"F34.boolean.opBoolean","SPLIT",FACE,{"disambiguationData":[TD([subQ31])],"derivedFrom":makeQuery(id+"F33.boolean.opBoolean","SPLIT",FACE,{"disambiguationData":[TD([subQ31])],"derivedFrom":makeQuery(id+"F32.boolean.opBoolean","SPLIT",FACE,{"disambiguationData":[TD([subQ31])],"derivedFrom":makeQuery(id+"F31.boolean.opBoolean","SPLIT",FACE,{"disambiguationData":[TD([subQ31])],"derivedFrom":makeQuery(id+"F30.boolean.opBoolean","SPLIT",FACE,{"disambiguationData":[TD([subQ81])],"derivedFrom":makeQuery(id+"F29.boolean.opBoolean","SPLIT",FACE,{"disambiguationData":[TD([subQ81])],"derivedFrom":makeQuery(id+"F28.boolean.opBoolean","SPLIT",FACE,{"disambiguationData":[TD([subQ81])],"derivedFrom":makeQuery(id+"F27.boolean.opBoolean","SPLIT",FACE,{"disambiguationData":[TD([subQ81])],"derivedFrom":makeQuery(id+"F26.boolean.opBoolean","SPLIT",FACE,{"disambiguationData":[TD([subQ81])],"derivedFrom":makeQuery(id+"F25.boolean.opBoolean","SPLIT",FACE,{"disambiguationData":[TD([subQ81])],"derivedFrom":makeQuery(id+"F24.boolean.opBoolean","SPLIT",FACE,{"disambiguationData":[TD([subQ81])],"derivedFrom":makeQuery(id+"F1.opRevolve","SWEPT_FACE",FACE,{"disambiguationData":[OSD([sQuery(id+"F0.wireOp",EDGE,"E13")])]})})})})})})})})})})})})})})})],"blendedInto":[makeQuery(id+"F40.boolean.opBoolean","SPLIT",FACE,{"disambiguationData":[TD([subQ0])],"derivedFrom":makeQuery(id+"F36.boolean.opBoolean","SPLIT",FACE,{"disambiguationData":[TD([subQ12])],"derivedFrom":makeQuery(id+"F35.boolean.opBoolean","SPLIT",FACE,{"disambiguationData":[TD([subQ31])],"derivedFrom":makeQuery(id+"F34.boolean.opBoolean","SPLIT",FACE,{"disambiguationData":[TD([subQ31])],"derivedFrom":makeQuery(id+"F33.boolean.opBoolean","SPLIT",FACE,{"disambiguationData":[TD([subQ31])],"derivedFrom":makeQuery(id+"F32.boolean.opBoolean","SPLIT",FACE,{"disambiguationData":[TD([subQ31])],"derivedFrom":makeQuery(id+"F31.boolean.opBoolean","SPLIT",FACE,{"disambiguationData":[TD([subQ31])],"derivedFrom":makeQuery(id+"F30.boolean.opBoolean","SPLIT",FACE,{"disambiguationData":[TD([subQ81])],"derivedFrom":makeQuery(id+"F29.boolean.opBoolean","SPLIT",FACE,{"disambiguationData":[TD([subQ81])],"derivedFrom":makeQuery(id+"F28.boolean.opBoolean","SPLIT",FACE,{"disambiguationData":[TD([subQ81])],"derivedFrom":makeQuery(id+"F27.boolean.opBoolean","SPLIT",FACE,{"disambiguationData":[TD([subQ81])],"derivedFrom":makeQuery(id+"F26.boolean.opBoolean","SPLIT",FACE,{"disambiguationData":[TD([subQ81])],"derivedFrom":makeQuery(id+"F25.boolean.opBoolean","SPLIT",FACE,{"disambiguationData":[TD([subQ81])],"derivedFrom":makeQuery(id+"F24.boolean.opBoolean","SPLIT",FACE,{"disambiguationData":[TD([subQ81])],"derivedFrom":makeQuery(id+"F1.opRevolve","SWEPT_FACE",FACE,{"disambiguationData":[OSD([sQuery(id+"F0.wireOp",EDGE,"E13")])]})})})})})})})})})})})})})})})]});}
            var Q17;
            {var subQ0=makeQuery(id+"F1.opRevolve","SWEPT_FACE",FACE,{"disambiguationData":[OSD([sQuery(id+"F0.wireOp",EDGE,"E12")])]});var subQ5=sQuery(id+"F3.wireOp",EDGE,"E20.4.3");var subQ6=sQuery(id+"F3.wireOp",EDGE,"E20.4.2");var subQ7=sQuery(id+"F3.wireOp",EDGE,"E20.4.1");var subQ8=makeQuery(id+"F35.opLoft","SWEPT_FACE",FACE,{"disambiguationData":[OSD([subQ7,subQ6,subQ5,sQuery(id+"F22.wireOp",EDGE,"E28.12.0"),sQuery(id+"F22.wireOp",EDGE,"E28.12.2"),sQuery(id+"F22.wireOp",EDGE,"E28.12.3")])]});var subQ9=makeQuery(id+"F40.opExtrude","CAP_FACE",FACE,{"disambiguationData":[OSD([sQuery(id+"F39.wireOp",EDGE,"E29"),sQuery(id+"F39.wireOp",EDGE,"E30")])],"isStart":true});var subQ10=sQuery(id+"F4.wireOp",EDGE,"E26.4.3");var subQ11=sQuery(id+"F4.wireOp",EDGE,"E26.4.2");var subQ12=makeQuery(id+"F17.opLoft","SWEPT_FACE",FACE,{"disambiguationData":[OSD([subQ7,subQ6,subQ5,sQuery(id+"F4.wireOp",EDGE,"E26.4.1"),subQ11,subQ10])]});var subQ33=sQuery(id+"F3.wireOp",EDGE,"E20.7.0");var subQ37=makeQuery(id+"F14.opLoft","CAP_FACE",FACE,{"disambiguationData":[OSD([makeQuery(id+"F3.imprint","IMPRINT",FACE,{"disambiguationData":[TD([[makeQuery(id+"F3.imprint","IMPRINT",EDGE,{"derivedFrom":subQ33}),-1.0]])]})])],"isStart":true});var subQ76=sQuery(id+"F3.wireOp",EDGE,"E18.bottom");var subQ81=makeQuery(id+"F5.opLoft","CAP_FACE",FACE,{"disambiguationData":[OSD([makeQuery(id+"F3.imprint","IMPRINT",FACE,{"disambiguationData":[TD([[makeQuery(id+"F3.imprint","IMPRINT",EDGE,{"derivedFrom":subQ76}),1.0]])]})])],"isStart":true});Q17=makeQuery(id+"F44.opFillet","BLEND_EDGE",EDGE,{"blendedFrom":[makeQuery(id+"F40.boolean.opBoolean","INTERSECT",EDGE,{"derivedFrom":[subQ8,subQ9]}),makeQuery(id+"F40.boolean.opBoolean","SPLIT",FACE,{"disambiguationData":[TD([subQ0])],"derivedFrom":makeQuery(id+"F35.boolean.opBoolean","SPLIT",FACE,{"disambiguationData":[TD([subQ12])],"derivedFrom":makeQuery(id+"F34.boolean.opBoolean","SPLIT",FACE,{"disambiguationData":[TD([subQ37])],"derivedFrom":makeQuery(id+"F33.boolean.opBoolean","SPLIT",FACE,{"disambiguationData":[TD([subQ37])],"derivedFrom":makeQuery(id+"F32.boolean.opBoolean","SPLIT",FACE,{"disambiguationData":[TD([subQ37])],"derivedFrom":makeQuery(id+"F31.boolean.opBoolean","SPLIT",FACE,{"disambiguationData":[TD([subQ37])],"derivedFrom":makeQuery(id+"F30.boolean.opBoolean","SPLIT",FACE,{"disambiguationData":[TD([subQ81])],"derivedFrom":makeQuery(id+"F29.boolean.opBoolean","SPLIT",FACE,{"disambiguationData":[TD([subQ81])],"derivedFrom":makeQuery(id+"F28.boolean.opBoolean","SPLIT",FACE,{"disambiguationData":[TD([subQ81])],"derivedFrom":makeQuery(id+"F27.boolean.opBoolean","SPLIT",FACE,{"disambiguationData":[TD([subQ81])],"derivedFrom":makeQuery(id+"F26.boolean.opBoolean","SPLIT",FACE,{"disambiguationData":[TD([subQ81])],"derivedFrom":makeQuery(id+"F25.boolean.opBoolean","SPLIT",FACE,{"disambiguationData":[TD([subQ81])],"derivedFrom":makeQuery(id+"F24.boolean.opBoolean","SPLIT",FACE,{"disambiguationData":[TD([subQ81])],"derivedFrom":makeQuery(id+"F1.opRevolve","SWEPT_FACE",FACE,{"disambiguationData":[OSD([sQuery(id+"F0.wireOp",EDGE,"E13")])]})})})})})})})})})})})})})})],"blendedInto":[makeQuery(id+"F40.boolean.opBoolean","SPLIT",FACE,{"disambiguationData":[TD([subQ0])],"derivedFrom":makeQuery(id+"F35.boolean.opBoolean","SPLIT",FACE,{"disambiguationData":[TD([subQ12])],"derivedFrom":makeQuery(id+"F34.boolean.opBoolean","SPLIT",FACE,{"disambiguationData":[TD([subQ37])],"derivedFrom":makeQuery(id+"F33.boolean.opBoolean","SPLIT",FACE,{"disambiguationData":[TD([subQ37])],"derivedFrom":makeQuery(id+"F32.boolean.opBoolean","SPLIT",FACE,{"disambiguationData":[TD([subQ37])],"derivedFrom":makeQuery(id+"F31.boolean.opBoolean","SPLIT",FACE,{"disambiguationData":[TD([subQ37])],"derivedFrom":makeQuery(id+"F30.boolean.opBoolean","SPLIT",FACE,{"disambiguationData":[TD([subQ81])],"derivedFrom":makeQuery(id+"F29.boolean.opBoolean","SPLIT",FACE,{"disambiguationData":[TD([subQ81])],"derivedFrom":makeQuery(id+"F28.boolean.opBoolean","SPLIT",FACE,{"disambiguationData":[TD([subQ81])],"derivedFrom":makeQuery(id+"F27.boolean.opBoolean","SPLIT",FACE,{"disambiguationData":[TD([subQ81])],"derivedFrom":makeQuery(id+"F26.boolean.opBoolean","SPLIT",FACE,{"disambiguationData":[TD([subQ81])],"derivedFrom":makeQuery(id+"F25.boolean.opBoolean","SPLIT",FACE,{"disambiguationData":[TD([subQ81])],"derivedFrom":makeQuery(id+"F24.boolean.opBoolean","SPLIT",FACE,{"disambiguationData":[TD([subQ81])],"derivedFrom":makeQuery(id+"F1.opRevolve","SWEPT_FACE",FACE,{"disambiguationData":[OSD([sQuery(id+"F0.wireOp",EDGE,"E13")])]})})})})})})})})})})})})})})]});}
            var Q18;
            {var subQ0=makeQuery(id+"F1.opRevolve","SWEPT_FACE",FACE,{"disambiguationData":[OSD([sQuery(id+"F0.wireOp",EDGE,"E12")])]});var subQ5=makeQuery(id+"F40.opExtrude","CAP_FACE",FACE,{"disambiguationData":[OSD([sQuery(id+"F39.wireOp",EDGE,"E29"),sQuery(id+"F39.wireOp",EDGE,"E30")])],"isStart":true});var subQ6=sQuery(id+"F3.wireOp",EDGE,"E20.3.3");var subQ7=sQuery(id+"F3.wireOp",EDGE,"E20.3.2");var subQ8=sQuery(id+"F3.wireOp",EDGE,"E20.3.1");var subQ9=makeQuery(id+"F34.opLoft","SWEPT_FACE",FACE,{"disambiguationData":[OSD([subQ8,subQ7,subQ6,sQuery(id+"F22.wireOp",EDGE,"E28.11.0"),sQuery(id+"F22.wireOp",EDGE,"E28.11.2"),sQuery(id+"F22.wireOp",EDGE,"E28.11.3")])]});var subQ13=sQuery(id+"F4.wireOp",EDGE,"E26.3.3");var subQ14=sQuery(id+"F4.wireOp",EDGE,"E26.3.2");var subQ15=makeQuery(id+"F18.opLoft","SWEPT_FACE",FACE,{"disambiguationData":[OSD([subQ8,subQ7,subQ6,sQuery(id+"F4.wireOp",EDGE,"E26.3.1"),subQ14,subQ13])]});var subQ36=sQuery(id+"F3.wireOp",EDGE,"E20.7.0");var subQ40=makeQuery(id+"F14.opLoft","CAP_FACE",FACE,{"disambiguationData":[OSD([makeQuery(id+"F3.imprint","IMPRINT",FACE,{"disambiguationData":[TD([[makeQuery(id+"F3.imprint","IMPRINT",EDGE,{"derivedFrom":subQ36}),-1.0]])]})])],"isStart":true});var subQ76=sQuery(id+"F3.wireOp",EDGE,"E18.bottom");var subQ81=makeQuery(id+"F5.opLoft","CAP_FACE",FACE,{"disambiguationData":[OSD([makeQuery(id+"F3.imprint","IMPRINT",FACE,{"disambiguationData":[TD([[makeQuery(id+"F3.imprint","IMPRINT",EDGE,{"derivedFrom":subQ76}),1.0]])]})])],"isStart":true});Q18=makeQuery(id+"F44.opFillet","BLEND_EDGE",EDGE,{"blendedFrom":[makeQuery(id+"F40.boolean.opBoolean","INTERSECT",EDGE,{"derivedFrom":[subQ9,subQ5]}),makeQuery(id+"F40.boolean.opBoolean","SPLIT",FACE,{"disambiguationData":[TD([subQ0])],"derivedFrom":makeQuery(id+"F34.boolean.opBoolean","SPLIT",FACE,{"disambiguationData":[TD([subQ15])],"derivedFrom":makeQuery(id+"F33.boolean.opBoolean","SPLIT",FACE,{"disambiguationData":[TD([subQ40])],"derivedFrom":makeQuery(id+"F32.boolean.opBoolean","SPLIT",FACE,{"disambiguationData":[TD([subQ40])],"derivedFrom":makeQuery(id+"F31.boolean.opBoolean","SPLIT",FACE,{"disambiguationData":[TD([subQ40])],"derivedFrom":makeQuery(id+"F30.boolean.opBoolean","SPLIT",FACE,{"disambiguationData":[TD([subQ81])],"derivedFrom":makeQuery(id+"F29.boolean.opBoolean","SPLIT",FACE,{"disambiguationData":[TD([subQ81])],"derivedFrom":makeQuery(id+"F28.boolean.opBoolean","SPLIT",FACE,{"disambiguationData":[TD([subQ81])],"derivedFrom":makeQuery(id+"F27.boolean.opBoolean","SPLIT",FACE,{"disambiguationData":[TD([subQ81])],"derivedFrom":makeQuery(id+"F26.boolean.opBoolean","SPLIT",FACE,{"disambiguationData":[TD([subQ81])],"derivedFrom":makeQuery(id+"F25.boolean.opBoolean","SPLIT",FACE,{"disambiguationData":[TD([subQ81])],"derivedFrom":makeQuery(id+"F24.boolean.opBoolean","SPLIT",FACE,{"disambiguationData":[TD([subQ81])],"derivedFrom":makeQuery(id+"F1.opRevolve","SWEPT_FACE",FACE,{"disambiguationData":[OSD([sQuery(id+"F0.wireOp",EDGE,"E13")])]})})})})})})})})})})})})})],"blendedInto":[makeQuery(id+"F40.boolean.opBoolean","SPLIT",FACE,{"disambiguationData":[TD([subQ0])],"derivedFrom":makeQuery(id+"F34.boolean.opBoolean","SPLIT",FACE,{"disambiguationData":[TD([subQ15])],"derivedFrom":makeQuery(id+"F33.boolean.opBoolean","SPLIT",FACE,{"disambiguationData":[TD([subQ40])],"derivedFrom":makeQuery(id+"F32.boolean.opBoolean","SPLIT",FACE,{"disambiguationData":[TD([subQ40])],"derivedFrom":makeQuery(id+"F31.boolean.opBoolean","SPLIT",FACE,{"disambiguationData":[TD([subQ40])],"derivedFrom":makeQuery(id+"F30.boolean.opBoolean","SPLIT",FACE,{"disambiguationData":[TD([subQ81])],"derivedFrom":makeQuery(id+"F29.boolean.opBoolean","SPLIT",FACE,{"disambiguationData":[TD([subQ81])],"derivedFrom":makeQuery(id+"F28.boolean.opBoolean","SPLIT",FACE,{"disambiguationData":[TD([subQ81])],"derivedFrom":makeQuery(id+"F27.boolean.opBoolean","SPLIT",FACE,{"disambiguationData":[TD([subQ81])],"derivedFrom":makeQuery(id+"F26.boolean.opBoolean","SPLIT",FACE,{"disambiguationData":[TD([subQ81])],"derivedFrom":makeQuery(id+"F25.boolean.opBoolean","SPLIT",FACE,{"disambiguationData":[TD([subQ81])],"derivedFrom":makeQuery(id+"F24.boolean.opBoolean","SPLIT",FACE,{"disambiguationData":[TD([subQ81])],"derivedFrom":makeQuery(id+"F1.opRevolve","SWEPT_FACE",FACE,{"disambiguationData":[OSD([sQuery(id+"F0.wireOp",EDGE,"E13")])]})})})})})})})})})})})})})]});}
            var Q19;
            {var subQ0=makeQuery(id+"F1.opRevolve","SWEPT_FACE",FACE,{"disambiguationData":[OSD([sQuery(id+"F0.wireOp",EDGE,"E10")])]});var subQ1=sQuery(id+"F4.wireOp",EDGE,"E26.3.3");var subQ2=sQuery(id+"F4.wireOp",EDGE,"E26.3.2");var subQ3=sQuery(id+"F3.wireOp",EDGE,"E20.3.3");var subQ4=sQuery(id+"F3.wireOp",EDGE,"E20.3.2");var subQ5=sQuery(id+"F3.wireOp",EDGE,"E20.3.1");var subQ6=makeQuery(id+"F18.opLoft","SWEPT_FACE",FACE,{"disambiguationData":[OSD([subQ5,subQ4,subQ3,sQuery(id+"F4.wireOp",EDGE,"E26.3.1"),subQ2,subQ1])]});var subQ13=makeQuery(id+"F40.opExtrude","CAP_FACE",FACE,{"disambiguationData":[OSD([sQuery(id+"F39.wireOp",EDGE,"E29"),sQuery(id+"F39.wireOp",EDGE,"E30")])],"isStart":false});var subQ35=sQuery(id+"F3.wireOp",EDGE,"E20.7.0");var subQ39=makeQuery(id+"F14.opLoft","CAP_FACE",FACE,{"disambiguationData":[OSD([makeQuery(id+"F3.imprint","IMPRINT",FACE,{"disambiguationData":[TD([[makeQuery(id+"F3.imprint","IMPRINT",EDGE,{"derivedFrom":subQ35}),-1.0]])]})])],"isStart":true});var subQ75=sQuery(id+"F3.wireOp",EDGE,"E18.bottom");var subQ80=makeQuery(id+"F5.opLoft","CAP_FACE",FACE,{"disambiguationData":[OSD([makeQuery(id+"F3.imprint","IMPRINT",FACE,{"disambiguationData":[TD([[makeQuery(id+"F3.imprint","IMPRINT",EDGE,{"derivedFrom":subQ75}),1.0]])]})])],"isStart":true});Q19=makeQuery(id+"F44.opFillet","BLEND_EDGE",EDGE,{"blendedFrom":[makeQuery(id+"F40.boolean.opBoolean","INTERSECT",EDGE,{"derivedFrom":[subQ6,subQ13]}),makeQuery(id+"F40.boolean.opBoolean","SPLIT",FACE,{"disambiguationData":[TD([subQ0])],"derivedFrom":makeQuery(id+"F34.boolean.opBoolean","SPLIT",FACE,{"disambiguationData":[TD([subQ6])],"derivedFrom":makeQuery(id+"F33.boolean.opBoolean","SPLIT",FACE,{"disambiguationData":[TD([subQ39])],"derivedFrom":makeQuery(id+"F32.boolean.opBoolean","SPLIT",FACE,{"disambiguationData":[TD([subQ39])],"derivedFrom":makeQuery(id+"F31.boolean.opBoolean","SPLIT",FACE,{"disambiguationData":[TD([subQ39])],"derivedFrom":makeQuery(id+"F30.boolean.opBoolean","SPLIT",FACE,{"disambiguationData":[TD([subQ80])],"derivedFrom":makeQuery(id+"F29.boolean.opBoolean","SPLIT",FACE,{"disambiguationData":[TD([subQ80])],"derivedFrom":makeQuery(id+"F28.boolean.opBoolean","SPLIT",FACE,{"disambiguationData":[TD([subQ80])],"derivedFrom":makeQuery(id+"F27.boolean.opBoolean","SPLIT",FACE,{"disambiguationData":[TD([subQ80])],"derivedFrom":makeQuery(id+"F26.boolean.opBoolean","SPLIT",FACE,{"disambiguationData":[TD([subQ80])],"derivedFrom":makeQuery(id+"F25.boolean.opBoolean","SPLIT",FACE,{"disambiguationData":[TD([subQ80])],"derivedFrom":makeQuery(id+"F24.boolean.opBoolean","SPLIT",FACE,{"disambiguationData":[TD([subQ80])],"derivedFrom":makeQuery(id+"F1.opRevolve","SWEPT_FACE",FACE,{"disambiguationData":[OSD([sQuery(id+"F0.wireOp",EDGE,"E13")])]})})})})})})})})})})})})})],"blendedInto":[makeQuery(id+"F40.boolean.opBoolean","SPLIT",FACE,{"disambiguationData":[TD([subQ0])],"derivedFrom":makeQuery(id+"F34.boolean.opBoolean","SPLIT",FACE,{"disambiguationData":[TD([subQ6])],"derivedFrom":makeQuery(id+"F33.boolean.opBoolean","SPLIT",FACE,{"disambiguationData":[TD([subQ39])],"derivedFrom":makeQuery(id+"F32.boolean.opBoolean","SPLIT",FACE,{"disambiguationData":[TD([subQ39])],"derivedFrom":makeQuery(id+"F31.boolean.opBoolean","SPLIT",FACE,{"disambiguationData":[TD([subQ39])],"derivedFrom":makeQuery(id+"F30.boolean.opBoolean","SPLIT",FACE,{"disambiguationData":[TD([subQ80])],"derivedFrom":makeQuery(id+"F29.boolean.opBoolean","SPLIT",FACE,{"disambiguationData":[TD([subQ80])],"derivedFrom":makeQuery(id+"F28.boolean.opBoolean","SPLIT",FACE,{"disambiguationData":[TD([subQ80])],"derivedFrom":makeQuery(id+"F27.boolean.opBoolean","SPLIT",FACE,{"disambiguationData":[TD([subQ80])],"derivedFrom":makeQuery(id+"F26.boolean.opBoolean","SPLIT",FACE,{"disambiguationData":[TD([subQ80])],"derivedFrom":makeQuery(id+"F25.boolean.opBoolean","SPLIT",FACE,{"disambiguationData":[TD([subQ80])],"derivedFrom":makeQuery(id+"F24.boolean.opBoolean","SPLIT",FACE,{"disambiguationData":[TD([subQ80])],"derivedFrom":makeQuery(id+"F1.opRevolve","SWEPT_FACE",FACE,{"disambiguationData":[OSD([sQuery(id+"F0.wireOp",EDGE,"E13")])]})})})})})})})})})})})})})]});}
            var Q20;
            {var subQ0=makeQuery(id+"F1.opRevolve","SWEPT_FACE",FACE,{"disambiguationData":[OSD([sQuery(id+"F0.wireOp",EDGE,"E10")])]});var subQ7=sQuery(id+"F4.wireOp",EDGE,"E26.4.3");var subQ8=sQuery(id+"F4.wireOp",EDGE,"E26.4.2");var subQ9=sQuery(id+"F3.wireOp",EDGE,"E20.4.3");var subQ10=sQuery(id+"F3.wireOp",EDGE,"E20.4.2");var subQ11=sQuery(id+"F3.wireOp",EDGE,"E20.4.1");var subQ12=makeQuery(id+"F17.opLoft","SWEPT_FACE",FACE,{"disambiguationData":[OSD([subQ11,subQ10,subQ9,sQuery(id+"F4.wireOp",EDGE,"E26.4.1"),subQ8,subQ7])]});var subQ13=makeQuery(id+"F40.opExtrude","CAP_FACE",FACE,{"disambiguationData":[OSD([sQuery(id+"F39.wireOp",EDGE,"E29"),sQuery(id+"F39.wireOp",EDGE,"E30")])],"isStart":false});var subQ32=sQuery(id+"F3.wireOp",EDGE,"E20.7.0");var subQ36=makeQuery(id+"F14.opLoft","CAP_FACE",FACE,{"disambiguationData":[OSD([makeQuery(id+"F3.imprint","IMPRINT",FACE,{"disambiguationData":[TD([[makeQuery(id+"F3.imprint","IMPRINT",EDGE,{"derivedFrom":subQ32}),-1.0]])]})])],"isStart":true});var subQ75=sQuery(id+"F3.wireOp",EDGE,"E18.bottom");var subQ80=makeQuery(id+"F5.opLoft","CAP_FACE",FACE,{"disambiguationData":[OSD([makeQuery(id+"F3.imprint","IMPRINT",FACE,{"disambiguationData":[TD([[makeQuery(id+"F3.imprint","IMPRINT",EDGE,{"derivedFrom":subQ75}),1.0]])]})])],"isStart":true});Q20=makeQuery(id+"F44.opFillet","BLEND_EDGE",EDGE,{"blendedFrom":[makeQuery(id+"F40.boolean.opBoolean","INTERSECT",EDGE,{"derivedFrom":[subQ12,subQ13]}),makeQuery(id+"F40.boolean.opBoolean","SPLIT",FACE,{"disambiguationData":[TD([subQ0])],"derivedFrom":makeQuery(id+"F35.boolean.opBoolean","SPLIT",FACE,{"disambiguationData":[TD([subQ12])],"derivedFrom":makeQuery(id+"F34.boolean.opBoolean","SPLIT",FACE,{"disambiguationData":[TD([subQ36])],"derivedFrom":makeQuery(id+"F33.boolean.opBoolean","SPLIT",FACE,{"disambiguationData":[TD([subQ36])],"derivedFrom":makeQuery(id+"F32.boolean.opBoolean","SPLIT",FACE,{"disambiguationData":[TD([subQ36])],"derivedFrom":makeQuery(id+"F31.boolean.opBoolean","SPLIT",FACE,{"disambiguationData":[TD([subQ36])],"derivedFrom":makeQuery(id+"F30.boolean.opBoolean","SPLIT",FACE,{"disambiguationData":[TD([subQ80])],"derivedFrom":makeQuery(id+"F29.boolean.opBoolean","SPLIT",FACE,{"disambiguationData":[TD([subQ80])],"derivedFrom":makeQuery(id+"F28.boolean.opBoolean","SPLIT",FACE,{"disambiguationData":[TD([subQ80])],"derivedFrom":makeQuery(id+"F27.boolean.opBoolean","SPLIT",FACE,{"disambiguationData":[TD([subQ80])],"derivedFrom":makeQuery(id+"F26.boolean.opBoolean","SPLIT",FACE,{"disambiguationData":[TD([subQ80])],"derivedFrom":makeQuery(id+"F25.boolean.opBoolean","SPLIT",FACE,{"disambiguationData":[TD([subQ80])],"derivedFrom":makeQuery(id+"F24.boolean.opBoolean","SPLIT",FACE,{"disambiguationData":[TD([subQ80])],"derivedFrom":makeQuery(id+"F1.opRevolve","SWEPT_FACE",FACE,{"disambiguationData":[OSD([sQuery(id+"F0.wireOp",EDGE,"E13")])]})})})})})})})})})})})})})})],"blendedInto":[makeQuery(id+"F40.boolean.opBoolean","SPLIT",FACE,{"disambiguationData":[TD([subQ0])],"derivedFrom":makeQuery(id+"F35.boolean.opBoolean","SPLIT",FACE,{"disambiguationData":[TD([subQ12])],"derivedFrom":makeQuery(id+"F34.boolean.opBoolean","SPLIT",FACE,{"disambiguationData":[TD([subQ36])],"derivedFrom":makeQuery(id+"F33.boolean.opBoolean","SPLIT",FACE,{"disambiguationData":[TD([subQ36])],"derivedFrom":makeQuery(id+"F32.boolean.opBoolean","SPLIT",FACE,{"disambiguationData":[TD([subQ36])],"derivedFrom":makeQuery(id+"F31.boolean.opBoolean","SPLIT",FACE,{"disambiguationData":[TD([subQ36])],"derivedFrom":makeQuery(id+"F30.boolean.opBoolean","SPLIT",FACE,{"disambiguationData":[TD([subQ80])],"derivedFrom":makeQuery(id+"F29.boolean.opBoolean","SPLIT",FACE,{"disambiguationData":[TD([subQ80])],"derivedFrom":makeQuery(id+"F28.boolean.opBoolean","SPLIT",FACE,{"disambiguationData":[TD([subQ80])],"derivedFrom":makeQuery(id+"F27.boolean.opBoolean","SPLIT",FACE,{"disambiguationData":[TD([subQ80])],"derivedFrom":makeQuery(id+"F26.boolean.opBoolean","SPLIT",FACE,{"disambiguationData":[TD([subQ80])],"derivedFrom":makeQuery(id+"F25.boolean.opBoolean","SPLIT",FACE,{"disambiguationData":[TD([subQ80])],"derivedFrom":makeQuery(id+"F24.boolean.opBoolean","SPLIT",FACE,{"disambiguationData":[TD([subQ80])],"derivedFrom":makeQuery(id+"F1.opRevolve","SWEPT_FACE",FACE,{"disambiguationData":[OSD([sQuery(id+"F0.wireOp",EDGE,"E13")])]})})})})})})})})})})})})})})]});}
            var Q21;
            {var subQ0=makeQuery(id+"F1.opRevolve","SWEPT_FACE",FACE,{"disambiguationData":[OSD([sQuery(id+"F0.wireOp",EDGE,"E10")])]});var subQ7=sQuery(id+"F4.wireOp",EDGE,"E26.5.3");var subQ8=sQuery(id+"F4.wireOp",EDGE,"E26.5.2");var subQ9=sQuery(id+"F3.wireOp",EDGE,"E20.5.3");var subQ10=sQuery(id+"F3.wireOp",EDGE,"E20.5.2");var subQ11=sQuery(id+"F3.wireOp",EDGE,"E20.5.1");var subQ12=makeQuery(id+"F16.opLoft","SWEPT_FACE",FACE,{"disambiguationData":[OSD([subQ11,subQ10,subQ9,sQuery(id+"F4.wireOp",EDGE,"E26.5.1"),subQ8,subQ7])]});var subQ13=makeQuery(id+"F40.opExtrude","CAP_FACE",FACE,{"disambiguationData":[OSD([sQuery(id+"F39.wireOp",EDGE,"E29"),sQuery(id+"F39.wireOp",EDGE,"E30")])],"isStart":false});var subQ26=sQuery(id+"F3.wireOp",EDGE,"E20.7.0");var subQ30=makeQuery(id+"F14.opLoft","CAP_FACE",FACE,{"disambiguationData":[OSD([makeQuery(id+"F3.imprint","IMPRINT",FACE,{"disambiguationData":[TD([[makeQuery(id+"F3.imprint","IMPRINT",EDGE,{"derivedFrom":subQ26}),-1.0]])]})])],"isStart":true});var subQ75=sQuery(id+"F3.wireOp",EDGE,"E18.bottom");var subQ80=makeQuery(id+"F5.opLoft","CAP_FACE",FACE,{"disambiguationData":[OSD([makeQuery(id+"F3.imprint","IMPRINT",FACE,{"disambiguationData":[TD([[makeQuery(id+"F3.imprint","IMPRINT",EDGE,{"derivedFrom":subQ75}),1.0]])]})])],"isStart":true});Q21=makeQuery(id+"F44.opFillet","BLEND_EDGE",EDGE,{"blendedFrom":[makeQuery(id+"F40.boolean.opBoolean","INTERSECT",EDGE,{"derivedFrom":[subQ12,subQ13]}),makeQuery(id+"F40.boolean.opBoolean","SPLIT",FACE,{"disambiguationData":[TD([subQ0])],"derivedFrom":makeQuery(id+"F36.boolean.opBoolean","SPLIT",FACE,{"disambiguationData":[TD([subQ12])],"derivedFrom":makeQuery(id+"F35.boolean.opBoolean","SPLIT",FACE,{"disambiguationData":[TD([subQ30])],"derivedFrom":makeQuery(id+"F34.boolean.opBoolean","SPLIT",FACE,{"disambiguationData":[TD([subQ30])],"derivedFrom":makeQuery(id+"F33.boolean.opBoolean","SPLIT",FACE,{"disambiguationData":[TD([subQ30])],"derivedFrom":makeQuery(id+"F32.boolean.opBoolean","SPLIT",FACE,{"disambiguationData":[TD([subQ30])],"derivedFrom":makeQuery(id+"F31.boolean.opBoolean","SPLIT",FACE,{"disambiguationData":[TD([subQ30])],"derivedFrom":makeQuery(id+"F30.boolean.opBoolean","SPLIT",FACE,{"disambiguationData":[TD([subQ80])],"derivedFrom":makeQuery(id+"F29.boolean.opBoolean","SPLIT",FACE,{"disambiguationData":[TD([subQ80])],"derivedFrom":makeQuery(id+"F28.boolean.opBoolean","SPLIT",FACE,{"disambiguationData":[TD([subQ80])],"derivedFrom":makeQuery(id+"F27.boolean.opBoolean","SPLIT",FACE,{"disambiguationData":[TD([subQ80])],"derivedFrom":makeQuery(id+"F26.boolean.opBoolean","SPLIT",FACE,{"disambiguationData":[TD([subQ80])],"derivedFrom":makeQuery(id+"F25.boolean.opBoolean","SPLIT",FACE,{"disambiguationData":[TD([subQ80])],"derivedFrom":makeQuery(id+"F24.boolean.opBoolean","SPLIT",FACE,{"disambiguationData":[TD([subQ80])],"derivedFrom":makeQuery(id+"F1.opRevolve","SWEPT_FACE",FACE,{"disambiguationData":[OSD([sQuery(id+"F0.wireOp",EDGE,"E13")])]})})})})})})})})})})})})})})})],"blendedInto":[makeQuery(id+"F40.boolean.opBoolean","SPLIT",FACE,{"disambiguationData":[TD([subQ0])],"derivedFrom":makeQuery(id+"F36.boolean.opBoolean","SPLIT",FACE,{"disambiguationData":[TD([subQ12])],"derivedFrom":makeQuery(id+"F35.boolean.opBoolean","SPLIT",FACE,{"disambiguationData":[TD([subQ30])],"derivedFrom":makeQuery(id+"F34.boolean.opBoolean","SPLIT",FACE,{"disambiguationData":[TD([subQ30])],"derivedFrom":makeQuery(id+"F33.boolean.opBoolean","SPLIT",FACE,{"disambiguationData":[TD([subQ30])],"derivedFrom":makeQuery(id+"F32.boolean.opBoolean","SPLIT",FACE,{"disambiguationData":[TD([subQ30])],"derivedFrom":makeQuery(id+"F31.boolean.opBoolean","SPLIT",FACE,{"disambiguationData":[TD([subQ30])],"derivedFrom":makeQuery(id+"F30.boolean.opBoolean","SPLIT",FACE,{"disambiguationData":[TD([subQ80])],"derivedFrom":makeQuery(id+"F29.boolean.opBoolean","SPLIT",FACE,{"disambiguationData":[TD([subQ80])],"derivedFrom":makeQuery(id+"F28.boolean.opBoolean","SPLIT",FACE,{"disambiguationData":[TD([subQ80])],"derivedFrom":makeQuery(id+"F27.boolean.opBoolean","SPLIT",FACE,{"disambiguationData":[TD([subQ80])],"derivedFrom":makeQuery(id+"F26.boolean.opBoolean","SPLIT",FACE,{"disambiguationData":[TD([subQ80])],"derivedFrom":makeQuery(id+"F25.boolean.opBoolean","SPLIT",FACE,{"disambiguationData":[TD([subQ80])],"derivedFrom":makeQuery(id+"F24.boolean.opBoolean","SPLIT",FACE,{"disambiguationData":[TD([subQ80])],"derivedFrom":makeQuery(id+"F1.opRevolve","SWEPT_FACE",FACE,{"disambiguationData":[OSD([sQuery(id+"F0.wireOp",EDGE,"E13")])]})})})})})})})})})})})})})})})]});}
            var Q22;
            {var subQ0=makeQuery(id+"F1.opRevolve","SWEPT_FACE",FACE,{"disambiguationData":[OSD([sQuery(id+"F0.wireOp",EDGE,"E10")])]});var subQ1=sQuery(id+"F4.wireOp",EDGE,"E26.6.3");var subQ2=sQuery(id+"F4.wireOp",EDGE,"E26.6.2");var subQ3=sQuery(id+"F3.wireOp",EDGE,"E20.6.3");var subQ4=sQuery(id+"F3.wireOp",EDGE,"E20.6.2");var subQ5=sQuery(id+"F3.wireOp",EDGE,"E20.6.1");var subQ6=makeQuery(id+"F15.opLoft","SWEPT_FACE",FACE,{"disambiguationData":[OSD([subQ5,subQ4,subQ3,sQuery(id+"F4.wireOp",EDGE,"E26.6.1"),subQ2,subQ1])]});var subQ13=makeQuery(id+"F40.opExtrude","CAP_FACE",FACE,{"disambiguationData":[OSD([sQuery(id+"F39.wireOp",EDGE,"E29"),sQuery(id+"F39.wireOp",EDGE,"E30")])],"isStart":false});var subQ19=sQuery(id+"F3.wireOp",EDGE,"E20.7.0");var subQ23=makeQuery(id+"F14.opLoft","CAP_FACE",FACE,{"disambiguationData":[OSD([makeQuery(id+"F3.imprint","IMPRINT",FACE,{"disambiguationData":[TD([[makeQuery(id+"F3.imprint","IMPRINT",EDGE,{"derivedFrom":subQ19}),-1.0]])]})])],"isStart":true});var subQ75=sQuery(id+"F3.wireOp",EDGE,"E18.bottom");var subQ80=makeQuery(id+"F5.opLoft","CAP_FACE",FACE,{"disambiguationData":[OSD([makeQuery(id+"F3.imprint","IMPRINT",FACE,{"disambiguationData":[TD([[makeQuery(id+"F3.imprint","IMPRINT",EDGE,{"derivedFrom":subQ75}),1.0]])]})])],"isStart":true});Q22=makeQuery(id+"F44.opFillet","BLEND_EDGE",EDGE,{"blendedFrom":[makeQuery(id+"F40.boolean.opBoolean","INTERSECT",EDGE,{"derivedFrom":[subQ6,subQ13]}),makeQuery(id+"F40.boolean.opBoolean","SPLIT",FACE,{"disambiguationData":[TD([subQ0])],"derivedFrom":makeQuery(id+"F37.boolean.opBoolean","SPLIT",FACE,{"disambiguationData":[TD([subQ6])],"derivedFrom":makeQuery(id+"F36.boolean.opBoolean","SPLIT",FACE,{"disambiguationData":[TD([subQ23])],"derivedFrom":makeQuery(id+"F35.boolean.opBoolean","SPLIT",FACE,{"disambiguationData":[TD([subQ23])],"derivedFrom":makeQuery(id+"F34.boolean.opBoolean","SPLIT",FACE,{"disambiguationData":[TD([subQ23])],"derivedFrom":makeQuery(id+"F33.boolean.opBoolean","SPLIT",FACE,{"disambiguationData":[TD([subQ23])],"derivedFrom":makeQuery(id+"F32.boolean.opBoolean","SPLIT",FACE,{"disambiguationData":[TD([subQ23])],"derivedFrom":makeQuery(id+"F31.boolean.opBoolean","SPLIT",FACE,{"disambiguationData":[TD([subQ23])],"derivedFrom":makeQuery(id+"F30.boolean.opBoolean","SPLIT",FACE,{"disambiguationData":[TD([subQ80])],"derivedFrom":makeQuery(id+"F29.boolean.opBoolean","SPLIT",FACE,{"disambiguationData":[TD([subQ80])],"derivedFrom":makeQuery(id+"F28.boolean.opBoolean","SPLIT",FACE,{"disambiguationData":[TD([subQ80])],"derivedFrom":makeQuery(id+"F27.boolean.opBoolean","SPLIT",FACE,{"disambiguationData":[TD([subQ80])],"derivedFrom":makeQuery(id+"F26.boolean.opBoolean","SPLIT",FACE,{"disambiguationData":[TD([subQ80])],"derivedFrom":makeQuery(id+"F25.boolean.opBoolean","SPLIT",FACE,{"disambiguationData":[TD([subQ80])],"derivedFrom":makeQuery(id+"F24.boolean.opBoolean","SPLIT",FACE,{"disambiguationData":[TD([subQ80])],"derivedFrom":makeQuery(id+"F1.opRevolve","SWEPT_FACE",FACE,{"disambiguationData":[OSD([sQuery(id+"F0.wireOp",EDGE,"E13")])]})})})})})})})})})})})})})})})})],"blendedInto":[makeQuery(id+"F40.boolean.opBoolean","SPLIT",FACE,{"disambiguationData":[TD([subQ0])],"derivedFrom":makeQuery(id+"F37.boolean.opBoolean","SPLIT",FACE,{"disambiguationData":[TD([subQ6])],"derivedFrom":makeQuery(id+"F36.boolean.opBoolean","SPLIT",FACE,{"disambiguationData":[TD([subQ23])],"derivedFrom":makeQuery(id+"F35.boolean.opBoolean","SPLIT",FACE,{"disambiguationData":[TD([subQ23])],"derivedFrom":makeQuery(id+"F34.boolean.opBoolean","SPLIT",FACE,{"disambiguationData":[TD([subQ23])],"derivedFrom":makeQuery(id+"F33.boolean.opBoolean","SPLIT",FACE,{"disambiguationData":[TD([subQ23])],"derivedFrom":makeQuery(id+"F32.boolean.opBoolean","SPLIT",FACE,{"disambiguationData":[TD([subQ23])],"derivedFrom":makeQuery(id+"F31.boolean.opBoolean","SPLIT",FACE,{"disambiguationData":[TD([subQ23])],"derivedFrom":makeQuery(id+"F30.boolean.opBoolean","SPLIT",FACE,{"disambiguationData":[TD([subQ80])],"derivedFrom":makeQuery(id+"F29.boolean.opBoolean","SPLIT",FACE,{"disambiguationData":[TD([subQ80])],"derivedFrom":makeQuery(id+"F28.boolean.opBoolean","SPLIT",FACE,{"disambiguationData":[TD([subQ80])],"derivedFrom":makeQuery(id+"F27.boolean.opBoolean","SPLIT",FACE,{"disambiguationData":[TD([subQ80])],"derivedFrom":makeQuery(id+"F26.boolean.opBoolean","SPLIT",FACE,{"disambiguationData":[TD([subQ80])],"derivedFrom":makeQuery(id+"F25.boolean.opBoolean","SPLIT",FACE,{"disambiguationData":[TD([subQ80])],"derivedFrom":makeQuery(id+"F24.boolean.opBoolean","SPLIT",FACE,{"disambiguationData":[TD([subQ80])],"derivedFrom":makeQuery(id+"F1.opRevolve","SWEPT_FACE",FACE,{"disambiguationData":[OSD([sQuery(id+"F0.wireOp",EDGE,"E13")])]})})})})})})})})})})})})})})})})]});}
            var Q23;
            {var subQ0=makeQuery(id+"F1.opRevolve","SWEPT_FACE",FACE,{"disambiguationData":[OSD([sQuery(id+"F0.wireOp",EDGE,"E10")])]});var subQ1=sQuery(id+"F4.wireOp",EDGE,"E26.7.3");var subQ2=sQuery(id+"F4.wireOp",EDGE,"E26.7.2");var subQ3=sQuery(id+"F3.wireOp",EDGE,"E20.7.3");var subQ4=sQuery(id+"F3.wireOp",EDGE,"E20.7.2");var subQ5=sQuery(id+"F3.wireOp",EDGE,"E20.7.1");var subQ6=makeQuery(id+"F14.opLoft","SWEPT_FACE",FACE,{"disambiguationData":[OSD([subQ5,subQ4,subQ3,sQuery(id+"F4.wireOp",EDGE,"E26.7.1"),subQ2,subQ1])]});var subQ13=makeQuery(id+"F40.opExtrude","CAP_FACE",FACE,{"disambiguationData":[OSD([sQuery(id+"F39.wireOp",EDGE,"E29"),sQuery(id+"F39.wireOp",EDGE,"E30")])],"isStart":false});var subQ20=sQuery(id+"F3.wireOp",EDGE,"E20.7.0");var subQ22=makeQuery(id+"F14.opLoft","CAP_FACE",FACE,{"disambiguationData":[OSD([makeQuery(id+"F3.imprint","IMPRINT",FACE,{"disambiguationData":[TD([[makeQuery(id+"F3.imprint","IMPRINT",EDGE,{"derivedFrom":subQ20}),-1.0]])]})])],"isStart":true});var subQ75=sQuery(id+"F3.wireOp",EDGE,"E18.bottom");var subQ80=makeQuery(id+"F5.opLoft","CAP_FACE",FACE,{"disambiguationData":[OSD([makeQuery(id+"F3.imprint","IMPRINT",FACE,{"disambiguationData":[TD([[makeQuery(id+"F3.imprint","IMPRINT",EDGE,{"derivedFrom":subQ75}),1.0]])]})])],"isStart":true});Q23=makeQuery(id+"F44.opFillet","BLEND_EDGE",EDGE,{"blendedFrom":[makeQuery(id+"F40.boolean.opBoolean","INTERSECT",EDGE,{"derivedFrom":[subQ6,subQ13]}),makeQuery(id+"F40.boolean.opBoolean","SPLIT",FACE,{"disambiguationData":[TD([subQ0])],"derivedFrom":makeQuery(id+"F38.boolean.opBoolean","SPLIT",FACE,{"disambiguationData":[TD([subQ6])],"derivedFrom":makeQuery(id+"F37.boolean.opBoolean","SPLIT",FACE,{"disambiguationData":[TD([subQ22])],"derivedFrom":makeQuery(id+"F36.boolean.opBoolean","SPLIT",FACE,{"disambiguationData":[TD([subQ22])],"derivedFrom":makeQuery(id+"F35.boolean.opBoolean","SPLIT",FACE,{"disambiguationData":[TD([subQ22])],"derivedFrom":makeQuery(id+"F34.boolean.opBoolean","SPLIT",FACE,{"disambiguationData":[TD([subQ22])],"derivedFrom":makeQuery(id+"F33.boolean.opBoolean","SPLIT",FACE,{"disambiguationData":[TD([subQ22])],"derivedFrom":makeQuery(id+"F32.boolean.opBoolean","SPLIT",FACE,{"disambiguationData":[TD([subQ22])],"derivedFrom":makeQuery(id+"F31.boolean.opBoolean","SPLIT",FACE,{"disambiguationData":[TD([subQ22])],"derivedFrom":makeQuery(id+"F30.boolean.opBoolean","SPLIT",FACE,{"disambiguationData":[TD([subQ80])],"derivedFrom":makeQuery(id+"F29.boolean.opBoolean","SPLIT",FACE,{"disambiguationData":[TD([subQ80])],"derivedFrom":makeQuery(id+"F28.boolean.opBoolean","SPLIT",FACE,{"disambiguationData":[TD([subQ80])],"derivedFrom":makeQuery(id+"F27.boolean.opBoolean","SPLIT",FACE,{"disambiguationData":[TD([subQ80])],"derivedFrom":makeQuery(id+"F26.boolean.opBoolean","SPLIT",FACE,{"disambiguationData":[TD([subQ80])],"derivedFrom":makeQuery(id+"F25.boolean.opBoolean","SPLIT",FACE,{"disambiguationData":[TD([subQ80])],"derivedFrom":makeQuery(id+"F24.boolean.opBoolean","SPLIT",FACE,{"disambiguationData":[TD([subQ80])],"derivedFrom":makeQuery(id+"F1.opRevolve","SWEPT_FACE",FACE,{"disambiguationData":[OSD([sQuery(id+"F0.wireOp",EDGE,"E13")])]})})})})})})})})})})})})})})})})})],"blendedInto":[makeQuery(id+"F40.boolean.opBoolean","SPLIT",FACE,{"disambiguationData":[TD([subQ0])],"derivedFrom":makeQuery(id+"F38.boolean.opBoolean","SPLIT",FACE,{"disambiguationData":[TD([subQ6])],"derivedFrom":makeQuery(id+"F37.boolean.opBoolean","SPLIT",FACE,{"disambiguationData":[TD([subQ22])],"derivedFrom":makeQuery(id+"F36.boolean.opBoolean","SPLIT",FACE,{"disambiguationData":[TD([subQ22])],"derivedFrom":makeQuery(id+"F35.boolean.opBoolean","SPLIT",FACE,{"disambiguationData":[TD([subQ22])],"derivedFrom":makeQuery(id+"F34.boolean.opBoolean","SPLIT",FACE,{"disambiguationData":[TD([subQ22])],"derivedFrom":makeQuery(id+"F33.boolean.opBoolean","SPLIT",FACE,{"disambiguationData":[TD([subQ22])],"derivedFrom":makeQuery(id+"F32.boolean.opBoolean","SPLIT",FACE,{"disambiguationData":[TD([subQ22])],"derivedFrom":makeQuery(id+"F31.boolean.opBoolean","SPLIT",FACE,{"disambiguationData":[TD([subQ22])],"derivedFrom":makeQuery(id+"F30.boolean.opBoolean","SPLIT",FACE,{"disambiguationData":[TD([subQ80])],"derivedFrom":makeQuery(id+"F29.boolean.opBoolean","SPLIT",FACE,{"disambiguationData":[TD([subQ80])],"derivedFrom":makeQuery(id+"F28.boolean.opBoolean","SPLIT",FACE,{"disambiguationData":[TD([subQ80])],"derivedFrom":makeQuery(id+"F27.boolean.opBoolean","SPLIT",FACE,{"disambiguationData":[TD([subQ80])],"derivedFrom":makeQuery(id+"F26.boolean.opBoolean","SPLIT",FACE,{"disambiguationData":[TD([subQ80])],"derivedFrom":makeQuery(id+"F25.boolean.opBoolean","SPLIT",FACE,{"disambiguationData":[TD([subQ80])],"derivedFrom":makeQuery(id+"F24.boolean.opBoolean","SPLIT",FACE,{"disambiguationData":[TD([subQ80])],"derivedFrom":makeQuery(id+"F1.opRevolve","SWEPT_FACE",FACE,{"disambiguationData":[OSD([sQuery(id+"F0.wireOp",EDGE,"E13")])]})})})})})})})})})})})})})})})})})]});}
            var Q24;
            {var subQ0=makeQuery(id+"F1.opRevolve","SWEPT_FACE",FACE,{"disambiguationData":[OSD([sQuery(id+"F0.wireOp",EDGE,"E10")])]});var subQ1=sQuery(id+"F3.wireOp",EDGE,"E20.8.3");var subQ2=sQuery(id+"F3.wireOp",EDGE,"E20.8.2");var subQ3=sQuery(id+"F3.wireOp",EDGE,"E20.8.1");var subQ4=makeQuery(id+"F13.opLoft","SWEPT_FACE",FACE,{"disambiguationData":[OSD([subQ3,subQ2,subQ1,sQuery(id+"F4.wireOp",EDGE,"E26.8.1"),sQuery(id+"F4.wireOp",EDGE,"E26.8.2"),sQuery(id+"F4.wireOp",EDGE,"E26.8.3")])]});var subQ5=makeQuery(id+"F40.opExtrude","CAP_FACE",FACE,{"disambiguationData":[OSD([sQuery(id+"F39.wireOp",EDGE,"E29"),sQuery(id+"F39.wireOp",EDGE,"E30")])],"isStart":false});var subQ10=sQuery(id+"F3.wireOp",EDGE,"E20.7.0");var subQ16=makeQuery(id+"F14.opLoft","CAP_FACE",FACE,{"disambiguationData":[OSD([makeQuery(id+"F3.imprint","IMPRINT",FACE,{"disambiguationData":[TD([[makeQuery(id+"F3.imprint","IMPRINT",EDGE,{"derivedFrom":subQ10}),-1.0]])]})])],"isStart":true});var subQ74=sQuery(id+"F3.wireOp",EDGE,"E18.bottom");var subQ79=makeQuery(id+"F5.opLoft","CAP_FACE",FACE,{"disambiguationData":[OSD([makeQuery(id+"F3.imprint","IMPRINT",FACE,{"disambiguationData":[TD([[makeQuery(id+"F3.imprint","IMPRINT",EDGE,{"derivedFrom":subQ74}),1.0]])]})])],"isStart":true});Q24=makeQuery(id+"F44.opFillet","BLEND_EDGE",EDGE,{"blendedFrom":[makeQuery(id+"F40.boolean.opBoolean","INTERSECT",EDGE,{"derivedFrom":[subQ4,subQ5]}),makeQuery(id+"F40.boolean.opBoolean","SPLIT",FACE,{"disambiguationData":[TD([subQ0])],"derivedFrom":makeQuery(id+"F38.boolean.opBoolean","SPLIT",FACE,{"disambiguationData":[TD([subQ4])],"derivedFrom":makeQuery(id+"F37.boolean.opBoolean","SPLIT",FACE,{"disambiguationData":[TD([subQ16])],"derivedFrom":makeQuery(id+"F36.boolean.opBoolean","SPLIT",FACE,{"disambiguationData":[TD([subQ16])],"derivedFrom":makeQuery(id+"F35.boolean.opBoolean","SPLIT",FACE,{"disambiguationData":[TD([subQ16])],"derivedFrom":makeQuery(id+"F34.boolean.opBoolean","SPLIT",FACE,{"disambiguationData":[TD([subQ16])],"derivedFrom":makeQuery(id+"F33.boolean.opBoolean","SPLIT",FACE,{"disambiguationData":[TD([subQ16])],"derivedFrom":makeQuery(id+"F32.boolean.opBoolean","SPLIT",FACE,{"disambiguationData":[TD([subQ16])],"derivedFrom":makeQuery(id+"F31.boolean.opBoolean","SPLIT",FACE,{"disambiguationData":[TD([subQ16])],"derivedFrom":makeQuery(id+"F30.boolean.opBoolean","SPLIT",FACE,{"disambiguationData":[TD([subQ79])],"derivedFrom":makeQuery(id+"F29.boolean.opBoolean","SPLIT",FACE,{"disambiguationData":[TD([subQ79])],"derivedFrom":makeQuery(id+"F28.boolean.opBoolean","SPLIT",FACE,{"disambiguationData":[TD([subQ79])],"derivedFrom":makeQuery(id+"F27.boolean.opBoolean","SPLIT",FACE,{"disambiguationData":[TD([subQ79])],"derivedFrom":makeQuery(id+"F26.boolean.opBoolean","SPLIT",FACE,{"disambiguationData":[TD([subQ79])],"derivedFrom":makeQuery(id+"F25.boolean.opBoolean","SPLIT",FACE,{"disambiguationData":[TD([subQ79])],"derivedFrom":makeQuery(id+"F24.boolean.opBoolean","SPLIT",FACE,{"disambiguationData":[TD([subQ79])],"derivedFrom":makeQuery(id+"F1.opRevolve","SWEPT_FACE",FACE,{"disambiguationData":[OSD([sQuery(id+"F0.wireOp",EDGE,"E13")])]})})})})})})})})})})})})})})})})})],"blendedInto":[makeQuery(id+"F40.boolean.opBoolean","SPLIT",FACE,{"disambiguationData":[TD([subQ0])],"derivedFrom":makeQuery(id+"F38.boolean.opBoolean","SPLIT",FACE,{"disambiguationData":[TD([subQ4])],"derivedFrom":makeQuery(id+"F37.boolean.opBoolean","SPLIT",FACE,{"disambiguationData":[TD([subQ16])],"derivedFrom":makeQuery(id+"F36.boolean.opBoolean","SPLIT",FACE,{"disambiguationData":[TD([subQ16])],"derivedFrom":makeQuery(id+"F35.boolean.opBoolean","SPLIT",FACE,{"disambiguationData":[TD([subQ16])],"derivedFrom":makeQuery(id+"F34.boolean.opBoolean","SPLIT",FACE,{"disambiguationData":[TD([subQ16])],"derivedFrom":makeQuery(id+"F33.boolean.opBoolean","SPLIT",FACE,{"disambiguationData":[TD([subQ16])],"derivedFrom":makeQuery(id+"F32.boolean.opBoolean","SPLIT",FACE,{"disambiguationData":[TD([subQ16])],"derivedFrom":makeQuery(id+"F31.boolean.opBoolean","SPLIT",FACE,{"disambiguationData":[TD([subQ16])],"derivedFrom":makeQuery(id+"F30.boolean.opBoolean","SPLIT",FACE,{"disambiguationData":[TD([subQ79])],"derivedFrom":makeQuery(id+"F29.boolean.opBoolean","SPLIT",FACE,{"disambiguationData":[TD([subQ79])],"derivedFrom":makeQuery(id+"F28.boolean.opBoolean","SPLIT",FACE,{"disambiguationData":[TD([subQ79])],"derivedFrom":makeQuery(id+"F27.boolean.opBoolean","SPLIT",FACE,{"disambiguationData":[TD([subQ79])],"derivedFrom":makeQuery(id+"F26.boolean.opBoolean","SPLIT",FACE,{"disambiguationData":[TD([subQ79])],"derivedFrom":makeQuery(id+"F25.boolean.opBoolean","SPLIT",FACE,{"disambiguationData":[TD([subQ79])],"derivedFrom":makeQuery(id+"F24.boolean.opBoolean","SPLIT",FACE,{"disambiguationData":[TD([subQ79])],"derivedFrom":makeQuery(id+"F1.opRevolve","SWEPT_FACE",FACE,{"disambiguationData":[OSD([sQuery(id+"F0.wireOp",EDGE,"E13")])]})})})})})})})})})})})})})})})})})]});}
            var Q25;
            {var subQ0=makeQuery(id+"F1.opRevolve","SWEPT_FACE",FACE,{"disambiguationData":[OSD([sQuery(id+"F0.wireOp",EDGE,"E10")])]});var subQ1=sQuery(id+"F3.wireOp",EDGE,"E20.9.3");var subQ2=sQuery(id+"F3.wireOp",EDGE,"E20.9.2");var subQ3=sQuery(id+"F3.wireOp",EDGE,"E20.9.1");var subQ4=makeQuery(id+"F12.opLoft","SWEPT_FACE",FACE,{"disambiguationData":[OSD([subQ3,subQ2,subQ1,sQuery(id+"F4.wireOp",EDGE,"E26.9.1"),sQuery(id+"F4.wireOp",EDGE,"E26.9.2"),sQuery(id+"F4.wireOp",EDGE,"E26.9.3")])]});var subQ9=makeQuery(id+"F40.opExtrude","CAP_FACE",FACE,{"disambiguationData":[OSD([sQuery(id+"F39.wireOp",EDGE,"E29"),sQuery(id+"F39.wireOp",EDGE,"E30")])],"isStart":false});Q25=makeQuery(id+"F44.opFillet","BLEND_EDGE",EDGE,{"blendedFrom":[makeQuery(id+"F40.boolean.opBoolean","INTERSECT",EDGE,{"derivedFrom":[subQ4,subQ9]}),makeQuery(id+"F40.boolean.opBoolean","SPLIT",FACE,{"disambiguationData":[TD([subQ0])],"derivedFrom":makeQuery(id+"F24.boolean.opBoolean","SPLIT",FACE,{"disambiguationData":[TD([subQ4])],"derivedFrom":makeQuery(id+"F1.opRevolve","SWEPT_FACE",FACE,{"disambiguationData":[OSD([sQuery(id+"F0.wireOp",EDGE,"E13")])]})})})],"blendedInto":[makeQuery(id+"F40.boolean.opBoolean","SPLIT",FACE,{"disambiguationData":[TD([subQ0])],"derivedFrom":makeQuery(id+"F24.boolean.opBoolean","SPLIT",FACE,{"disambiguationData":[TD([subQ4])],"derivedFrom":makeQuery(id+"F1.opRevolve","SWEPT_FACE",FACE,{"disambiguationData":[OSD([sQuery(id+"F0.wireOp",EDGE,"E13")])]})})})]});}
            var Q26;
            {var subQ0=makeQuery(id+"F1.opRevolve","SWEPT_FACE",FACE,{"disambiguationData":[OSD([sQuery(id+"F0.wireOp",EDGE,"E10")])]});var subQ1=sQuery(id+"F4.wireOp",EDGE,"E26.10.3");var subQ2=sQuery(id+"F4.wireOp",EDGE,"E26.10.2");var subQ3=sQuery(id+"F3.wireOp",EDGE,"E20.10.3");var subQ4=sQuery(id+"F3.wireOp",EDGE,"E20.10.2");var subQ5=sQuery(id+"F3.wireOp",EDGE,"E20.10.1");var subQ6=makeQuery(id+"F11.opLoft","SWEPT_FACE",FACE,{"disambiguationData":[OSD([subQ5,subQ4,subQ3,sQuery(id+"F4.wireOp",EDGE,"E26.10.1"),subQ2,subQ1])]});var subQ11=makeQuery(id+"F40.opExtrude","CAP_FACE",FACE,{"disambiguationData":[OSD([sQuery(id+"F39.wireOp",EDGE,"E29"),sQuery(id+"F39.wireOp",EDGE,"E30")])],"isStart":false});var subQ89=sQuery(id+"F3.wireOp",EDGE,"E18.bottom");Q26=makeQuery(id+"F44.opFillet","BLEND_EDGE",EDGE,{"blendedFrom":[makeQuery(id+"F40.boolean.opBoolean","INTERSECT",EDGE,{"derivedFrom":[subQ6,subQ11]}),makeQuery(id+"F40.boolean.opBoolean","SPLIT",FACE,{"disambiguationData":[TD([subQ0])],"derivedFrom":makeQuery(id+"F25.boolean.opBoolean","SPLIT",FACE,{"disambiguationData":[TD([subQ6])],"derivedFrom":makeQuery(id+"F24.boolean.opBoolean","SPLIT",FACE,{"disambiguationData":[TD([makeQuery(id+"F5.opLoft","CAP_FACE",FACE,{"disambiguationData":[OSD([makeQuery(id+"F3.imprint","IMPRINT",FACE,{"disambiguationData":[TD([[makeQuery(id+"F3.imprint","IMPRINT",EDGE,{"derivedFrom":subQ89}),1.0]])]})])],"isStart":true})])],"derivedFrom":makeQuery(id+"F1.opRevolve","SWEPT_FACE",FACE,{"disambiguationData":[OSD([sQuery(id+"F0.wireOp",EDGE,"E13")])]})})})})],"blendedInto":[makeQuery(id+"F40.boolean.opBoolean","SPLIT",FACE,{"disambiguationData":[TD([subQ0])],"derivedFrom":makeQuery(id+"F25.boolean.opBoolean","SPLIT",FACE,{"disambiguationData":[TD([subQ6])],"derivedFrom":makeQuery(id+"F24.boolean.opBoolean","SPLIT",FACE,{"disambiguationData":[TD([makeQuery(id+"F5.opLoft","CAP_FACE",FACE,{"disambiguationData":[OSD([makeQuery(id+"F3.imprint","IMPRINT",FACE,{"disambiguationData":[TD([[makeQuery(id+"F3.imprint","IMPRINT",EDGE,{"derivedFrom":subQ89}),1.0]])]})])],"isStart":true})])],"derivedFrom":makeQuery(id+"F1.opRevolve","SWEPT_FACE",FACE,{"disambiguationData":[OSD([sQuery(id+"F0.wireOp",EDGE,"E13")])]})})})})]});}
            var Q27;
            {var subQ0=makeQuery(id+"F1.opRevolve","SWEPT_FACE",FACE,{"disambiguationData":[OSD([sQuery(id+"F0.wireOp",EDGE,"E10")])]});var subQ1=sQuery(id+"F4.wireOp",EDGE,"E26.11.3");var subQ2=sQuery(id+"F4.wireOp",EDGE,"E26.11.2");var subQ3=sQuery(id+"F3.wireOp",EDGE,"E20.11.3");var subQ4=sQuery(id+"F3.wireOp",EDGE,"E20.11.2");var subQ5=sQuery(id+"F3.wireOp",EDGE,"E20.11.1");var subQ6=makeQuery(id+"F10.opLoft","SWEPT_FACE",FACE,{"disambiguationData":[OSD([subQ5,subQ4,subQ3,sQuery(id+"F4.wireOp",EDGE,"E26.11.1"),subQ2,subQ1])]});var subQ13=makeQuery(id+"F40.opExtrude","CAP_FACE",FACE,{"disambiguationData":[OSD([sQuery(id+"F39.wireOp",EDGE,"E29"),sQuery(id+"F39.wireOp",EDGE,"E30")])],"isStart":false});var subQ79=sQuery(id+"F3.wireOp",EDGE,"E18.bottom");var subQ82=makeQuery(id+"F5.opLoft","CAP_FACE",FACE,{"disambiguationData":[OSD([makeQuery(id+"F3.imprint","IMPRINT",FACE,{"disambiguationData":[TD([[makeQuery(id+"F3.imprint","IMPRINT",EDGE,{"derivedFrom":subQ79}),1.0]])]})])],"isStart":true});Q27=makeQuery(id+"F44.opFillet","BLEND_EDGE",EDGE,{"blendedFrom":[makeQuery(id+"F40.boolean.opBoolean","INTERSECT",EDGE,{"derivedFrom":[subQ6,subQ13]}),makeQuery(id+"F40.boolean.opBoolean","SPLIT",FACE,{"disambiguationData":[TD([subQ0])],"derivedFrom":makeQuery(id+"F26.boolean.opBoolean","SPLIT",FACE,{"disambiguationData":[TD([subQ6])],"derivedFrom":makeQuery(id+"F25.boolean.opBoolean","SPLIT",FACE,{"disambiguationData":[TD([subQ82])],"derivedFrom":makeQuery(id+"F24.boolean.opBoolean","SPLIT",FACE,{"disambiguationData":[TD([subQ82])],"derivedFrom":makeQuery(id+"F1.opRevolve","SWEPT_FACE",FACE,{"disambiguationData":[OSD([sQuery(id+"F0.wireOp",EDGE,"E13")])]})})})})})],"blendedInto":[makeQuery(id+"F40.boolean.opBoolean","SPLIT",FACE,{"disambiguationData":[TD([subQ0])],"derivedFrom":makeQuery(id+"F26.boolean.opBoolean","SPLIT",FACE,{"disambiguationData":[TD([subQ6])],"derivedFrom":makeQuery(id+"F25.boolean.opBoolean","SPLIT",FACE,{"disambiguationData":[TD([subQ82])],"derivedFrom":makeQuery(id+"F24.boolean.opBoolean","SPLIT",FACE,{"disambiguationData":[TD([subQ82])],"derivedFrom":makeQuery(id+"F1.opRevolve","SWEPT_FACE",FACE,{"disambiguationData":[OSD([sQuery(id+"F0.wireOp",EDGE,"E13")])]})})})})})]});}
            var Q28;
            {var subQ0=makeQuery(id+"F1.opRevolve","SWEPT_FACE",FACE,{"disambiguationData":[OSD([sQuery(id+"F0.wireOp",EDGE,"E10")])]});var subQ1=sQuery(id+"F4.wireOp",EDGE,"E26.12.3");var subQ2=sQuery(id+"F4.wireOp",EDGE,"E26.12.2");var subQ3=sQuery(id+"F3.wireOp",EDGE,"E20.12.3");var subQ4=sQuery(id+"F3.wireOp",EDGE,"E20.12.2");var subQ5=sQuery(id+"F3.wireOp",EDGE,"E20.12.1");var subQ6=makeQuery(id+"F9.opLoft","SWEPT_FACE",FACE,{"disambiguationData":[OSD([subQ5,subQ4,subQ3,sQuery(id+"F4.wireOp",EDGE,"E26.12.1"),subQ2,subQ1])]});var subQ7=makeQuery(id+"F40.opExtrude","CAP_FACE",FACE,{"disambiguationData":[OSD([sQuery(id+"F39.wireOp",EDGE,"E29"),sQuery(id+"F39.wireOp",EDGE,"E30")])],"isStart":false});var subQ74=sQuery(id+"F3.wireOp",EDGE,"E18.bottom");var subQ77=makeQuery(id+"F5.opLoft","CAP_FACE",FACE,{"disambiguationData":[OSD([makeQuery(id+"F3.imprint","IMPRINT",FACE,{"disambiguationData":[TD([[makeQuery(id+"F3.imprint","IMPRINT",EDGE,{"derivedFrom":subQ74}),1.0]])]})])],"isStart":true});Q28=makeQuery(id+"F44.opFillet","BLEND_EDGE",EDGE,{"blendedFrom":[makeQuery(id+"F40.boolean.opBoolean","INTERSECT",EDGE,{"derivedFrom":[subQ6,subQ7]}),makeQuery(id+"F40.boolean.opBoolean","SPLIT",FACE,{"disambiguationData":[TD([subQ0])],"derivedFrom":makeQuery(id+"F27.boolean.opBoolean","SPLIT",FACE,{"disambiguationData":[TD([subQ6])],"derivedFrom":makeQuery(id+"F26.boolean.opBoolean","SPLIT",FACE,{"disambiguationData":[TD([subQ77])],"derivedFrom":makeQuery(id+"F25.boolean.opBoolean","SPLIT",FACE,{"disambiguationData":[TD([subQ77])],"derivedFrom":makeQuery(id+"F24.boolean.opBoolean","SPLIT",FACE,{"disambiguationData":[TD([subQ77])],"derivedFrom":makeQuery(id+"F1.opRevolve","SWEPT_FACE",FACE,{"disambiguationData":[OSD([sQuery(id+"F0.wireOp",EDGE,"E13")])]})})})})})})],"blendedInto":[makeQuery(id+"F40.boolean.opBoolean","SPLIT",FACE,{"disambiguationData":[TD([subQ0])],"derivedFrom":makeQuery(id+"F27.boolean.opBoolean","SPLIT",FACE,{"disambiguationData":[TD([subQ6])],"derivedFrom":makeQuery(id+"F26.boolean.opBoolean","SPLIT",FACE,{"disambiguationData":[TD([subQ77])],"derivedFrom":makeQuery(id+"F25.boolean.opBoolean","SPLIT",FACE,{"disambiguationData":[TD([subQ77])],"derivedFrom":makeQuery(id+"F24.boolean.opBoolean","SPLIT",FACE,{"disambiguationData":[TD([subQ77])],"derivedFrom":makeQuery(id+"F1.opRevolve","SWEPT_FACE",FACE,{"disambiguationData":[OSD([sQuery(id+"F0.wireOp",EDGE,"E13")])]})})})})})})]});}
            var Q29;
            {var subQ0=makeQuery(id+"F1.opRevolve","SWEPT_FACE",FACE,{"disambiguationData":[OSD([sQuery(id+"F0.wireOp",EDGE,"E10")])]});var subQ1=sQuery(id+"F4.wireOp",EDGE,"E26.13.3");var subQ2=sQuery(id+"F4.wireOp",EDGE,"E26.13.2");var subQ3=sQuery(id+"F3.wireOp",EDGE,"E20.13.3");var subQ4=sQuery(id+"F3.wireOp",EDGE,"E20.13.2");var subQ5=sQuery(id+"F3.wireOp",EDGE,"E20.13.1");var subQ6=makeQuery(id+"F8.opLoft","SWEPT_FACE",FACE,{"disambiguationData":[OSD([subQ5,subQ4,subQ3,sQuery(id+"F4.wireOp",EDGE,"E26.13.1"),subQ2,subQ1])]});var subQ13=makeQuery(id+"F40.opExtrude","CAP_FACE",FACE,{"disambiguationData":[OSD([sQuery(id+"F39.wireOp",EDGE,"E29"),sQuery(id+"F39.wireOp",EDGE,"E30")])],"isStart":false});var subQ56=sQuery(id+"F3.wireOp",EDGE,"E18.bottom");var subQ59=makeQuery(id+"F5.opLoft","CAP_FACE",FACE,{"disambiguationData":[OSD([makeQuery(id+"F3.imprint","IMPRINT",FACE,{"disambiguationData":[TD([[makeQuery(id+"F3.imprint","IMPRINT",EDGE,{"derivedFrom":subQ56}),1.0]])]})])],"isStart":true});Q29=makeQuery(id+"F44.opFillet","BLEND_EDGE",EDGE,{"blendedFrom":[makeQuery(id+"F40.boolean.opBoolean","INTERSECT",EDGE,{"derivedFrom":[subQ6,subQ13]}),makeQuery(id+"F40.boolean.opBoolean","SPLIT",FACE,{"disambiguationData":[TD([subQ0])],"derivedFrom":makeQuery(id+"F28.boolean.opBoolean","SPLIT",FACE,{"disambiguationData":[TD([subQ6])],"derivedFrom":makeQuery(id+"F27.boolean.opBoolean","SPLIT",FACE,{"disambiguationData":[TD([subQ59])],"derivedFrom":makeQuery(id+"F26.boolean.opBoolean","SPLIT",FACE,{"disambiguationData":[TD([subQ59])],"derivedFrom":makeQuery(id+"F25.boolean.opBoolean","SPLIT",FACE,{"disambiguationData":[TD([subQ59])],"derivedFrom":makeQuery(id+"F24.boolean.opBoolean","SPLIT",FACE,{"disambiguationData":[TD([subQ59])],"derivedFrom":makeQuery(id+"F1.opRevolve","SWEPT_FACE",FACE,{"disambiguationData":[OSD([sQuery(id+"F0.wireOp",EDGE,"E13")])]})})})})})})})],"blendedInto":[makeQuery(id+"F40.boolean.opBoolean","SPLIT",FACE,{"disambiguationData":[TD([subQ0])],"derivedFrom":makeQuery(id+"F28.boolean.opBoolean","SPLIT",FACE,{"disambiguationData":[TD([subQ6])],"derivedFrom":makeQuery(id+"F27.boolean.opBoolean","SPLIT",FACE,{"disambiguationData":[TD([subQ59])],"derivedFrom":makeQuery(id+"F26.boolean.opBoolean","SPLIT",FACE,{"disambiguationData":[TD([subQ59])],"derivedFrom":makeQuery(id+"F25.boolean.opBoolean","SPLIT",FACE,{"disambiguationData":[TD([subQ59])],"derivedFrom":makeQuery(id+"F24.boolean.opBoolean","SPLIT",FACE,{"disambiguationData":[TD([subQ59])],"derivedFrom":makeQuery(id+"F1.opRevolve","SWEPT_FACE",FACE,{"disambiguationData":[OSD([sQuery(id+"F0.wireOp",EDGE,"E13")])]})})})})})})})]});}
            var Q30;
            {var subQ0=makeQuery(id+"F1.opRevolve","SWEPT_FACE",FACE,{"disambiguationData":[OSD([sQuery(id+"F0.wireOp",EDGE,"E10")])]});var subQ1=sQuery(id+"F4.wireOp",EDGE,"E26.14.3");var subQ2=sQuery(id+"F4.wireOp",EDGE,"E26.14.2");var subQ3=sQuery(id+"F3.wireOp",EDGE,"E20.14.3");var subQ4=sQuery(id+"F3.wireOp",EDGE,"E20.14.2");var subQ5=sQuery(id+"F3.wireOp",EDGE,"E20.14.1");var subQ6=makeQuery(id+"F7.opLoft","SWEPT_FACE",FACE,{"disambiguationData":[OSD([subQ5,subQ4,subQ3,sQuery(id+"F4.wireOp",EDGE,"E26.14.1"),subQ2,subQ1])]});var subQ13=makeQuery(id+"F40.opExtrude","CAP_FACE",FACE,{"disambiguationData":[OSD([sQuery(id+"F39.wireOp",EDGE,"E29"),sQuery(id+"F39.wireOp",EDGE,"E30")])],"isStart":false});var subQ48=sQuery(id+"F3.wireOp",EDGE,"E18.bottom");var subQ51=makeQuery(id+"F5.opLoft","CAP_FACE",FACE,{"disambiguationData":[OSD([makeQuery(id+"F3.imprint","IMPRINT",FACE,{"disambiguationData":[TD([[makeQuery(id+"F3.imprint","IMPRINT",EDGE,{"derivedFrom":subQ48}),1.0]])]})])],"isStart":true});Q30=makeQuery(id+"F44.opFillet","BLEND_EDGE",EDGE,{"blendedFrom":[makeQuery(id+"F40.boolean.opBoolean","INTERSECT",EDGE,{"derivedFrom":[subQ6,subQ13]}),makeQuery(id+"F40.boolean.opBoolean","SPLIT",FACE,{"disambiguationData":[TD([subQ0])],"derivedFrom":makeQuery(id+"F29.boolean.opBoolean","SPLIT",FACE,{"disambiguationData":[TD([subQ6])],"derivedFrom":makeQuery(id+"F28.boolean.opBoolean","SPLIT",FACE,{"disambiguationData":[TD([subQ51])],"derivedFrom":makeQuery(id+"F27.boolean.opBoolean","SPLIT",FACE,{"disambiguationData":[TD([subQ51])],"derivedFrom":makeQuery(id+"F26.boolean.opBoolean","SPLIT",FACE,{"disambiguationData":[TD([subQ51])],"derivedFrom":makeQuery(id+"F25.boolean.opBoolean","SPLIT",FACE,{"disambiguationData":[TD([subQ51])],"derivedFrom":makeQuery(id+"F24.boolean.opBoolean","SPLIT",FACE,{"disambiguationData":[TD([subQ51])],"derivedFrom":makeQuery(id+"F1.opRevolve","SWEPT_FACE",FACE,{"disambiguationData":[OSD([sQuery(id+"F0.wireOp",EDGE,"E13")])]})})})})})})})})],"blendedInto":[makeQuery(id+"F40.boolean.opBoolean","SPLIT",FACE,{"disambiguationData":[TD([subQ0])],"derivedFrom":makeQuery(id+"F29.boolean.opBoolean","SPLIT",FACE,{"disambiguationData":[TD([subQ6])],"derivedFrom":makeQuery(id+"F28.boolean.opBoolean","SPLIT",FACE,{"disambiguationData":[TD([subQ51])],"derivedFrom":makeQuery(id+"F27.boolean.opBoolean","SPLIT",FACE,{"disambiguationData":[TD([subQ51])],"derivedFrom":makeQuery(id+"F26.boolean.opBoolean","SPLIT",FACE,{"disambiguationData":[TD([subQ51])],"derivedFrom":makeQuery(id+"F25.boolean.opBoolean","SPLIT",FACE,{"disambiguationData":[TD([subQ51])],"derivedFrom":makeQuery(id+"F24.boolean.opBoolean","SPLIT",FACE,{"disambiguationData":[TD([subQ51])],"derivedFrom":makeQuery(id+"F1.opRevolve","SWEPT_FACE",FACE,{"disambiguationData":[OSD([sQuery(id+"F0.wireOp",EDGE,"E13")])]})})})})})})})})]});}
            var Q31;
            {var subQ0=makeQuery(id+"F1.opRevolve","SWEPT_FACE",FACE,{"disambiguationData":[OSD([sQuery(id+"F0.wireOp",EDGE,"E10")])]});var subQ7=sQuery(id+"F4.wireOp",EDGE,"E26.15.3");var subQ8=sQuery(id+"F4.wireOp",EDGE,"E26.15.2");var subQ9=sQuery(id+"F3.wireOp",EDGE,"E20.15.3");var subQ10=sQuery(id+"F3.wireOp",EDGE,"E20.15.2");var subQ11=sQuery(id+"F3.wireOp",EDGE,"E20.15.1");var subQ12=makeQuery(id+"F6.opLoft","SWEPT_FACE",FACE,{"disambiguationData":[OSD([subQ11,subQ10,subQ9,sQuery(id+"F4.wireOp",EDGE,"E26.15.1"),subQ8,subQ7])]});var subQ13=makeQuery(id+"F40.opExtrude","CAP_FACE",FACE,{"disambiguationData":[OSD([sQuery(id+"F39.wireOp",EDGE,"E29"),sQuery(id+"F39.wireOp",EDGE,"E30")])],"isStart":false});var subQ47=sQuery(id+"F3.wireOp",EDGE,"E18.bottom");var subQ50=makeQuery(id+"F5.opLoft","CAP_FACE",FACE,{"disambiguationData":[OSD([makeQuery(id+"F3.imprint","IMPRINT",FACE,{"disambiguationData":[TD([[makeQuery(id+"F3.imprint","IMPRINT",EDGE,{"derivedFrom":subQ47}),1.0]])]})])],"isStart":true});Q31=makeQuery(id+"F44.opFillet","BLEND_EDGE",EDGE,{"blendedFrom":[makeQuery(id+"F40.boolean.opBoolean","INTERSECT",EDGE,{"derivedFrom":[subQ12,subQ13]}),makeQuery(id+"F40.boolean.opBoolean","SPLIT",FACE,{"disambiguationData":[TD([subQ0])],"derivedFrom":makeQuery(id+"F30.boolean.opBoolean","SPLIT",FACE,{"disambiguationData":[TD([subQ12])],"derivedFrom":makeQuery(id+"F29.boolean.opBoolean","SPLIT",FACE,{"disambiguationData":[TD([subQ50])],"derivedFrom":makeQuery(id+"F28.boolean.opBoolean","SPLIT",FACE,{"disambiguationData":[TD([subQ50])],"derivedFrom":makeQuery(id+"F27.boolean.opBoolean","SPLIT",FACE,{"disambiguationData":[TD([subQ50])],"derivedFrom":makeQuery(id+"F26.boolean.opBoolean","SPLIT",FACE,{"disambiguationData":[TD([subQ50])],"derivedFrom":makeQuery(id+"F25.boolean.opBoolean","SPLIT",FACE,{"disambiguationData":[TD([subQ50])],"derivedFrom":makeQuery(id+"F24.boolean.opBoolean","SPLIT",FACE,{"disambiguationData":[TD([subQ50])],"derivedFrom":makeQuery(id+"F1.opRevolve","SWEPT_FACE",FACE,{"disambiguationData":[OSD([sQuery(id+"F0.wireOp",EDGE,"E13")])]})})})})})})})})})],"blendedInto":[makeQuery(id+"F40.boolean.opBoolean","SPLIT",FACE,{"disambiguationData":[TD([subQ0])],"derivedFrom":makeQuery(id+"F30.boolean.opBoolean","SPLIT",FACE,{"disambiguationData":[TD([subQ12])],"derivedFrom":makeQuery(id+"F29.boolean.opBoolean","SPLIT",FACE,{"disambiguationData":[TD([subQ50])],"derivedFrom":makeQuery(id+"F28.boolean.opBoolean","SPLIT",FACE,{"disambiguationData":[TD([subQ50])],"derivedFrom":makeQuery(id+"F27.boolean.opBoolean","SPLIT",FACE,{"disambiguationData":[TD([subQ50])],"derivedFrom":makeQuery(id+"F26.boolean.opBoolean","SPLIT",FACE,{"disambiguationData":[TD([subQ50])],"derivedFrom":makeQuery(id+"F25.boolean.opBoolean","SPLIT",FACE,{"disambiguationData":[TD([subQ50])],"derivedFrom":makeQuery(id+"F24.boolean.opBoolean","SPLIT",FACE,{"disambiguationData":[TD([subQ50])],"derivedFrom":makeQuery(id+"F1.opRevolve","SWEPT_FACE",FACE,{"disambiguationData":[OSD([sQuery(id+"F0.wireOp",EDGE,"E13")])]})})})})})})})})})]});}
            fillet(context, id + "F45", {"entities" : qUnion([Q0, Q1, Q2, Q3, Q4, Q5, Q6, Q7, Q8, Q9, Q10, Q11, Q12, Q13, Q14, Q15, Q16, Q17, Q18, Q19, Q20, Q21, Q22, Q23, Q24, Q25, Q26, Q27, Q28, Q29, Q30, Q31]), "radius" : 4 * mm, "tangentPropagation" : true, "allowEdgeOverflow" : false});
        }
        {
            var Q0;
            Q0=makeQuery(id+"F19.boolean.opBoolean","INTERSECT",EDGE,{"derivedFrom":[makeQuery(id+"F1.opRevolve","SWEPT_FACE",FACE,{"disambiguationData":[OSD([sQuery(id+"F0.wireOp",EDGE,"E13")])]}),makeQuery(id+"F19.opLoft","SWEPT_FACE",FACE,{"disambiguationData":[OSD([sQuery(id+"F3.wireOp",EDGE,"E20.2.0"),sQuery(id+"F3.wireOp",EDGE,"E20.2.1"),sQuery(id+"F3.wireOp",EDGE,"E20.2.3"),sQuery(id+"F4.wireOp",EDGE,"E26.2.0"),sQuery(id+"F4.wireOp",EDGE,"E26.2.2"),sQuery(id+"F4.wireOp",EDGE,"E26.2.3")])]})]});
            var Q1;
            Q1=makeQuery(id+"F20.boolean.opBoolean","INTERSECT",EDGE,{"derivedFrom":[makeQuery(id+"F1.opRevolve","SWEPT_FACE",FACE,{"disambiguationData":[OSD([sQuery(id+"F0.wireOp",EDGE,"E13")])]}),makeQuery(id+"F20.opLoft","SWEPT_FACE",FACE,{"disambiguationData":[OSD([sQuery(id+"F3.wireOp",EDGE,"E20.1.0"),sQuery(id+"F3.wireOp",EDGE,"E20.1.1"),sQuery(id+"F3.wireOp",EDGE,"E20.1.3"),sQuery(id+"F4.wireOp",EDGE,"E26.1.0"),sQuery(id+"F4.wireOp",EDGE,"E26.1.2"),sQuery(id+"F4.wireOp",EDGE,"E26.1.3")])]})]});
            var Q2;
            {var subQ0=sQuery(id+"F3.wireOp",EDGE,"E20.1.3");var subQ1=sQuery(id+"F3.wireOp",EDGE,"E20.1.1");var subQ2=sQuery(id+"F3.wireOp",EDGE,"E20.1.0");var subQ51=sQuery(id+"F3.wireOp",EDGE,"E18.bottom");var subQ62=sQuery(id+"F3.wireOp",EDGE,"E20.7.0");var subQ70=makeQuery(id+"F14.opLoft","CAP_FACE",FACE,{"disambiguationData":[OSD([makeQuery(id+"F3.imprint","IMPRINT",FACE,{"disambiguationData":[TD([[makeQuery(id+"F3.imprint","IMPRINT",EDGE,{"derivedFrom":subQ62}),-1.0]])]})])],"isStart":true});var subQ78=makeQuery(id+"F5.opLoft","CAP_FACE",FACE,{"disambiguationData":[OSD([makeQuery(id+"F3.imprint","IMPRINT",FACE,{"disambiguationData":[TD([[makeQuery(id+"F3.imprint","IMPRINT",EDGE,{"derivedFrom":subQ51}),1.0]])]})])],"isStart":true});Q2=makeQuery(id+"F32.boolean.opBoolean","INTERSECT",EDGE,{"derivedFrom":[makeQuery(id+"F31.boolean.opBoolean","SPLIT",FACE,{"disambiguationData":[TD([subQ70])],"derivedFrom":makeQuery(id+"F30.boolean.opBoolean","SPLIT",FACE,{"disambiguationData":[TD([subQ78])],"derivedFrom":makeQuery(id+"F29.boolean.opBoolean","SPLIT",FACE,{"disambiguationData":[TD([subQ78])],"derivedFrom":makeQuery(id+"F28.boolean.opBoolean","SPLIT",FACE,{"disambiguationData":[TD([subQ78])],"derivedFrom":makeQuery(id+"F27.boolean.opBoolean","SPLIT",FACE,{"disambiguationData":[TD([subQ78])],"derivedFrom":makeQuery(id+"F26.boolean.opBoolean","SPLIT",FACE,{"disambiguationData":[TD([subQ78])],"derivedFrom":makeQuery(id+"F25.boolean.opBoolean","SPLIT",FACE,{"disambiguationData":[TD([subQ78])],"derivedFrom":makeQuery(id+"F24.boolean.opBoolean","SPLIT",FACE,{"disambiguationData":[TD([subQ78])],"derivedFrom":makeQuery(id+"F1.opRevolve","SWEPT_FACE",FACE,{"disambiguationData":[OSD([sQuery(id+"F0.wireOp",EDGE,"E13")])]})})})})})})})})}),makeQuery(id+"F32.opLoft","SWEPT_FACE",FACE,{"disambiguationData":[OSD([subQ2,subQ1,subQ0,sQuery(id+"F22.wireOp",EDGE,"E28.9.1"),sQuery(id+"F22.wireOp",EDGE,"E28.9.2"),sQuery(id+"F22.wireOp",EDGE,"E28.9.3")])]})]});}
            var Q3;
            {var subQ0=sQuery(id+"F3.wireOp",EDGE,"E20.2.3");var subQ1=sQuery(id+"F3.wireOp",EDGE,"E20.2.1");var subQ2=sQuery(id+"F3.wireOp",EDGE,"E20.2.0");var subQ51=sQuery(id+"F3.wireOp",EDGE,"E20.7.0");var subQ60=makeQuery(id+"F14.opLoft","CAP_FACE",FACE,{"disambiguationData":[OSD([makeQuery(id+"F3.imprint","IMPRINT",FACE,{"disambiguationData":[TD([[makeQuery(id+"F3.imprint","IMPRINT",EDGE,{"derivedFrom":subQ51}),-1.0]])]})])],"isStart":true});var subQ73=sQuery(id+"F3.wireOp",EDGE,"E18.bottom");var subQ78=makeQuery(id+"F5.opLoft","CAP_FACE",FACE,{"disambiguationData":[OSD([makeQuery(id+"F3.imprint","IMPRINT",FACE,{"disambiguationData":[TD([[makeQuery(id+"F3.imprint","IMPRINT",EDGE,{"derivedFrom":subQ73}),1.0]])]})])],"isStart":true});Q3=makeQuery(id+"F33.boolean.opBoolean","INTERSECT",EDGE,{"derivedFrom":[makeQuery(id+"F32.boolean.opBoolean","SPLIT",FACE,{"disambiguationData":[TD([subQ60])],"derivedFrom":makeQuery(id+"F31.boolean.opBoolean","SPLIT",FACE,{"disambiguationData":[TD([subQ60])],"derivedFrom":makeQuery(id+"F30.boolean.opBoolean","SPLIT",FACE,{"disambiguationData":[TD([subQ78])],"derivedFrom":makeQuery(id+"F29.boolean.opBoolean","SPLIT",FACE,{"disambiguationData":[TD([subQ78])],"derivedFrom":makeQuery(id+"F28.boolean.opBoolean","SPLIT",FACE,{"disambiguationData":[TD([subQ78])],"derivedFrom":makeQuery(id+"F27.boolean.opBoolean","SPLIT",FACE,{"disambiguationData":[TD([subQ78])],"derivedFrom":makeQuery(id+"F26.boolean.opBoolean","SPLIT",FACE,{"disambiguationData":[TD([subQ78])],"derivedFrom":makeQuery(id+"F25.boolean.opBoolean","SPLIT",FACE,{"disambiguationData":[TD([subQ78])],"derivedFrom":makeQuery(id+"F24.boolean.opBoolean","SPLIT",FACE,{"disambiguationData":[TD([subQ78])],"derivedFrom":makeQuery(id+"F1.opRevolve","SWEPT_FACE",FACE,{"disambiguationData":[OSD([sQuery(id+"F0.wireOp",EDGE,"E13")])]})})})})})})})})})}),makeQuery(id+"F33.opLoft","SWEPT_FACE",FACE,{"disambiguationData":[OSD([subQ2,subQ1,subQ0,sQuery(id+"F22.wireOp",EDGE,"E28.10.1"),sQuery(id+"F22.wireOp",EDGE,"E28.10.2"),sQuery(id+"F22.wireOp",EDGE,"E28.10.3")])]})]});}
            var Q4;
            {var subQ0=sQuery(id+"F3.wireOp",EDGE,"E20.3.3");var subQ1=sQuery(id+"F3.wireOp",EDGE,"E20.3.1");var subQ2=sQuery(id+"F3.wireOp",EDGE,"E20.3.0");var subQ22=sQuery(id+"F3.wireOp",EDGE,"E20.7.0");var subQ26=makeQuery(id+"F14.opLoft","CAP_FACE",FACE,{"disambiguationData":[OSD([makeQuery(id+"F3.imprint","IMPRINT",FACE,{"disambiguationData":[TD([[makeQuery(id+"F3.imprint","IMPRINT",EDGE,{"derivedFrom":subQ22}),-1.0]])]})])],"isStart":true});var subQ73=sQuery(id+"F3.wireOp",EDGE,"E18.bottom");var subQ78=makeQuery(id+"F5.opLoft","CAP_FACE",FACE,{"disambiguationData":[OSD([makeQuery(id+"F3.imprint","IMPRINT",FACE,{"disambiguationData":[TD([[makeQuery(id+"F3.imprint","IMPRINT",EDGE,{"derivedFrom":subQ73}),1.0]])]})])],"isStart":true});Q4=makeQuery(id+"F34.boolean.opBoolean","INTERSECT",EDGE,{"derivedFrom":[makeQuery(id+"F33.boolean.opBoolean","SPLIT",FACE,{"disambiguationData":[TD([subQ26])],"derivedFrom":makeQuery(id+"F32.boolean.opBoolean","SPLIT",FACE,{"disambiguationData":[TD([subQ26])],"derivedFrom":makeQuery(id+"F31.boolean.opBoolean","SPLIT",FACE,{"disambiguationData":[TD([subQ26])],"derivedFrom":makeQuery(id+"F30.boolean.opBoolean","SPLIT",FACE,{"disambiguationData":[TD([subQ78])],"derivedFrom":makeQuery(id+"F29.boolean.opBoolean","SPLIT",FACE,{"disambiguationData":[TD([subQ78])],"derivedFrom":makeQuery(id+"F28.boolean.opBoolean","SPLIT",FACE,{"disambiguationData":[TD([subQ78])],"derivedFrom":makeQuery(id+"F27.boolean.opBoolean","SPLIT",FACE,{"disambiguationData":[TD([subQ78])],"derivedFrom":makeQuery(id+"F26.boolean.opBoolean","SPLIT",FACE,{"disambiguationData":[TD([subQ78])],"derivedFrom":makeQuery(id+"F25.boolean.opBoolean","SPLIT",FACE,{"disambiguationData":[TD([subQ78])],"derivedFrom":makeQuery(id+"F24.boolean.opBoolean","SPLIT",FACE,{"disambiguationData":[TD([subQ78])],"derivedFrom":makeQuery(id+"F1.opRevolve","SWEPT_FACE",FACE,{"disambiguationData":[OSD([sQuery(id+"F0.wireOp",EDGE,"E13")])]})})})})})})})})})})}),makeQuery(id+"F34.opLoft","SWEPT_FACE",FACE,{"disambiguationData":[OSD([subQ2,subQ1,subQ0,sQuery(id+"F22.wireOp",EDGE,"E28.11.1"),sQuery(id+"F22.wireOp",EDGE,"E28.11.2"),sQuery(id+"F22.wireOp",EDGE,"E28.11.3")])]})]});}
            var Q5;
            {var subQ0=sQuery(id+"F3.wireOp",EDGE,"E20.4.3");var subQ1=sQuery(id+"F3.wireOp",EDGE,"E20.4.1");var subQ2=sQuery(id+"F3.wireOp",EDGE,"E20.4.0");var subQ19=sQuery(id+"F3.wireOp",EDGE,"E20.7.0");var subQ23=makeQuery(id+"F14.opLoft","CAP_FACE",FACE,{"disambiguationData":[OSD([makeQuery(id+"F3.imprint","IMPRINT",FACE,{"disambiguationData":[TD([[makeQuery(id+"F3.imprint","IMPRINT",EDGE,{"derivedFrom":subQ19}),-1.0]])]})])],"isStart":true});var subQ73=sQuery(id+"F3.wireOp",EDGE,"E18.bottom");var subQ78=makeQuery(id+"F5.opLoft","CAP_FACE",FACE,{"disambiguationData":[OSD([makeQuery(id+"F3.imprint","IMPRINT",FACE,{"disambiguationData":[TD([[makeQuery(id+"F3.imprint","IMPRINT",EDGE,{"derivedFrom":subQ73}),1.0]])]})])],"isStart":true});Q5=makeQuery(id+"F35.boolean.opBoolean","INTERSECT",EDGE,{"derivedFrom":[makeQuery(id+"F34.boolean.opBoolean","SPLIT",FACE,{"disambiguationData":[TD([subQ23])],"derivedFrom":makeQuery(id+"F33.boolean.opBoolean","SPLIT",FACE,{"disambiguationData":[TD([subQ23])],"derivedFrom":makeQuery(id+"F32.boolean.opBoolean","SPLIT",FACE,{"disambiguationData":[TD([subQ23])],"derivedFrom":makeQuery(id+"F31.boolean.opBoolean","SPLIT",FACE,{"disambiguationData":[TD([subQ23])],"derivedFrom":makeQuery(id+"F30.boolean.opBoolean","SPLIT",FACE,{"disambiguationData":[TD([subQ78])],"derivedFrom":makeQuery(id+"F29.boolean.opBoolean","SPLIT",FACE,{"disambiguationData":[TD([subQ78])],"derivedFrom":makeQuery(id+"F28.boolean.opBoolean","SPLIT",FACE,{"disambiguationData":[TD([subQ78])],"derivedFrom":makeQuery(id+"F27.boolean.opBoolean","SPLIT",FACE,{"disambiguationData":[TD([subQ78])],"derivedFrom":makeQuery(id+"F26.boolean.opBoolean","SPLIT",FACE,{"disambiguationData":[TD([subQ78])],"derivedFrom":makeQuery(id+"F25.boolean.opBoolean","SPLIT",FACE,{"disambiguationData":[TD([subQ78])],"derivedFrom":makeQuery(id+"F24.boolean.opBoolean","SPLIT",FACE,{"disambiguationData":[TD([subQ78])],"derivedFrom":makeQuery(id+"F1.opRevolve","SWEPT_FACE",FACE,{"disambiguationData":[OSD([sQuery(id+"F0.wireOp",EDGE,"E13")])]})})})})})})})})})})})}),makeQuery(id+"F35.opLoft","SWEPT_FACE",FACE,{"disambiguationData":[OSD([subQ2,subQ1,subQ0,sQuery(id+"F22.wireOp",EDGE,"E28.12.1"),sQuery(id+"F22.wireOp",EDGE,"E28.12.2"),sQuery(id+"F22.wireOp",EDGE,"E28.12.3")])]})]});}
            var Q6;
            {var subQ0=sQuery(id+"F3.wireOp",EDGE,"E20.5.3");var subQ1=sQuery(id+"F3.wireOp",EDGE,"E20.5.1");var subQ2=sQuery(id+"F3.wireOp",EDGE,"E20.5.0");var subQ14=sQuery(id+"F3.wireOp",EDGE,"E20.7.0");var subQ18=makeQuery(id+"F14.opLoft","CAP_FACE",FACE,{"disambiguationData":[OSD([makeQuery(id+"F3.imprint","IMPRINT",FACE,{"disambiguationData":[TD([[makeQuery(id+"F3.imprint","IMPRINT",EDGE,{"derivedFrom":subQ14}),-1.0]])]})])],"isStart":true});var subQ73=sQuery(id+"F3.wireOp",EDGE,"E18.bottom");var subQ78=makeQuery(id+"F5.opLoft","CAP_FACE",FACE,{"disambiguationData":[OSD([makeQuery(id+"F3.imprint","IMPRINT",FACE,{"disambiguationData":[TD([[makeQuery(id+"F3.imprint","IMPRINT",EDGE,{"derivedFrom":subQ73}),1.0]])]})])],"isStart":true});Q6=makeQuery(id+"F36.boolean.opBoolean","INTERSECT",EDGE,{"derivedFrom":[makeQuery(id+"F35.boolean.opBoolean","SPLIT",FACE,{"disambiguationData":[TD([subQ18])],"derivedFrom":makeQuery(id+"F34.boolean.opBoolean","SPLIT",FACE,{"disambiguationData":[TD([subQ18])],"derivedFrom":makeQuery(id+"F33.boolean.opBoolean","SPLIT",FACE,{"disambiguationData":[TD([subQ18])],"derivedFrom":makeQuery(id+"F32.boolean.opBoolean","SPLIT",FACE,{"disambiguationData":[TD([subQ18])],"derivedFrom":makeQuery(id+"F31.boolean.opBoolean","SPLIT",FACE,{"disambiguationData":[TD([subQ18])],"derivedFrom":makeQuery(id+"F30.boolean.opBoolean","SPLIT",FACE,{"disambiguationData":[TD([subQ78])],"derivedFrom":makeQuery(id+"F29.boolean.opBoolean","SPLIT",FACE,{"disambiguationData":[TD([subQ78])],"derivedFrom":makeQuery(id+"F28.boolean.opBoolean","SPLIT",FACE,{"disambiguationData":[TD([subQ78])],"derivedFrom":makeQuery(id+"F27.boolean.opBoolean","SPLIT",FACE,{"disambiguationData":[TD([subQ78])],"derivedFrom":makeQuery(id+"F26.boolean.opBoolean","SPLIT",FACE,{"disambiguationData":[TD([subQ78])],"derivedFrom":makeQuery(id+"F25.boolean.opBoolean","SPLIT",FACE,{"disambiguationData":[TD([subQ78])],"derivedFrom":makeQuery(id+"F24.boolean.opBoolean","SPLIT",FACE,{"disambiguationData":[TD([subQ78])],"derivedFrom":makeQuery(id+"F1.opRevolve","SWEPT_FACE",FACE,{"disambiguationData":[OSD([sQuery(id+"F0.wireOp",EDGE,"E13")])]})})})})})})})})})})})})}),makeQuery(id+"F36.opLoft","SWEPT_FACE",FACE,{"disambiguationData":[OSD([subQ2,subQ1,subQ0,sQuery(id+"F22.wireOp",EDGE,"E28.13.1"),sQuery(id+"F22.wireOp",EDGE,"E28.13.2"),sQuery(id+"F22.wireOp",EDGE,"E28.13.3")])]})]});}
            var Q7;
            {var subQ0=sQuery(id+"F3.wireOp",EDGE,"E20.6.3");var subQ1=sQuery(id+"F3.wireOp",EDGE,"E20.6.1");var subQ2=sQuery(id+"F3.wireOp",EDGE,"E20.6.0");var subQ14=sQuery(id+"F3.wireOp",EDGE,"E20.7.0");var subQ18=makeQuery(id+"F14.opLoft","CAP_FACE",FACE,{"disambiguationData":[OSD([makeQuery(id+"F3.imprint","IMPRINT",FACE,{"disambiguationData":[TD([[makeQuery(id+"F3.imprint","IMPRINT",EDGE,{"derivedFrom":subQ14}),-1.0]])]})])],"isStart":true});var subQ73=sQuery(id+"F3.wireOp",EDGE,"E18.bottom");var subQ78=makeQuery(id+"F5.opLoft","CAP_FACE",FACE,{"disambiguationData":[OSD([makeQuery(id+"F3.imprint","IMPRINT",FACE,{"disambiguationData":[TD([[makeQuery(id+"F3.imprint","IMPRINT",EDGE,{"derivedFrom":subQ73}),1.0]])]})])],"isStart":true});Q7=makeQuery(id+"F37.boolean.opBoolean","INTERSECT",EDGE,{"derivedFrom":[makeQuery(id+"F36.boolean.opBoolean","SPLIT",FACE,{"disambiguationData":[TD([subQ18])],"derivedFrom":makeQuery(id+"F35.boolean.opBoolean","SPLIT",FACE,{"disambiguationData":[TD([subQ18])],"derivedFrom":makeQuery(id+"F34.boolean.opBoolean","SPLIT",FACE,{"disambiguationData":[TD([subQ18])],"derivedFrom":makeQuery(id+"F33.boolean.opBoolean","SPLIT",FACE,{"disambiguationData":[TD([subQ18])],"derivedFrom":makeQuery(id+"F32.boolean.opBoolean","SPLIT",FACE,{"disambiguationData":[TD([subQ18])],"derivedFrom":makeQuery(id+"F31.boolean.opBoolean","SPLIT",FACE,{"disambiguationData":[TD([subQ18])],"derivedFrom":makeQuery(id+"F30.boolean.opBoolean","SPLIT",FACE,{"disambiguationData":[TD([subQ78])],"derivedFrom":makeQuery(id+"F29.boolean.opBoolean","SPLIT",FACE,{"disambiguationData":[TD([subQ78])],"derivedFrom":makeQuery(id+"F28.boolean.opBoolean","SPLIT",FACE,{"disambiguationData":[TD([subQ78])],"derivedFrom":makeQuery(id+"F27.boolean.opBoolean","SPLIT",FACE,{"disambiguationData":[TD([subQ78])],"derivedFrom":makeQuery(id+"F26.boolean.opBoolean","SPLIT",FACE,{"disambiguationData":[TD([subQ78])],"derivedFrom":makeQuery(id+"F25.boolean.opBoolean","SPLIT",FACE,{"disambiguationData":[TD([subQ78])],"derivedFrom":makeQuery(id+"F24.boolean.opBoolean","SPLIT",FACE,{"disambiguationData":[TD([subQ78])],"derivedFrom":makeQuery(id+"F1.opRevolve","SWEPT_FACE",FACE,{"disambiguationData":[OSD([sQuery(id+"F0.wireOp",EDGE,"E13")])]})})})})})})})})})})})})})}),makeQuery(id+"F37.opLoft","SWEPT_FACE",FACE,{"disambiguationData":[OSD([subQ2,subQ1,subQ0,sQuery(id+"F22.wireOp",EDGE,"E28.14.1"),sQuery(id+"F22.wireOp",EDGE,"E28.14.2"),sQuery(id+"F22.wireOp",EDGE,"E28.14.3")])]})]});}
            var Q8;
            {var subQ0=sQuery(id+"F3.wireOp",EDGE,"E20.7.3");var subQ1=sQuery(id+"F3.wireOp",EDGE,"E20.7.1");var subQ2=sQuery(id+"F3.wireOp",EDGE,"E20.7.0");var subQ14=makeQuery(id+"F14.opLoft","CAP_FACE",FACE,{"disambiguationData":[OSD([makeQuery(id+"F3.imprint","IMPRINT",FACE,{"disambiguationData":[TD([[makeQuery(id+"F3.imprint","IMPRINT",EDGE,{"derivedFrom":subQ2}),-1.0]])]})])],"isStart":true});var subQ73=sQuery(id+"F3.wireOp",EDGE,"E18.bottom");var subQ78=makeQuery(id+"F5.opLoft","CAP_FACE",FACE,{"disambiguationData":[OSD([makeQuery(id+"F3.imprint","IMPRINT",FACE,{"disambiguationData":[TD([[makeQuery(id+"F3.imprint","IMPRINT",EDGE,{"derivedFrom":subQ73}),1.0]])]})])],"isStart":true});Q8=makeQuery(id+"F38.boolean.opBoolean","INTERSECT",EDGE,{"derivedFrom":[makeQuery(id+"F37.boolean.opBoolean","SPLIT",FACE,{"disambiguationData":[TD([subQ14])],"derivedFrom":makeQuery(id+"F36.boolean.opBoolean","SPLIT",FACE,{"disambiguationData":[TD([subQ14])],"derivedFrom":makeQuery(id+"F35.boolean.opBoolean","SPLIT",FACE,{"disambiguationData":[TD([subQ14])],"derivedFrom":makeQuery(id+"F34.boolean.opBoolean","SPLIT",FACE,{"disambiguationData":[TD([subQ14])],"derivedFrom":makeQuery(id+"F33.boolean.opBoolean","SPLIT",FACE,{"disambiguationData":[TD([subQ14])],"derivedFrom":makeQuery(id+"F32.boolean.opBoolean","SPLIT",FACE,{"disambiguationData":[TD([subQ14])],"derivedFrom":makeQuery(id+"F31.boolean.opBoolean","SPLIT",FACE,{"disambiguationData":[TD([subQ14])],"derivedFrom":makeQuery(id+"F30.boolean.opBoolean","SPLIT",FACE,{"disambiguationData":[TD([subQ78])],"derivedFrom":makeQuery(id+"F29.boolean.opBoolean","SPLIT",FACE,{"disambiguationData":[TD([subQ78])],"derivedFrom":makeQuery(id+"F28.boolean.opBoolean","SPLIT",FACE,{"disambiguationData":[TD([subQ78])],"derivedFrom":makeQuery(id+"F27.boolean.opBoolean","SPLIT",FACE,{"disambiguationData":[TD([subQ78])],"derivedFrom":makeQuery(id+"F26.boolean.opBoolean","SPLIT",FACE,{"disambiguationData":[TD([subQ78])],"derivedFrom":makeQuery(id+"F25.boolean.opBoolean","SPLIT",FACE,{"disambiguationData":[TD([subQ78])],"derivedFrom":makeQuery(id+"F24.boolean.opBoolean","SPLIT",FACE,{"disambiguationData":[TD([subQ78])],"derivedFrom":makeQuery(id+"F1.opRevolve","SWEPT_FACE",FACE,{"disambiguationData":[OSD([sQuery(id+"F0.wireOp",EDGE,"E13")])]})})})})})})})})})})})})})})}),makeQuery(id+"F38.opLoft","SWEPT_FACE",FACE,{"disambiguationData":[OSD([subQ2,subQ1,subQ0,sQuery(id+"F22.wireOp",EDGE,"E28.15.1"),sQuery(id+"F22.wireOp",EDGE,"E28.15.2"),sQuery(id+"F22.wireOp",EDGE,"E28.15.3")])]})]});}
            var Q9;
            Q9=makeQuery(id+"F23.boolean.opBoolean","INTERSECT",EDGE,{"derivedFrom":[makeQuery(id+"F1.opRevolve","SWEPT_FACE",FACE,{"disambiguationData":[OSD([sQuery(id+"F0.wireOp",EDGE,"E13")])]}),makeQuery(id+"F23.opLoft","SWEPT_FACE",FACE,{"disambiguationData":[OSD([sQuery(id+"F3.wireOp",EDGE,"E20.8.0"),sQuery(id+"F3.wireOp",EDGE,"E20.8.1"),sQuery(id+"F3.wireOp",EDGE,"E20.8.3"),sQuery(id+"F22.wireOp",EDGE,"E27.bottom"),sQuery(id+"F22.wireOp",EDGE,"E27.top"),sQuery(id+"F22.wireOp",EDGE,"E27.right")])]})]});
            var Q10;
            Q10=makeQuery(id+"F24.boolean.opBoolean","INTERSECT",EDGE,{"derivedFrom":[makeQuery(id+"F1.opRevolve","SWEPT_FACE",FACE,{"disambiguationData":[OSD([sQuery(id+"F0.wireOp",EDGE,"E13")])]}),makeQuery(id+"F24.opLoft","SWEPT_FACE",FACE,{"disambiguationData":[OSD([sQuery(id+"F3.wireOp",EDGE,"E20.9.0"),sQuery(id+"F3.wireOp",EDGE,"E20.9.1"),sQuery(id+"F3.wireOp",EDGE,"E20.9.3"),sQuery(id+"F22.wireOp",EDGE,"E28.1.1"),sQuery(id+"F22.wireOp",EDGE,"E28.1.2"),sQuery(id+"F22.wireOp",EDGE,"E28.1.3")])]})]});
            var Q11;
            {var subQ0=sQuery(id+"F3.wireOp",EDGE,"E20.10.3");var subQ1=sQuery(id+"F3.wireOp",EDGE,"E20.10.1");var subQ2=sQuery(id+"F3.wireOp",EDGE,"E20.10.0");var subQ81=sQuery(id+"F3.wireOp",EDGE,"E18.bottom");Q11=makeQuery(id+"F25.boolean.opBoolean","INTERSECT",EDGE,{"derivedFrom":[makeQuery(id+"F24.boolean.opBoolean","SPLIT",FACE,{"disambiguationData":[TD([makeQuery(id+"F5.opLoft","CAP_FACE",FACE,{"disambiguationData":[OSD([makeQuery(id+"F3.imprint","IMPRINT",FACE,{"disambiguationData":[TD([[makeQuery(id+"F3.imprint","IMPRINT",EDGE,{"derivedFrom":subQ81}),1.0]])]})])],"isStart":true})])],"derivedFrom":makeQuery(id+"F1.opRevolve","SWEPT_FACE",FACE,{"disambiguationData":[OSD([sQuery(id+"F0.wireOp",EDGE,"E13")])]})}),makeQuery(id+"F25.opLoft","SWEPT_FACE",FACE,{"disambiguationData":[OSD([subQ2,subQ1,subQ0,sQuery(id+"F22.wireOp",EDGE,"E28.2.1"),sQuery(id+"F22.wireOp",EDGE,"E28.2.2"),sQuery(id+"F22.wireOp",EDGE,"E28.2.3")])]})]});}
            var Q12;
            {var subQ0=sQuery(id+"F3.wireOp",EDGE,"E20.11.3");var subQ1=sQuery(id+"F3.wireOp",EDGE,"E20.11.1");var subQ2=sQuery(id+"F3.wireOp",EDGE,"E20.11.0");var subQ74=sQuery(id+"F3.wireOp",EDGE,"E18.bottom");var subQ77=makeQuery(id+"F5.opLoft","CAP_FACE",FACE,{"disambiguationData":[OSD([makeQuery(id+"F3.imprint","IMPRINT",FACE,{"disambiguationData":[TD([[makeQuery(id+"F3.imprint","IMPRINT",EDGE,{"derivedFrom":subQ74}),1.0]])]})])],"isStart":true});Q12=makeQuery(id+"F26.boolean.opBoolean","INTERSECT",EDGE,{"derivedFrom":[makeQuery(id+"F25.boolean.opBoolean","SPLIT",FACE,{"disambiguationData":[TD([subQ77])],"derivedFrom":makeQuery(id+"F24.boolean.opBoolean","SPLIT",FACE,{"disambiguationData":[TD([subQ77])],"derivedFrom":makeQuery(id+"F1.opRevolve","SWEPT_FACE",FACE,{"disambiguationData":[OSD([sQuery(id+"F0.wireOp",EDGE,"E13")])]})})}),makeQuery(id+"F26.opLoft","SWEPT_FACE",FACE,{"disambiguationData":[OSD([subQ2,subQ1,subQ0,sQuery(id+"F22.wireOp",EDGE,"E28.3.1"),sQuery(id+"F22.wireOp",EDGE,"E28.3.2"),sQuery(id+"F22.wireOp",EDGE,"E28.3.3")])]})]});}
            var Q13;
            {var subQ0=sQuery(id+"F3.wireOp",EDGE,"E20.12.3");var subQ1=sQuery(id+"F3.wireOp",EDGE,"E20.12.1");var subQ2=sQuery(id+"F3.wireOp",EDGE,"E20.12.0");var subQ70=sQuery(id+"F3.wireOp",EDGE,"E18.bottom");var subQ73=makeQuery(id+"F5.opLoft","CAP_FACE",FACE,{"disambiguationData":[OSD([makeQuery(id+"F3.imprint","IMPRINT",FACE,{"disambiguationData":[TD([[makeQuery(id+"F3.imprint","IMPRINT",EDGE,{"derivedFrom":subQ70}),1.0]])]})])],"isStart":true});Q13=makeQuery(id+"F27.boolean.opBoolean","INTERSECT",EDGE,{"derivedFrom":[makeQuery(id+"F26.boolean.opBoolean","SPLIT",FACE,{"disambiguationData":[TD([subQ73])],"derivedFrom":makeQuery(id+"F25.boolean.opBoolean","SPLIT",FACE,{"disambiguationData":[TD([subQ73])],"derivedFrom":makeQuery(id+"F24.boolean.opBoolean","SPLIT",FACE,{"disambiguationData":[TD([subQ73])],"derivedFrom":makeQuery(id+"F1.opRevolve","SWEPT_FACE",FACE,{"disambiguationData":[OSD([sQuery(id+"F0.wireOp",EDGE,"E13")])]})})})}),makeQuery(id+"F27.opLoft","SWEPT_FACE",FACE,{"disambiguationData":[OSD([subQ2,subQ1,subQ0,sQuery(id+"F22.wireOp",EDGE,"E28.4.1"),sQuery(id+"F22.wireOp",EDGE,"E28.4.2"),sQuery(id+"F22.wireOp",EDGE,"E28.4.3")])]})]});}
            var Q14;
            {var subQ0=sQuery(id+"F3.wireOp",EDGE,"E20.13.3");var subQ1=sQuery(id+"F3.wireOp",EDGE,"E20.13.1");var subQ2=sQuery(id+"F3.wireOp",EDGE,"E20.13.0");var subQ52=sQuery(id+"F3.wireOp",EDGE,"E18.bottom");var subQ55=makeQuery(id+"F5.opLoft","CAP_FACE",FACE,{"disambiguationData":[OSD([makeQuery(id+"F3.imprint","IMPRINT",FACE,{"disambiguationData":[TD([[makeQuery(id+"F3.imprint","IMPRINT",EDGE,{"derivedFrom":subQ52}),1.0]])]})])],"isStart":true});Q14=makeQuery(id+"F28.boolean.opBoolean","INTERSECT",EDGE,{"derivedFrom":[makeQuery(id+"F27.boolean.opBoolean","SPLIT",FACE,{"disambiguationData":[TD([subQ55])],"derivedFrom":makeQuery(id+"F26.boolean.opBoolean","SPLIT",FACE,{"disambiguationData":[TD([subQ55])],"derivedFrom":makeQuery(id+"F25.boolean.opBoolean","SPLIT",FACE,{"disambiguationData":[TD([subQ55])],"derivedFrom":makeQuery(id+"F24.boolean.opBoolean","SPLIT",FACE,{"disambiguationData":[TD([subQ55])],"derivedFrom":makeQuery(id+"F1.opRevolve","SWEPT_FACE",FACE,{"disambiguationData":[OSD([sQuery(id+"F0.wireOp",EDGE,"E13")])]})})})})}),makeQuery(id+"F28.opLoft","SWEPT_FACE",FACE,{"disambiguationData":[OSD([subQ2,subQ1,subQ0,sQuery(id+"F22.wireOp",EDGE,"E28.5.1"),sQuery(id+"F22.wireOp",EDGE,"E28.5.2"),sQuery(id+"F22.wireOp",EDGE,"E28.5.3")])]})]});}
            var Q15;
            {var subQ0=sQuery(id+"F3.wireOp",EDGE,"E20.14.3");var subQ1=sQuery(id+"F3.wireOp",EDGE,"E20.14.1");var subQ2=sQuery(id+"F3.wireOp",EDGE,"E20.14.0");var subQ41=sQuery(id+"F3.wireOp",EDGE,"E18.bottom");var subQ44=makeQuery(id+"F5.opLoft","CAP_FACE",FACE,{"disambiguationData":[OSD([makeQuery(id+"F3.imprint","IMPRINT",FACE,{"disambiguationData":[TD([[makeQuery(id+"F3.imprint","IMPRINT",EDGE,{"derivedFrom":subQ41}),1.0]])]})])],"isStart":true});Q15=makeQuery(id+"F29.boolean.opBoolean","INTERSECT",EDGE,{"derivedFrom":[makeQuery(id+"F28.boolean.opBoolean","SPLIT",FACE,{"disambiguationData":[TD([subQ44])],"derivedFrom":makeQuery(id+"F27.boolean.opBoolean","SPLIT",FACE,{"disambiguationData":[TD([subQ44])],"derivedFrom":makeQuery(id+"F26.boolean.opBoolean","SPLIT",FACE,{"disambiguationData":[TD([subQ44])],"derivedFrom":makeQuery(id+"F25.boolean.opBoolean","SPLIT",FACE,{"disambiguationData":[TD([subQ44])],"derivedFrom":makeQuery(id+"F24.boolean.opBoolean","SPLIT",FACE,{"disambiguationData":[TD([subQ44])],"derivedFrom":makeQuery(id+"F1.opRevolve","SWEPT_FACE",FACE,{"disambiguationData":[OSD([sQuery(id+"F0.wireOp",EDGE,"E13")])]})})})})})}),makeQuery(id+"F29.opLoft","SWEPT_FACE",FACE,{"disambiguationData":[OSD([subQ2,subQ1,subQ0,sQuery(id+"F22.wireOp",EDGE,"E28.6.1"),sQuery(id+"F22.wireOp",EDGE,"E28.6.2"),sQuery(id+"F22.wireOp",EDGE,"E28.6.3")])]})]});}
            var Q16;
            {var subQ0=sQuery(id+"F3.wireOp",EDGE,"E20.15.3");var subQ1=sQuery(id+"F3.wireOp",EDGE,"E20.15.1");var subQ2=sQuery(id+"F3.wireOp",EDGE,"E20.15.0");var subQ34=sQuery(id+"F3.wireOp",EDGE,"E18.bottom");var subQ37=makeQuery(id+"F5.opLoft","CAP_FACE",FACE,{"disambiguationData":[OSD([makeQuery(id+"F3.imprint","IMPRINT",FACE,{"disambiguationData":[TD([[makeQuery(id+"F3.imprint","IMPRINT",EDGE,{"derivedFrom":subQ34}),1.0]])]})])],"isStart":true});Q16=makeQuery(id+"F30.boolean.opBoolean","INTERSECT",EDGE,{"derivedFrom":[makeQuery(id+"F29.boolean.opBoolean","SPLIT",FACE,{"disambiguationData":[TD([subQ37])],"derivedFrom":makeQuery(id+"F28.boolean.opBoolean","SPLIT",FACE,{"disambiguationData":[TD([subQ37])],"derivedFrom":makeQuery(id+"F27.boolean.opBoolean","SPLIT",FACE,{"disambiguationData":[TD([subQ37])],"derivedFrom":makeQuery(id+"F26.boolean.opBoolean","SPLIT",FACE,{"disambiguationData":[TD([subQ37])],"derivedFrom":makeQuery(id+"F25.boolean.opBoolean","SPLIT",FACE,{"disambiguationData":[TD([subQ37])],"derivedFrom":makeQuery(id+"F24.boolean.opBoolean","SPLIT",FACE,{"disambiguationData":[TD([subQ37])],"derivedFrom":makeQuery(id+"F1.opRevolve","SWEPT_FACE",FACE,{"disambiguationData":[OSD([sQuery(id+"F0.wireOp",EDGE,"E13")])]})})})})})})}),makeQuery(id+"F30.opLoft","SWEPT_FACE",FACE,{"disambiguationData":[OSD([subQ2,subQ1,subQ0,sQuery(id+"F22.wireOp",EDGE,"E28.7.1"),sQuery(id+"F22.wireOp",EDGE,"E28.7.2"),sQuery(id+"F22.wireOp",EDGE,"E28.7.3")])]})]});}
            var Q17;
            {var subQ0=sQuery(id+"F3.wireOp",EDGE,"E18.left");var subQ1=sQuery(id+"F3.wireOp",EDGE,"E18.top");var subQ2=sQuery(id+"F3.wireOp",EDGE,"E18.bottom");var subQ48=makeQuery(id+"F5.opLoft","CAP_FACE",FACE,{"disambiguationData":[OSD([makeQuery(id+"F3.imprint","IMPRINT",FACE,{"disambiguationData":[TD([[makeQuery(id+"F3.imprint","IMPRINT",EDGE,{"derivedFrom":subQ2}),1.0]])]})])],"isStart":true});Q17=makeQuery(id+"F31.boolean.opBoolean","INTERSECT",EDGE,{"derivedFrom":[makeQuery(id+"F30.boolean.opBoolean","SPLIT",FACE,{"disambiguationData":[TD([subQ48])],"derivedFrom":makeQuery(id+"F29.boolean.opBoolean","SPLIT",FACE,{"disambiguationData":[TD([subQ48])],"derivedFrom":makeQuery(id+"F28.boolean.opBoolean","SPLIT",FACE,{"disambiguationData":[TD([subQ48])],"derivedFrom":makeQuery(id+"F27.boolean.opBoolean","SPLIT",FACE,{"disambiguationData":[TD([subQ48])],"derivedFrom":makeQuery(id+"F26.boolean.opBoolean","SPLIT",FACE,{"disambiguationData":[TD([subQ48])],"derivedFrom":makeQuery(id+"F25.boolean.opBoolean","SPLIT",FACE,{"disambiguationData":[TD([subQ48])],"derivedFrom":makeQuery(id+"F24.boolean.opBoolean","SPLIT",FACE,{"disambiguationData":[TD([subQ48])],"derivedFrom":makeQuery(id+"F1.opRevolve","SWEPT_FACE",FACE,{"disambiguationData":[OSD([sQuery(id+"F0.wireOp",EDGE,"E13")])]})})})})})})})}),makeQuery(id+"F31.opLoft","SWEPT_FACE",FACE,{"disambiguationData":[OSD([subQ2,subQ1,subQ0,sQuery(id+"F22.wireOp",EDGE,"E28.8.1"),sQuery(id+"F22.wireOp",EDGE,"E28.8.2"),sQuery(id+"F22.wireOp",EDGE,"E28.8.3")])]})]});}
            var Q18;
            Q18=makeQuery(id+"F5.boolean.opBoolean","INTERSECT",EDGE,{"derivedFrom":[makeQuery(id+"F1.opRevolve","SWEPT_FACE",FACE,{"disambiguationData":[OSD([sQuery(id+"F0.wireOp",EDGE,"E13")])]}),makeQuery(id+"F5.opLoft","SWEPT_FACE",FACE,{"disambiguationData":[OSD([sQuery(id+"F3.wireOp",EDGE,"E18.bottom"),sQuery(id+"F3.wireOp",EDGE,"E18.top"),sQuery(id+"F3.wireOp",EDGE,"E18.left"),sQuery(id+"F4.wireOp",EDGE,"E21"),sQuery(id+"F4.wireOp",EDGE,"E22"),sQuery(id+"F4.wireOp",EDGE,"E23")])]})]});
            var Q19;
            Q19=makeQuery(id+"F6.boolean.opBoolean","INTERSECT",EDGE,{"derivedFrom":[makeQuery(id+"F1.opRevolve","SWEPT_FACE",FACE,{"disambiguationData":[OSD([sQuery(id+"F0.wireOp",EDGE,"E13")])]}),makeQuery(id+"F6.opLoft","SWEPT_FACE",FACE,{"disambiguationData":[OSD([sQuery(id+"F3.wireOp",EDGE,"E20.15.0"),sQuery(id+"F3.wireOp",EDGE,"E20.15.1"),sQuery(id+"F3.wireOp",EDGE,"E20.15.3"),sQuery(id+"F4.wireOp",EDGE,"E26.15.0"),sQuery(id+"F4.wireOp",EDGE,"E26.15.2"),sQuery(id+"F4.wireOp",EDGE,"E26.15.3")])]})]});
            var Q20;
            Q20=makeQuery(id+"F7.boolean.opBoolean","INTERSECT",EDGE,{"derivedFrom":[makeQuery(id+"F1.opRevolve","SWEPT_FACE",FACE,{"disambiguationData":[OSD([sQuery(id+"F0.wireOp",EDGE,"E13")])]}),makeQuery(id+"F7.opLoft","SWEPT_FACE",FACE,{"disambiguationData":[OSD([sQuery(id+"F3.wireOp",EDGE,"E20.14.0"),sQuery(id+"F3.wireOp",EDGE,"E20.14.1"),sQuery(id+"F3.wireOp",EDGE,"E20.14.3"),sQuery(id+"F4.wireOp",EDGE,"E26.14.0"),sQuery(id+"F4.wireOp",EDGE,"E26.14.2"),sQuery(id+"F4.wireOp",EDGE,"E26.14.3")])]})]});
            var Q21;
            Q21=makeQuery(id+"F8.boolean.opBoolean","INTERSECT",EDGE,{"derivedFrom":[makeQuery(id+"F1.opRevolve","SWEPT_FACE",FACE,{"disambiguationData":[OSD([sQuery(id+"F0.wireOp",EDGE,"E13")])]}),makeQuery(id+"F8.opLoft","SWEPT_FACE",FACE,{"disambiguationData":[OSD([sQuery(id+"F3.wireOp",EDGE,"E20.13.0"),sQuery(id+"F3.wireOp",EDGE,"E20.13.1"),sQuery(id+"F3.wireOp",EDGE,"E20.13.3"),sQuery(id+"F4.wireOp",EDGE,"E26.13.0"),sQuery(id+"F4.wireOp",EDGE,"E26.13.2"),sQuery(id+"F4.wireOp",EDGE,"E26.13.3")])]})]});
            var Q22;
            Q22=makeQuery(id+"F9.boolean.opBoolean","INTERSECT",EDGE,{"derivedFrom":[makeQuery(id+"F1.opRevolve","SWEPT_FACE",FACE,{"disambiguationData":[OSD([sQuery(id+"F0.wireOp",EDGE,"E13")])]}),makeQuery(id+"F9.opLoft","SWEPT_FACE",FACE,{"disambiguationData":[OSD([sQuery(id+"F3.wireOp",EDGE,"E20.12.0"),sQuery(id+"F3.wireOp",EDGE,"E20.12.1"),sQuery(id+"F3.wireOp",EDGE,"E20.12.3"),sQuery(id+"F4.wireOp",EDGE,"E26.12.0"),sQuery(id+"F4.wireOp",EDGE,"E26.12.2"),sQuery(id+"F4.wireOp",EDGE,"E26.12.3")])]})]});
            var Q23;
            Q23=makeQuery(id+"F10.boolean.opBoolean","INTERSECT",EDGE,{"derivedFrom":[makeQuery(id+"F1.opRevolve","SWEPT_FACE",FACE,{"disambiguationData":[OSD([sQuery(id+"F0.wireOp",EDGE,"E13")])]}),makeQuery(id+"F10.opLoft","SWEPT_FACE",FACE,{"disambiguationData":[OSD([sQuery(id+"F3.wireOp",EDGE,"E20.11.0"),sQuery(id+"F3.wireOp",EDGE,"E20.11.1"),sQuery(id+"F3.wireOp",EDGE,"E20.11.3"),sQuery(id+"F4.wireOp",EDGE,"E26.11.0"),sQuery(id+"F4.wireOp",EDGE,"E26.11.2"),sQuery(id+"F4.wireOp",EDGE,"E26.11.3")])]})]});
            var Q24;
            Q24=makeQuery(id+"F11.boolean.opBoolean","INTERSECT",EDGE,{"derivedFrom":[makeQuery(id+"F1.opRevolve","SWEPT_FACE",FACE,{"disambiguationData":[OSD([sQuery(id+"F0.wireOp",EDGE,"E13")])]}),makeQuery(id+"F11.opLoft","SWEPT_FACE",FACE,{"disambiguationData":[OSD([sQuery(id+"F3.wireOp",EDGE,"E20.10.0"),sQuery(id+"F3.wireOp",EDGE,"E20.10.1"),sQuery(id+"F3.wireOp",EDGE,"E20.10.3"),sQuery(id+"F4.wireOp",EDGE,"E26.10.0"),sQuery(id+"F4.wireOp",EDGE,"E26.10.2"),sQuery(id+"F4.wireOp",EDGE,"E26.10.3")])]})]});
            var Q25;
            Q25=makeQuery(id+"F12.boolean.opBoolean","INTERSECT",EDGE,{"derivedFrom":[makeQuery(id+"F1.opRevolve","SWEPT_FACE",FACE,{"disambiguationData":[OSD([sQuery(id+"F0.wireOp",EDGE,"E13")])]}),makeQuery(id+"F12.opLoft","SWEPT_FACE",FACE,{"disambiguationData":[OSD([sQuery(id+"F3.wireOp",EDGE,"E20.9.0"),sQuery(id+"F3.wireOp",EDGE,"E20.9.1"),sQuery(id+"F3.wireOp",EDGE,"E20.9.3"),sQuery(id+"F4.wireOp",EDGE,"E26.9.0"),sQuery(id+"F4.wireOp",EDGE,"E26.9.2"),sQuery(id+"F4.wireOp",EDGE,"E26.9.3")])]})]});
            var Q26;
            Q26=makeQuery(id+"F13.boolean.opBoolean","INTERSECT",EDGE,{"derivedFrom":[makeQuery(id+"F1.opRevolve","SWEPT_FACE",FACE,{"disambiguationData":[OSD([sQuery(id+"F0.wireOp",EDGE,"E13")])]}),makeQuery(id+"F13.opLoft","SWEPT_FACE",FACE,{"disambiguationData":[OSD([sQuery(id+"F3.wireOp",EDGE,"E20.8.0"),sQuery(id+"F3.wireOp",EDGE,"E20.8.1"),sQuery(id+"F3.wireOp",EDGE,"E20.8.3"),sQuery(id+"F4.wireOp",EDGE,"E26.8.0"),sQuery(id+"F4.wireOp",EDGE,"E26.8.2"),sQuery(id+"F4.wireOp",EDGE,"E26.8.3")])]})]});
            var Q27;
            Q27=makeQuery(id+"F14.boolean.opBoolean","INTERSECT",EDGE,{"derivedFrom":[makeQuery(id+"F1.opRevolve","SWEPT_FACE",FACE,{"disambiguationData":[OSD([sQuery(id+"F0.wireOp",EDGE,"E13")])]}),makeQuery(id+"F14.opLoft","SWEPT_FACE",FACE,{"disambiguationData":[OSD([sQuery(id+"F3.wireOp",EDGE,"E20.7.0"),sQuery(id+"F3.wireOp",EDGE,"E20.7.1"),sQuery(id+"F3.wireOp",EDGE,"E20.7.3"),sQuery(id+"F4.wireOp",EDGE,"E26.7.0"),sQuery(id+"F4.wireOp",EDGE,"E26.7.2"),sQuery(id+"F4.wireOp",EDGE,"E26.7.3")])]})]});
            var Q28;
            Q28=makeQuery(id+"F15.boolean.opBoolean","INTERSECT",EDGE,{"derivedFrom":[makeQuery(id+"F1.opRevolve","SWEPT_FACE",FACE,{"disambiguationData":[OSD([sQuery(id+"F0.wireOp",EDGE,"E13")])]}),makeQuery(id+"F15.opLoft","SWEPT_FACE",FACE,{"disambiguationData":[OSD([sQuery(id+"F3.wireOp",EDGE,"E20.6.0"),sQuery(id+"F3.wireOp",EDGE,"E20.6.1"),sQuery(id+"F3.wireOp",EDGE,"E20.6.3"),sQuery(id+"F4.wireOp",EDGE,"E26.6.0"),sQuery(id+"F4.wireOp",EDGE,"E26.6.2"),sQuery(id+"F4.wireOp",EDGE,"E26.6.3")])]})]});
            var Q29;
            Q29=makeQuery(id+"F16.boolean.opBoolean","INTERSECT",EDGE,{"derivedFrom":[makeQuery(id+"F1.opRevolve","SWEPT_FACE",FACE,{"disambiguationData":[OSD([sQuery(id+"F0.wireOp",EDGE,"E13")])]}),makeQuery(id+"F16.opLoft","SWEPT_FACE",FACE,{"disambiguationData":[OSD([sQuery(id+"F3.wireOp",EDGE,"E20.5.0"),sQuery(id+"F3.wireOp",EDGE,"E20.5.1"),sQuery(id+"F3.wireOp",EDGE,"E20.5.3"),sQuery(id+"F4.wireOp",EDGE,"E26.5.0"),sQuery(id+"F4.wireOp",EDGE,"E26.5.2"),sQuery(id+"F4.wireOp",EDGE,"E26.5.3")])]})]});
            var Q30;
            Q30=makeQuery(id+"F17.boolean.opBoolean","INTERSECT",EDGE,{"derivedFrom":[makeQuery(id+"F1.opRevolve","SWEPT_FACE",FACE,{"disambiguationData":[OSD([sQuery(id+"F0.wireOp",EDGE,"E13")])]}),makeQuery(id+"F17.opLoft","SWEPT_FACE",FACE,{"disambiguationData":[OSD([sQuery(id+"F3.wireOp",EDGE,"E20.4.0"),sQuery(id+"F3.wireOp",EDGE,"E20.4.1"),sQuery(id+"F3.wireOp",EDGE,"E20.4.3"),sQuery(id+"F4.wireOp",EDGE,"E26.4.0"),sQuery(id+"F4.wireOp",EDGE,"E26.4.2"),sQuery(id+"F4.wireOp",EDGE,"E26.4.3")])]})]});
            var Q31;
            Q31=makeQuery(id+"F18.boolean.opBoolean","INTERSECT",EDGE,{"derivedFrom":[makeQuery(id+"F1.opRevolve","SWEPT_FACE",FACE,{"disambiguationData":[OSD([sQuery(id+"F0.wireOp",EDGE,"E13")])]}),makeQuery(id+"F18.opLoft","SWEPT_FACE",FACE,{"disambiguationData":[OSD([sQuery(id+"F3.wireOp",EDGE,"E20.3.0"),sQuery(id+"F3.wireOp",EDGE,"E20.3.1"),sQuery(id+"F3.wireOp",EDGE,"E20.3.3"),sQuery(id+"F4.wireOp",EDGE,"E26.3.0"),sQuery(id+"F4.wireOp",EDGE,"E26.3.2"),sQuery(id+"F4.wireOp",EDGE,"E26.3.3")])]})]});
            fillet(context, id + "F46", {"entities" : qUnion([Q0, Q1, Q2, Q3, Q4, Q5, Q6, Q7, Q8, Q9, Q10, Q11, Q12, Q13, Q14, Q15, Q16, Q17, Q18, Q19, Q20, Q21, Q22, Q23, Q24, Q25, Q26, Q27, Q28, Q29, Q30, Q31]), "radius" : 1.5 * mm, "tangentPropagation" : true, "allowEdgeOverflow" : false});
        }
        {
            var Q0;
            Q0=makeQuery(id+"F1.opRevolve","SWEPT_EDGE",EDGE,{"disambiguationData":[OSD([sQuery(id+"F0.wireOp",EDGE,"E0"),sQuery(id+"F0.wireOp",EDGE,"E14")])]});
            var Q1;
            Q1=makeQuery(id+"F1.opRevolve","SWEPT_EDGE",EDGE,{"disambiguationData":[OSD([sQuery(id+"F0.wireOp",EDGE,"E7"),sQuery(id+"F0.wireOp",EDGE,"E15")])]});
            chamfer(context, id + "F47", {"entities" : qUnion([Q0, Q1]), "width" : 1 * mm, "tangentPropagation" : true});
        }
    });
